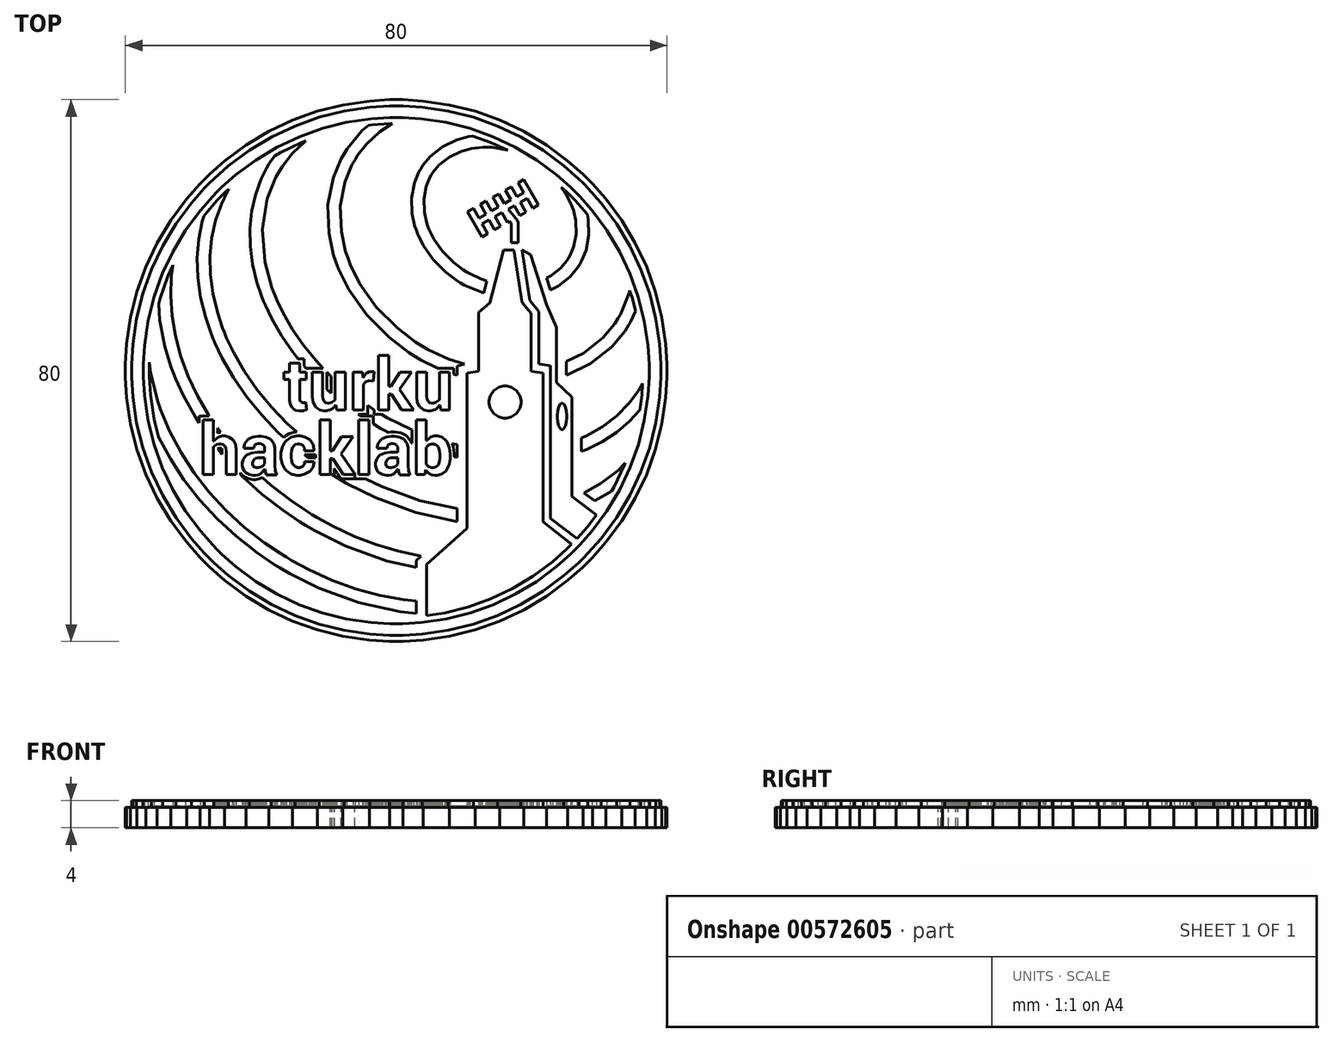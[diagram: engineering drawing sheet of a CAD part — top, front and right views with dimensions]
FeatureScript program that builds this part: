
annotation { "Feature Type Name" : "Feature", "Feature Type Description" : "" }
export const myFeature = defineFeature(function(context is Context, id is Id, definition is map)
    precondition{}
    {
        {
            var Q0;
            Q0=qCreatedBy(makeId("Top.planeOp"),FACE);
            var sketch = newSketch(context, id + "F0", { "sketchPlane" : qUnion([Q0])});
            skLineSegment(sketch, "E0", {"start": v(-12.45, -21.24) * mm, "end": v(-11.69, -21.7) * mm});
            skLineSegment(sketch, "E1", {"start": v(-11.69, -21.7) * mm, "end": v(-9.32, -22.98) * mm});
            skLineSegment(sketch, "E2", {"start": v(-9.32, -22.98) * mm, "end": v(-6.15, -24.46) * mm});
            skLineSegment(sketch, "E3", {"start": v(-6.15, -24.46) * mm, "end": v(-2.94, -25.69) * mm});
            skLineSegment(sketch, "E4", {"start": v(-2.94, -25.69) * mm, "end": v(0.28, -26.66) * mm});
            skLineSegment(sketch, "E5", {"start": v(0.28, -26.66) * mm, "end": v(3.5, -27.37) * mm});
            skLineSegment(sketch, "E6", {"start": v(3.5, -27.37) * mm, "end": v(6.7, -27.84) * mm});
            skLineSegment(sketch, "E7", {"start": v(6.7, -27.84) * mm, "end": v(9.84, -28.05) * mm});
            skLineSegment(sketch, "E8", {"start": v(9.84, -28.05) * mm, "end": v(12.93, -28.02) * mm});
            skLineSegment(sketch, "E9", {"start": v(12.93, -28.02) * mm, "end": v(15.94, -27.74) * mm});
            skLineSegment(sketch, "E10", {"start": v(15.94, -27.74) * mm, "end": v(18.85, -27.22) * mm});
            skLineSegment(sketch, "E11", {"start": v(18.85, -27.22) * mm, "end": v(21.64, -26.46) * mm});
            skLineSegment(sketch, "E12", {"start": v(21.64, -26.46) * mm, "end": v(24.3, -25.46) * mm});
            skLineSegment(sketch, "E13", {"start": v(24.3, -25.46) * mm, "end": v(26.8, -24.22) * mm});
            skLineSegment(sketch, "E14", {"start": v(26.8, -24.22) * mm, "end": v(29.13, -22.75) * mm});
            skLineSegment(sketch, "E15", {"start": v(29.13, -22.75) * mm, "end": v(31.27, -21.05) * mm});
            skLineSegment(sketch, "E16", {"start": v(31.27, -21.05) * mm, "end": v(32.74, -19.62) * mm});
            skLineSegment(sketch, "E17", {"start": v(32.74, -19.62) * mm, "end": v(33.2, -19.11) * mm});
            skLineSegment(sketch, "E18", {"start": v(33.2, -19.11) * mm, "end": v(33.4, -18.77) * mm});
            skLineSegment(sketch, "E19", {"start": v(33.4, -18.77) * mm, "end": v(35.17, -15.19) * mm});
            skLineSegment(sketch, "E20", {"start": v(35.17, -15.19) * mm, "end": v(35.32, -14.82) * mm});
            skLineSegment(sketch, "E21", {"start": v(35.32, -14.82) * mm, "end": v(34.55, -15.63) * mm});
            skLineSegment(sketch, "E22", {"start": v(34.55, -15.63) * mm, "end": v(31.91, -17.75) * mm});
            skLineSegment(sketch, "E23", {"start": v(31.91, -17.75) * mm, "end": v(27.89, -20.04) * mm});
            skLineSegment(sketch, "E24", {"start": v(27.89, -20.04) * mm, "end": v(23.32, -21.64) * mm});
            skLineSegment(sketch, "E25", {"start": v(23.32, -21.64) * mm, "end": v(19.53, -22.4) * mm});
            skLineSegment(sketch, "E26", {"start": v(19.53, -22.4) * mm, "end": v(18.25, -22.53) * mm});
            skLineSegment(sketch, "E27", {"start": v(18.25, -22.53) * mm, "end": v(17.96, -22.56) * mm});
            skLineSegment(sketch, "E28", {"start": v(17.96, -22.56) * mm, "end": v(15.49, -22.7) * mm});
            skLineSegment(sketch, "E29", {"start": v(15.49, -22.7) * mm, "end": v(14.67, -22.7) * mm});
            skLineSegment(sketch, "E30", {"start": v(14.67, -22.7) * mm, "end": v(13.2, -22.7) * mm});
            skLineSegment(sketch, "E31", {"start": v(13.2, -22.7) * mm, "end": v(8.78, -22.26) * mm});
            skLineSegment(sketch, "E32", {"start": v(8.78, -22.26) * mm, "end": v(2.85, -20.95) * mm});
            skLineSegment(sketch, "E33", {"start": v(2.85, -20.95) * mm, "end": v(-3, -18.8) * mm});
            skLineSegment(sketch, "E34", {"start": v(-3, -18.8) * mm, "end": v(-7.31, -16.66) * mm});
            skLineSegment(sketch, "E35", {"start": v(-7.31, -16.66) * mm, "end": v(-8.68, -15.84) * mm});
            skLineSegment(sketch, "E36", {"start": v(-8.68, -15.84) * mm, "end": v(-9.48, -15.36) * mm});
            skLineSegment(sketch, "E37", {"start": v(-9.48, -15.36) * mm, "end": v(-11.8, -13.8) * mm});
            skLineSegment(sketch, "E38", {"start": v(-11.8, -13.8) * mm, "end": v(-14.7, -11.57) * mm});
            skLineSegment(sketch, "E39", {"start": v(-14.7, -11.57) * mm, "end": v(-17.4, -9.16) * mm});
            skLineSegment(sketch, "E40", {"start": v(-17.4, -9.16) * mm, "end": v(-19.85, -6.6) * mm});
            skLineSegment(sketch, "E41", {"start": v(-19.85, -6.6) * mm, "end": v(-22.07, -3.9) * mm});
            skLineSegment(sketch, "E42", {"start": v(-22.07, -3.9) * mm, "end": v(-24.03, -1.07) * mm});
            skLineSegment(sketch, "E43", {"start": v(-24.03, -1.07) * mm, "end": v(-25.7, 1.88) * mm});
            skLineSegment(sketch, "E44", {"start": v(-25.7, 1.88) * mm, "end": v(-26.79, 4.14) * mm});
            skLineSegment(sketch, "E45", {"start": v(-26.79, 4.14) * mm, "end": v(-27.1, 4.9) * mm});
            skLineSegment(sketch, "E46", {"start": v(-27.1, 4.9) * mm, "end": v(-27.4, 5.64) * mm});
            skLineSegment(sketch, "E47", {"start": v(-27.4, 5.64) * mm, "end": v(-28.16, 7.9) * mm});
            skLineSegment(sketch, "E48", {"start": v(-28.16, 7.9) * mm, "end": v(-28.9, 10.84) * mm});
            skLineSegment(sketch, "E49", {"start": v(-28.9, 10.84) * mm, "end": v(-29.3, 13.75) * mm});
            skLineSegment(sketch, "E50", {"start": v(-29.3, 13.75) * mm, "end": v(-29.4, 16.6) * mm});
            skLineSegment(sketch, "E51", {"start": v(-29.4, 16.6) * mm, "end": v(-29.2, 19.38) * mm});
            skLineSegment(sketch, "E52", {"start": v(-29.2, 19.38) * mm, "end": v(-28.66, 22.06) * mm});
            skLineSegment(sketch, "E53", {"start": v(-28.66, 22.06) * mm, "end": v(-27.82, 24.64) * mm});
            skLineSegment(sketch, "E54", {"start": v(-27.82, 24.64) * mm, "end": v(-26.98, 26.5) * mm});
            skLineSegment(sketch, "E55", {"start": v(-26.98, 26.5) * mm, "end": v(-26.66, 27.1) * mm});
            skLineSegment(sketch, "E56", {"start": v(-26.66, 27.1) * mm, "end": v(-27.05, 26.72) * mm});
            skLineSegment(sketch, "E57", {"start": v(-27.05, 26.72) * mm, "end": v(-28.88, 24.72) * mm});
            skLineSegment(sketch, "E58", {"start": v(-28.88, 24.72) * mm, "end": v(-30.57, 22.6) * mm});
            skLineSegment(sketch, "E59", {"start": v(-30.57, 22.6) * mm, "end": v(-30.89, 22.16) * mm});
            skLineSegment(sketch, "E60", {"start": v(-30.89, 22.16) * mm, "end": v(-31.2, 21.52) * mm});
            skLineSegment(sketch, "E61", {"start": v(-31.2, 21.52) * mm, "end": v(-32, 19.5) * mm});
            skLineSegment(sketch, "E62", {"start": v(-32, 19.5) * mm, "end": v(-32.76, 16.75) * mm});
            skLineSegment(sketch, "E63", {"start": v(-32.76, 16.75) * mm, "end": v(-33.2, 13.9) * mm});
            skLineSegment(sketch, "E64", {"start": v(-33.2, 13.9) * mm, "end": v(-33.32, 11) * mm});
            skLineSegment(sketch, "E65", {"start": v(-33.32, 11) * mm, "end": v(-33.12, 8.06) * mm});
            skLineSegment(sketch, "E66", {"start": v(-33.12, 8.06) * mm, "end": v(-32.61, 5.1) * mm});
            skLineSegment(sketch, "E67", {"start": v(-32.61, 5.1) * mm, "end": v(-31.81, 2.14) * mm});
            skLineSegment(sketch, "E68", {"start": v(-31.81, 2.14) * mm, "end": v(-30.72, -0.8) * mm});
            skLineSegment(sketch, "E69", {"start": v(-30.72, -0.8) * mm, "end": v(-29.34, -3.71) * mm});
            skLineSegment(sketch, "E70", {"start": v(-29.34, -3.71) * mm, "end": v(-27.7, -6.56) * mm});
            skLineSegment(sketch, "E71", {"start": v(-27.7, -6.56) * mm, "end": v(-25.78, -9.32) * mm});
            skLineSegment(sketch, "E72", {"start": v(-25.78, -9.32) * mm, "end": v(-23.6, -11.99) * mm});
            skLineSegment(sketch, "E73", {"start": v(-23.6, -11.99) * mm, "end": v(-21.17, -14.53) * mm});
            skLineSegment(sketch, "E74", {"start": v(-21.17, -14.53) * mm, "end": v(-18.5, -16.93) * mm});
            skLineSegment(sketch, "E75", {"start": v(-18.5, -16.93) * mm, "end": v(-15.59, -19.18) * mm});
            skLineSegment(sketch, "E76", {"start": v(-15.59, -19.18) * mm, "end": v(-13.25, -20.75) * mm});
            skLineSegment(sketch, "E77", {"start": v(-13.25, -20.75) * mm, "end": v(-12.45, -21.24) * mm});
            skLineSegment(sketch, "E78", {"start": v(-24.6, 26.95) * mm, "end": v(-24.95, 26.39) * mm});
            skLineSegment(sketch, "E79", {"start": v(-24.95, 26.39) * mm, "end": v(-25.81, 24.62) * mm});
            skLineSegment(sketch, "E80", {"start": v(-25.81, 24.62) * mm, "end": v(-26.7, 22.17) * mm});
            skLineSegment(sketch, "E81", {"start": v(-26.7, 22.17) * mm, "end": v(-27.28, 19.6) * mm});
            skLineSegment(sketch, "E82", {"start": v(-27.28, 19.6) * mm, "end": v(-27.53, 16.93) * mm});
            skLineSegment(sketch, "E83", {"start": v(-27.53, 16.93) * mm, "end": v(-27.47, 14.18) * mm});
            skLineSegment(sketch, "E84", {"start": v(-27.47, 14.18) * mm, "end": v(-27.1, 11.37) * mm});
            skLineSegment(sketch, "E85", {"start": v(-27.1, 11.37) * mm, "end": v(-26.4, 8.51) * mm});
            skLineSegment(sketch, "E86", {"start": v(-26.4, 8.51) * mm, "end": v(-25.67, 6.33) * mm});
            skLineSegment(sketch, "E87", {"start": v(-25.67, 6.33) * mm, "end": v(-25.38, 5.62) * mm});
            skLineSegment(sketch, "E88", {"start": v(-25.38, 5.62) * mm, "end": v(-25.08, 4.88) * mm});
            skLineSegment(sketch, "E89", {"start": v(-25.08, 4.88) * mm, "end": v(-24.05, 2.72) * mm});
            skLineSegment(sketch, "E90", {"start": v(-24.05, 2.72) * mm, "end": v(-22.44, -0.1) * mm});
            skLineSegment(sketch, "E91", {"start": v(-22.44, -0.1) * mm, "end": v(-20.56, -2.8) * mm});
            skLineSegment(sketch, "E92", {"start": v(-20.56, -2.8) * mm, "end": v(-18.44, -5.39) * mm});
            skLineSegment(sketch, "E93", {"start": v(-18.44, -5.39) * mm, "end": v(-16.08, -7.85) * mm});
            skLineSegment(sketch, "E94", {"start": v(-16.08, -7.85) * mm, "end": v(-13.5, -10.15) * mm});
            skLineSegment(sketch, "E95", {"start": v(-13.5, -10.15) * mm, "end": v(-10.7, -12.3) * mm});
            skLineSegment(sketch, "E96", {"start": v(-10.7, -12.3) * mm, "end": v(-8.47, -13.79) * mm});
            skLineSegment(sketch, "E97", {"start": v(-8.47, -13.79) * mm, "end": v(-7.71, -14.25) * mm});
            skLineSegment(sketch, "E98", {"start": v(-7.71, -14.25) * mm, "end": v(-6.37, -15.06) * mm});
            skLineSegment(sketch, "E99", {"start": v(-6.37, -15.06) * mm, "end": v(-2.13, -17.15) * mm});
            skLineSegment(sketch, "E100", {"start": v(-2.13, -17.15) * mm, "end": v(3.55, -19.2) * mm});
            skLineSegment(sketch, "E101", {"start": v(3.55, -19.2) * mm, "end": v(9.2, -20.43) * mm});
            skLineSegment(sketch, "E102", {"start": v(9.2, -20.43) * mm, "end": v(13.35, -20.84) * mm});
            skLineSegment(sketch, "E103", {"start": v(13.35, -20.84) * mm, "end": v(14.73, -20.84) * mm});
            skLineSegment(sketch, "E104", {"start": v(14.73, -20.84) * mm, "end": v(15.6, -20.84) * mm});
            skLineSegment(sketch, "E105", {"start": v(15.6, -20.84) * mm, "end": v(18.19, -20.67) * mm});
            skLineSegment(sketch, "E106", {"start": v(18.19, -20.67) * mm, "end": v(21.5, -20.16) * mm});
            skLineSegment(sketch, "E107", {"start": v(21.5, -20.16) * mm, "end": v(24.66, -19.3) * mm});
            skLineSegment(sketch, "E108", {"start": v(24.66, -19.3) * mm, "end": v(27.6, -18.12) * mm});
            skLineSegment(sketch, "E109", {"start": v(27.6, -18.12) * mm, "end": v(30.3, -16.6) * mm});
            skLineSegment(sketch, "E110", {"start": v(30.3, -16.6) * mm, "end": v(32.72, -14.76) * mm});
            skLineSegment(sketch, "E111", {"start": v(32.72, -14.76) * mm, "end": v(34.84, -12.59) * mm});
            skLineSegment(sketch, "E112", {"start": v(34.84, -12.59) * mm, "end": v(36.23, -10.75) * mm});
            skLineSegment(sketch, "E113", {"start": v(36.23, -10.75) * mm, "end": v(36.63, -10.1) * mm});
            skLineSegment(sketch, "E114", {"start": v(36.63, -10.1) * mm, "end": v(36.68, -10.01) * mm});
            skLineSegment(sketch, "E115", {"start": v(36.68, -10.01) * mm, "end": v(37.17, -9.14) * mm});
            skLineSegment(sketch, "E116", {"start": v(37.17, -9.14) * mm, "end": v(37.21, -9.05) * mm});
            skLineSegment(sketch, "E117", {"start": v(37.21, -9.05) * mm, "end": v(37.34, -8.51) * mm});
            skLineSegment(sketch, "E118", {"start": v(37.34, -8.51) * mm, "end": v(37.85, -5.78) * mm});
            skLineSegment(sketch, "E119", {"start": v(37.85, -5.78) * mm, "end": v(38.16, -2.99) * mm});
            skLineSegment(sketch, "E120", {"start": v(38.16, -2.99) * mm, "end": v(38.2, -2.42) * mm});
            skLineSegment(sketch, "E121", {"start": v(38.2, -2.42) * mm, "end": v(38.15, -2.52) * mm});
            skLineSegment(sketch, "E122", {"start": v(38.15, -2.52) * mm, "end": v(37.6, -3.52) * mm});
            skLineSegment(sketch, "E123", {"start": v(37.6, -3.52) * mm, "end": v(37.54, -3.62) * mm});
            skLineSegment(sketch, "E124", {"start": v(37.54, -3.62) * mm, "end": v(37.22, -4.15) * mm});
            skLineSegment(sketch, "E125", {"start": v(37.22, -4.15) * mm, "end": v(36.11, -5.66) * mm});
            skLineSegment(sketch, "E126", {"start": v(36.11, -5.66) * mm, "end": v(34.44, -7.5) * mm});
            skLineSegment(sketch, "E127", {"start": v(34.44, -7.5) * mm, "end": v(32.55, -9.11) * mm});
            skLineSegment(sketch, "E128", {"start": v(32.55, -9.11) * mm, "end": v(30.43, -10.5) * mm});
            skLineSegment(sketch, "E129", {"start": v(30.43, -10.5) * mm, "end": v(28.11, -11.66) * mm});
            skLineSegment(sketch, "E130", {"start": v(28.11, -11.66) * mm, "end": v(25.6, -12.58) * mm});
            skLineSegment(sketch, "E131", {"start": v(25.6, -12.58) * mm, "end": v(22.92, -13.25) * mm});
            skLineSegment(sketch, "E132", {"start": v(22.92, -13.25) * mm, "end": v(20.78, -13.6) * mm});
            skLineSegment(sketch, "E133", {"start": v(20.78, -13.6) * mm, "end": v(20.07, -13.67) * mm});
            skLineSegment(sketch, "E134", {"start": v(20.07, -13.67) * mm, "end": v(19.81, -13.7) * mm});
            skLineSegment(sketch, "E135", {"start": v(19.81, -13.7) * mm, "end": v(17.65, -13.82) * mm});
            skLineSegment(sketch, "E136", {"start": v(17.65, -13.82) * mm, "end": v(16.93, -13.82) * mm});
            skLineSegment(sketch, "E137", {"start": v(16.93, -13.82) * mm, "end": v(15.64, -13.82) * mm});
            skLineSegment(sketch, "E138", {"start": v(15.64, -13.82) * mm, "end": v(11.78, -13.43) * mm});
            skLineSegment(sketch, "E139", {"start": v(11.78, -13.43) * mm, "end": v(6.6, -12.3) * mm});
            skLineSegment(sketch, "E140", {"start": v(6.6, -12.3) * mm, "end": v(1.47, -10.41) * mm});
            skLineSegment(sketch, "E141", {"start": v(1.47, -10.41) * mm, "end": v(-2.3, -8.54) * mm});
            skLineSegment(sketch, "E142", {"start": v(-2.3, -8.54) * mm, "end": v(-3.5, -7.82) * mm});
            skLineSegment(sketch, "E143", {"start": v(-3.5, -7.82) * mm, "end": v(-4.19, -7.4) * mm});
            skLineSegment(sketch, "E144", {"start": v(-4.19, -7.4) * mm, "end": v(-6.21, -6.03) * mm});
            skLineSegment(sketch, "E145", {"start": v(-6.21, -6.03) * mm, "end": v(-8.76, -4.08) * mm});
            skLineSegment(sketch, "E146", {"start": v(-8.76, -4.08) * mm, "end": v(-11.11, -1.98) * mm});
            skLineSegment(sketch, "E147", {"start": v(-11.11, -1.98) * mm, "end": v(-13.27, 0.26) * mm});
            skLineSegment(sketch, "E148", {"start": v(-13.27, 0.26) * mm, "end": v(-15.2, 2.63) * mm});
            skLineSegment(sketch, "E149", {"start": v(-15.2, 2.63) * mm, "end": v(-16.92, 5.1) * mm});
            skLineSegment(sketch, "E150", {"start": v(-16.92, 5.1) * mm, "end": v(-18.39, 7.67) * mm});
            skLineSegment(sketch, "E151", {"start": v(-18.39, 7.67) * mm, "end": v(-19.33, 9.65) * mm});
            skLineSegment(sketch, "E152", {"start": v(-19.33, 9.65) * mm, "end": v(-19.6, 10.33) * mm});
            skLineSegment(sketch, "E153", {"start": v(-19.6, 10.33) * mm, "end": v(-19.88, 11) * mm});
            skLineSegment(sketch, "E154", {"start": v(-19.88, 11) * mm, "end": v(-20.56, 13.04) * mm});
            skLineSegment(sketch, "E155", {"start": v(-20.56, 13.04) * mm, "end": v(-21.2, 15.74) * mm});
            skLineSegment(sketch, "E156", {"start": v(-21.2, 15.74) * mm, "end": v(-21.56, 18.38) * mm});
            skLineSegment(sketch, "E157", {"start": v(-21.56, 18.38) * mm, "end": v(-21.6, 20.98) * mm});
            skLineSegment(sketch, "E158", {"start": v(-21.6, 20.98) * mm, "end": v(-21.36, 23.5) * mm});
            skLineSegment(sketch, "E159", {"start": v(-21.36, 23.5) * mm, "end": v(-20.8, 25.93) * mm});
            skLineSegment(sketch, "E160", {"start": v(-20.8, 25.93) * mm, "end": v(-19.96, 28.26) * mm});
            skLineSegment(sketch, "E161", {"start": v(-19.96, 28.26) * mm, "end": v(-19.13, 29.94) * mm});
            skLineSegment(sketch, "E162", {"start": v(-19.13, 29.94) * mm, "end": v(-18.8, 30.47) * mm});
            skLineSegment(sketch, "E163", {"start": v(-18.8, 30.47) * mm, "end": v(-18.55, 30.9) * mm});
            skLineSegment(sketch, "E164", {"start": v(-18.55, 30.9) * mm, "end": v(-17.1, 32.85) * mm});
            skLineSegment(sketch, "E165", {"start": v(-17.1, 32.85) * mm, "end": v(-15.43, 34.61) * mm});
            skLineSegment(sketch, "E166", {"start": v(-15.43, 34.61) * mm, "end": v(-15.07, 34.94) * mm});
            skLineSegment(sketch, "E167", {"start": v(-15.07, 34.94) * mm, "end": v(-15.42, 34.78) * mm});
            skLineSegment(sketch, "E168", {"start": v(-15.42, 34.78) * mm, "end": v(-18.86, 33.04) * mm});
            skLineSegment(sketch, "E169", {"start": v(-18.86, 33.04) * mm, "end": v(-19.2, 32.84) * mm});
            skLineSegment(sketch, "E170", {"start": v(-19.2, 32.84) * mm, "end": v(-19.74, 32.44) * mm});
            skLineSegment(sketch, "E171", {"start": v(-19.74, 32.44) * mm, "end": v(-22.2, 30.16) * mm});
            skLineSegment(sketch, "E172", {"start": v(-22.2, 30.16) * mm, "end": v(-24.26, 27.53) * mm});
            skLineSegment(sketch, "E173", {"start": v(-24.26, 27.53) * mm, "end": v(-24.6, 26.95) * mm});
            skLineSegment(sketch, "E174", {"start": v(-6.06, 31.17) * mm, "end": v(-6.53, 30.4) * mm});
            skLineSegment(sketch, "E175", {"start": v(-6.53, 30.4) * mm, "end": v(-7.56, 27.86) * mm});
            skLineSegment(sketch, "E176", {"start": v(-7.56, 27.86) * mm, "end": v(-8.24, 24.29) * mm});
            skLineSegment(sketch, "E177", {"start": v(-8.24, 24.29) * mm, "end": v(-8.11, 20.53) * mm});
            skLineSegment(sketch, "E178", {"start": v(-8.11, 20.53) * mm, "end": v(-7.49, 17.6) * mm});
            skLineSegment(sketch, "E179", {"start": v(-7.49, 17.6) * mm, "end": v(-7.16, 16.67) * mm});
            skLineSegment(sketch, "E180", {"start": v(-7.16, 16.67) * mm, "end": v(-6.81, 15.69) * mm});
            skLineSegment(sketch, "E181", {"start": v(-6.81, 15.69) * mm, "end": v(-5.4, 12.87) * mm});
            skLineSegment(sketch, "E182", {"start": v(-5.4, 12.87) * mm, "end": v(-2.94, 9.39) * mm});
            skLineSegment(sketch, "E183", {"start": v(-2.94, 9.39) * mm, "end": v(0.15, 6.3) * mm});
            skLineSegment(sketch, "E184", {"start": v(0.15, 6.3) * mm, "end": v(2.84, 4.24) * mm});
            skLineSegment(sketch, "E185", {"start": v(2.84, 4.24) * mm, "end": v(3.8, 3.66) * mm});
            skLineSegment(sketch, "E186", {"start": v(3.8, 3.66) * mm, "end": v(4.76, 3.08) * mm});
            skLineSegment(sketch, "E187", {"start": v(4.76, 3.08) * mm, "end": v(7.82, 1.65) * mm});
            skLineSegment(sketch, "E188", {"start": v(7.82, 1.65) * mm, "end": v(12, 0.35) * mm});
            skLineSegment(sketch, "E189", {"start": v(12, 0.35) * mm, "end": v(16.23, -0.2) * mm});
            skLineSegment(sketch, "E190", {"start": v(16.23, -0.2) * mm, "end": v(19.38, -0.15) * mm});
            skLineSegment(sketch, "E191", {"start": v(19.38, -0.15) * mm, "end": v(20.4, 0) * mm});
            skLineSegment(sketch, "E192", {"start": v(20.4, 0) * mm, "end": v(21.39, 0.14) * mm});
            skLineSegment(sketch, "E193", {"start": v(21.39, 0.14) * mm, "end": v(24.27, 0.94) * mm});
            skLineSegment(sketch, "E194", {"start": v(24.27, 0.94) * mm, "end": v(27.66, 2.57) * mm});
            skLineSegment(sketch, "E195", {"start": v(27.66, 2.57) * mm, "end": v(30.51, 4.84) * mm});
            skLineSegment(sketch, "E196", {"start": v(30.51, 4.84) * mm, "end": v(32.28, 6.93) * mm});
            skLineSegment(sketch, "E197", {"start": v(32.28, 6.93) * mm, "end": v(32.75, 7.7) * mm});
            skLineSegment(sketch, "E198", {"start": v(32.75, 7.7) * mm, "end": v(33.11, 8.3) * mm});
            skLineSegment(sketch, "E199", {"start": v(33.11, 8.3) * mm, "end": v(34.38, 11.48) * mm});
            skLineSegment(sketch, "E200", {"start": v(34.38, 11.48) * mm, "end": v(34.95, 14.83) * mm});
            skLineSegment(sketch, "E201", {"start": v(34.95, 14.83) * mm, "end": v(34.97, 15.51) * mm});
            skLineSegment(sketch, "E202", {"start": v(34.97, 15.51) * mm, "end": v(34.58, 16.38) * mm});
            skLineSegment(sketch, "E203", {"start": v(34.58, 16.38) * mm, "end": v(33.25, 18.88) * mm});
            skLineSegment(sketch, "E204", {"start": v(33.25, 18.88) * mm, "end": v(31.22, 22.04) * mm});
            skLineSegment(sketch, "E205", {"start": v(31.22, 22.04) * mm, "end": v(28.9, 24.98) * mm});
            skLineSegment(sketch, "E206", {"start": v(28.9, 24.98) * mm, "end": v(27, 27.03) * mm});
            skLineSegment(sketch, "E207", {"start": v(27, 27.03) * mm, "end": v(26.32, 27.67) * mm});
            skLineSegment(sketch, "E208", {"start": v(26.32, 27.67) * mm, "end": v(26.47, 27.44) * mm});
            skLineSegment(sketch, "E209", {"start": v(26.47, 27.44) * mm, "end": v(27.15, 26.24) * mm});
            skLineSegment(sketch, "E210", {"start": v(27.15, 26.24) * mm, "end": v(27.7, 24.98) * mm});
            skLineSegment(sketch, "E211", {"start": v(27.7, 24.98) * mm, "end": v(27.8, 24.72) * mm});
            skLineSegment(sketch, "E212", {"start": v(27.8, 24.72) * mm, "end": v(28, 24.14) * mm});
            skLineSegment(sketch, "E213", {"start": v(28, 24.14) * mm, "end": v(28.39, 22.32) * mm});
            skLineSegment(sketch, "E214", {"start": v(28.39, 22.32) * mm, "end": v(28.46, 19.98) * mm});
            skLineSegment(sketch, "E215", {"start": v(28.46, 19.98) * mm, "end": v(28.03, 17.74) * mm});
            skLineSegment(sketch, "E216", {"start": v(28.03, 17.74) * mm, "end": v(27.38, 16.15) * mm});
            skLineSegment(sketch, "E217", {"start": v(27.38, 16.15) * mm, "end": v(27.09, 15.67) * mm});
            skLineSegment(sketch, "E218", {"start": v(27.09, 15.67) * mm, "end": v(26.8, 15.18) * mm});
            skLineSegment(sketch, "E219", {"start": v(26.8, 15.18) * mm, "end": v(25.68, 13.87) * mm});
            skLineSegment(sketch, "E220", {"start": v(25.68, 13.87) * mm, "end": v(23.9, 12.44) * mm});
            skLineSegment(sketch, "E221", {"start": v(23.9, 12.44) * mm, "end": v(21.8, 11.42) * mm});
            skLineSegment(sketch, "E222", {"start": v(21.8, 11.42) * mm, "end": v(20, 10.92) * mm});
            skLineSegment(sketch, "E223", {"start": v(20, 10.92) * mm, "end": v(19.4, 10.84) * mm});
            skLineSegment(sketch, "E224", {"start": v(19.4, 10.84) * mm, "end": v(19.23, 10.81) * mm});
            skLineSegment(sketch, "E225", {"start": v(19.23, 10.81) * mm, "end": v(17.9, 10.7) * mm});
            skLineSegment(sketch, "E226", {"start": v(17.9, 10.7) * mm, "end": v(17.47, 10.7) * mm});
            skLineSegment(sketch, "E227", {"start": v(17.47, 10.7) * mm, "end": v(16.45, 10.7) * mm});
            skLineSegment(sketch, "E228", {"start": v(16.45, 10.7) * mm, "end": v(13.4, 11.29) * mm});
            skLineSegment(sketch, "E229", {"start": v(13.4, 11.29) * mm, "end": v(10.1, 12.63) * mm});
            skLineSegment(sketch, "E230", {"start": v(10.1, 12.63) * mm, "end": v(9.47, 13) * mm});
            skLineSegment(sketch, "E231", {"start": v(9.47, 13) * mm, "end": v(8.9, 13.35) * mm});
            skLineSegment(sketch, "E232", {"start": v(8.9, 13.35) * mm, "end": v(7.3, 14.57) * mm});
            skLineSegment(sketch, "E233", {"start": v(7.3, 14.57) * mm, "end": v(5.46, 16.42) * mm});
            skLineSegment(sketch, "E234", {"start": v(5.46, 16.42) * mm, "end": v(4, 18.5) * mm});
            skLineSegment(sketch, "E235", {"start": v(4, 18.5) * mm, "end": v(3.15, 20.19) * mm});
            skLineSegment(sketch, "E236", {"start": v(3.15, 20.19) * mm, "end": v(2.94, 20.78) * mm});
            skLineSegment(sketch, "E237", {"start": v(2.94, 20.78) * mm, "end": v(2.73, 21.36) * mm});
            skLineSegment(sketch, "E238", {"start": v(2.73, 21.36) * mm, "end": v(2.35, 23.17) * mm});
            skLineSegment(sketch, "E239", {"start": v(2.35, 23.17) * mm, "end": v(2.27, 25.52) * mm});
            skLineSegment(sketch, "E240", {"start": v(2.27, 25.52) * mm, "end": v(2.7, 27.75) * mm});
            skLineSegment(sketch, "E241", {"start": v(2.7, 27.75) * mm, "end": v(3.36, 29.34) * mm});
            skLineSegment(sketch, "E242", {"start": v(3.36, 29.34) * mm, "end": v(3.65, 29.83) * mm});
            skLineSegment(sketch, "E243", {"start": v(3.65, 29.83) * mm, "end": v(3.94, 30.31) * mm});
            skLineSegment(sketch, "E244", {"start": v(3.94, 30.31) * mm, "end": v(5.05, 31.63) * mm});
            skLineSegment(sketch, "E245", {"start": v(5.05, 31.63) * mm, "end": v(6.83, 33.05) * mm});
            skLineSegment(sketch, "E246", {"start": v(6.83, 33.05) * mm, "end": v(8.94, 34.07) * mm});
            skLineSegment(sketch, "E247", {"start": v(8.94, 34.07) * mm, "end": v(10.73, 34.57) * mm});
            skLineSegment(sketch, "E248", {"start": v(10.73, 34.57) * mm, "end": v(11.34, 34.66) * mm});
            skLineSegment(sketch, "E249", {"start": v(11.34, 34.66) * mm, "end": v(11.75, 34.72) * mm});
            skLineSegment(sketch, "E250", {"start": v(11.75, 34.72) * mm, "end": v(13.82, 34.78) * mm});
            skLineSegment(sketch, "E251", {"start": v(13.82, 34.78) * mm, "end": v(15.9, 34.55) * mm});
            skLineSegment(sketch, "E252", {"start": v(15.9, 34.55) * mm, "end": v(16.31, 34.46) * mm});
            skLineSegment(sketch, "E253", {"start": v(16.31, 34.46) * mm, "end": v(15.53, 34.83) * mm});
            skLineSegment(sketch, "E254", {"start": v(15.53, 34.83) * mm, "end": v(13.1, 35.8) * mm});
            skLineSegment(sketch, "E255", {"start": v(13.1, 35.8) * mm, "end": v(9.73, 36.83) * mm});
            skLineSegment(sketch, "E256", {"start": v(9.73, 36.83) * mm, "end": v(6.25, 37.56) * mm});
            skLineSegment(sketch, "E257", {"start": v(6.25, 37.56) * mm, "end": v(3.55, 37.9) * mm});
            skLineSegment(sketch, "E258", {"start": v(3.55, 37.9) * mm, "end": v(2.65, 37.97) * mm});
            skLineSegment(sketch, "E259", {"start": v(2.65, 37.97) * mm, "end": v(1.96, 37.74) * mm});
            skLineSegment(sketch, "E260", {"start": v(1.96, 37.74) * mm, "end": v(-0.03, 36.82) * mm});
            skLineSegment(sketch, "E261", {"start": v(-0.03, 36.82) * mm, "end": v(-2.4, 35.3) * mm});
            skLineSegment(sketch, "E262", {"start": v(-2.4, 35.3) * mm, "end": v(-4.42, 33.4) * mm});
            skLineSegment(sketch, "E263", {"start": v(-4.42, 33.4) * mm, "end": v(-5.7, 31.76) * mm});
            skLineSegment(sketch, "E264", {"start": v(-5.7, 31.76) * mm, "end": v(-6.06, 31.17) * mm});
            skLineSegment(sketch, "E265", {"start": v(13.24, 32.97) * mm, "end": v(12.82, 32.97) * mm});
            skLineSegment(sketch, "E266", {"start": v(12.82, 32.97) * mm, "end": v(11.71, 32.86) * mm});
            skLineSegment(sketch, "E267", {"start": v(11.71, 32.86) * mm, "end": v(11.57, 32.84) * mm});
            skLineSegment(sketch, "E268", {"start": v(11.57, 32.84) * mm, "end": v(11.07, 32.77) * mm});
            skLineSegment(sketch, "E269", {"start": v(11.07, 32.77) * mm, "end": v(9.58, 32.36) * mm});
            skLineSegment(sketch, "E270", {"start": v(9.58, 32.36) * mm, "end": v(7.83, 31.52) * mm});
            skLineSegment(sketch, "E271", {"start": v(7.83, 31.52) * mm, "end": v(6.36, 30.35) * mm});
            skLineSegment(sketch, "E272", {"start": v(6.36, 30.35) * mm, "end": v(5.44, 29.28) * mm});
            skLineSegment(sketch, "E273", {"start": v(5.44, 29.28) * mm, "end": v(5.2, 28.89) * mm});
            skLineSegment(sketch, "E274", {"start": v(5.2, 28.89) * mm, "end": v(4.96, 28.5) * mm});
            skLineSegment(sketch, "E275", {"start": v(4.96, 28.5) * mm, "end": v(4.43, 27.19) * mm});
            skLineSegment(sketch, "E276", {"start": v(4.43, 27.19) * mm, "end": v(4.08, 25.34) * mm});
            skLineSegment(sketch, "E277", {"start": v(4.08, 25.34) * mm, "end": v(4.15, 23.4) * mm});
            skLineSegment(sketch, "E278", {"start": v(4.15, 23.4) * mm, "end": v(4.48, 21.9) * mm});
            skLineSegment(sketch, "E279", {"start": v(4.48, 21.9) * mm, "end": v(4.65, 21.4) * mm});
            skLineSegment(sketch, "E280", {"start": v(4.65, 21.4) * mm, "end": v(4.83, 20.9) * mm});
            skLineSegment(sketch, "E281", {"start": v(4.83, 20.9) * mm, "end": v(5.57, 19.42) * mm});
            skLineSegment(sketch, "E282", {"start": v(5.57, 19.42) * mm, "end": v(6.85, 17.6) * mm});
            skLineSegment(sketch, "E283", {"start": v(6.85, 17.6) * mm, "end": v(8.47, 15.97) * mm});
            skLineSegment(sketch, "E284", {"start": v(8.47, 15.97) * mm, "end": v(9.89, 14.9) * mm});
            skLineSegment(sketch, "E285", {"start": v(9.89, 14.9) * mm, "end": v(10.39, 14.6) * mm});
            skLineSegment(sketch, "E286", {"start": v(10.39, 14.6) * mm, "end": v(10.9, 14.29) * mm});
            skLineSegment(sketch, "E287", {"start": v(10.9, 14.29) * mm, "end": v(12.5, 13.53) * mm});
            skLineSegment(sketch, "E288", {"start": v(12.5, 13.53) * mm, "end": v(14.68, 12.85) * mm});
            skLineSegment(sketch, "E289", {"start": v(14.68, 12.85) * mm, "end": v(16.9, 12.56) * mm});
            skLineSegment(sketch, "E290", {"start": v(16.9, 12.56) * mm, "end": v(18.54, 12.59) * mm});
            skLineSegment(sketch, "E291", {"start": v(18.54, 12.59) * mm, "end": v(19.08, 12.67) * mm});
            skLineSegment(sketch, "E292", {"start": v(19.08, 12.67) * mm, "end": v(19.59, 12.74) * mm});
            skLineSegment(sketch, "E293", {"start": v(19.59, 12.74) * mm, "end": v(21.08, 13.15) * mm});
            skLineSegment(sketch, "E294", {"start": v(21.08, 13.15) * mm, "end": v(22.83, 14) * mm});
            skLineSegment(sketch, "E295", {"start": v(22.83, 14) * mm, "end": v(24.3, 15.16) * mm});
            skLineSegment(sketch, "E296", {"start": v(24.3, 15.16) * mm, "end": v(25.21, 16.23) * mm});
            skLineSegment(sketch, "E297", {"start": v(25.21, 16.23) * mm, "end": v(25.46, 16.62) * mm});
            skLineSegment(sketch, "E298", {"start": v(25.46, 16.62) * mm, "end": v(25.7, 17.02) * mm});
            skLineSegment(sketch, "E299", {"start": v(25.7, 17.02) * mm, "end": v(26.23, 18.32) * mm});
            skLineSegment(sketch, "E300", {"start": v(26.23, 18.32) * mm, "end": v(26.57, 20.17) * mm});
            skLineSegment(sketch, "E301", {"start": v(26.57, 20.17) * mm, "end": v(26.5, 22.1) * mm});
            skLineSegment(sketch, "E302", {"start": v(26.5, 22.1) * mm, "end": v(26.18, 23.62) * mm});
            skLineSegment(sketch, "E303", {"start": v(26.18, 23.62) * mm, "end": v(26, 24.1) * mm});
            skLineSegment(sketch, "E304", {"start": v(26, 24.1) * mm, "end": v(25.83, 24.62) * mm});
            skLineSegment(sketch, "E305", {"start": v(25.83, 24.62) * mm, "end": v(25.09, 26.09) * mm});
            skLineSegment(sketch, "E306", {"start": v(25.09, 26.09) * mm, "end": v(23.8, 27.91) * mm});
            skLineSegment(sketch, "E307", {"start": v(23.8, 27.91) * mm, "end": v(22.18, 29.54) * mm});
            skLineSegment(sketch, "E308", {"start": v(22.18, 29.54) * mm, "end": v(20.77, 30.61) * mm});
            skLineSegment(sketch, "E309", {"start": v(20.77, 30.61) * mm, "end": v(20.27, 30.92) * mm});
            skLineSegment(sketch, "E310", {"start": v(20.27, 30.92) * mm, "end": v(19.71, 31.25) * mm});
            skLineSegment(sketch, "E311", {"start": v(19.71, 31.25) * mm, "end": v(16.81, 32.45) * mm});
            skLineSegment(sketch, "E312", {"start": v(16.81, 32.45) * mm, "end": v(14.13, 32.97) * mm});
            skLineSegment(sketch, "E313", {"start": v(14.13, 32.97) * mm, "end": v(13.24, 32.97) * mm});
            skLineSegment(sketch, "E314", {"start": v(19.65, 18.9) * mm, "end": v(14.93, 18.9) * mm});
            skLineSegment(sketch, "E315", {"start": v(14.93, 18.9) * mm, "end": v(12.68, 10.53) * mm});
            skLineSegment(sketch, "E316", {"start": v(12.68, 10.53) * mm, "end": v(11.03, 9.19) * mm});
            skLineSegment(sketch, "E317", {"start": v(11.03, 9.19) * mm, "end": v(11.03, 1.19) * mm});
            skLineSegment(sketch, "E318", {"start": v(11.03, 1.19) * mm, "end": v(8.99, 0.68) * mm});
            skLineSegment(sketch, "E319", {"start": v(8.99, 0.68) * mm, "end": v(8.99, -22.52) * mm});
            skLineSegment(sketch, "E320", {"start": v(8.99, -22.52) * mm, "end": v(2.94, -28.06) * mm});
            skLineSegment(sketch, "E321", {"start": v(2.94, -28.06) * mm, "end": v(2.94, -37.83) * mm});
            skLineSegment(sketch, "E322", {"start": v(2.94, -37.83) * mm, "end": v(11.7, -36.24) * mm});
            skLineSegment(sketch, "E323", {"start": v(11.7, -36.24) * mm, "end": v(20.02, -32.58) * mm});
            skLineSegment(sketch, "E324", {"start": v(20.02, -32.58) * mm, "end": v(26.36, -27.69) * mm});
            skLineSegment(sketch, "E325", {"start": v(26.36, -27.69) * mm, "end": v(31.9, -21.07) * mm});
            skLineSegment(sketch, "E326", {"start": v(31.9, -21.07) * mm, "end": v(27.35, -17.8) * mm});
            skLineSegment(sketch, "E327", {"start": v(27.35, -17.8) * mm, "end": v(27.35, -3.02) * mm});
            skLineSegment(sketch, "E328", {"start": v(27.35, -3.02) * mm, "end": v(25.1, -0.55) * mm});
            skLineSegment(sketch, "E329", {"start": v(25.1, -0.55) * mm, "end": v(25.1, 6.11) * mm});
            skLineSegment(sketch, "E330", {"start": v(25.1, 6.11) * mm, "end": v(23.35, 10.22) * mm});
            skLineSegment(sketch, "E331", {"start": v(23.35, 10.22) * mm, "end": v(20.58, 18.9) * mm});
            skLineSegment(sketch, "E332", {"start": v(20.58, 18.9) * mm, "end": v(19.65, 18.9) * mm});
            skLineSegment(sketch, "E333", {"start": v(18.86, 28.2) * mm, "end": v(18, 27.71) * mm});
            skLineSegment(sketch, "E334", {"start": v(18, 27.71) * mm, "end": v(18.82, 26.27) * mm});
            skLineSegment(sketch, "E335", {"start": v(18.82, 26.27) * mm, "end": v(17.82, 25.7) * mm});
            skLineSegment(sketch, "E336", {"start": v(17.82, 25.7) * mm, "end": v(17, 27.14) * mm});
            skLineSegment(sketch, "E337", {"start": v(17, 27.14) * mm, "end": v(16.14, 26.65) * mm});
            skLineSegment(sketch, "E338", {"start": v(16.14, 26.65) * mm, "end": v(16.96, 25.2) * mm});
            skLineSegment(sketch, "E339", {"start": v(16.96, 25.2) * mm, "end": v(15.96, 24.64) * mm});
            skLineSegment(sketch, "E340", {"start": v(15.96, 24.64) * mm, "end": v(15.13, 26.08) * mm});
            skLineSegment(sketch, "E341", {"start": v(15.13, 26.08) * mm, "end": v(14.27, 25.59) * mm});
            skLineSegment(sketch, "E342", {"start": v(14.27, 25.59) * mm, "end": v(15.1, 24.14) * mm});
            skLineSegment(sketch, "E343", {"start": v(15.1, 24.14) * mm, "end": v(14.1, 23.57) * mm});
            skLineSegment(sketch, "E344", {"start": v(14.1, 23.57) * mm, "end": v(13.27, 25.02) * mm});
            skLineSegment(sketch, "E345", {"start": v(13.27, 25.02) * mm, "end": v(12.41, 24.52) * mm});
            skLineSegment(sketch, "E346", {"start": v(12.41, 24.52) * mm, "end": v(13.23, 23.08) * mm});
            skLineSegment(sketch, "E347", {"start": v(13.23, 23.08) * mm, "end": v(12.23, 22.51) * mm});
            skLineSegment(sketch, "E348", {"start": v(12.23, 22.51) * mm, "end": v(11.4, 23.95) * mm});
            skLineSegment(sketch, "E349", {"start": v(11.4, 23.95) * mm, "end": v(10.55, 23.46) * mm});
            skLineSegment(sketch, "E350", {"start": v(10.55, 23.46) * mm, "end": v(12.67, 19.74) * mm});
            skLineSegment(sketch, "E351", {"start": v(12.67, 19.74) * mm, "end": v(13.53, 20.23) * mm});
            skLineSegment(sketch, "E352", {"start": v(13.53, 20.23) * mm, "end": v(12.71, 21.67) * mm});
            skLineSegment(sketch, "E353", {"start": v(12.71, 21.67) * mm, "end": v(13.71, 22.24) * mm});
            skLineSegment(sketch, "E354", {"start": v(13.71, 22.24) * mm, "end": v(14.54, 20.8) * mm});
            skLineSegment(sketch, "E355", {"start": v(14.54, 20.8) * mm, "end": v(15.4, 21.3) * mm});
            skLineSegment(sketch, "E356", {"start": v(15.4, 21.3) * mm, "end": v(14.57, 22.73) * mm});
            skLineSegment(sketch, "E357", {"start": v(14.57, 22.73) * mm, "end": v(15.57, 23.3) * mm});
            skLineSegment(sketch, "E358", {"start": v(15.57, 23.3) * mm, "end": v(16.4, 21.86) * mm});
            skLineSegment(sketch, "E359", {"start": v(16.4, 21.86) * mm, "end": v(16.72, 22.05) * mm});
            skLineSegment(sketch, "E360", {"start": v(16.72, 22.05) * mm, "end": v(17, 21.71) * mm});
            skLineSegment(sketch, "E361", {"start": v(17, 21.71) * mm, "end": v(17.02, 18.88) * mm});
            skLineSegment(sketch, "E362", {"start": v(17.02, 18.88) * mm, "end": v(18, 18.89) * mm});
            skLineSegment(sketch, "E363", {"start": v(18, 18.89) * mm, "end": v(18, 21.88) * mm});
            skLineSegment(sketch, "E364", {"start": v(18, 21.88) * mm, "end": v(17.98, 22.06) * mm});
            skLineSegment(sketch, "E365", {"start": v(17.98, 22.06) * mm, "end": v(17.88, 22.18) * mm});
            skLineSegment(sketch, "E366", {"start": v(17.88, 22.18) * mm, "end": v(16.54, 23.83) * mm});
            skLineSegment(sketch, "E367", {"start": v(16.54, 23.83) * mm, "end": v(17.47, 24.36) * mm});
            skLineSegment(sketch, "E368", {"start": v(17.47, 24.36) * mm, "end": v(18.3, 22.91) * mm});
            skLineSegment(sketch, "E369", {"start": v(18.3, 22.91) * mm, "end": v(19.16, 23.4) * mm});
            skLineSegment(sketch, "E370", {"start": v(19.16, 23.4) * mm, "end": v(18.34, 24.85) * mm});
            skLineSegment(sketch, "E371", {"start": v(18.34, 24.85) * mm, "end": v(19.34, 25.42) * mm});
            skLineSegment(sketch, "E372", {"start": v(19.34, 25.42) * mm, "end": v(20.16, 23.98) * mm});
            skLineSegment(sketch, "E373", {"start": v(20.16, 23.98) * mm, "end": v(21.02, 24.47) * mm});
            skLineSegment(sketch, "E374", {"start": v(21.02, 24.47) * mm, "end": v(18.86, 28.2) * mm});
            skLineSegment(sketch, "E375", {"start": v(15.86, 17.8) * mm, "end": v(13.86, 9.99) * mm});
            skLineSegment(sketch, "E376", {"start": v(13.86, 9.99) * mm, "end": v(12.18, 8.59) * mm});
            skLineSegment(sketch, "E377", {"start": v(12.18, 8.59) * mm, "end": v(12.18, -0.1) * mm});
            skLineSegment(sketch, "E378", {"start": v(12.18, -0.1) * mm, "end": v(10.44, -0.35) * mm});
            skLineSegment(sketch, "E379", {"start": v(10.44, -0.35) * mm, "end": v(10.44, -23.25) * mm});
            skLineSegment(sketch, "E380", {"start": v(10.44, -23.25) * mm, "end": v(4.5, -28.6) * mm});
            skLineSegment(sketch, "E381", {"start": v(4.5, -28.6) * mm, "end": v(4.5, -38.12) * mm});
            skLineSegment(sketch, "E382", {"start": v(4.5, -38.12) * mm, "end": v(18.58, -34.43) * mm});
            skLineSegment(sketch, "E383", {"start": v(18.58, -34.43) * mm, "end": v(28.17, -27.46) * mm});
            skLineSegment(sketch, "E384", {"start": v(28.17, -27.46) * mm, "end": v(21.67, -22.31) * mm});
            skLineSegment(sketch, "E385", {"start": v(21.67, -22.31) * mm, "end": v(21.67, -0.35) * mm});
            skLineSegment(sketch, "E386", {"start": v(21.67, -0.35) * mm, "end": v(19.95, -0.1) * mm});
            skLineSegment(sketch, "E387", {"start": v(19.95, -0.1) * mm, "end": v(19.95, 8.47) * mm});
            skLineSegment(sketch, "E388", {"start": v(19.95, 8.47) * mm, "end": v(18.61, 10.07) * mm});
            skLineSegment(sketch, "E389", {"start": v(18.61, 10.07) * mm, "end": v(17.41, 17.8) * mm});
            skLineSegment(sketch, "E390", {"start": v(17.41, 17.8) * mm, "end": v(15.86, 17.8) * mm});
            skLineSegment(sketch, "E391", {"start": v(16.09, -2.26) * mm, "end": v(16.32, -2.26) * mm});
            skLineSegment(sketch, "E392", {"start": v(16.32, -2.26) * mm, "end": v(17.01, -2.45) * mm});
            skLineSegment(sketch, "E393", {"start": v(17.01, -2.45) * mm, "end": v(17.76, -2.96) * mm});
            skLineSegment(sketch, "E394", {"start": v(17.76, -2.96) * mm, "end": v(18.27, -3.7) * mm});
            skLineSegment(sketch, "E395", {"start": v(18.27, -3.7) * mm, "end": v(18.46, -4.4) * mm});
            skLineSegment(sketch, "E396", {"start": v(18.46, -4.4) * mm, "end": v(18.46, -4.63) * mm});
            skLineSegment(sketch, "E397", {"start": v(18.46, -4.63) * mm, "end": v(18.46, -4.86) * mm});
            skLineSegment(sketch, "E398", {"start": v(18.46, -4.86) * mm, "end": v(18.27, -5.55) * mm});
            skLineSegment(sketch, "E399", {"start": v(18.27, -5.55) * mm, "end": v(17.76, -6.3) * mm});
            skLineSegment(sketch, "E400", {"start": v(17.76, -6.3) * mm, "end": v(17.01, -6.81) * mm});
            skLineSegment(sketch, "E401", {"start": v(17.01, -6.81) * mm, "end": v(16.32, -7) * mm});
            skLineSegment(sketch, "E402", {"start": v(16.32, -7) * mm, "end": v(16.09, -7) * mm});
            skLineSegment(sketch, "E403", {"start": v(16.09, -7) * mm, "end": v(15.86, -7) * mm});
            skLineSegment(sketch, "E404", {"start": v(15.86, -7) * mm, "end": v(15.17, -6.81) * mm});
            skLineSegment(sketch, "E405", {"start": v(15.17, -6.81) * mm, "end": v(14.41, -6.3) * mm});
            skLineSegment(sketch, "E406", {"start": v(14.41, -6.3) * mm, "end": v(13.9, -5.55) * mm});
            skLineSegment(sketch, "E407", {"start": v(13.9, -5.55) * mm, "end": v(13.72, -4.86) * mm});
            skLineSegment(sketch, "E408", {"start": v(13.72, -4.86) * mm, "end": v(13.72, -4.63) * mm});
            skLineSegment(sketch, "E409", {"start": v(13.72, -4.63) * mm, "end": v(13.72, -4.4) * mm});
            skLineSegment(sketch, "E410", {"start": v(13.72, -4.4) * mm, "end": v(13.9, -3.7) * mm});
            skLineSegment(sketch, "E411", {"start": v(13.9, -3.7) * mm, "end": v(14.41, -2.96) * mm});
            skLineSegment(sketch, "E412", {"start": v(14.41, -2.96) * mm, "end": v(15.17, -2.45) * mm});
            skLineSegment(sketch, "E413", {"start": v(15.17, -2.45) * mm, "end": v(15.86, -2.26) * mm});
            skLineSegment(sketch, "E414", {"start": v(15.86, -2.26) * mm, "end": v(16.09, -2.26) * mm});
            skLineSegment(sketch, "E415", {"start": v(32, -23.12) * mm, "end": v(25.95, -18.6) * mm});
            skLineSegment(sketch, "E416", {"start": v(25.95, -18.6) * mm, "end": v(25.95, -3.9) * mm});
            skLineSegment(sketch, "E417", {"start": v(25.95, -3.9) * mm, "end": v(23.68, -1.75) * mm});
            skLineSegment(sketch, "E418", {"start": v(23.68, -1.75) * mm, "end": v(23.68, 6.39) * mm});
            skLineSegment(sketch, "E419", {"start": v(23.68, 6.39) * mm, "end": v(22.2, 9.71) * mm});
            skLineSegment(sketch, "E420", {"start": v(22.2, 9.71) * mm, "end": v(19.83, 17.1) * mm});
            skLineSegment(sketch, "E421", {"start": v(19.83, 17.1) * mm, "end": v(18.57, 17.8) * mm});
            skLineSegment(sketch, "E422", {"start": v(18.57, 17.8) * mm, "end": v(19.75, 10.34) * mm});
            skLineSegment(sketch, "E423", {"start": v(19.75, 10.34) * mm, "end": v(21.08, 8.7) * mm});
            skLineSegment(sketch, "E424", {"start": v(21.08, 8.7) * mm, "end": v(21.06, 0.97) * mm});
            skLineSegment(sketch, "E425", {"start": v(21.06, 0.97) * mm, "end": v(22.8, 0.7) * mm});
            skLineSegment(sketch, "E426", {"start": v(22.8, 0.7) * mm, "end": v(22.8, -21.8) * mm});
            skLineSegment(sketch, "E427", {"start": v(22.8, -21.8) * mm, "end": v(29.02, -26.6) * mm});
            skLineSegment(sketch, "E428", {"start": v(24.5, -4.79) * mm, "end": v(24.56, -4.79) * mm});
            skLineSegment(sketch, "E429", {"start": v(24.56, -4.79) * mm, "end": v(24.77, -4.94) * mm});
            skLineSegment(sketch, "E430", {"start": v(24.77, -4.94) * mm, "end": v(24.99, -5.36) * mm});
            skLineSegment(sketch, "E431", {"start": v(24.99, -5.36) * mm, "end": v(25.13, -5.99) * mm});
            skLineSegment(sketch, "E432", {"start": v(25.13, -5.99) * mm, "end": v(25.18, -6.56) * mm});
            skLineSegment(sketch, "E433", {"start": v(25.18, -6.56) * mm, "end": v(25.18, -6.75) * mm});
            skLineSegment(sketch, "E434", {"start": v(25.18, -6.75) * mm, "end": v(25.18, -6.95) * mm});
            skLineSegment(sketch, "E435", {"start": v(25.18, -6.95) * mm, "end": v(25.13, -7.52) * mm});
            skLineSegment(sketch, "E436", {"start": v(25.13, -7.52) * mm, "end": v(24.98, -8.15) * mm});
            skLineSegment(sketch, "E437", {"start": v(24.98, -8.15) * mm, "end": v(24.76, -8.57) * mm});
            skLineSegment(sketch, "E438", {"start": v(24.76, -8.57) * mm, "end": v(24.56, -8.73) * mm});
            skLineSegment(sketch, "E439", {"start": v(24.56, -8.73) * mm, "end": v(24.5, -8.73) * mm});
            skLineSegment(sketch, "E440", {"start": v(24.5, -8.73) * mm, "end": v(24.42, -8.73) * mm});
            skLineSegment(sketch, "E441", {"start": v(24.42, -8.73) * mm, "end": v(24.22, -8.57) * mm});
            skLineSegment(sketch, "E442", {"start": v(24.22, -8.57) * mm, "end": v(24, -8.15) * mm});
            skLineSegment(sketch, "E443", {"start": v(24, -8.15) * mm, "end": v(23.85, -7.52) * mm});
            skLineSegment(sketch, "E444", {"start": v(23.85, -7.52) * mm, "end": v(23.8, -6.95) * mm});
            skLineSegment(sketch, "E445", {"start": v(23.8, -6.95) * mm, "end": v(23.8, -6.75) * mm});
            skLineSegment(sketch, "E446", {"start": v(23.8, -6.75) * mm, "end": v(23.8, -6.56) * mm});
            skLineSegment(sketch, "E447", {"start": v(23.8, -6.56) * mm, "end": v(23.85, -6) * mm});
            skLineSegment(sketch, "E448", {"start": v(23.85, -6) * mm, "end": v(24, -5.37) * mm});
            skLineSegment(sketch, "E449", {"start": v(24, -5.37) * mm, "end": v(24.22, -4.94) * mm});
            skLineSegment(sketch, "E450", {"start": v(24.22, -4.94) * mm, "end": v(24.42, -4.79) * mm});
            skLineSegment(sketch, "E451", {"start": v(24.42, -4.79) * mm, "end": v(24.5, -4.79) * mm});
            skLineSegment(sketch, "E452", {"start": v(-26.96, -10.47) * mm, "end": v(-26.92, -10.4) * mm});
            skLineSegment(sketch, "E453", {"start": v(-26.92, -10.4) * mm, "end": v(-26.38, -9.9) * mm});
            skLineSegment(sketch, "E454", {"start": v(-26.38, -9.9) * mm, "end": v(-26.32, -9.87) * mm});
            skLineSegment(sketch, "E455", {"start": v(-26.32, -9.87) * mm, "end": v(-26.25, -9.83) * mm});
            skLineSegment(sketch, "E456", {"start": v(-26.25, -9.83) * mm, "end": v(-25.67, -9.65) * mm});
            skLineSegment(sketch, "E457", {"start": v(-25.67, -9.65) * mm, "end": v(-25.47, -9.65) * mm});
            skLineSegment(sketch, "E458", {"start": v(-25.47, -9.65) * mm, "end": v(-25.28, -9.65) * mm});
            skLineSegment(sketch, "E459", {"start": v(-25.28, -9.65) * mm, "end": v(-24.69, -9.8) * mm});
            skLineSegment(sketch, "E460", {"start": v(-24.69, -9.8) * mm, "end": v(-24.18, -10.14) * mm});
            skLineSegment(sketch, "E461", {"start": v(-24.18, -10.14) * mm, "end": v(-24.1, -10.23) * mm});
            skLineSegment(sketch, "E462", {"start": v(-24.1, -10.23) * mm, "end": v(-24.02, -10.33) * mm});
            skLineSegment(sketch, "E463", {"start": v(-24.02, -10.33) * mm, "end": v(-23.73, -10.97) * mm});
            skLineSegment(sketch, "E464", {"start": v(-23.73, -10.97) * mm, "end": v(-23.6, -11.77) * mm});
            skLineSegment(sketch, "E465", {"start": v(-23.6, -11.77) * mm, "end": v(-23.6, -12.03) * mm});
            skLineSegment(sketch, "E466", {"start": v(-23.6, -12.03) * mm, "end": v(-23.6, -15.36) * mm});
            skLineSegment(sketch, "E467", {"start": v(-23.6, -15.36) * mm, "end": v(-25.12, -15.36) * mm});
            skLineSegment(sketch, "E468", {"start": v(-25.12, -15.36) * mm, "end": v(-25.12, -12.02) * mm});
            skLineSegment(sketch, "E469", {"start": v(-25.12, -12.02) * mm, "end": v(-25.12, -11.88) * mm});
            skLineSegment(sketch, "E470", {"start": v(-25.12, -11.88) * mm, "end": v(-25.18, -11.47) * mm});
            skLineSegment(sketch, "E471", {"start": v(-25.18, -11.47) * mm, "end": v(-25.31, -11.14) * mm});
            skLineSegment(sketch, "E472", {"start": v(-25.31, -11.14) * mm, "end": v(-25.35, -11.1) * mm});
            skLineSegment(sketch, "E473", {"start": v(-25.35, -11.1) * mm, "end": v(-25.39, -11.05) * mm});
            skLineSegment(sketch, "E474", {"start": v(-25.39, -11.05) * mm, "end": v(-25.64, -10.89) * mm});
            skLineSegment(sketch, "E475", {"start": v(-25.64, -10.89) * mm, "end": v(-25.94, -10.82) * mm});
            skLineSegment(sketch, "E476", {"start": v(-25.94, -10.82) * mm, "end": v(-26.04, -10.82) * mm});
            skLineSegment(sketch, "E477", {"start": v(-26.04, -10.82) * mm, "end": v(-26.18, -10.82) * mm});
            skLineSegment(sketch, "E478", {"start": v(-26.18, -10.82) * mm, "end": v(-26.55, -10.9) * mm});
            skLineSegment(sketch, "E479", {"start": v(-26.55, -10.9) * mm, "end": v(-26.6, -10.93) * mm});
            skLineSegment(sketch, "E480", {"start": v(-26.6, -10.93) * mm, "end": v(-26.63, -10.95) * mm});
            skLineSegment(sketch, "E481", {"start": v(-26.63, -10.95) * mm, "end": v(-26.97, -11.2) * mm});
            skLineSegment(sketch, "E482", {"start": v(-26.97, -11.2) * mm, "end": v(-27, -11.24) * mm});
            skLineSegment(sketch, "E483", {"start": v(-27, -11.24) * mm, "end": v(-27, -15.34) * mm});
            skLineSegment(sketch, "E484", {"start": v(-27, -15.34) * mm, "end": v(-28.5, -15.34) * mm});
            skLineSegment(sketch, "E485", {"start": v(-28.5, -15.34) * mm, "end": v(-28.5, -7.28) * mm});
            skLineSegment(sketch, "E486", {"start": v(-28.5, -7.28) * mm, "end": v(-27, -7.28) * mm});
            skLineSegment(sketch, "E487", {"start": v(-27, -7.28) * mm, "end": v(-27, -10.47) * mm});
            skLineSegment(sketch, "E488", {"start": v(-27, -10.47) * mm, "end": v(-26.96, -10.47) * mm});
            skLineSegment(sketch, "E489", {"start": v(-22.98, -15.97) * mm, "end": v(-25.72, -15.97) * mm});
            skLineSegment(sketch, "E490", {"start": v(-25.72, -15.97) * mm, "end": v(-25.72, -12.02) * mm});
            skLineSegment(sketch, "E491", {"start": v(-25.72, -12.02) * mm, "end": v(-25.72, -11.91) * mm});
            skLineSegment(sketch, "E492", {"start": v(-25.72, -11.91) * mm, "end": v(-25.76, -11.6) * mm});
            skLineSegment(sketch, "E493", {"start": v(-25.76, -11.6) * mm, "end": v(-25.8, -11.5) * mm});
            skLineSegment(sketch, "E494", {"start": v(-25.8, -11.5) * mm, "end": v(-25.81, -11.5) * mm});
            skLineSegment(sketch, "E495", {"start": v(-25.81, -11.5) * mm, "end": v(-25.82, -11.48) * mm});
            skLineSegment(sketch, "E496", {"start": v(-25.82, -11.48) * mm, "end": v(-25.97, -11.45) * mm});
            skLineSegment(sketch, "E497", {"start": v(-25.97, -11.45) * mm, "end": v(-26.03, -11.45) * mm});
            skLineSegment(sketch, "E498", {"start": v(-26.03, -11.45) * mm, "end": v(-26.1, -11.45) * mm});
            skLineSegment(sketch, "E499", {"start": v(-26.1, -11.45) * mm, "end": v(-26.3, -11.49) * mm});
            skLineSegment(sketch, "E500", {"start": v(-26.3, -11.49) * mm, "end": v(-26.32, -11.5) * mm});
            skLineSegment(sketch, "E501", {"start": v(-26.32, -11.5) * mm, "end": v(-26.33, -11.5) * mm});
            skLineSegment(sketch, "E502", {"start": v(-26.33, -11.5) * mm, "end": v(-26.36, -11.51) * mm});
            skLineSegment(sketch, "E503", {"start": v(-26.36, -11.51) * mm, "end": v(-26.36, -11.51) * mm});
            skLineSegment(sketch, "E504", {"start": v(-26.36, -11.51) * mm, "end": v(-26.36, -15.97) * mm});
            skLineSegment(sketch, "E505", {"start": v(-26.36, -15.97) * mm, "end": v(-29.1, -15.97) * mm});
            skLineSegment(sketch, "E506", {"start": v(-29.1, -15.97) * mm, "end": v(-29.1, -6.68) * mm});
            skLineSegment(sketch, "E507", {"start": v(-29.1, -6.68) * mm, "end": v(-26.36, -6.68) * mm});
            skLineSegment(sketch, "E508", {"start": v(-26.36, -6.68) * mm, "end": v(-26.36, -9.22) * mm});
            skLineSegment(sketch, "E509", {"start": v(-26.36, -9.22) * mm, "end": v(-26.3, -9.2) * mm});
            skLineSegment(sketch, "E510", {"start": v(-26.3, -9.2) * mm, "end": v(-25.69, -9.05) * mm});
            skLineSegment(sketch, "E511", {"start": v(-25.69, -9.05) * mm, "end": v(-25.49, -9.05) * mm});
            skLineSegment(sketch, "E512", {"start": v(-25.49, -9.05) * mm, "end": v(-25.23, -9.05) * mm});
            skLineSegment(sketch, "E513", {"start": v(-25.23, -9.05) * mm, "end": v(-24.45, -9.25) * mm});
            skLineSegment(sketch, "E514", {"start": v(-24.45, -9.25) * mm, "end": v(-23.76, -9.72) * mm});
            skLineSegment(sketch, "E515", {"start": v(-23.76, -9.72) * mm, "end": v(-23.64, -9.85) * mm});
            skLineSegment(sketch, "E516", {"start": v(-23.64, -9.85) * mm, "end": v(-23.53, -9.98) * mm});
            skLineSegment(sketch, "E517", {"start": v(-23.53, -9.98) * mm, "end": v(-23.16, -10.78) * mm});
            skLineSegment(sketch, "E518", {"start": v(-23.16, -10.78) * mm, "end": v(-23, -11.73) * mm});
            skLineSegment(sketch, "E519", {"start": v(-23, -11.73) * mm, "end": v(-23, -12.05) * mm});
            skLineSegment(sketch, "E520", {"start": v(-23, -12.05) * mm, "end": v(-23, -15.97) * mm});
            skLineSegment(sketch, "E521", {"start": v(-23, -15.97) * mm, "end": v(-22.98, -15.97) * mm});
            skLineSegment(sketch, "E522", {"start": v(-19.16, -15.36) * mm, "end": v(-19.18, -15.33) * mm});
            skLineSegment(sketch, "E523", {"start": v(-19.18, -15.33) * mm, "end": v(-19.3, -15) * mm});
            skLineSegment(sketch, "E524", {"start": v(-19.3, -15) * mm, "end": v(-19.3, -14.96) * mm});
            skLineSegment(sketch, "E525", {"start": v(-19.3, -14.96) * mm, "end": v(-19.31, -14.92) * mm});
            skLineSegment(sketch, "E526", {"start": v(-19.31, -14.92) * mm, "end": v(-19.38, -14.56) * mm});
            skLineSegment(sketch, "E527", {"start": v(-19.38, -14.56) * mm, "end": v(-19.4, -14.53) * mm});
            skLineSegment(sketch, "E528", {"start": v(-19.4, -14.53) * mm, "end": v(-19.43, -14.6) * mm});
            skLineSegment(sketch, "E529", {"start": v(-19.43, -14.6) * mm, "end": v(-19.94, -15.16) * mm});
            skLineSegment(sketch, "E530", {"start": v(-19.94, -15.16) * mm, "end": v(-20, -15.2) * mm});
            skLineSegment(sketch, "E531", {"start": v(-20, -15.2) * mm, "end": v(-20.07, -15.25) * mm});
            skLineSegment(sketch, "E532", {"start": v(-20.07, -15.25) * mm, "end": v(-20.43, -15.4) * mm});
            skLineSegment(sketch, "E533", {"start": v(-20.43, -15.4) * mm, "end": v(-20.8, -15.47) * mm});
            skLineSegment(sketch, "E534", {"start": v(-20.8, -15.47) * mm, "end": v(-20.92, -15.47) * mm});
            skLineSegment(sketch, "E535", {"start": v(-20.92, -15.47) * mm, "end": v(-21.1, -15.47) * mm});
            skLineSegment(sketch, "E536", {"start": v(-21.1, -15.47) * mm, "end": v(-21.7, -15.35) * mm});
            skLineSegment(sketch, "E537", {"start": v(-21.7, -15.35) * mm, "end": v(-22.19, -15.1) * mm});
            skLineSegment(sketch, "E538", {"start": v(-22.19, -15.1) * mm, "end": v(-22.27, -15.02) * mm});
            skLineSegment(sketch, "E539", {"start": v(-22.27, -15.02) * mm, "end": v(-22.35, -14.95) * mm});
            skLineSegment(sketch, "E540", {"start": v(-22.35, -14.95) * mm, "end": v(-22.63, -14.5) * mm});
            skLineSegment(sketch, "E541", {"start": v(-22.63, -14.5) * mm, "end": v(-22.75, -13.97) * mm});
            skLineSegment(sketch, "E542", {"start": v(-22.75, -13.97) * mm, "end": v(-22.75, -13.79) * mm});
            skLineSegment(sketch, "E543", {"start": v(-22.75, -13.79) * mm, "end": v(-22.75, -13.6) * mm});
            skLineSegment(sketch, "E544", {"start": v(-22.75, -13.6) * mm, "end": v(-22.59, -13.06) * mm});
            skLineSegment(sketch, "E545", {"start": v(-22.59, -13.06) * mm, "end": v(-22.22, -12.59) * mm});
            skLineSegment(sketch, "E546", {"start": v(-22.22, -12.59) * mm, "end": v(-22.12, -12.51) * mm});
            skLineSegment(sketch, "E547", {"start": v(-22.12, -12.51) * mm, "end": v(-22.01, -12.44) * mm});
            skLineSegment(sketch, "E548", {"start": v(-22.01, -12.44) * mm, "end": v(-21.34, -12.17) * mm});
            skLineSegment(sketch, "E549", {"start": v(-21.34, -12.17) * mm, "end": v(-20.54, -12.07) * mm});
            skLineSegment(sketch, "E550", {"start": v(-20.54, -12.07) * mm, "end": v(-20.27, -12.07) * mm});
            skLineSegment(sketch, "E551", {"start": v(-20.27, -12.07) * mm, "end": v(-19.42, -12.07) * mm});
            skLineSegment(sketch, "E552", {"start": v(-19.42, -12.07) * mm, "end": v(-19.42, -11.62) * mm});
            skLineSegment(sketch, "E553", {"start": v(-19.42, -11.62) * mm, "end": v(-19.42, -11.53) * mm});
            skLineSegment(sketch, "E554", {"start": v(-19.42, -11.53) * mm, "end": v(-19.48, -11.26) * mm});
            skLineSegment(sketch, "E555", {"start": v(-19.48, -11.26) * mm, "end": v(-19.6, -11.03) * mm});
            skLineSegment(sketch, "E556", {"start": v(-19.6, -11.03) * mm, "end": v(-19.64, -10.99) * mm});
            skLineSegment(sketch, "E557", {"start": v(-19.64, -10.99) * mm, "end": v(-19.67, -10.95) * mm});
            skLineSegment(sketch, "E558", {"start": v(-19.67, -10.95) * mm, "end": v(-19.9, -10.82) * mm});
            skLineSegment(sketch, "E559", {"start": v(-19.9, -10.82) * mm, "end": v(-20.18, -10.77) * mm});
            skLineSegment(sketch, "E560", {"start": v(-20.18, -10.77) * mm, "end": v(-20.27, -10.77) * mm});
            skLineSegment(sketch, "E561", {"start": v(-20.27, -10.77) * mm, "end": v(-20.41, -10.77) * mm});
            skLineSegment(sketch, "E562", {"start": v(-20.41, -10.77) * mm, "end": v(-20.8, -10.93) * mm});
            skLineSegment(sketch, "E563", {"start": v(-20.8, -10.93) * mm, "end": v(-20.84, -10.96) * mm});
            skLineSegment(sketch, "E564", {"start": v(-20.84, -10.96) * mm, "end": v(-20.87, -10.99) * mm});
            skLineSegment(sketch, "E565", {"start": v(-20.87, -10.99) * mm, "end": v(-21, -11.17) * mm});
            skLineSegment(sketch, "E566", {"start": v(-21, -11.17) * mm, "end": v(-21.04, -11.38) * mm});
            skLineSegment(sketch, "E567", {"start": v(-21.04, -11.38) * mm, "end": v(-21.04, -11.45) * mm});
            skLineSegment(sketch, "E568", {"start": v(-21.04, -11.45) * mm, "end": v(-22.5, -11.45) * mm});
            skLineSegment(sketch, "E569", {"start": v(-22.5, -11.45) * mm, "end": v(-22.5, -11.42) * mm});
            skLineSegment(sketch, "E570", {"start": v(-22.5, -11.42) * mm, "end": v(-22.5, -11.3) * mm});
            skLineSegment(sketch, "E571", {"start": v(-22.5, -11.3) * mm, "end": v(-22.37, -10.76) * mm});
            skLineSegment(sketch, "E572", {"start": v(-22.37, -10.76) * mm, "end": v(-22, -10.28) * mm});
            skLineSegment(sketch, "E573", {"start": v(-22, -10.28) * mm, "end": v(-21.89, -10.19) * mm});
            skLineSegment(sketch, "E574", {"start": v(-21.89, -10.19) * mm, "end": v(-21.78, -10.1) * mm});
            skLineSegment(sketch, "E575", {"start": v(-21.78, -10.1) * mm, "end": v(-21.14, -9.8) * mm});
            skLineSegment(sketch, "E576", {"start": v(-21.14, -9.8) * mm, "end": v(-20.42, -9.68) * mm});
            skLineSegment(sketch, "E577", {"start": v(-20.42, -9.68) * mm, "end": v(-20.18, -9.68) * mm});
            skLineSegment(sketch, "E578", {"start": v(-20.18, -9.68) * mm, "end": v(-19.95, -9.68) * mm});
            skLineSegment(sketch, "E579", {"start": v(-19.95, -9.68) * mm, "end": v(-19.27, -9.8) * mm});
            skLineSegment(sketch, "E580", {"start": v(-19.27, -9.8) * mm, "end": v(-18.65, -10.1) * mm});
            skLineSegment(sketch, "E581", {"start": v(-18.65, -10.1) * mm, "end": v(-18.55, -10.19) * mm});
            skLineSegment(sketch, "E582", {"start": v(-18.55, -10.19) * mm, "end": v(-18.44, -10.27) * mm});
            skLineSegment(sketch, "E583", {"start": v(-18.44, -10.27) * mm, "end": v(-18.08, -10.8) * mm});
            skLineSegment(sketch, "E584", {"start": v(-18.08, -10.8) * mm, "end": v(-17.91, -11.43) * mm});
            skLineSegment(sketch, "E585", {"start": v(-17.91, -11.43) * mm, "end": v(-17.91, -11.63) * mm});
            skLineSegment(sketch, "E586", {"start": v(-17.91, -11.63) * mm, "end": v(-17.91, -13.94) * mm});
            skLineSegment(sketch, "E587", {"start": v(-17.91, -13.94) * mm, "end": v(-17.91, -14.13) * mm});
            skLineSegment(sketch, "E588", {"start": v(-17.91, -14.13) * mm, "end": v(-17.87, -14.63) * mm});
            skLineSegment(sketch, "E589", {"start": v(-17.87, -14.63) * mm, "end": v(-17.85, -14.68) * mm});
            skLineSegment(sketch, "E590", {"start": v(-17.85, -14.68) * mm, "end": v(-17.84, -14.74) * mm});
            skLineSegment(sketch, "E591", {"start": v(-17.84, -14.74) * mm, "end": v(-17.69, -15.32) * mm});
            skLineSegment(sketch, "E592", {"start": v(-17.69, -15.32) * mm, "end": v(-17.67, -15.38) * mm});
            skLineSegment(sketch, "E593", {"start": v(-17.67, -15.38) * mm, "end": v(-19.16, -15.38) * mm});
            skLineSegment(sketch, "E594", {"start": v(-19.16, -15.38) * mm, "end": v(-19.16, -15.36) * mm});
            skLineSegment(sketch, "E595", {"start": v(-20.55, -14.34) * mm, "end": v(-20.37, -14.34) * mm});
            skLineSegment(sketch, "E596", {"start": v(-20.37, -14.34) * mm, "end": v(-19.89, -14.18) * mm});
            skLineSegment(sketch, "E597", {"start": v(-19.89, -14.18) * mm, "end": v(-19.84, -14.14) * mm});
            skLineSegment(sketch, "E598", {"start": v(-19.84, -14.14) * mm, "end": v(-19.79, -14.1) * mm});
            skLineSegment(sketch, "E599", {"start": v(-19.79, -14.1) * mm, "end": v(-19.58, -13.93) * mm});
            skLineSegment(sketch, "E600", {"start": v(-19.58, -13.93) * mm, "end": v(-19.44, -13.73) * mm});
            skLineSegment(sketch, "E601", {"start": v(-19.44, -13.73) * mm, "end": v(-19.42, -13.68) * mm});
            skLineSegment(sketch, "E602", {"start": v(-19.42, -13.68) * mm, "end": v(-19.42, -12.9) * mm});
            skLineSegment(sketch, "E603", {"start": v(-19.42, -12.9) * mm, "end": v(-20.27, -12.9) * mm});
            skLineSegment(sketch, "E604", {"start": v(-20.27, -12.9) * mm, "end": v(-20.38, -12.9) * mm});
            skLineSegment(sketch, "E605", {"start": v(-20.38, -12.9) * mm, "end": v(-20.7, -12.96) * mm});
            skLineSegment(sketch, "E606", {"start": v(-20.7, -12.96) * mm, "end": v(-20.95, -13.1) * mm});
            skLineSegment(sketch, "E607", {"start": v(-20.95, -13.1) * mm, "end": v(-21, -13.14) * mm});
            skLineSegment(sketch, "E608", {"start": v(-21, -13.14) * mm, "end": v(-21.03, -13.19) * mm});
            skLineSegment(sketch, "E609", {"start": v(-21.03, -13.19) * mm, "end": v(-21.17, -13.41) * mm});
            skLineSegment(sketch, "E610", {"start": v(-21.17, -13.41) * mm, "end": v(-21.24, -13.65) * mm});
            skLineSegment(sketch, "E611", {"start": v(-21.24, -13.65) * mm, "end": v(-21.24, -13.73) * mm});
            skLineSegment(sketch, "E612", {"start": v(-21.24, -13.73) * mm, "end": v(-21.24, -13.84) * mm});
            skLineSegment(sketch, "E613", {"start": v(-21.24, -13.84) * mm, "end": v(-21.09, -14.15) * mm});
            skLineSegment(sketch, "E614", {"start": v(-21.09, -14.15) * mm, "end": v(-21.05, -14.17) * mm});
            skLineSegment(sketch, "E615", {"start": v(-21.05, -14.17) * mm, "end": v(-21.02, -14.2) * mm});
            skLineSegment(sketch, "E616", {"start": v(-21.02, -14.2) * mm, "end": v(-20.67, -14.34) * mm});
            skLineSegment(sketch, "E617", {"start": v(-20.67, -14.34) * mm, "end": v(-20.55, -14.34) * mm});
            skLineSegment(sketch, "E618", {"start": v(-20.92, -16.08) * mm, "end": v(-21.17, -16.08) * mm});
            skLineSegment(sketch, "E619", {"start": v(-21.17, -16.08) * mm, "end": v(-21.92, -15.92) * mm});
            skLineSegment(sketch, "E620", {"start": v(-21.92, -15.92) * mm, "end": v(-22.59, -15.57) * mm});
            skLineSegment(sketch, "E621", {"start": v(-22.59, -15.57) * mm, "end": v(-22.7, -15.47) * mm});
            skLineSegment(sketch, "E622", {"start": v(-22.7, -15.47) * mm, "end": v(-22.81, -15.36) * mm});
            skLineSegment(sketch, "E623", {"start": v(-22.81, -15.36) * mm, "end": v(-23.2, -14.73) * mm});
            skLineSegment(sketch, "E624", {"start": v(-23.2, -14.73) * mm, "end": v(-23.36, -14.02) * mm});
            skLineSegment(sketch, "E625", {"start": v(-23.36, -14.02) * mm, "end": v(-23.36, -13.79) * mm});
            skLineSegment(sketch, "E626", {"start": v(-23.36, -13.79) * mm, "end": v(-23.36, -13.54) * mm});
            skLineSegment(sketch, "E627", {"start": v(-23.36, -13.54) * mm, "end": v(-23.15, -12.8) * mm});
            skLineSegment(sketch, "E628", {"start": v(-23.15, -12.8) * mm, "end": v(-22.66, -12.15) * mm});
            skLineSegment(sketch, "E629", {"start": v(-22.66, -12.15) * mm, "end": v(-22.52, -12.05) * mm});
            skLineSegment(sketch, "E630", {"start": v(-22.52, -12.05) * mm, "end": v(-23, -12.05) * mm});
            skLineSegment(sketch, "E631", {"start": v(-23, -12.05) * mm, "end": v(-23.09, -11.43) * mm});
            skLineSegment(sketch, "E632", {"start": v(-23.09, -11.43) * mm, "end": v(-23.1, -11.34) * mm});
            skLineSegment(sketch, "E633", {"start": v(-23.1, -11.34) * mm, "end": v(-23.07, -11.05) * mm});
            skLineSegment(sketch, "E634", {"start": v(-23.07, -11.05) * mm, "end": v(-22.95, -10.61) * mm});
            skLineSegment(sketch, "E635", {"start": v(-22.95, -10.61) * mm, "end": v(-22.69, -10.15) * mm});
            skLineSegment(sketch, "E636", {"start": v(-22.69, -10.15) * mm, "end": v(-22.36, -9.8) * mm});
            skLineSegment(sketch, "E637", {"start": v(-22.36, -9.8) * mm, "end": v(-22.24, -9.7) * mm});
            skLineSegment(sketch, "E638", {"start": v(-22.24, -9.7) * mm, "end": v(-22.1, -9.59) * mm});
            skLineSegment(sketch, "E639", {"start": v(-22.1, -9.59) * mm, "end": v(-21.3, -9.21) * mm});
            skLineSegment(sketch, "E640", {"start": v(-21.3, -9.21) * mm, "end": v(-20.44, -9.05) * mm});
            skLineSegment(sketch, "E641", {"start": v(-20.44, -9.05) * mm, "end": v(-20.15, -9.05) * mm});
            skLineSegment(sketch, "E642", {"start": v(-20.15, -9.05) * mm, "end": v(-19.87, -9.05) * mm});
            skLineSegment(sketch, "E643", {"start": v(-19.87, -9.05) * mm, "end": v(-19.03, -9.21) * mm});
            skLineSegment(sketch, "E644", {"start": v(-19.03, -9.21) * mm, "end": v(-18.26, -9.59) * mm});
            skLineSegment(sketch, "E645", {"start": v(-18.26, -9.59) * mm, "end": v(-18.13, -9.7) * mm});
            skLineSegment(sketch, "E646", {"start": v(-18.13, -9.7) * mm, "end": v(-17.99, -9.81) * mm});
            skLineSegment(sketch, "E647", {"start": v(-17.99, -9.81) * mm, "end": v(-17.5, -10.52) * mm});
            skLineSegment(sketch, "E648", {"start": v(-17.5, -10.52) * mm, "end": v(-17.28, -11.35) * mm});
            skLineSegment(sketch, "E649", {"start": v(-17.28, -11.35) * mm, "end": v(-17.28, -11.62) * mm});
            skLineSegment(sketch, "E650", {"start": v(-17.28, -11.62) * mm, "end": v(-17.28, -13.93) * mm});
            skLineSegment(sketch, "E651", {"start": v(-17.28, -13.93) * mm, "end": v(-17.28, -14.09) * mm});
            skLineSegment(sketch, "E652", {"start": v(-17.28, -14.09) * mm, "end": v(-17.25, -14.51) * mm});
            skLineSegment(sketch, "E653", {"start": v(-17.25, -14.51) * mm, "end": v(-17.24, -14.56) * mm});
            skLineSegment(sketch, "E654", {"start": v(-17.24, -14.56) * mm, "end": v(-17.23, -14.6) * mm});
            skLineSegment(sketch, "E655", {"start": v(-17.23, -14.6) * mm, "end": v(-17.1, -15.08) * mm});
            skLineSegment(sketch, "E656", {"start": v(-17.1, -15.08) * mm, "end": v(-17.08, -15.13) * mm});
            skLineSegment(sketch, "E657", {"start": v(-17.08, -15.13) * mm, "end": v(-16.76, -15.96) * mm});
            skLineSegment(sketch, "E658", {"start": v(-16.76, -15.96) * mm, "end": v(-19.56, -15.96) * mm});
            skLineSegment(sketch, "E659", {"start": v(-19.56, -15.96) * mm, "end": v(-19.67, -15.71) * mm});
            skLineSegment(sketch, "E660", {"start": v(-19.67, -15.71) * mm, "end": v(-19.76, -15.77) * mm});
            skLineSegment(sketch, "E661", {"start": v(-19.76, -15.77) * mm, "end": v(-20.25, -16) * mm});
            skLineSegment(sketch, "E662", {"start": v(-20.25, -16) * mm, "end": v(-20.75, -16.08) * mm});
            skLineSegment(sketch, "E663", {"start": v(-20.75, -16.08) * mm, "end": v(-20.92, -16.08) * mm});
            skLineSegment(sketch, "E664", {"start": v(-20.62, -13.73) * mm, "end": v(-20.55, -13.73) * mm});
            skLineSegment(sketch, "E665", {"start": v(-20.55, -13.73) * mm, "end": v(-20.45, -13.73) * mm});
            skLineSegment(sketch, "E666", {"start": v(-20.45, -13.73) * mm, "end": v(-20.19, -13.64) * mm});
            skLineSegment(sketch, "E667", {"start": v(-20.19, -13.64) * mm, "end": v(-20.16, -13.62) * mm});
            skLineSegment(sketch, "E668", {"start": v(-20.16, -13.62) * mm, "end": v(-20.15, -13.61) * mm});
            skLineSegment(sketch, "E669", {"start": v(-20.15, -13.61) * mm, "end": v(-20.03, -13.52) * mm});
            skLineSegment(sketch, "E670", {"start": v(-20.03, -13.52) * mm, "end": v(-20.02, -13.51) * mm});
            skLineSegment(sketch, "E671", {"start": v(-20.02, -13.51) * mm, "end": v(-20.25, -13.51) * mm});
            skLineSegment(sketch, "E672", {"start": v(-20.25, -13.51) * mm, "end": v(-20.33, -13.51) * mm});
            skLineSegment(sketch, "E673", {"start": v(-20.33, -13.51) * mm, "end": v(-20.55, -13.57) * mm});
            skLineSegment(sketch, "E674", {"start": v(-20.55, -13.57) * mm, "end": v(-20.56, -13.57) * mm});
            skLineSegment(sketch, "E675", {"start": v(-20.56, -13.57) * mm, "end": v(-20.57, -13.59) * mm});
            skLineSegment(sketch, "E676", {"start": v(-20.57, -13.59) * mm, "end": v(-20.62, -13.7) * mm});
            skLineSegment(sketch, "E677", {"start": v(-20.62, -13.7) * mm, "end": v(-20.62, -13.73) * mm});
            skLineSegment(sketch, "E678", {"start": v(-20.4, -11.39) * mm, "end": v(-20.4, -11.42) * mm});
            skLineSegment(sketch, "E679", {"start": v(-20.4, -11.42) * mm, "end": v(-20.07, -11.42) * mm});
            skLineSegment(sketch, "E680", {"start": v(-20.07, -11.42) * mm, "end": v(-20.07, -11.41) * mm});
            skLineSegment(sketch, "E681", {"start": v(-20.07, -11.41) * mm, "end": v(-20.08, -11.39) * mm});
            skLineSegment(sketch, "E682", {"start": v(-20.08, -11.39) * mm, "end": v(-20.22, -11.36) * mm});
            skLineSegment(sketch, "E683", {"start": v(-20.22, -11.36) * mm, "end": v(-20.27, -11.36) * mm});
            skLineSegment(sketch, "E684", {"start": v(-20.27, -11.36) * mm, "end": v(-20.29, -11.36) * mm});
            skLineSegment(sketch, "E685", {"start": v(-20.29, -11.36) * mm, "end": v(-20.38, -11.39) * mm});
            skLineSegment(sketch, "E686", {"start": v(-20.38, -11.39) * mm, "end": v(-20.4, -11.39) * mm});
            skLineSegment(sketch, "E687", {"start": v(-14.4, -14.3) * mm, "end": v(-14.24, -14.3) * mm});
            skLineSegment(sketch, "E688", {"start": v(-14.24, -14.3) * mm, "end": v(-13.8, -14.1) * mm});
            skLineSegment(sketch, "E689", {"start": v(-13.8, -14.1) * mm, "end": v(-13.76, -14.07) * mm});
            skLineSegment(sketch, "E690", {"start": v(-13.76, -14.07) * mm, "end": v(-13.72, -14.03) * mm});
            skLineSegment(sketch, "E691", {"start": v(-13.72, -14.03) * mm, "end": v(-13.57, -13.8) * mm});
            skLineSegment(sketch, "E692", {"start": v(-13.57, -13.8) * mm, "end": v(-13.51, -13.52) * mm});
            skLineSegment(sketch, "E693", {"start": v(-13.51, -13.52) * mm, "end": v(-13.51, -13.44) * mm});
            skLineSegment(sketch, "E694", {"start": v(-13.51, -13.44) * mm, "end": v(-12.14, -13.44) * mm});
            skLineSegment(sketch, "E695", {"start": v(-12.14, -13.44) * mm, "end": v(-12.13, -13.47) * mm});
            skLineSegment(sketch, "E696", {"start": v(-12.13, -13.47) * mm, "end": v(-12.12, -13.6) * mm});
            skLineSegment(sketch, "E697", {"start": v(-12.12, -13.6) * mm, "end": v(-12.28, -14.25) * mm});
            skLineSegment(sketch, "E698", {"start": v(-12.28, -14.25) * mm, "end": v(-12.66, -14.79) * mm});
            skLineSegment(sketch, "E699", {"start": v(-12.66, -14.79) * mm, "end": v(-12.77, -14.88) * mm});
            skLineSegment(sketch, "E700", {"start": v(-12.77, -14.88) * mm, "end": v(-12.89, -14.98) * mm});
            skLineSegment(sketch, "E701", {"start": v(-12.89, -14.98) * mm, "end": v(-13.52, -15.31) * mm});
            skLineSegment(sketch, "E702", {"start": v(-13.52, -15.31) * mm, "end": v(-14.18, -15.45) * mm});
            skLineSegment(sketch, "E703", {"start": v(-14.18, -15.45) * mm, "end": v(-14.4, -15.45) * mm});
            skLineSegment(sketch, "E704", {"start": v(-14.4, -15.45) * mm, "end": v(-14.68, -15.45) * mm});
            skLineSegment(sketch, "E705", {"start": v(-14.68, -15.45) * mm, "end": v(-15.51, -15.26) * mm});
            skLineSegment(sketch, "E706", {"start": v(-15.51, -15.26) * mm, "end": v(-16.22, -14.8) * mm});
            skLineSegment(sketch, "E707", {"start": v(-16.22, -14.8) * mm, "end": v(-16.33, -14.67) * mm});
            skLineSegment(sketch, "E708", {"start": v(-16.33, -14.67) * mm, "end": v(-16.44, -14.54) * mm});
            skLineSegment(sketch, "E709", {"start": v(-16.44, -14.54) * mm, "end": v(-16.84, -13.77) * mm});
            skLineSegment(sketch, "E710", {"start": v(-16.84, -13.77) * mm, "end": v(-17, -12.92) * mm});
            skLineSegment(sketch, "E711", {"start": v(-17, -12.92) * mm, "end": v(-17, -12.64) * mm});
            skLineSegment(sketch, "E712", {"start": v(-17, -12.64) * mm, "end": v(-17, -12.48) * mm});
            skLineSegment(sketch, "E713", {"start": v(-17, -12.48) * mm, "end": v(-17, -12.2) * mm});
            skLineSegment(sketch, "E714", {"start": v(-17, -12.2) * mm, "end": v(-16.84, -11.35) * mm});
            skLineSegment(sketch, "E715", {"start": v(-16.84, -11.35) * mm, "end": v(-16.44, -10.58) * mm});
            skLineSegment(sketch, "E716", {"start": v(-16.44, -10.58) * mm, "end": v(-16.33, -10.45) * mm});
            skLineSegment(sketch, "E717", {"start": v(-16.33, -10.45) * mm, "end": v(-16.22, -10.32) * mm});
            skLineSegment(sketch, "E718", {"start": v(-16.22, -10.32) * mm, "end": v(-15.51, -9.85) * mm});
            skLineSegment(sketch, "E719", {"start": v(-15.51, -9.85) * mm, "end": v(-14.68, -9.65) * mm});
            skLineSegment(sketch, "E720", {"start": v(-14.68, -9.65) * mm, "end": v(-14.4, -9.65) * mm});
            skLineSegment(sketch, "E721", {"start": v(-14.4, -9.65) * mm, "end": v(-14.17, -9.65) * mm});
            skLineSegment(sketch, "E722", {"start": v(-14.17, -9.65) * mm, "end": v(-13.47, -9.8) * mm});
            skLineSegment(sketch, "E723", {"start": v(-13.47, -9.8) * mm, "end": v(-12.85, -10.14) * mm});
            skLineSegment(sketch, "E724", {"start": v(-12.85, -10.14) * mm, "end": v(-12.74, -10.23) * mm});
            skLineSegment(sketch, "E725", {"start": v(-12.74, -10.23) * mm, "end": v(-12.64, -10.33) * mm});
            skLineSegment(sketch, "E726", {"start": v(-12.64, -10.33) * mm, "end": v(-12.27, -10.91) * mm});
            skLineSegment(sketch, "E727", {"start": v(-12.27, -10.91) * mm, "end": v(-12.12, -11.63) * mm});
            skLineSegment(sketch, "E728", {"start": v(-12.12, -11.63) * mm, "end": v(-12.13, -11.79) * mm});
            skLineSegment(sketch, "E729", {"start": v(-12.13, -11.79) * mm, "end": v(-12.14, -11.82) * mm});
            skLineSegment(sketch, "E730", {"start": v(-12.14, -11.82) * mm, "end": v(-13.51, -11.82) * mm});
            skLineSegment(sketch, "E731", {"start": v(-13.51, -11.82) * mm, "end": v(-13.51, -11.72) * mm});
            skLineSegment(sketch, "E732", {"start": v(-13.51, -11.72) * mm, "end": v(-13.57, -11.42) * mm});
            skLineSegment(sketch, "E733", {"start": v(-13.57, -11.42) * mm, "end": v(-13.7, -11.15) * mm});
            skLineSegment(sketch, "E734", {"start": v(-13.7, -11.15) * mm, "end": v(-13.74, -11.1) * mm});
            skLineSegment(sketch, "E735", {"start": v(-13.74, -11.1) * mm, "end": v(-13.78, -11.05) * mm});
            skLineSegment(sketch, "E736", {"start": v(-13.78, -11.05) * mm, "end": v(-14.03, -10.88) * mm});
            skLineSegment(sketch, "E737", {"start": v(-14.03, -10.88) * mm, "end": v(-14.31, -10.8) * mm});
            skLineSegment(sketch, "E738", {"start": v(-14.31, -10.8) * mm, "end": v(-14.4, -10.8) * mm});
            skLineSegment(sketch, "E739", {"start": v(-14.4, -10.8) * mm, "end": v(-14.53, -10.8) * mm});
            skLineSegment(sketch, "E740", {"start": v(-14.53, -10.8) * mm, "end": v(-14.92, -10.92) * mm});
            skLineSegment(sketch, "E741", {"start": v(-14.92, -10.92) * mm, "end": v(-15.21, -11.19) * mm});
            skLineSegment(sketch, "E742", {"start": v(-15.21, -11.19) * mm, "end": v(-15.25, -11.27) * mm});
            skLineSegment(sketch, "E743", {"start": v(-15.25, -11.27) * mm, "end": v(-15.3, -11.34) * mm});
            skLineSegment(sketch, "E744", {"start": v(-15.3, -11.34) * mm, "end": v(-15.44, -11.8) * mm});
            skLineSegment(sketch, "E745", {"start": v(-15.44, -11.8) * mm, "end": v(-15.5, -12.3) * mm});
            skLineSegment(sketch, "E746", {"start": v(-15.5, -12.3) * mm, "end": v(-15.5, -12.47) * mm});
            skLineSegment(sketch, "E747", {"start": v(-15.5, -12.47) * mm, "end": v(-15.5, -12.62) * mm});
            skLineSegment(sketch, "E748", {"start": v(-15.5, -12.62) * mm, "end": v(-15.5, -12.79) * mm});
            skLineSegment(sketch, "E749", {"start": v(-15.5, -12.79) * mm, "end": v(-15.44, -13.3) * mm});
            skLineSegment(sketch, "E750", {"start": v(-15.44, -13.3) * mm, "end": v(-15.3, -13.75) * mm});
            skLineSegment(sketch, "E751", {"start": v(-15.3, -13.75) * mm, "end": v(-15.25, -13.82) * mm});
            skLineSegment(sketch, "E752", {"start": v(-15.25, -13.82) * mm, "end": v(-15.21, -13.9) * mm});
            skLineSegment(sketch, "E753", {"start": v(-15.21, -13.9) * mm, "end": v(-14.92, -14.17) * mm});
            skLineSegment(sketch, "E754", {"start": v(-14.92, -14.17) * mm, "end": v(-14.53, -14.3) * mm});
            skLineSegment(sketch, "E755", {"start": v(-14.53, -14.3) * mm, "end": v(-14.4, -14.3) * mm});
            skLineSegment(sketch, "E756", {"start": v(-14.4, -16.08) * mm, "end": v(-14.59, -16.08) * mm});
            skLineSegment(sketch, "E757", {"start": v(-14.59, -16.08) * mm, "end": v(-15.13, -16.02) * mm});
            skLineSegment(sketch, "E758", {"start": v(-15.13, -16.02) * mm, "end": v(-15.77, -15.83) * mm});
            skLineSegment(sketch, "E759", {"start": v(-15.77, -15.83) * mm, "end": v(-16.33, -15.52) * mm});
            skLineSegment(sketch, "E760", {"start": v(-16.33, -15.52) * mm, "end": v(-16.7, -15.2) * mm});
            skLineSegment(sketch, "E761", {"start": v(-16.7, -15.2) * mm, "end": v(-16.8, -15.08) * mm});
            skLineSegment(sketch, "E762", {"start": v(-16.8, -15.08) * mm, "end": v(-16.95, -14.92) * mm});
            skLineSegment(sketch, "E763", {"start": v(-16.95, -14.92) * mm, "end": v(-17.43, -13.99) * mm});
            skLineSegment(sketch, "E764", {"start": v(-17.43, -13.99) * mm, "end": v(-17.64, -12.98) * mm});
            skLineSegment(sketch, "E765", {"start": v(-17.64, -12.98) * mm, "end": v(-17.64, -12.65) * mm});
            skLineSegment(sketch, "E766", {"start": v(-17.64, -12.65) * mm, "end": v(-17.64, -12.5) * mm});
            skLineSegment(sketch, "E767", {"start": v(-17.64, -12.5) * mm, "end": v(-17.64, -12.16) * mm});
            skLineSegment(sketch, "E768", {"start": v(-17.64, -12.16) * mm, "end": v(-17.43, -11.16) * mm});
            skLineSegment(sketch, "E769", {"start": v(-17.43, -11.16) * mm, "end": v(-16.96, -10.23) * mm});
            skLineSegment(sketch, "E770", {"start": v(-16.96, -10.23) * mm, "end": v(-16.82, -10.07) * mm});
            skLineSegment(sketch, "E771", {"start": v(-16.82, -10.07) * mm, "end": v(-16.72, -9.94) * mm});
            skLineSegment(sketch, "E772", {"start": v(-16.72, -9.94) * mm, "end": v(-16.35, -9.62) * mm});
            skLineSegment(sketch, "E773", {"start": v(-16.35, -9.62) * mm, "end": v(-15.8, -9.3) * mm});
            skLineSegment(sketch, "E774", {"start": v(-15.8, -9.3) * mm, "end": v(-15.15, -9.11) * mm});
            skLineSegment(sketch, "E775", {"start": v(-15.15, -9.11) * mm, "end": v(-14.6, -9.05) * mm});
            skLineSegment(sketch, "E776", {"start": v(-14.6, -9.05) * mm, "end": v(-14.42, -9.05) * mm});
            skLineSegment(sketch, "E777", {"start": v(-14.42, -9.05) * mm, "end": v(-14.13, -9.05) * mm});
            skLineSegment(sketch, "E778", {"start": v(-14.13, -9.05) * mm, "end": v(-13.26, -9.24) * mm});
            skLineSegment(sketch, "E779", {"start": v(-13.26, -9.24) * mm, "end": v(-12.46, -9.68) * mm});
            skLineSegment(sketch, "E780", {"start": v(-12.46, -9.68) * mm, "end": v(-12.33, -9.8) * mm});
            skLineSegment(sketch, "E781", {"start": v(-12.33, -9.8) * mm, "end": v(-12.19, -9.93) * mm});
            skLineSegment(sketch, "E782", {"start": v(-12.19, -9.93) * mm, "end": v(-11.7, -10.7) * mm});
            skLineSegment(sketch, "E783", {"start": v(-11.7, -10.7) * mm, "end": v(-11.5, -11.62) * mm});
            skLineSegment(sketch, "E784", {"start": v(-11.5, -11.62) * mm, "end": v(-11.51, -11.82) * mm});
            skLineSegment(sketch, "E785", {"start": v(-11.51, -11.82) * mm, "end": v(-11.51, -11.91) * mm});
            skLineSegment(sketch, "E786", {"start": v(-11.51, -11.91) * mm, "end": v(-11.7, -12.45) * mm});
            skLineSegment(sketch, "E787", {"start": v(-11.7, -12.45) * mm, "end": v(-14.13, -12.45) * mm});
            skLineSegment(sketch, "E788", {"start": v(-14.13, -12.45) * mm, "end": v(-14.13, -11.84) * mm});
            skLineSegment(sketch, "E789", {"start": v(-14.13, -11.84) * mm, "end": v(-14.13, -11.78) * mm});
            skLineSegment(sketch, "E790", {"start": v(-14.13, -11.78) * mm, "end": v(-14.16, -11.62) * mm});
            skLineSegment(sketch, "E791", {"start": v(-14.16, -11.62) * mm, "end": v(-14.21, -11.52) * mm});
            skLineSegment(sketch, "E792", {"start": v(-14.21, -11.52) * mm, "end": v(-14.22, -11.51) * mm});
            skLineSegment(sketch, "E793", {"start": v(-14.22, -11.51) * mm, "end": v(-14.23, -11.5) * mm});
            skLineSegment(sketch, "E794", {"start": v(-14.23, -11.5) * mm, "end": v(-14.27, -11.47) * mm});
            skLineSegment(sketch, "E795", {"start": v(-14.27, -11.47) * mm, "end": v(-14.37, -11.45) * mm});
            skLineSegment(sketch, "E796", {"start": v(-14.37, -11.45) * mm, "end": v(-14.4, -11.45) * mm});
            skLineSegment(sketch, "E797", {"start": v(-14.4, -11.45) * mm, "end": v(-14.46, -11.45) * mm});
            skLineSegment(sketch, "E798", {"start": v(-14.46, -11.45) * mm, "end": v(-14.63, -11.5) * mm});
            skLineSegment(sketch, "E799", {"start": v(-14.63, -11.5) * mm, "end": v(-14.7, -11.57) * mm});
            skLineSegment(sketch, "E800", {"start": v(-14.7, -11.57) * mm, "end": v(-14.71, -11.59) * mm});
            skLineSegment(sketch, "E801", {"start": v(-14.71, -11.59) * mm, "end": v(-14.74, -11.64) * mm});
            skLineSegment(sketch, "E802", {"start": v(-14.74, -11.64) * mm, "end": v(-14.84, -11.98) * mm});
            skLineSegment(sketch, "E803", {"start": v(-14.84, -11.98) * mm, "end": v(-14.88, -12.37) * mm});
            skLineSegment(sketch, "E804", {"start": v(-14.88, -12.37) * mm, "end": v(-14.88, -12.5) * mm});
            skLineSegment(sketch, "E805", {"start": v(-14.88, -12.5) * mm, "end": v(-14.88, -12.65) * mm});
            skLineSegment(sketch, "E806", {"start": v(-14.88, -12.65) * mm, "end": v(-14.88, -12.78) * mm});
            skLineSegment(sketch, "E807", {"start": v(-14.88, -12.78) * mm, "end": v(-14.84, -13.18) * mm});
            skLineSegment(sketch, "E808", {"start": v(-14.84, -13.18) * mm, "end": v(-14.74, -13.5) * mm});
            skLineSegment(sketch, "E809", {"start": v(-14.74, -13.5) * mm, "end": v(-14.71, -13.56) * mm});
            skLineSegment(sketch, "E810", {"start": v(-14.71, -13.56) * mm, "end": v(-14.7, -13.57) * mm});
            skLineSegment(sketch, "E811", {"start": v(-14.7, -13.57) * mm, "end": v(-14.63, -13.65) * mm});
            skLineSegment(sketch, "E812", {"start": v(-14.63, -13.65) * mm, "end": v(-14.46, -13.7) * mm});
            skLineSegment(sketch, "E813", {"start": v(-14.46, -13.7) * mm, "end": v(-14.4, -13.7) * mm});
            skLineSegment(sketch, "E814", {"start": v(-14.4, -13.7) * mm, "end": v(-14.37, -13.7) * mm});
            skLineSegment(sketch, "E815", {"start": v(-14.37, -13.7) * mm, "end": v(-14.25, -13.67) * mm});
            skLineSegment(sketch, "E816", {"start": v(-14.25, -13.67) * mm, "end": v(-14.2, -13.64) * mm});
            skLineSegment(sketch, "E817", {"start": v(-14.2, -13.64) * mm, "end": v(-14.2, -13.64) * mm});
            skLineSegment(sketch, "E818", {"start": v(-14.2, -13.64) * mm, "end": v(-14.19, -13.63) * mm});
            skLineSegment(sketch, "E819", {"start": v(-14.19, -13.63) * mm, "end": v(-14.15, -13.59) * mm});
            skLineSegment(sketch, "E820", {"start": v(-14.15, -13.59) * mm, "end": v(-14.13, -13.49) * mm});
            skLineSegment(sketch, "E821", {"start": v(-14.13, -13.49) * mm, "end": v(-14.13, -13.45) * mm});
            skLineSegment(sketch, "E822", {"start": v(-14.13, -13.45) * mm, "end": v(-14.13, -12.84) * mm});
            skLineSegment(sketch, "E823", {"start": v(-14.13, -12.84) * mm, "end": v(-11.76, -12.84) * mm});
            skLineSegment(sketch, "E824", {"start": v(-11.76, -12.84) * mm, "end": v(-11.51, -13.33) * mm});
            skLineSegment(sketch, "E825", {"start": v(-11.51, -13.33) * mm, "end": v(-11.51, -13.47) * mm});
            skLineSegment(sketch, "E826", {"start": v(-11.51, -13.47) * mm, "end": v(-11.5, -13.65) * mm});
            skLineSegment(sketch, "E827", {"start": v(-11.5, -13.65) * mm, "end": v(-11.72, -14.5) * mm});
            skLineSegment(sketch, "E828", {"start": v(-11.72, -14.5) * mm, "end": v(-12.22, -15.24) * mm});
            skLineSegment(sketch, "E829", {"start": v(-12.22, -15.24) * mm, "end": v(-12.36, -15.36) * mm});
            skLineSegment(sketch, "E830", {"start": v(-12.36, -15.36) * mm, "end": v(-12.5, -15.48) * mm});
            skLineSegment(sketch, "E831", {"start": v(-12.5, -15.48) * mm, "end": v(-13.3, -15.9) * mm});
            skLineSegment(sketch, "E832", {"start": v(-13.3, -15.9) * mm, "end": v(-14.13, -16.08) * mm});
            skLineSegment(sketch, "E833", {"start": v(-14.13, -16.08) * mm, "end": v(-14.4, -16.08) * mm});
            skLineSegment(sketch, "E834", {"start": v(-9.34, -13) * mm, "end": v(-9.76, -13) * mm});
            skLineSegment(sketch, "E835", {"start": v(-9.76, -13) * mm, "end": v(-9.76, -15.34) * mm});
            skLineSegment(sketch, "E836", {"start": v(-9.76, -15.34) * mm, "end": v(-11.27, -15.34) * mm});
            skLineSegment(sketch, "E837", {"start": v(-11.27, -15.34) * mm, "end": v(-11.27, -7.28) * mm});
            skLineSegment(sketch, "E838", {"start": v(-11.27, -7.28) * mm, "end": v(-9.76, -7.28) * mm});
            skLineSegment(sketch, "E839", {"start": v(-9.76, -7.28) * mm, "end": v(-9.76, -11.87) * mm});
            skLineSegment(sketch, "E840", {"start": v(-9.76, -11.87) * mm, "end": v(-9.39, -11.87) * mm});
            skLineSegment(sketch, "E841", {"start": v(-9.39, -11.87) * mm, "end": v(-8.1, -9.76) * mm});
            skLineSegment(sketch, "E842", {"start": v(-8.1, -9.76) * mm, "end": v(-6.34, -9.76) * mm});
            skLineSegment(sketch, "E843", {"start": v(-6.34, -9.76) * mm, "end": v(-8.13, -12.3) * mm});
            skLineSegment(sketch, "E844", {"start": v(-8.13, -12.3) * mm, "end": v(-6.06, -15.36) * mm});
            skLineSegment(sketch, "E845", {"start": v(-6.06, -15.36) * mm, "end": v(-7.8, -15.36) * mm});
            skLineSegment(sketch, "E846", {"start": v(-7.8, -15.36) * mm, "end": v(-9.34, -13) * mm});
            skLineSegment(sketch, "E847", {"start": v(-4.9, -15.97) * mm, "end": v(-8.13, -15.97) * mm});
            skLineSegment(sketch, "E848", {"start": v(-8.13, -15.97) * mm, "end": v(-9.14, -14.44) * mm});
            skLineSegment(sketch, "E849", {"start": v(-9.14, -14.44) * mm, "end": v(-9.14, -15.97) * mm});
            skLineSegment(sketch, "E850", {"start": v(-9.14, -15.97) * mm, "end": v(-11.88, -15.97) * mm});
            skLineSegment(sketch, "E851", {"start": v(-11.88, -15.97) * mm, "end": v(-11.88, -6.68) * mm});
            skLineSegment(sketch, "E852", {"start": v(-11.88, -6.68) * mm, "end": v(-9.14, -6.68) * mm});
            skLineSegment(sketch, "E853", {"start": v(-9.14, -6.68) * mm, "end": v(-9.14, -10.31) * mm});
            skLineSegment(sketch, "E854", {"start": v(-9.14, -10.31) * mm, "end": v(-8.43, -9.16) * mm});
            skLineSegment(sketch, "E855", {"start": v(-8.43, -9.16) * mm, "end": v(-5.16, -9.16) * mm});
            skLineSegment(sketch, "E856", {"start": v(-5.16, -9.16) * mm, "end": v(-7.39, -12.31) * mm});
            skLineSegment(sketch, "E857", {"start": v(-7.39, -12.31) * mm, "end": v(-4.9, -15.97) * mm});
            skLineSegment(sketch, "E858", {"start": v(-5.53, -7.3) * mm, "end": v(-4.02, -7.3) * mm});
            skLineSegment(sketch, "E859", {"start": v(-4.02, -7.3) * mm, "end": v(-4.02, -15.36) * mm});
            skLineSegment(sketch, "E860", {"start": v(-4.02, -15.36) * mm, "end": v(-5.53, -15.36) * mm});
            skLineSegment(sketch, "E861", {"start": v(-5.53, -15.36) * mm, "end": v(-5.53, -7.3) * mm});
            skLineSegment(sketch, "E862", {"start": v(-6.14, -6.68) * mm, "end": v(-3.4, -6.68) * mm});
            skLineSegment(sketch, "E863", {"start": v(-3.4, -6.68) * mm, "end": v(-3.4, -15.97) * mm});
            skLineSegment(sketch, "E864", {"start": v(-3.4, -15.97) * mm, "end": v(-6.14, -15.97) * mm});
            skLineSegment(sketch, "E865", {"start": v(-6.14, -15.97) * mm, "end": v(-6.14, -6.68) * mm});
            skLineSegment(sketch, "E866", {"start": v(0.52, -15.36) * mm, "end": v(0.5, -15.33) * mm});
            skLineSegment(sketch, "E867", {"start": v(0.5, -15.33) * mm, "end": v(0.4, -15) * mm});
            skLineSegment(sketch, "E868", {"start": v(0.4, -15) * mm, "end": v(0.38, -14.96) * mm});
            skLineSegment(sketch, "E869", {"start": v(0.38, -14.96) * mm, "end": v(0.37, -14.92) * mm});
            skLineSegment(sketch, "E870", {"start": v(0.37, -14.92) * mm, "end": v(0.3, -14.56) * mm});
            skLineSegment(sketch, "E871", {"start": v(0.3, -14.56) * mm, "end": v(0.3, -14.53) * mm});
            skLineSegment(sketch, "E872", {"start": v(0.3, -14.53) * mm, "end": v(0.25, -14.6) * mm});
            skLineSegment(sketch, "E873", {"start": v(0.25, -14.6) * mm, "end": v(-0.26, -15.16) * mm});
            skLineSegment(sketch, "E874", {"start": v(-0.26, -15.16) * mm, "end": v(-0.32, -15.2) * mm});
            skLineSegment(sketch, "E875", {"start": v(-0.32, -15.2) * mm, "end": v(-0.39, -15.25) * mm});
            skLineSegment(sketch, "E876", {"start": v(-0.39, -15.25) * mm, "end": v(-0.74, -15.4) * mm});
            skLineSegment(sketch, "E877", {"start": v(-0.74, -15.4) * mm, "end": v(-1.1, -15.47) * mm});
            skLineSegment(sketch, "E878", {"start": v(-1.1, -15.47) * mm, "end": v(-1.23, -15.47) * mm});
            skLineSegment(sketch, "E879", {"start": v(-1.23, -15.47) * mm, "end": v(-1.43, -15.47) * mm});
            skLineSegment(sketch, "E880", {"start": v(-1.43, -15.47) * mm, "end": v(-2, -15.35) * mm});
            skLineSegment(sketch, "E881", {"start": v(-2, -15.35) * mm, "end": v(-2.5, -15.1) * mm});
            skLineSegment(sketch, "E882", {"start": v(-2.5, -15.1) * mm, "end": v(-2.59, -15.02) * mm});
            skLineSegment(sketch, "E883", {"start": v(-2.59, -15.02) * mm, "end": v(-2.67, -14.95) * mm});
            skLineSegment(sketch, "E884", {"start": v(-2.67, -14.95) * mm, "end": v(-2.95, -14.5) * mm});
            skLineSegment(sketch, "E885", {"start": v(-2.95, -14.5) * mm, "end": v(-3.06, -13.97) * mm});
            skLineSegment(sketch, "E886", {"start": v(-3.06, -13.97) * mm, "end": v(-3.06, -13.79) * mm});
            skLineSegment(sketch, "E887", {"start": v(-3.06, -13.79) * mm, "end": v(-3.06, -13.6) * mm});
            skLineSegment(sketch, "E888", {"start": v(-3.06, -13.6) * mm, "end": v(-2.9, -13.06) * mm});
            skLineSegment(sketch, "E889", {"start": v(-2.9, -13.06) * mm, "end": v(-2.54, -12.59) * mm});
            skLineSegment(sketch, "E890", {"start": v(-2.54, -12.59) * mm, "end": v(-2.43, -12.51) * mm});
            skLineSegment(sketch, "E891", {"start": v(-2.43, -12.51) * mm, "end": v(-2.33, -12.44) * mm});
            skLineSegment(sketch, "E892", {"start": v(-2.33, -12.44) * mm, "end": v(-1.65, -12.17) * mm});
            skLineSegment(sketch, "E893", {"start": v(-1.65, -12.17) * mm, "end": v(-0.85, -12.07) * mm});
            skLineSegment(sketch, "E894", {"start": v(-0.85, -12.07) * mm, "end": v(-0.59, -12.07) * mm});
            skLineSegment(sketch, "E895", {"start": v(-0.59, -12.07) * mm, "end": v(0.26, -12.07) * mm});
            skLineSegment(sketch, "E896", {"start": v(0.26, -12.07) * mm, "end": v(0.26, -11.62) * mm});
            skLineSegment(sketch, "E897", {"start": v(0.26, -11.62) * mm, "end": v(0.26, -11.53) * mm});
            skLineSegment(sketch, "E898", {"start": v(0.26, -11.53) * mm, "end": v(0.2, -11.26) * mm});
            skLineSegment(sketch, "E899", {"start": v(0.2, -11.26) * mm, "end": v(0.08, -11.03) * mm});
            skLineSegment(sketch, "E900", {"start": v(0.08, -11.03) * mm, "end": v(0.05, -10.99) * mm});
            skLineSegment(sketch, "E901", {"start": v(0.05, -10.99) * mm, "end": v(0.01, -10.95) * mm});
            skLineSegment(sketch, "E902", {"start": v(0.01, -10.95) * mm, "end": v(-0.22, -10.82) * mm});
            skLineSegment(sketch, "E903", {"start": v(-0.22, -10.82) * mm, "end": v(-0.5, -10.77) * mm});
            skLineSegment(sketch, "E904", {"start": v(-0.5, -10.77) * mm, "end": v(-0.59, -10.77) * mm});
            skLineSegment(sketch, "E905", {"start": v(-0.59, -10.77) * mm, "end": v(-0.73, -10.77) * mm});
            skLineSegment(sketch, "E906", {"start": v(-0.73, -10.77) * mm, "end": v(-1.12, -10.93) * mm});
            skLineSegment(sketch, "E907", {"start": v(-1.12, -10.93) * mm, "end": v(-1.15, -10.96) * mm});
            skLineSegment(sketch, "E908", {"start": v(-1.15, -10.96) * mm, "end": v(-1.19, -10.99) * mm});
            skLineSegment(sketch, "E909", {"start": v(-1.19, -10.99) * mm, "end": v(-1.3, -11.17) * mm});
            skLineSegment(sketch, "E910", {"start": v(-1.3, -11.17) * mm, "end": v(-1.35, -11.38) * mm});
            skLineSegment(sketch, "E911", {"start": v(-1.35, -11.38) * mm, "end": v(-1.35, -11.45) * mm});
            skLineSegment(sketch, "E912", {"start": v(-1.35, -11.45) * mm, "end": v(-2.82, -11.45) * mm});
            skLineSegment(sketch, "E913", {"start": v(-2.82, -11.45) * mm, "end": v(-2.82, -11.42) * mm});
            skLineSegment(sketch, "E914", {"start": v(-2.82, -11.42) * mm, "end": v(-2.82, -11.3) * mm});
            skLineSegment(sketch, "E915", {"start": v(-2.82, -11.3) * mm, "end": v(-2.68, -10.76) * mm});
            skLineSegment(sketch, "E916", {"start": v(-2.68, -10.76) * mm, "end": v(-2.3, -10.28) * mm});
            skLineSegment(sketch, "E917", {"start": v(-2.3, -10.28) * mm, "end": v(-2.2, -10.19) * mm});
            skLineSegment(sketch, "E918", {"start": v(-2.2, -10.19) * mm, "end": v(-2.1, -10.1) * mm});
            skLineSegment(sketch, "E919", {"start": v(-2.1, -10.1) * mm, "end": v(-1.45, -9.8) * mm});
            skLineSegment(sketch, "E920", {"start": v(-1.45, -9.8) * mm, "end": v(-0.73, -9.68) * mm});
            skLineSegment(sketch, "E921", {"start": v(-0.73, -9.68) * mm, "end": v(-0.5, -9.68) * mm});
            skLineSegment(sketch, "E922", {"start": v(-0.5, -9.68) * mm, "end": v(-0.27, -9.68) * mm});
            skLineSegment(sketch, "E923", {"start": v(-0.27, -9.68) * mm, "end": v(0.42, -9.8) * mm});
            skLineSegment(sketch, "E924", {"start": v(0.42, -9.8) * mm, "end": v(1.03, -10.1) * mm});
            skLineSegment(sketch, "E925", {"start": v(1.03, -10.1) * mm, "end": v(1.14, -10.19) * mm});
            skLineSegment(sketch, "E926", {"start": v(1.14, -10.19) * mm, "end": v(1.24, -10.27) * mm});
            skLineSegment(sketch, "E927", {"start": v(1.24, -10.27) * mm, "end": v(1.6, -10.8) * mm});
            skLineSegment(sketch, "E928", {"start": v(1.6, -10.8) * mm, "end": v(1.77, -11.43) * mm});
            skLineSegment(sketch, "E929", {"start": v(1.77, -11.43) * mm, "end": v(1.77, -11.63) * mm});
            skLineSegment(sketch, "E930", {"start": v(1.77, -11.63) * mm, "end": v(1.77, -13.94) * mm});
            skLineSegment(sketch, "E931", {"start": v(1.77, -13.94) * mm, "end": v(1.77, -14.13) * mm});
            skLineSegment(sketch, "E932", {"start": v(1.77, -14.13) * mm, "end": v(1.82, -14.63) * mm});
            skLineSegment(sketch, "E933", {"start": v(1.82, -14.63) * mm, "end": v(1.83, -14.68) * mm});
            skLineSegment(sketch, "E934", {"start": v(1.83, -14.68) * mm, "end": v(1.84, -14.74) * mm});
            skLineSegment(sketch, "E935", {"start": v(1.84, -14.74) * mm, "end": v(2, -15.32) * mm});
            skLineSegment(sketch, "E936", {"start": v(2, -15.32) * mm, "end": v(2.02, -15.38) * mm});
            skLineSegment(sketch, "E937", {"start": v(2.02, -15.38) * mm, "end": v(0.52, -15.38) * mm});
            skLineSegment(sketch, "E938", {"start": v(0.52, -15.38) * mm, "end": v(0.52, -15.36) * mm});
            skLineSegment(sketch, "E939", {"start": v(-0.86, -14.34) * mm, "end": v(-0.69, -14.34) * mm});
            skLineSegment(sketch, "E940", {"start": v(-0.69, -14.34) * mm, "end": v(-0.2, -14.18) * mm});
            skLineSegment(sketch, "E941", {"start": v(-0.2, -14.18) * mm, "end": v(-0.15, -14.14) * mm});
            skLineSegment(sketch, "E942", {"start": v(-0.15, -14.14) * mm, "end": v(-0.1, -14.1) * mm});
            skLineSegment(sketch, "E943", {"start": v(-0.1, -14.1) * mm, "end": v(0.1, -13.93) * mm});
            skLineSegment(sketch, "E944", {"start": v(0.1, -13.93) * mm, "end": v(0.25, -13.73) * mm});
            skLineSegment(sketch, "E945", {"start": v(0.25, -13.73) * mm, "end": v(0.26, -13.68) * mm});
            skLineSegment(sketch, "E946", {"start": v(0.26, -13.68) * mm, "end": v(0.26, -12.9) * mm});
            skLineSegment(sketch, "E947", {"start": v(0.26, -12.9) * mm, "end": v(-0.59, -12.9) * mm});
            skLineSegment(sketch, "E948", {"start": v(-0.59, -12.9) * mm, "end": v(-0.7, -12.9) * mm});
            skLineSegment(sketch, "E949", {"start": v(-0.7, -12.9) * mm, "end": v(-1.01, -12.96) * mm});
            skLineSegment(sketch, "E950", {"start": v(-1.01, -12.96) * mm, "end": v(-1.27, -13.1) * mm});
            skLineSegment(sketch, "E951", {"start": v(-1.27, -13.1) * mm, "end": v(-1.3, -13.14) * mm});
            skLineSegment(sketch, "E952", {"start": v(-1.3, -13.14) * mm, "end": v(-1.35, -13.19) * mm});
            skLineSegment(sketch, "E953", {"start": v(-1.35, -13.19) * mm, "end": v(-1.49, -13.41) * mm});
            skLineSegment(sketch, "E954", {"start": v(-1.49, -13.41) * mm, "end": v(-1.55, -13.65) * mm});
            skLineSegment(sketch, "E955", {"start": v(-1.55, -13.65) * mm, "end": v(-1.55, -13.73) * mm});
            skLineSegment(sketch, "E956", {"start": v(-1.55, -13.73) * mm, "end": v(-1.55, -13.84) * mm});
            skLineSegment(sketch, "E957", {"start": v(-1.55, -13.84) * mm, "end": v(-1.4, -14.15) * mm});
            skLineSegment(sketch, "E958", {"start": v(-1.4, -14.15) * mm, "end": v(-1.37, -14.17) * mm});
            skLineSegment(sketch, "E959", {"start": v(-1.37, -14.17) * mm, "end": v(-1.34, -14.2) * mm});
            skLineSegment(sketch, "E960", {"start": v(-1.34, -14.2) * mm, "end": v(-0.98, -14.34) * mm});
            skLineSegment(sketch, "E961", {"start": v(-0.98, -14.34) * mm, "end": v(-0.86, -14.34) * mm});
            skLineSegment(sketch, "E962", {"start": v(-1.23, -16.08) * mm, "end": v(-1.48, -16.08) * mm});
            skLineSegment(sketch, "E963", {"start": v(-1.48, -16.08) * mm, "end": v(-2.24, -15.92) * mm});
            skLineSegment(sketch, "E964", {"start": v(-2.24, -15.92) * mm, "end": v(-2.9, -15.57) * mm});
            skLineSegment(sketch, "E965", {"start": v(-2.9, -15.57) * mm, "end": v(-3.02, -15.47) * mm});
            skLineSegment(sketch, "E966", {"start": v(-3.02, -15.47) * mm, "end": v(-3.13, -15.36) * mm});
            skLineSegment(sketch, "E967", {"start": v(-3.13, -15.36) * mm, "end": v(-3.52, -14.73) * mm});
            skLineSegment(sketch, "E968", {"start": v(-3.52, -14.73) * mm, "end": v(-3.68, -14.02) * mm});
            skLineSegment(sketch, "E969", {"start": v(-3.68, -14.02) * mm, "end": v(-3.68, -13.79) * mm});
            skLineSegment(sketch, "E970", {"start": v(-3.68, -13.79) * mm, "end": v(-3.68, -13.54) * mm});
            skLineSegment(sketch, "E971", {"start": v(-3.68, -13.54) * mm, "end": v(-3.46, -12.8) * mm});
            skLineSegment(sketch, "E972", {"start": v(-3.46, -12.8) * mm, "end": v(-2.97, -12.15) * mm});
            skLineSegment(sketch, "E973", {"start": v(-2.97, -12.15) * mm, "end": v(-2.83, -12.05) * mm});
            skLineSegment(sketch, "E974", {"start": v(-2.83, -12.05) * mm, "end": v(-3.3, -12.05) * mm});
            skLineSegment(sketch, "E975", {"start": v(-3.3, -12.05) * mm, "end": v(-3.4, -11.43) * mm});
            skLineSegment(sketch, "E976", {"start": v(-3.4, -11.43) * mm, "end": v(-3.4, -11.34) * mm});
            skLineSegment(sketch, "E977", {"start": v(-3.4, -11.34) * mm, "end": v(-3.39, -11.05) * mm});
            skLineSegment(sketch, "E978", {"start": v(-3.39, -11.05) * mm, "end": v(-3.27, -10.61) * mm});
            skLineSegment(sketch, "E979", {"start": v(-3.27, -10.61) * mm, "end": v(-3, -10.15) * mm});
            skLineSegment(sketch, "E980", {"start": v(-3, -10.15) * mm, "end": v(-2.68, -9.8) * mm});
            skLineSegment(sketch, "E981", {"start": v(-2.68, -9.8) * mm, "end": v(-2.55, -9.7) * mm});
            skLineSegment(sketch, "E982", {"start": v(-2.55, -9.7) * mm, "end": v(-2.42, -9.59) * mm});
            skLineSegment(sketch, "E983", {"start": v(-2.42, -9.59) * mm, "end": v(-1.62, -9.21) * mm});
            skLineSegment(sketch, "E984", {"start": v(-1.62, -9.21) * mm, "end": v(-0.75, -9.05) * mm});
            skLineSegment(sketch, "E985", {"start": v(-0.75, -9.05) * mm, "end": v(-0.46, -9.05) * mm});
            skLineSegment(sketch, "E986", {"start": v(-0.46, -9.05) * mm, "end": v(-0.18, -9.05) * mm});
            skLineSegment(sketch, "E987", {"start": v(-0.18, -9.05) * mm, "end": v(0.66, -9.21) * mm});
            skLineSegment(sketch, "E988", {"start": v(0.66, -9.21) * mm, "end": v(1.42, -9.59) * mm});
            skLineSegment(sketch, "E989", {"start": v(1.42, -9.59) * mm, "end": v(1.55, -9.7) * mm});
            skLineSegment(sketch, "E990", {"start": v(1.55, -9.7) * mm, "end": v(1.7, -9.81) * mm});
            skLineSegment(sketch, "E991", {"start": v(1.7, -9.81) * mm, "end": v(2.2, -10.52) * mm});
            skLineSegment(sketch, "E992", {"start": v(2.2, -10.52) * mm, "end": v(2.4, -11.35) * mm});
            skLineSegment(sketch, "E993", {"start": v(2.4, -11.35) * mm, "end": v(2.4, -11.62) * mm});
            skLineSegment(sketch, "E994", {"start": v(2.4, -11.62) * mm, "end": v(2.4, -13.93) * mm});
            skLineSegment(sketch, "E995", {"start": v(2.4, -13.93) * mm, "end": v(2.4, -14.09) * mm});
            skLineSegment(sketch, "E996", {"start": v(2.4, -14.09) * mm, "end": v(2.44, -14.51) * mm});
            skLineSegment(sketch, "E997", {"start": v(2.44, -14.51) * mm, "end": v(2.45, -14.56) * mm});
            skLineSegment(sketch, "E998", {"start": v(2.45, -14.56) * mm, "end": v(2.45, -14.6) * mm});
            skLineSegment(sketch, "E999", {"start": v(2.45, -14.6) * mm, "end": v(2.58, -15.08) * mm});
            skLineSegment(sketch, "E1000", {"start": v(2.58, -15.08) * mm, "end": v(2.6, -15.13) * mm});
            skLineSegment(sketch, "E1001", {"start": v(2.6, -15.13) * mm, "end": v(2.92, -15.96) * mm});
            skLineSegment(sketch, "E1002", {"start": v(2.92, -15.96) * mm, "end": v(0.12, -15.96) * mm});
            skLineSegment(sketch, "E1003", {"start": v(0.12, -15.96) * mm, "end": v(0.02, -15.71) * mm});
            skLineSegment(sketch, "E1004", {"start": v(0.02, -15.71) * mm, "end": v(-0.08, -15.77) * mm});
            skLineSegment(sketch, "E1005", {"start": v(-0.08, -15.77) * mm, "end": v(-0.57, -16) * mm});
            skLineSegment(sketch, "E1006", {"start": v(-0.57, -16) * mm, "end": v(-1.07, -16.08) * mm});
            skLineSegment(sketch, "E1007", {"start": v(-1.07, -16.08) * mm, "end": v(-1.23, -16.08) * mm});
            skLineSegment(sketch, "E1008", {"start": v(-0.94, -13.73) * mm, "end": v(-0.86, -13.73) * mm});
            skLineSegment(sketch, "E1009", {"start": v(-0.86, -13.73) * mm, "end": v(-0.77, -13.73) * mm});
            skLineSegment(sketch, "E1010", {"start": v(-0.77, -13.73) * mm, "end": v(-0.5, -13.64) * mm});
            skLineSegment(sketch, "E1011", {"start": v(-0.5, -13.64) * mm, "end": v(-0.48, -13.62) * mm});
            skLineSegment(sketch, "E1012", {"start": v(-0.48, -13.62) * mm, "end": v(-0.46, -13.61) * mm});
            skLineSegment(sketch, "E1013", {"start": v(-0.46, -13.61) * mm, "end": v(-0.35, -13.52) * mm});
            skLineSegment(sketch, "E1014", {"start": v(-0.35, -13.52) * mm, "end": v(-0.34, -13.51) * mm});
            skLineSegment(sketch, "E1015", {"start": v(-0.34, -13.51) * mm, "end": v(-0.57, -13.51) * mm});
            skLineSegment(sketch, "E1016", {"start": v(-0.57, -13.51) * mm, "end": v(-0.65, -13.51) * mm});
            skLineSegment(sketch, "E1017", {"start": v(-0.65, -13.51) * mm, "end": v(-0.87, -13.57) * mm});
            skLineSegment(sketch, "E1018", {"start": v(-0.87, -13.57) * mm, "end": v(-0.88, -13.57) * mm});
            skLineSegment(sketch, "E1019", {"start": v(-0.88, -13.57) * mm, "end": v(-0.89, -13.59) * mm});
            skLineSegment(sketch, "E1020", {"start": v(-0.89, -13.59) * mm, "end": v(-0.94, -13.7) * mm});
            skLineSegment(sketch, "E1021", {"start": v(-0.94, -13.7) * mm, "end": v(-0.94, -13.73) * mm});
            skLineSegment(sketch, "E1022", {"start": v(-0.72, -11.39) * mm, "end": v(-0.72, -11.42) * mm});
            skLineSegment(sketch, "E1023", {"start": v(-0.72, -11.42) * mm, "end": v(-0.38, -11.42) * mm});
            skLineSegment(sketch, "E1024", {"start": v(-0.38, -11.42) * mm, "end": v(-0.38, -11.41) * mm});
            skLineSegment(sketch, "E1025", {"start": v(-0.38, -11.41) * mm, "end": v(-0.4, -11.39) * mm});
            skLineSegment(sketch, "E1026", {"start": v(-0.4, -11.39) * mm, "end": v(-0.54, -11.36) * mm});
            skLineSegment(sketch, "E1027", {"start": v(-0.54, -11.36) * mm, "end": v(-0.59, -11.36) * mm});
            skLineSegment(sketch, "E1028", {"start": v(-0.59, -11.36) * mm, "end": v(-0.6, -11.36) * mm});
            skLineSegment(sketch, "E1029", {"start": v(-0.6, -11.36) * mm, "end": v(-0.7, -11.39) * mm});
            skLineSegment(sketch, "E1030", {"start": v(-0.7, -11.39) * mm, "end": v(-0.72, -11.39) * mm});
            skLineSegment(sketch, "E1031", {"start": v(7.97, -12.71) * mm, "end": v(7.97, -13) * mm});
            skLineSegment(sketch, "E1032", {"start": v(7.97, -13) * mm, "end": v(7.83, -13.84) * mm});
            skLineSegment(sketch, "E1033", {"start": v(7.83, -13.84) * mm, "end": v(7.5, -14.59) * mm});
            skLineSegment(sketch, "E1034", {"start": v(7.5, -14.59) * mm, "end": v(7.42, -14.71) * mm});
            skLineSegment(sketch, "E1035", {"start": v(7.42, -14.71) * mm, "end": v(7.32, -14.84) * mm});
            skLineSegment(sketch, "E1036", {"start": v(7.32, -14.84) * mm, "end": v(6.74, -15.27) * mm});
            skLineSegment(sketch, "E1037", {"start": v(6.74, -15.27) * mm, "end": v(6.04, -15.47) * mm});
            skLineSegment(sketch, "E1038", {"start": v(6.04, -15.47) * mm, "end": v(5.8, -15.47) * mm});
            skLineSegment(sketch, "E1039", {"start": v(5.8, -15.47) * mm, "end": v(5.69, -15.47) * mm});
            skLineSegment(sketch, "E1040", {"start": v(5.69, -15.47) * mm, "end": v(5.34, -15.42) * mm});
            skLineSegment(sketch, "E1041", {"start": v(5.34, -15.42) * mm, "end": v(5.01, -15.3) * mm});
            skLineSegment(sketch, "E1042", {"start": v(5.01, -15.3) * mm, "end": v(4.96, -15.27) * mm});
            skLineSegment(sketch, "E1043", {"start": v(4.96, -15.27) * mm, "end": v(4.9, -15.23) * mm});
            skLineSegment(sketch, "E1044", {"start": v(4.9, -15.23) * mm, "end": v(4.38, -14.73) * mm});
            skLineSegment(sketch, "E1045", {"start": v(4.38, -14.73) * mm, "end": v(4.34, -14.67) * mm});
            skLineSegment(sketch, "E1046", {"start": v(4.34, -14.67) * mm, "end": v(4.23, -15.36) * mm});
            skLineSegment(sketch, "E1047", {"start": v(4.23, -15.36) * mm, "end": v(2.94, -15.36) * mm});
            skLineSegment(sketch, "E1048", {"start": v(2.94, -15.36) * mm, "end": v(2.94, -7.3) * mm});
            skLineSegment(sketch, "E1049", {"start": v(2.94, -7.3) * mm, "end": v(4.45, -7.3) * mm});
            skLineSegment(sketch, "E1050", {"start": v(4.45, -7.3) * mm, "end": v(4.45, -10.36) * mm});
            skLineSegment(sketch, "E1051", {"start": v(4.45, -10.36) * mm, "end": v(4.49, -10.3) * mm});
            skLineSegment(sketch, "E1052", {"start": v(4.49, -10.3) * mm, "end": v(4.97, -9.87) * mm});
            skLineSegment(sketch, "E1053", {"start": v(4.97, -9.87) * mm, "end": v(5.03, -9.83) * mm});
            skLineSegment(sketch, "E1054", {"start": v(5.03, -9.83) * mm, "end": v(5.1, -9.8) * mm});
            skLineSegment(sketch, "E1055", {"start": v(5.1, -9.8) * mm, "end": v(5.64, -9.65) * mm});
            skLineSegment(sketch, "E1056", {"start": v(5.64, -9.65) * mm, "end": v(5.82, -9.65) * mm});
            skLineSegment(sketch, "E1057", {"start": v(5.82, -9.65) * mm, "end": v(6.05, -9.65) * mm});
            skLineSegment(sketch, "E1058", {"start": v(6.05, -9.65) * mm, "end": v(6.75, -9.85) * mm});
            skLineSegment(sketch, "E1059", {"start": v(6.75, -9.85) * mm, "end": v(7.35, -10.32) * mm});
            skLineSegment(sketch, "E1060", {"start": v(7.35, -10.32) * mm, "end": v(7.45, -10.45) * mm});
            skLineSegment(sketch, "E1061", {"start": v(7.45, -10.45) * mm, "end": v(7.54, -10.58) * mm});
            skLineSegment(sketch, "E1062", {"start": v(7.54, -10.58) * mm, "end": v(7.86, -11.39) * mm});
            skLineSegment(sketch, "E1063", {"start": v(7.86, -11.39) * mm, "end": v(8, -12.29) * mm});
            skLineSegment(sketch, "E1064", {"start": v(8, -12.29) * mm, "end": v(8, -12.59) * mm});
            skLineSegment(sketch, "E1065", {"start": v(8, -12.59) * mm, "end": v(8, -12.71) * mm});
            skLineSegment(sketch, "E1066", {"start": v(8, -12.71) * mm, "end": v(7.97, -12.71) * mm});
            skLineSegment(sketch, "E1067", {"start": v(6.46, -12.6) * mm, "end": v(6.46, -12.42) * mm});
            skLineSegment(sketch, "E1068", {"start": v(6.46, -12.42) * mm, "end": v(6.4, -11.86) * mm});
            skLineSegment(sketch, "E1069", {"start": v(6.4, -11.86) * mm, "end": v(6.26, -11.38) * mm});
            skLineSegment(sketch, "E1070", {"start": v(6.26, -11.38) * mm, "end": v(6.22, -11.3) * mm});
            skLineSegment(sketch, "E1071", {"start": v(6.22, -11.3) * mm, "end": v(6.18, -11.22) * mm});
            skLineSegment(sketch, "E1072", {"start": v(6.18, -11.22) * mm, "end": v(5.9, -10.94) * mm});
            skLineSegment(sketch, "E1073", {"start": v(5.9, -10.94) * mm, "end": v(5.53, -10.82) * mm});
            skLineSegment(sketch, "E1074", {"start": v(5.53, -10.82) * mm, "end": v(5.4, -10.82) * mm});
            skLineSegment(sketch, "E1075", {"start": v(5.4, -10.82) * mm, "end": v(5.25, -10.82) * mm});
            skLineSegment(sketch, "E1076", {"start": v(5.25, -10.82) * mm, "end": v(4.84, -10.95) * mm});
            skLineSegment(sketch, "E1077", {"start": v(4.84, -10.95) * mm, "end": v(4.8, -10.97) * mm});
            skLineSegment(sketch, "E1078", {"start": v(4.8, -10.97) * mm, "end": v(4.76, -11) * mm});
            skLineSegment(sketch, "E1079", {"start": v(4.76, -11) * mm, "end": v(4.44, -11.36) * mm});
            skLineSegment(sketch, "E1080", {"start": v(4.44, -11.36) * mm, "end": v(4.42, -11.4) * mm});
            skLineSegment(sketch, "E1081", {"start": v(4.42, -11.4) * mm, "end": v(4.42, -13.79) * mm});
            skLineSegment(sketch, "E1082", {"start": v(4.42, -13.79) * mm, "end": v(4.44, -13.83) * mm});
            skLineSegment(sketch, "E1083", {"start": v(4.44, -13.83) * mm, "end": v(4.76, -14.16) * mm});
            skLineSegment(sketch, "E1084", {"start": v(4.76, -14.16) * mm, "end": v(4.8, -14.17) * mm});
            skLineSegment(sketch, "E1085", {"start": v(4.8, -14.17) * mm, "end": v(4.84, -14.2) * mm});
            skLineSegment(sketch, "E1086", {"start": v(4.84, -14.2) * mm, "end": v(5.26, -14.31) * mm});
            skLineSegment(sketch, "E1087", {"start": v(5.26, -14.31) * mm, "end": v(5.4, -14.31) * mm});
            skLineSegment(sketch, "E1088", {"start": v(5.4, -14.31) * mm, "end": v(5.53, -14.31) * mm});
            skLineSegment(sketch, "E1089", {"start": v(5.53, -14.31) * mm, "end": v(5.9, -14.2) * mm});
            skLineSegment(sketch, "E1090", {"start": v(5.9, -14.2) * mm, "end": v(6.18, -13.97) * mm});
            skLineSegment(sketch, "E1091", {"start": v(6.18, -13.97) * mm, "end": v(6.22, -13.9) * mm});
            skLineSegment(sketch, "E1092", {"start": v(6.22, -13.9) * mm, "end": v(6.26, -13.83) * mm});
            skLineSegment(sketch, "E1093", {"start": v(6.26, -13.83) * mm, "end": v(6.4, -13.4) * mm});
            skLineSegment(sketch, "E1094", {"start": v(6.4, -13.4) * mm, "end": v(6.45, -12.9) * mm});
            skLineSegment(sketch, "E1095", {"start": v(6.45, -12.9) * mm, "end": v(6.45, -12.73) * mm});
            skLineSegment(sketch, "E1096", {"start": v(6.45, -12.73) * mm, "end": v(6.45, -12.6) * mm});
            skLineSegment(sketch, "E1097", {"start": v(6.45, -12.6) * mm, "end": v(6.46, -12.6) * mm});
            skLineSegment(sketch, "E1098", {"start": v(5.8, -16.08) * mm, "end": v(5.54, -16.08) * mm});
            skLineSegment(sketch, "E1099", {"start": v(5.54, -16.08) * mm, "end": v(4.83, -15.9) * mm});
            skLineSegment(sketch, "E1100", {"start": v(4.83, -15.9) * mm, "end": v(4.76, -15.85) * mm});
            skLineSegment(sketch, "E1101", {"start": v(4.76, -15.85) * mm, "end": v(4.74, -15.97) * mm});
            skLineSegment(sketch, "E1102", {"start": v(4.74, -15.97) * mm, "end": v(2.3, -15.97) * mm});
            skLineSegment(sketch, "E1103", {"start": v(2.3, -15.97) * mm, "end": v(2.3, -6.68) * mm});
            skLineSegment(sketch, "E1104", {"start": v(2.3, -6.68) * mm, "end": v(5.05, -6.68) * mm});
            skLineSegment(sketch, "E1105", {"start": v(5.05, -6.68) * mm, "end": v(5.05, -9.16) * mm});
            skLineSegment(sketch, "E1106", {"start": v(5.05, -9.16) * mm, "end": v(5.1, -9.14) * mm});
            skLineSegment(sketch, "E1107", {"start": v(5.1, -9.14) * mm, "end": v(5.62, -9.05) * mm});
            skLineSegment(sketch, "E1108", {"start": v(5.62, -9.05) * mm, "end": v(5.79, -9.05) * mm});
            skLineSegment(sketch, "E1109", {"start": v(5.79, -9.05) * mm, "end": v(5.95, -9.05) * mm});
            skLineSegment(sketch, "E1110", {"start": v(5.95, -9.05) * mm, "end": v(6.43, -9.12) * mm});
            skLineSegment(sketch, "E1111", {"start": v(6.43, -9.12) * mm, "end": v(7, -9.32) * mm});
            skLineSegment(sketch, "E1112", {"start": v(7, -9.32) * mm, "end": v(7.5, -9.65) * mm});
            skLineSegment(sketch, "E1113", {"start": v(7.5, -9.65) * mm, "end": v(7.82, -9.99) * mm});
            skLineSegment(sketch, "E1114", {"start": v(7.82, -9.99) * mm, "end": v(7.91, -10.11) * mm});
            skLineSegment(sketch, "E1115", {"start": v(7.91, -10.11) * mm, "end": v(8.02, -10.27) * mm});
            skLineSegment(sketch, "E1116", {"start": v(8.02, -10.27) * mm, "end": v(8.4, -11.22) * mm});
            skLineSegment(sketch, "E1117", {"start": v(8.4, -11.22) * mm, "end": v(8.57, -12.26) * mm});
            skLineSegment(sketch, "E1118", {"start": v(8.57, -12.26) * mm, "end": v(8.57, -12.6) * mm});
            skLineSegment(sketch, "E1119", {"start": v(8.57, -12.6) * mm, "end": v(8.57, -12.71) * mm});
            skLineSegment(sketch, "E1120", {"start": v(8.57, -12.71) * mm, "end": v(8.57, -13.04) * mm});
            skLineSegment(sketch, "E1121", {"start": v(8.57, -13.04) * mm, "end": v(8.4, -14.04) * mm});
            skLineSegment(sketch, "E1122", {"start": v(8.4, -14.04) * mm, "end": v(8, -14.93) * mm});
            skLineSegment(sketch, "E1123", {"start": v(8, -14.93) * mm, "end": v(7.9, -15.08) * mm});
            skLineSegment(sketch, "E1124", {"start": v(7.9, -15.08) * mm, "end": v(7.8, -15.2) * mm});
            skLineSegment(sketch, "E1125", {"start": v(7.8, -15.2) * mm, "end": v(7.5, -15.51) * mm});
            skLineSegment(sketch, "E1126", {"start": v(7.5, -15.51) * mm, "end": v(7, -15.82) * mm});
            skLineSegment(sketch, "E1127", {"start": v(7, -15.82) * mm, "end": v(6.44, -16.02) * mm});
            skLineSegment(sketch, "E1128", {"start": v(6.44, -16.02) * mm, "end": v(5.96, -16.08) * mm});
            skLineSegment(sketch, "E1129", {"start": v(5.96, -16.08) * mm, "end": v(5.8, -16.08) * mm});
            skLineSegment(sketch, "E1130", {"start": v(5.05, -13.57) * mm, "end": v(5.05, -13.58) * mm});
            skLineSegment(sketch, "E1131", {"start": v(5.05, -13.58) * mm, "end": v(5.1, -13.62) * mm});
            skLineSegment(sketch, "E1132", {"start": v(5.1, -13.62) * mm, "end": v(5.1, -13.62) * mm});
            skLineSegment(sketch, "E1133", {"start": v(5.1, -13.62) * mm, "end": v(5.13, -13.63) * mm});
            skLineSegment(sketch, "E1134", {"start": v(5.13, -13.63) * mm, "end": v(5.35, -13.68) * mm});
            skLineSegment(sketch, "E1135", {"start": v(5.35, -13.68) * mm, "end": v(5.42, -13.68) * mm});
            skLineSegment(sketch, "E1136", {"start": v(5.42, -13.68) * mm, "end": v(5.47, -13.68) * mm});
            skLineSegment(sketch, "E1137", {"start": v(5.47, -13.68) * mm, "end": v(5.64, -13.65) * mm});
            skLineSegment(sketch, "E1138", {"start": v(5.64, -13.65) * mm, "end": v(5.7, -13.6) * mm});
            skLineSegment(sketch, "E1139", {"start": v(5.7, -13.6) * mm, "end": v(5.7, -13.59) * mm});
            skLineSegment(sketch, "E1140", {"start": v(5.7, -13.59) * mm, "end": v(5.71, -13.56) * mm});
            skLineSegment(sketch, "E1141", {"start": v(5.71, -13.56) * mm, "end": v(5.8, -13.29) * mm});
            skLineSegment(sketch, "E1142", {"start": v(5.8, -13.29) * mm, "end": v(5.85, -12.86) * mm});
            skLineSegment(sketch, "E1143", {"start": v(5.85, -12.86) * mm, "end": v(5.85, -12.71) * mm});
            skLineSegment(sketch, "E1144", {"start": v(5.85, -12.71) * mm, "end": v(5.85, -12.6) * mm});
            skLineSegment(sketch, "E1145", {"start": v(5.85, -12.6) * mm, "end": v(5.85, -12.45) * mm});
            skLineSegment(sketch, "E1146", {"start": v(5.85, -12.45) * mm, "end": v(5.8, -12) * mm});
            skLineSegment(sketch, "E1147", {"start": v(5.8, -12) * mm, "end": v(5.7, -11.63) * mm});
            skLineSegment(sketch, "E1148", {"start": v(5.7, -11.63) * mm, "end": v(5.68, -11.57) * mm});
            skLineSegment(sketch, "E1149", {"start": v(5.68, -11.57) * mm, "end": v(5.67, -11.55) * mm});
            skLineSegment(sketch, "E1150", {"start": v(5.67, -11.55) * mm, "end": v(5.6, -11.47) * mm});
            skLineSegment(sketch, "E1151", {"start": v(5.6, -11.47) * mm, "end": v(5.45, -11.43) * mm});
            skLineSegment(sketch, "E1152", {"start": v(5.45, -11.43) * mm, "end": v(5.4, -11.43) * mm});
            skLineSegment(sketch, "E1153", {"start": v(5.4, -11.43) * mm, "end": v(5.33, -11.43) * mm});
            skLineSegment(sketch, "E1154", {"start": v(5.33, -11.43) * mm, "end": v(5.14, -11.48) * mm});
            skLineSegment(sketch, "E1155", {"start": v(5.14, -11.48) * mm, "end": v(5.12, -11.5) * mm});
            skLineSegment(sketch, "E1156", {"start": v(5.12, -11.5) * mm, "end": v(5.12, -11.5) * mm});
            skLineSegment(sketch, "E1157", {"start": v(5.12, -11.5) * mm, "end": v(5.04, -11.57) * mm});
            skLineSegment(sketch, "E1158", {"start": v(5.04, -11.57) * mm, "end": v(5.03, -11.57) * mm});
            skLineSegment(sketch, "E1159", {"start": v(5.03, -11.57) * mm, "end": v(5.03, -13.57) * mm});
            skLineSegment(sketch, "E1160", {"start": v(5.03, -13.57) * mm, "end": v(5.05, -13.57) * mm});
            skLineSegment(sketch, "E1161", {"start": v(-14.24, 1.12) * mm, "end": v(-14.24, -0.25) * mm});
            skLineSegment(sketch, "E1162", {"start": v(-14.24, -0.25) * mm, "end": v(-13.3, -0.25) * mm});
            skLineSegment(sketch, "E1163", {"start": v(-13.3, -0.25) * mm, "end": v(-13.3, -1.3) * mm});
            skLineSegment(sketch, "E1164", {"start": v(-13.3, -1.3) * mm, "end": v(-14.24, -1.3) * mm});
            skLineSegment(sketch, "E1165", {"start": v(-14.24, -1.3) * mm, "end": v(-14.24, -4.16) * mm});
            skLineSegment(sketch, "E1166", {"start": v(-14.24, -4.16) * mm, "end": v(-14.24, -4.27) * mm});
            skLineSegment(sketch, "E1167", {"start": v(-14.24, -4.27) * mm, "end": v(-14.12, -4.6) * mm});
            skLineSegment(sketch, "E1168", {"start": v(-14.12, -4.6) * mm, "end": v(-14.1, -4.62) * mm});
            skLineSegment(sketch, "E1169", {"start": v(-14.1, -4.62) * mm, "end": v(-14.08, -4.64) * mm});
            skLineSegment(sketch, "E1170", {"start": v(-14.08, -4.64) * mm, "end": v(-13.82, -4.76) * mm});
            skLineSegment(sketch, "E1171", {"start": v(-13.82, -4.76) * mm, "end": v(-13.73, -4.76) * mm});
            skLineSegment(sketch, "E1172", {"start": v(-13.73, -4.76) * mm, "end": v(-13.68, -4.76) * mm});
            skLineSegment(sketch, "E1173", {"start": v(-13.68, -4.76) * mm, "end": v(-13.54, -4.74) * mm});
            skLineSegment(sketch, "E1174", {"start": v(-13.54, -4.74) * mm, "end": v(-13.53, -4.74) * mm});
            skLineSegment(sketch, "E1175", {"start": v(-13.53, -4.74) * mm, "end": v(-13.51, -4.74) * mm});
            skLineSegment(sketch, "E1176", {"start": v(-13.51, -4.74) * mm, "end": v(-13.35, -4.7) * mm});
            skLineSegment(sketch, "E1177", {"start": v(-13.35, -4.7) * mm, "end": v(-13.33, -4.7) * mm});
            skLineSegment(sketch, "E1178", {"start": v(-13.33, -4.7) * mm, "end": v(-13.2, -5.79) * mm});
            skLineSegment(sketch, "E1179", {"start": v(-13.2, -5.79) * mm, "end": v(-13.24, -5.8) * mm});
            skLineSegment(sketch, "E1180", {"start": v(-13.24, -5.8) * mm, "end": v(-13.62, -5.9) * mm});
            skLineSegment(sketch, "E1181", {"start": v(-13.62, -5.9) * mm, "end": v(-13.65, -5.91) * mm});
            skLineSegment(sketch, "E1182", {"start": v(-13.65, -5.91) * mm, "end": v(-13.69, -5.92) * mm});
            skLineSegment(sketch, "E1183", {"start": v(-13.69, -5.92) * mm, "end": v(-14.02, -5.96) * mm});
            skLineSegment(sketch, "E1184", {"start": v(-14.02, -5.96) * mm, "end": v(-14.13, -5.96) * mm});
            skLineSegment(sketch, "E1185", {"start": v(-14.13, -5.96) * mm, "end": v(-14.3, -5.96) * mm});
            skLineSegment(sketch, "E1186", {"start": v(-14.3, -5.96) * mm, "end": v(-14.82, -5.85) * mm});
            skLineSegment(sketch, "E1187", {"start": v(-14.82, -5.85) * mm, "end": v(-15.26, -5.6) * mm});
            skLineSegment(sketch, "E1188", {"start": v(-15.26, -5.6) * mm, "end": v(-15.33, -5.53) * mm});
            skLineSegment(sketch, "E1189", {"start": v(-15.33, -5.53) * mm, "end": v(-15.4, -5.45) * mm});
            skLineSegment(sketch, "E1190", {"start": v(-15.4, -5.45) * mm, "end": v(-15.64, -4.97) * mm});
            skLineSegment(sketch, "E1191", {"start": v(-15.64, -4.97) * mm, "end": v(-15.74, -4.37) * mm});
            skLineSegment(sketch, "E1192", {"start": v(-15.74, -4.37) * mm, "end": v(-15.74, -4.17) * mm});
            skLineSegment(sketch, "E1193", {"start": v(-15.74, -4.17) * mm, "end": v(-15.74, -1.3) * mm});
            skLineSegment(sketch, "E1194", {"start": v(-15.74, -1.3) * mm, "end": v(-16.56, -1.3) * mm});
            skLineSegment(sketch, "E1195", {"start": v(-16.56, -1.3) * mm, "end": v(-16.56, -0.25) * mm});
            skLineSegment(sketch, "E1196", {"start": v(-16.56, -0.25) * mm, "end": v(-15.74, -0.25) * mm});
            skLineSegment(sketch, "E1197", {"start": v(-15.74, -0.25) * mm, "end": v(-15.74, 1.12) * mm});
            skLineSegment(sketch, "E1198", {"start": v(-15.74, 1.12) * mm, "end": v(-14.24, 1.12) * mm});
            skLineSegment(sketch, "E1199", {"start": v(-14.11, -6.57) * mm, "end": v(-14.35, -6.57) * mm});
            skLineSegment(sketch, "E1200", {"start": v(-14.35, -6.57) * mm, "end": v(-15.05, -6.42) * mm});
            skLineSegment(sketch, "E1201", {"start": v(-15.05, -6.42) * mm, "end": v(-15.66, -6.06) * mm});
            skLineSegment(sketch, "E1202", {"start": v(-15.66, -6.06) * mm, "end": v(-15.76, -5.96) * mm});
            skLineSegment(sketch, "E1203", {"start": v(-15.76, -5.96) * mm, "end": v(-15.86, -5.86) * mm});
            skLineSegment(sketch, "E1204", {"start": v(-15.86, -5.86) * mm, "end": v(-16.21, -5.2) * mm});
            skLineSegment(sketch, "E1205", {"start": v(-16.21, -5.2) * mm, "end": v(-16.36, -4.43) * mm});
            skLineSegment(sketch, "E1206", {"start": v(-16.36, -4.43) * mm, "end": v(-16.36, -4.17) * mm});
            skLineSegment(sketch, "E1207", {"start": v(-16.36, -4.17) * mm, "end": v(-16.36, -1.92) * mm});
            skLineSegment(sketch, "E1208", {"start": v(-16.36, -1.92) * mm, "end": v(-17.18, -1.92) * mm});
            skLineSegment(sketch, "E1209", {"start": v(-17.18, -1.92) * mm, "end": v(-17.18, 0.37) * mm});
            skLineSegment(sketch, "E1210", {"start": v(-17.18, 0.37) * mm, "end": v(-16.36, 0.37) * mm});
            skLineSegment(sketch, "E1211", {"start": v(-16.36, 0.37) * mm, "end": v(-16.36, 1.74) * mm});
            skLineSegment(sketch, "E1212", {"start": v(-16.36, 1.74) * mm, "end": v(-13.62, 1.74) * mm});
            skLineSegment(sketch, "E1213", {"start": v(-13.62, 1.74) * mm, "end": v(-13.62, 0.37) * mm});
            skLineSegment(sketch, "E1214", {"start": v(-13.62, 0.37) * mm, "end": v(-12.68, 0.37) * mm});
            skLineSegment(sketch, "E1215", {"start": v(-12.68, 0.37) * mm, "end": v(-12.68, -1.92) * mm});
            skLineSegment(sketch, "E1216", {"start": v(-12.68, -1.92) * mm, "end": v(-13.62, -1.92) * mm});
            skLineSegment(sketch, "E1217", {"start": v(-13.62, -1.92) * mm, "end": v(-13.62, -4.14) * mm});
            skLineSegment(sketch, "E1218", {"start": v(-13.62, -4.14) * mm, "end": v(-13.51, -4.11) * mm});
            skLineSegment(sketch, "E1219", {"start": v(-13.51, -4.11) * mm, "end": v(-13.5, -4.1) * mm});
            skLineSegment(sketch, "E1220", {"start": v(-13.5, -4.1) * mm, "end": v(-12.8, -3.92) * mm});
            skLineSegment(sketch, "E1221", {"start": v(-12.8, -3.92) * mm, "end": v(-12.53, -6.22) * mm});
            skLineSegment(sketch, "E1222", {"start": v(-12.53, -6.22) * mm, "end": v(-13, -6.37) * mm});
            skLineSegment(sketch, "E1223", {"start": v(-13, -6.37) * mm, "end": v(-13.05, -6.39) * mm});
            skLineSegment(sketch, "E1224", {"start": v(-13.05, -6.39) * mm, "end": v(-13.5, -6.5) * mm});
            skLineSegment(sketch, "E1225", {"start": v(-13.5, -6.5) * mm, "end": v(-13.54, -6.5) * mm});
            skLineSegment(sketch, "E1226", {"start": v(-13.54, -6.5) * mm, "end": v(-13.59, -6.52) * mm});
            skLineSegment(sketch, "E1227", {"start": v(-13.59, -6.52) * mm, "end": v(-13.98, -6.57) * mm});
            skLineSegment(sketch, "E1228", {"start": v(-13.98, -6.57) * mm, "end": v(-14.11, -6.57) * mm});
            skLineSegment(sketch, "E1229", {"start": v(-8.91, -5.03) * mm, "end": v(-8.95, -5.1) * mm});
            skLineSegment(sketch, "E1230", {"start": v(-8.95, -5.1) * mm, "end": v(-9.2, -5.42) * mm});
            skLineSegment(sketch, "E1231", {"start": v(-9.2, -5.42) * mm, "end": v(-9.5, -5.67) * mm});
            skLineSegment(sketch, "E1232", {"start": v(-9.5, -5.67) * mm, "end": v(-9.57, -5.7) * mm});
            skLineSegment(sketch, "E1233", {"start": v(-9.57, -5.7) * mm, "end": v(-9.64, -5.75) * mm});
            skLineSegment(sketch, "E1234", {"start": v(-9.64, -5.75) * mm, "end": v(-10.28, -5.94) * mm});
            skLineSegment(sketch, "E1235", {"start": v(-10.28, -5.94) * mm, "end": v(-10.5, -5.94) * mm});
            skLineSegment(sketch, "E1236", {"start": v(-10.5, -5.94) * mm, "end": v(-10.7, -5.94) * mm});
            skLineSegment(sketch, "E1237", {"start": v(-10.7, -5.94) * mm, "end": v(-11.28, -5.8) * mm});
            skLineSegment(sketch, "E1238", {"start": v(-11.28, -5.8) * mm, "end": v(-11.8, -5.47) * mm});
            skLineSegment(sketch, "E1239", {"start": v(-11.8, -5.47) * mm, "end": v(-11.88, -5.37) * mm});
            skLineSegment(sketch, "E1240", {"start": v(-11.88, -5.37) * mm, "end": v(-11.97, -5.28) * mm});
            skLineSegment(sketch, "E1241", {"start": v(-11.97, -5.28) * mm, "end": v(-12.26, -4.64) * mm});
            skLineSegment(sketch, "E1242", {"start": v(-12.26, -4.64) * mm, "end": v(-12.37, -3.87) * mm});
            skLineSegment(sketch, "E1243", {"start": v(-12.37, -3.87) * mm, "end": v(-12.37, -3.62) * mm});
            skLineSegment(sketch, "E1244", {"start": v(-12.37, -3.62) * mm, "end": v(-12.37, -0.23) * mm});
            skLineSegment(sketch, "E1245", {"start": v(-12.37, -0.23) * mm, "end": v(-10.87, -0.23) * mm});
            skLineSegment(sketch, "E1246", {"start": v(-10.87, -0.23) * mm, "end": v(-10.87, -3.63) * mm});
            skLineSegment(sketch, "E1247", {"start": v(-10.87, -3.63) * mm, "end": v(-10.87, -3.76) * mm});
            skLineSegment(sketch, "E1248", {"start": v(-10.87, -3.76) * mm, "end": v(-10.82, -4.16) * mm});
            skLineSegment(sketch, "E1249", {"start": v(-10.82, -4.16) * mm, "end": v(-10.7, -4.47) * mm});
            skLineSegment(sketch, "E1250", {"start": v(-10.7, -4.47) * mm, "end": v(-10.67, -4.5) * mm});
            skLineSegment(sketch, "E1251", {"start": v(-10.67, -4.5) * mm, "end": v(-10.63, -4.55) * mm});
            skLineSegment(sketch, "E1252", {"start": v(-10.63, -4.55) * mm, "end": v(-10.41, -4.7) * mm});
            skLineSegment(sketch, "E1253", {"start": v(-10.41, -4.7) * mm, "end": v(-10.14, -4.77) * mm});
            skLineSegment(sketch, "E1254", {"start": v(-10.14, -4.77) * mm, "end": v(-10.05, -4.77) * mm});
            skLineSegment(sketch, "E1255", {"start": v(-10.05, -4.77) * mm, "end": v(-9.9, -4.77) * mm});
            skLineSegment(sketch, "E1256", {"start": v(-9.9, -4.77) * mm, "end": v(-9.48, -4.67) * mm});
            skLineSegment(sketch, "E1257", {"start": v(-9.48, -4.67) * mm, "end": v(-9.43, -4.65) * mm});
            skLineSegment(sketch, "E1258", {"start": v(-9.43, -4.65) * mm, "end": v(-9.4, -4.63) * mm});
            skLineSegment(sketch, "E1259", {"start": v(-9.4, -4.63) * mm, "end": v(-9.03, -4.34) * mm});
            skLineSegment(sketch, "E1260", {"start": v(-9.03, -4.34) * mm, "end": v(-9, -4.3) * mm});
            skLineSegment(sketch, "E1261", {"start": v(-9, -4.3) * mm, "end": v(-9, -0.23) * mm});
            skLineSegment(sketch, "E1262", {"start": v(-9, -0.23) * mm, "end": v(-7.5, -0.23) * mm});
            skLineSegment(sketch, "E1263", {"start": v(-7.5, -0.23) * mm, "end": v(-7.5, -5.83) * mm});
            skLineSegment(sketch, "E1264", {"start": v(-7.5, -5.83) * mm, "end": v(-8.79, -5.83) * mm});
            skLineSegment(sketch, "E1265", {"start": v(-8.79, -5.83) * mm, "end": v(-8.91, -5.03) * mm});
            skLineSegment(sketch, "E1266", {"start": v(-10.48, -6.57) * mm, "end": v(-10.74, -6.57) * mm});
            skLineSegment(sketch, "E1267", {"start": v(-10.74, -6.57) * mm, "end": v(-11.52, -6.38) * mm});
            skLineSegment(sketch, "E1268", {"start": v(-11.52, -6.38) * mm, "end": v(-12.21, -5.93) * mm});
            skLineSegment(sketch, "E1269", {"start": v(-12.21, -5.93) * mm, "end": v(-12.33, -5.8) * mm});
            skLineSegment(sketch, "E1270", {"start": v(-12.33, -5.8) * mm, "end": v(-12.44, -5.68) * mm});
            skLineSegment(sketch, "E1271", {"start": v(-12.44, -5.68) * mm, "end": v(-12.81, -4.89) * mm});
            skLineSegment(sketch, "E1272", {"start": v(-12.81, -4.89) * mm, "end": v(-12.97, -3.95) * mm});
            skLineSegment(sketch, "E1273", {"start": v(-12.97, -3.95) * mm, "end": v(-12.97, -3.63) * mm});
            skLineSegment(sketch, "E1274", {"start": v(-12.97, -3.63) * mm, "end": v(-12.97, 0.37) * mm});
            skLineSegment(sketch, "E1275", {"start": v(-12.97, 0.37) * mm, "end": v(-10.23, 0.37) * mm});
            skLineSegment(sketch, "E1276", {"start": v(-10.23, 0.37) * mm, "end": v(-10.23, -3.65) * mm});
            skLineSegment(sketch, "E1277", {"start": v(-10.23, -3.65) * mm, "end": v(-10.23, -3.75) * mm});
            skLineSegment(sketch, "E1278", {"start": v(-10.23, -3.75) * mm, "end": v(-10.2, -4.05) * mm});
            skLineSegment(sketch, "E1279", {"start": v(-10.2, -4.05) * mm, "end": v(-10.16, -4.16) * mm});
            skLineSegment(sketch, "E1280", {"start": v(-10.16, -4.16) * mm, "end": v(-10.15, -4.16) * mm});
            skLineSegment(sketch, "E1281", {"start": v(-10.15, -4.16) * mm, "end": v(-10.07, -4.19) * mm});
            skLineSegment(sketch, "E1282", {"start": v(-10.07, -4.19) * mm, "end": v(-10.04, -4.19) * mm});
            skLineSegment(sketch, "E1283", {"start": v(-10.04, -4.19) * mm, "end": v(-9.94, -4.19) * mm});
            skLineSegment(sketch, "E1284", {"start": v(-9.94, -4.19) * mm, "end": v(-9.69, -4.14) * mm});
            skLineSegment(sketch, "E1285", {"start": v(-9.69, -4.14) * mm, "end": v(-9.67, -4.12) * mm});
            skLineSegment(sketch, "E1286", {"start": v(-9.67, -4.12) * mm, "end": v(-9.66, -4.12) * mm});
            skLineSegment(sketch, "E1287", {"start": v(-9.66, -4.12) * mm, "end": v(-9.6, -4.1) * mm});
            skLineSegment(sketch, "E1288", {"start": v(-9.6, -4.1) * mm, "end": v(-9.6, -4.1) * mm});
            skLineSegment(sketch, "E1289", {"start": v(-9.6, -4.1) * mm, "end": v(-9.6, 0.35) * mm});
            skLineSegment(sketch, "E1290", {"start": v(-9.6, 0.35) * mm, "end": v(-6.86, 0.35) * mm});
            skLineSegment(sketch, "E1291", {"start": v(-6.86, 0.35) * mm, "end": v(-6.86, -6.48) * mm});
            skLineSegment(sketch, "E1292", {"start": v(-6.86, -6.48) * mm, "end": v(-9.3, -6.48) * mm});
            skLineSegment(sketch, "E1293", {"start": v(-9.3, -6.48) * mm, "end": v(-9.33, -6.31) * mm});
            skLineSegment(sketch, "E1294", {"start": v(-9.33, -6.31) * mm, "end": v(-9.41, -6.35) * mm});
            skLineSegment(sketch, "E1295", {"start": v(-9.41, -6.35) * mm, "end": v(-9.87, -6.5) * mm});
            skLineSegment(sketch, "E1296", {"start": v(-9.87, -6.5) * mm, "end": v(-10.33, -6.57) * mm});
            skLineSegment(sketch, "E1297", {"start": v(-10.33, -6.57) * mm, "end": v(-10.48, -6.57) * mm});
            skLineSegment(sketch, "E1298", {"start": v(-3.4, -1.54) * mm, "end": v(-3.96, -1.52) * mm});
            skLineSegment(sketch, "E1299", {"start": v(-3.96, -1.52) * mm, "end": v(-4.1, -1.52) * mm});
            skLineSegment(sketch, "E1300", {"start": v(-4.1, -1.52) * mm, "end": v(-4.48, -1.64) * mm});
            skLineSegment(sketch, "E1301", {"start": v(-4.48, -1.64) * mm, "end": v(-4.5, -1.66) * mm});
            skLineSegment(sketch, "E1302", {"start": v(-4.5, -1.66) * mm, "end": v(-4.55, -1.69) * mm});
            skLineSegment(sketch, "E1303", {"start": v(-4.55, -1.69) * mm, "end": v(-4.83, -2.02) * mm});
            skLineSegment(sketch, "E1304", {"start": v(-4.83, -2.02) * mm, "end": v(-4.85, -2.06) * mm});
            skLineSegment(sketch, "E1305", {"start": v(-4.85, -2.06) * mm, "end": v(-4.85, -5.85) * mm});
            skLineSegment(sketch, "E1306", {"start": v(-4.85, -5.85) * mm, "end": v(-6.36, -5.85) * mm});
            skLineSegment(sketch, "E1307", {"start": v(-6.36, -5.85) * mm, "end": v(-6.36, -0.25) * mm});
            skLineSegment(sketch, "E1308", {"start": v(-6.36, -0.25) * mm, "end": v(-4.96, -0.25) * mm});
            skLineSegment(sketch, "E1309", {"start": v(-4.96, -0.25) * mm, "end": v(-4.9, -1.08) * mm});
            skLineSegment(sketch, "E1310", {"start": v(-4.9, -1.08) * mm, "end": v(-4.86, -1) * mm});
            skLineSegment(sketch, "E1311", {"start": v(-4.86, -1) * mm, "end": v(-4.44, -0.43) * mm});
            skLineSegment(sketch, "E1312", {"start": v(-4.44, -0.43) * mm, "end": v(-4.39, -0.38) * mm});
            skLineSegment(sketch, "E1313", {"start": v(-4.39, -0.38) * mm, "end": v(-4.33, -0.34) * mm});
            skLineSegment(sketch, "E1314", {"start": v(-4.33, -0.34) * mm, "end": v(-4.05, -0.2) * mm});
            skLineSegment(sketch, "E1315", {"start": v(-4.05, -0.2) * mm, "end": v(-3.76, -0.14) * mm});
            skLineSegment(sketch, "E1316", {"start": v(-3.76, -0.14) * mm, "end": v(-3.66, -0.14) * mm});
            skLineSegment(sketch, "E1317", {"start": v(-3.66, -0.14) * mm, "end": v(-3.6, -0.14) * mm});
            skLineSegment(sketch, "E1318", {"start": v(-3.6, -0.14) * mm, "end": v(-3.47, -0.15) * mm});
            skLineSegment(sketch, "E1319", {"start": v(-3.47, -0.15) * mm, "end": v(-3.45, -0.15) * mm});
            skLineSegment(sketch, "E1320", {"start": v(-3.45, -0.15) * mm, "end": v(-3.43, -0.16) * mm});
            skLineSegment(sketch, "E1321", {"start": v(-3.43, -0.16) * mm, "end": v(-3.27, -0.2) * mm});
            skLineSegment(sketch, "E1322", {"start": v(-3.27, -0.2) * mm, "end": v(-3.25, -0.2) * mm});
            skLineSegment(sketch, "E1323", {"start": v(-3.25, -0.2) * mm, "end": v(-3.4, -1.54) * mm});
            skLineSegment(sketch, "E1324", {"start": v(-4.22, -6.46) * mm, "end": v(-6.96, -6.46) * mm});
            skLineSegment(sketch, "E1325", {"start": v(-6.96, -6.46) * mm, "end": v(-6.96, 0.37) * mm});
            skLineSegment(sketch, "E1326", {"start": v(-6.96, 0.37) * mm, "end": v(-4.37, 0.37) * mm});
            skLineSegment(sketch, "E1327", {"start": v(-4.37, 0.37) * mm, "end": v(-4.37, 0.32) * mm});
            skLineSegment(sketch, "E1328", {"start": v(-4.37, 0.32) * mm, "end": v(-4.31, 0.35) * mm});
            skLineSegment(sketch, "E1329", {"start": v(-4.31, 0.35) * mm, "end": v(-3.81, 0.48) * mm});
            skLineSegment(sketch, "E1330", {"start": v(-3.81, 0.48) * mm, "end": v(-3.65, 0.48) * mm});
            skLineSegment(sketch, "E1331", {"start": v(-3.65, 0.48) * mm, "end": v(-3.57, 0.48) * mm});
            skLineSegment(sketch, "E1332", {"start": v(-3.57, 0.48) * mm, "end": v(-3.35, 0.45) * mm});
            skLineSegment(sketch, "E1333", {"start": v(-3.35, 0.45) * mm, "end": v(-3.32, 0.45) * mm});
            skLineSegment(sketch, "E1334", {"start": v(-3.32, 0.45) * mm, "end": v(-3.1, 0.4) * mm});
            skLineSegment(sketch, "E1335", {"start": v(-3.1, 0.4) * mm, "end": v(-2.57, 0.26) * mm});
            skLineSegment(sketch, "E1336", {"start": v(-2.57, 0.26) * mm, "end": v(-2.86, -2.17) * mm});
            skLineSegment(sketch, "E1337", {"start": v(-2.86, -2.17) * mm, "end": v(-3.97, -2.14) * mm});
            skLineSegment(sketch, "E1338", {"start": v(-3.97, -2.14) * mm, "end": v(-4.03, -2.14) * mm});
            skLineSegment(sketch, "E1339", {"start": v(-4.03, -2.14) * mm, "end": v(-4.18, -2.18) * mm});
            skLineSegment(sketch, "E1340", {"start": v(-4.18, -2.18) * mm, "end": v(-4.19, -2.19) * mm});
            skLineSegment(sketch, "E1341", {"start": v(-4.19, -2.19) * mm, "end": v(-4.2, -2.19) * mm});
            skLineSegment(sketch, "E1342", {"start": v(-4.2, -2.19) * mm, "end": v(-4.23, -2.22) * mm});
            skLineSegment(sketch, "E1343", {"start": v(-4.23, -2.22) * mm, "end": v(-4.23, -2.23) * mm});
            skLineSegment(sketch, "E1344", {"start": v(-4.23, -2.23) * mm, "end": v(-4.23, -6.46) * mm});
            skLineSegment(sketch, "E1345", {"start": v(-4.23, -6.46) * mm, "end": v(-4.22, -6.46) * mm});
            skLineSegment(sketch, "E1346", {"start": v(-0.7, -3.5) * mm, "end": v(-1.12, -3.5) * mm});
            skLineSegment(sketch, "E1347", {"start": v(-1.12, -3.5) * mm, "end": v(-1.12, -5.83) * mm});
            skLineSegment(sketch, "E1348", {"start": v(-1.12, -5.83) * mm, "end": v(-2.63, -5.83) * mm});
            skLineSegment(sketch, "E1349", {"start": v(-2.63, -5.83) * mm, "end": v(-2.63, 2.23) * mm});
            skLineSegment(sketch, "E1350", {"start": v(-2.63, 2.23) * mm, "end": v(-1.12, 2.23) * mm});
            skLineSegment(sketch, "E1351", {"start": v(-1.12, 2.23) * mm, "end": v(-1.12, -2.35) * mm});
            skLineSegment(sketch, "E1352", {"start": v(-1.12, -2.35) * mm, "end": v(-0.75, -2.35) * mm});
            skLineSegment(sketch, "E1353", {"start": v(-0.75, -2.35) * mm, "end": v(0.54, -0.25) * mm});
            skLineSegment(sketch, "E1354", {"start": v(0.54, -0.25) * mm, "end": v(2.3, -0.25) * mm});
            skLineSegment(sketch, "E1355", {"start": v(2.3, -0.25) * mm, "end": v(0.5, -2.79) * mm});
            skLineSegment(sketch, "E1356", {"start": v(0.5, -2.79) * mm, "end": v(2.57, -5.85) * mm});
            skLineSegment(sketch, "E1357", {"start": v(2.57, -5.85) * mm, "end": v(0.83, -5.85) * mm});
            skLineSegment(sketch, "E1358", {"start": v(0.83, -5.85) * mm, "end": v(-0.7, -3.5) * mm});
            skLineSegment(sketch, "E1359", {"start": v(3.72, -6.46) * mm, "end": v(0.5, -6.46) * mm});
            skLineSegment(sketch, "E1360", {"start": v(0.5, -6.46) * mm, "end": v(-0.5, -4.92) * mm});
            skLineSegment(sketch, "E1361", {"start": v(-0.5, -4.92) * mm, "end": v(-0.5, -6.46) * mm});
            skLineSegment(sketch, "E1362", {"start": v(-0.5, -6.46) * mm, "end": v(-3.25, -6.46) * mm});
            skLineSegment(sketch, "E1363", {"start": v(-3.25, -6.46) * mm, "end": v(-3.25, 2.83) * mm});
            skLineSegment(sketch, "E1364", {"start": v(-3.25, 2.83) * mm, "end": v(-0.5, 2.83) * mm});
            skLineSegment(sketch, "E1365", {"start": v(-0.5, 2.83) * mm, "end": v(-0.5, -0.8) * mm});
            skLineSegment(sketch, "E1366", {"start": v(-0.5, -0.8) * mm, "end": v(0.2, 0.35) * mm});
            skLineSegment(sketch, "E1367", {"start": v(0.2, 0.35) * mm, "end": v(3.48, 0.35) * mm});
            skLineSegment(sketch, "E1368", {"start": v(3.48, 0.35) * mm, "end": v(1.25, -2.8) * mm});
            skLineSegment(sketch, "E1369", {"start": v(1.25, -2.8) * mm, "end": v(3.72, -6.46) * mm});
            skLineSegment(sketch, "E1370", {"start": v(6.46, -5.03) * mm, "end": v(6.42, -5.1) * mm});
            skLineSegment(sketch, "E1371", {"start": v(6.42, -5.1) * mm, "end": v(6.17, -5.42) * mm});
            skLineSegment(sketch, "E1372", {"start": v(6.17, -5.42) * mm, "end": v(5.87, -5.67) * mm});
            skLineSegment(sketch, "E1373", {"start": v(5.87, -5.67) * mm, "end": v(5.8, -5.7) * mm});
            skLineSegment(sketch, "E1374", {"start": v(5.8, -5.7) * mm, "end": v(5.74, -5.75) * mm});
            skLineSegment(sketch, "E1375", {"start": v(5.74, -5.75) * mm, "end": v(5.1, -5.94) * mm});
            skLineSegment(sketch, "E1376", {"start": v(5.1, -5.94) * mm, "end": v(4.88, -5.94) * mm});
            skLineSegment(sketch, "E1377", {"start": v(4.88, -5.94) * mm, "end": v(4.68, -5.94) * mm});
            skLineSegment(sketch, "E1378", {"start": v(4.68, -5.94) * mm, "end": v(4.1, -5.8) * mm});
            skLineSegment(sketch, "E1379", {"start": v(4.1, -5.8) * mm, "end": v(3.58, -5.47) * mm});
            skLineSegment(sketch, "E1380", {"start": v(3.58, -5.47) * mm, "end": v(3.5, -5.37) * mm});
            skLineSegment(sketch, "E1381", {"start": v(3.5, -5.37) * mm, "end": v(3.4, -5.28) * mm});
            skLineSegment(sketch, "E1382", {"start": v(3.4, -5.28) * mm, "end": v(3.12, -4.64) * mm});
            skLineSegment(sketch, "E1383", {"start": v(3.12, -4.64) * mm, "end": v(3, -3.87) * mm});
            skLineSegment(sketch, "E1384", {"start": v(3, -3.87) * mm, "end": v(3, -3.62) * mm});
            skLineSegment(sketch, "E1385", {"start": v(3, -3.62) * mm, "end": v(3, -0.23) * mm});
            skLineSegment(sketch, "E1386", {"start": v(3, -0.23) * mm, "end": v(4.5, -0.23) * mm});
            skLineSegment(sketch, "E1387", {"start": v(4.5, -0.23) * mm, "end": v(4.5, -3.63) * mm});
            skLineSegment(sketch, "E1388", {"start": v(4.5, -3.63) * mm, "end": v(4.5, -3.76) * mm});
            skLineSegment(sketch, "E1389", {"start": v(4.5, -3.76) * mm, "end": v(4.56, -4.16) * mm});
            skLineSegment(sketch, "E1390", {"start": v(4.56, -4.16) * mm, "end": v(4.67, -4.47) * mm});
            skLineSegment(sketch, "E1391", {"start": v(4.67, -4.47) * mm, "end": v(4.7, -4.5) * mm});
            skLineSegment(sketch, "E1392", {"start": v(4.7, -4.5) * mm, "end": v(4.74, -4.55) * mm});
            skLineSegment(sketch, "E1393", {"start": v(4.74, -4.55) * mm, "end": v(4.97, -4.7) * mm});
            skLineSegment(sketch, "E1394", {"start": v(4.97, -4.7) * mm, "end": v(5.23, -4.77) * mm});
            skLineSegment(sketch, "E1395", {"start": v(5.23, -4.77) * mm, "end": v(5.32, -4.77) * mm});
            skLineSegment(sketch, "E1396", {"start": v(5.32, -4.77) * mm, "end": v(5.48, -4.77) * mm});
            skLineSegment(sketch, "E1397", {"start": v(5.48, -4.77) * mm, "end": v(5.9, -4.67) * mm});
            skLineSegment(sketch, "E1398", {"start": v(5.9, -4.67) * mm, "end": v(5.94, -4.65) * mm});
            skLineSegment(sketch, "E1399", {"start": v(5.94, -4.65) * mm, "end": v(5.98, -4.63) * mm});
            skLineSegment(sketch, "E1400", {"start": v(5.98, -4.63) * mm, "end": v(6.34, -4.34) * mm});
            skLineSegment(sketch, "E1401", {"start": v(6.34, -4.34) * mm, "end": v(6.37, -4.3) * mm});
            skLineSegment(sketch, "E1402", {"start": v(6.37, -4.3) * mm, "end": v(6.37, -0.23) * mm});
            skLineSegment(sketch, "E1403", {"start": v(6.37, -0.23) * mm, "end": v(7.88, -0.23) * mm});
            skLineSegment(sketch, "E1404", {"start": v(7.88, -0.23) * mm, "end": v(7.88, -5.83) * mm});
            skLineSegment(sketch, "E1405", {"start": v(7.88, -5.83) * mm, "end": v(6.59, -5.83) * mm});
            skLineSegment(sketch, "E1406", {"start": v(6.59, -5.83) * mm, "end": v(6.46, -5.03) * mm});
            skLineSegment(sketch, "E1407", {"start": v(4.9, -6.57) * mm, "end": v(4.63, -6.57) * mm});
            skLineSegment(sketch, "E1408", {"start": v(4.63, -6.57) * mm, "end": v(3.85, -6.38) * mm});
            skLineSegment(sketch, "E1409", {"start": v(3.85, -6.38) * mm, "end": v(3.16, -5.93) * mm});
            skLineSegment(sketch, "E1410", {"start": v(3.16, -5.93) * mm, "end": v(3.05, -5.8) * mm});
            skLineSegment(sketch, "E1411", {"start": v(3.05, -5.8) * mm, "end": v(2.94, -5.68) * mm});
            skLineSegment(sketch, "E1412", {"start": v(2.94, -5.68) * mm, "end": v(2.56, -4.89) * mm});
            skLineSegment(sketch, "E1413", {"start": v(2.56, -4.89) * mm, "end": v(2.4, -3.95) * mm});
            skLineSegment(sketch, "E1414", {"start": v(2.4, -3.95) * mm, "end": v(2.4, -3.63) * mm});
            skLineSegment(sketch, "E1415", {"start": v(2.4, -3.63) * mm, "end": v(2.4, 0.37) * mm});
            skLineSegment(sketch, "E1416", {"start": v(2.4, 0.37) * mm, "end": v(5.14, 0.37) * mm});
            skLineSegment(sketch, "E1417", {"start": v(5.14, 0.37) * mm, "end": v(5.14, -3.65) * mm});
            skLineSegment(sketch, "E1418", {"start": v(5.14, -3.65) * mm, "end": v(5.14, -3.75) * mm});
            skLineSegment(sketch, "E1419", {"start": v(5.14, -3.75) * mm, "end": v(5.18, -4.05) * mm});
            skLineSegment(sketch, "E1420", {"start": v(5.18, -4.05) * mm, "end": v(5.22, -4.16) * mm});
            skLineSegment(sketch, "E1421", {"start": v(5.22, -4.16) * mm, "end": v(5.22, -4.16) * mm});
            skLineSegment(sketch, "E1422", {"start": v(5.22, -4.16) * mm, "end": v(5.3, -4.19) * mm});
            skLineSegment(sketch, "E1423", {"start": v(5.3, -4.19) * mm, "end": v(5.34, -4.19) * mm});
            skLineSegment(sketch, "E1424", {"start": v(5.34, -4.19) * mm, "end": v(5.43, -4.19) * mm});
            skLineSegment(sketch, "E1425", {"start": v(5.43, -4.19) * mm, "end": v(5.69, -4.14) * mm});
            skLineSegment(sketch, "E1426", {"start": v(5.69, -4.14) * mm, "end": v(5.7, -4.12) * mm});
            skLineSegment(sketch, "E1427", {"start": v(5.7, -4.12) * mm, "end": v(5.71, -4.12) * mm});
            skLineSegment(sketch, "E1428", {"start": v(5.71, -4.12) * mm, "end": v(5.77, -4.1) * mm});
            skLineSegment(sketch, "E1429", {"start": v(5.77, -4.1) * mm, "end": v(5.77, -4.1) * mm});
            skLineSegment(sketch, "E1430", {"start": v(5.77, -4.1) * mm, "end": v(5.77, 0.35) * mm});
            skLineSegment(sketch, "E1431", {"start": v(5.77, 0.35) * mm, "end": v(8.51, 0.35) * mm});
            skLineSegment(sketch, "E1432", {"start": v(8.51, 0.35) * mm, "end": v(8.51, -6.48) * mm});
            skLineSegment(sketch, "E1433", {"start": v(8.51, -6.48) * mm, "end": v(6.08, -6.48) * mm});
            skLineSegment(sketch, "E1434", {"start": v(6.08, -6.48) * mm, "end": v(6.05, -6.31) * mm});
            skLineSegment(sketch, "E1435", {"start": v(6.05, -6.31) * mm, "end": v(5.96, -6.35) * mm});
            skLineSegment(sketch, "E1436", {"start": v(5.96, -6.35) * mm, "end": v(5.16, -6.57) * mm});
            skLineSegment(sketch, "E1437", {"start": v(5.16, -6.57) * mm, "end": v(4.9, -6.57) * mm});
            skLineSegment(sketch, "E1438", {"start": v(0, 39.08) * mm, "end": v(0.97, 39.08) * mm});
            skLineSegment(sketch, "E1439", {"start": v(0.97, 39.08) * mm, "end": v(3.88, 38.89) * mm});
            skLineSegment(sketch, "E1440", {"start": v(3.88, 38.89) * mm, "end": v(7.68, 38.33) * mm});
            skLineSegment(sketch, "E1441", {"start": v(7.68, 38.33) * mm, "end": v(11.38, 37.4) * mm});
            skLineSegment(sketch, "E1442", {"start": v(11.38, 37.4) * mm, "end": v(14.96, 36.12) * mm});
            skLineSegment(sketch, "E1443", {"start": v(14.96, 36.12) * mm, "end": v(18.4, 34.5) * mm});
            skLineSegment(sketch, "E1444", {"start": v(18.4, 34.5) * mm, "end": v(21.67, 32.53) * mm});
            skLineSegment(sketch, "E1445", {"start": v(21.67, 32.53) * mm, "end": v(24.76, 30.24) * mm});
            skLineSegment(sketch, "E1446", {"start": v(24.76, 30.24) * mm, "end": v(26.95, 28.31) * mm});
            skLineSegment(sketch, "E1447", {"start": v(26.95, 28.31) * mm, "end": v(27.64, 27.63) * mm});
            skLineSegment(sketch, "E1448", {"start": v(27.64, 27.63) * mm, "end": v(28.33, 26.94) * mm});
            skLineSegment(sketch, "E1449", {"start": v(28.33, 26.94) * mm, "end": v(30.25, 24.75) * mm});
            skLineSegment(sketch, "E1450", {"start": v(30.25, 24.75) * mm, "end": v(32.55, 21.66) * mm});
            skLineSegment(sketch, "E1451", {"start": v(32.55, 21.66) * mm, "end": v(34.5, 18.39) * mm});
            skLineSegment(sketch, "E1452", {"start": v(34.5, 18.39) * mm, "end": v(36.14, 14.95) * mm});
            skLineSegment(sketch, "E1453", {"start": v(36.14, 14.95) * mm, "end": v(37.42, 11.38) * mm});
            skLineSegment(sketch, "E1454", {"start": v(37.42, 11.38) * mm, "end": v(38.34, 7.67) * mm});
            skLineSegment(sketch, "E1455", {"start": v(38.34, 7.67) * mm, "end": v(38.9, 3.87) * mm});
            skLineSegment(sketch, "E1456", {"start": v(38.9, 3.87) * mm, "end": v(39.1, 0.96) * mm});
            skLineSegment(sketch, "E1457", {"start": v(39.1, 0.96) * mm, "end": v(39.1, -0.02) * mm});
            skLineSegment(sketch, "E1458", {"start": v(39.1, -0.02) * mm, "end": v(39.1, -0.99) * mm});
            skLineSegment(sketch, "E1459", {"start": v(39.1, -0.99) * mm, "end": v(38.9, -3.9) * mm});
            skLineSegment(sketch, "E1460", {"start": v(38.9, -3.9) * mm, "end": v(38.34, -7.7) * mm});
            skLineSegment(sketch, "E1461", {"start": v(38.34, -7.7) * mm, "end": v(37.42, -11.4) * mm});
            skLineSegment(sketch, "E1462", {"start": v(37.42, -11.4) * mm, "end": v(36.14, -14.98) * mm});
            skLineSegment(sketch, "E1463", {"start": v(36.14, -14.98) * mm, "end": v(34.5, -18.41) * mm});
            skLineSegment(sketch, "E1464", {"start": v(34.5, -18.41) * mm, "end": v(32.55, -21.69) * mm});
            skLineSegment(sketch, "E1465", {"start": v(32.55, -21.69) * mm, "end": v(30.25, -24.78) * mm});
            skLineSegment(sketch, "E1466", {"start": v(30.25, -24.78) * mm, "end": v(28.33, -26.97) * mm});
            skLineSegment(sketch, "E1467", {"start": v(28.33, -26.97) * mm, "end": v(27.64, -27.66) * mm});
            skLineSegment(sketch, "E1468", {"start": v(27.64, -27.66) * mm, "end": v(26.95, -28.34) * mm});
            skLineSegment(sketch, "E1469", {"start": v(26.95, -28.34) * mm, "end": v(24.76, -30.27) * mm});
            skLineSegment(sketch, "E1470", {"start": v(24.76, -30.27) * mm, "end": v(21.67, -32.56) * mm});
            skLineSegment(sketch, "E1471", {"start": v(21.67, -32.56) * mm, "end": v(18.4, -34.53) * mm});
            skLineSegment(sketch, "E1472", {"start": v(18.4, -34.53) * mm, "end": v(14.97, -36.15) * mm});
            skLineSegment(sketch, "E1473", {"start": v(14.97, -36.15) * mm, "end": v(11.39, -37.43) * mm});
            skLineSegment(sketch, "E1474", {"start": v(11.39, -37.43) * mm, "end": v(7.69, -38.36) * mm});
            skLineSegment(sketch, "E1475", {"start": v(7.69, -38.36) * mm, "end": v(3.88, -38.92) * mm});
            skLineSegment(sketch, "E1476", {"start": v(3.88, -38.92) * mm, "end": v(0.97, -39.1) * mm});
            skLineSegment(sketch, "E1477", {"start": v(0.97, -39.1) * mm, "end": v(0, -39.1) * mm});
            skLineSegment(sketch, "E1478", {"start": v(0, -39.1) * mm, "end": v(-0.97, -39.1) * mm});
            skLineSegment(sketch, "E1479", {"start": v(-0.97, -39.1) * mm, "end": v(-3.89, -38.92) * mm});
            skLineSegment(sketch, "E1480", {"start": v(-3.89, -38.92) * mm, "end": v(-7.69, -38.36) * mm});
            skLineSegment(sketch, "E1481", {"start": v(-7.69, -38.36) * mm, "end": v(-11.4, -37.43) * mm});
            skLineSegment(sketch, "E1482", {"start": v(-11.4, -37.43) * mm, "end": v(-14.97, -36.15) * mm});
            skLineSegment(sketch, "E1483", {"start": v(-14.97, -36.15) * mm, "end": v(-18.4, -34.53) * mm});
            skLineSegment(sketch, "E1484", {"start": v(-18.4, -34.53) * mm, "end": v(-21.68, -32.56) * mm});
            skLineSegment(sketch, "E1485", {"start": v(-21.68, -32.56) * mm, "end": v(-24.76, -30.27) * mm});
            skLineSegment(sketch, "E1486", {"start": v(-24.76, -30.27) * mm, "end": v(-26.95, -28.34) * mm});
            skLineSegment(sketch, "E1487", {"start": v(-26.95, -28.34) * mm, "end": v(-27.64, -27.66) * mm});
            skLineSegment(sketch, "E1488", {"start": v(-27.64, -27.66) * mm, "end": v(-28.33, -26.97) * mm});
            skLineSegment(sketch, "E1489", {"start": v(-28.33, -26.97) * mm, "end": v(-30.25, -24.78) * mm});
            skLineSegment(sketch, "E1490", {"start": v(-30.25, -24.78) * mm, "end": v(-32.55, -21.7) * mm});
            skLineSegment(sketch, "E1491", {"start": v(-32.55, -21.7) * mm, "end": v(-34.51, -18.42) * mm});
            skLineSegment(sketch, "E1492", {"start": v(-34.51, -18.42) * mm, "end": v(-36.14, -14.98) * mm});
            skLineSegment(sketch, "E1493", {"start": v(-36.14, -14.98) * mm, "end": v(-37.42, -11.4) * mm});
            skLineSegment(sketch, "E1494", {"start": v(-37.42, -11.4) * mm, "end": v(-38.34, -7.7) * mm});
            skLineSegment(sketch, "E1495", {"start": v(-38.34, -7.7) * mm, "end": v(-38.9, -3.9) * mm});
            skLineSegment(sketch, "E1496", {"start": v(-38.9, -3.9) * mm, "end": v(-39.1, -0.99) * mm});
            skLineSegment(sketch, "E1497", {"start": v(-39.1, -0.99) * mm, "end": v(-39.1, -0.02) * mm});
            skLineSegment(sketch, "E1498", {"start": v(-39.1, -0.02) * mm, "end": v(-39.1, 0.96) * mm});
            skLineSegment(sketch, "E1499", {"start": v(-39.1, 0.96) * mm, "end": v(-38.9, 3.87) * mm});
            skLineSegment(sketch, "E1500", {"start": v(-38.9, 3.87) * mm, "end": v(-38.34, 7.67) * mm});
            skLineSegment(sketch, "E1501", {"start": v(-38.34, 7.67) * mm, "end": v(-37.42, 11.37) * mm});
            skLineSegment(sketch, "E1502", {"start": v(-37.42, 11.37) * mm, "end": v(-36.14, 14.95) * mm});
            skLineSegment(sketch, "E1503", {"start": v(-36.14, 14.95) * mm, "end": v(-34.51, 18.39) * mm});
            skLineSegment(sketch, "E1504", {"start": v(-34.51, 18.39) * mm, "end": v(-32.55, 21.66) * mm});
            skLineSegment(sketch, "E1505", {"start": v(-32.55, 21.66) * mm, "end": v(-30.25, 24.75) * mm});
            skLineSegment(sketch, "E1506", {"start": v(-30.25, 24.75) * mm, "end": v(-28.33, 26.94) * mm});
            skLineSegment(sketch, "E1507", {"start": v(-28.33, 26.94) * mm, "end": v(-27.64, 27.63) * mm});
            skLineSegment(sketch, "E1508", {"start": v(-27.64, 27.63) * mm, "end": v(-26.95, 28.31) * mm});
            skLineSegment(sketch, "E1509", {"start": v(-26.95, 28.31) * mm, "end": v(-24.76, 30.24) * mm});
            skLineSegment(sketch, "E1510", {"start": v(-24.76, 30.24) * mm, "end": v(-21.67, 32.53) * mm});
            skLineSegment(sketch, "E1511", {"start": v(-21.67, 32.53) * mm, "end": v(-18.4, 34.5) * mm});
            skLineSegment(sketch, "E1512", {"start": v(-18.4, 34.5) * mm, "end": v(-14.96, 36.12) * mm});
            skLineSegment(sketch, "E1513", {"start": v(-14.96, 36.12) * mm, "end": v(-11.38, 37.4) * mm});
            skLineSegment(sketch, "E1514", {"start": v(-11.38, 37.4) * mm, "end": v(-7.68, 38.33) * mm});
            skLineSegment(sketch, "E1515", {"start": v(-7.68, 38.33) * mm, "end": v(-3.88, 38.89) * mm});
            skLineSegment(sketch, "E1516", {"start": v(-3.88, 38.89) * mm, "end": v(-0.97, 39.08) * mm});
            skLineSegment(sketch, "E1517", {"start": v(-0.97, 39.08) * mm, "end": v(0, 39.08) * mm});
            skLineSegment(sketch, "E1518", {"start": v(0, -37.38) * mm, "end": v(0.93, -37.38) * mm});
            skLineSegment(sketch, "E1519", {"start": v(0.93, -37.38) * mm, "end": v(3.71, -37.2) * mm});
            skLineSegment(sketch, "E1520", {"start": v(3.71, -37.2) * mm, "end": v(7.35, -36.66) * mm});
            skLineSegment(sketch, "E1521", {"start": v(7.35, -36.66) * mm, "end": v(10.89, -35.78) * mm});
            skLineSegment(sketch, "E1522", {"start": v(10.89, -35.78) * mm, "end": v(14.3, -34.55) * mm});
            skLineSegment(sketch, "E1523", {"start": v(14.3, -34.55) * mm, "end": v(17.6, -33) * mm});
            skLineSegment(sketch, "E1524", {"start": v(17.6, -33) * mm, "end": v(20.72, -31.12) * mm});
            skLineSegment(sketch, "E1525", {"start": v(20.72, -31.12) * mm, "end": v(23.67, -28.93) * mm});
            skLineSegment(sketch, "E1526", {"start": v(23.67, -28.93) * mm, "end": v(25.77, -27.1) * mm});
            skLineSegment(sketch, "E1527", {"start": v(25.77, -27.1) * mm, "end": v(26.43, -26.44) * mm});
            skLineSegment(sketch, "E1528", {"start": v(26.43, -26.44) * mm, "end": v(27.08, -25.78) * mm});
            skLineSegment(sketch, "E1529", {"start": v(27.08, -25.78) * mm, "end": v(28.92, -23.69) * mm});
            skLineSegment(sketch, "E1530", {"start": v(28.92, -23.69) * mm, "end": v(31.11, -20.74) * mm});
            skLineSegment(sketch, "E1531", {"start": v(31.11, -20.74) * mm, "end": v(33, -17.6) * mm});
            skLineSegment(sketch, "E1532", {"start": v(33, -17.6) * mm, "end": v(34.55, -14.32) * mm});
            skLineSegment(sketch, "E1533", {"start": v(34.55, -14.32) * mm, "end": v(35.77, -10.9) * mm});
            skLineSegment(sketch, "E1534", {"start": v(35.77, -10.9) * mm, "end": v(36.65, -7.36) * mm});
            skLineSegment(sketch, "E1535", {"start": v(36.65, -7.36) * mm, "end": v(37.19, -3.73) * mm});
            skLineSegment(sketch, "E1536", {"start": v(37.19, -3.73) * mm, "end": v(37.37, -0.94) * mm});
            skLineSegment(sketch, "E1537", {"start": v(37.37, -0.94) * mm, "end": v(37.37, -0.02) * mm});
            skLineSegment(sketch, "E1538", {"start": v(37.37, -0.02) * mm, "end": v(37.37, 0.91) * mm});
            skLineSegment(sketch, "E1539", {"start": v(37.37, 0.91) * mm, "end": v(37.19, 3.7) * mm});
            skLineSegment(sketch, "E1540", {"start": v(37.19, 3.7) * mm, "end": v(36.65, 7.33) * mm});
            skLineSegment(sketch, "E1541", {"start": v(36.65, 7.33) * mm, "end": v(35.76, 10.87) * mm});
            skLineSegment(sketch, "E1542", {"start": v(35.76, 10.87) * mm, "end": v(34.54, 14.3) * mm});
            skLineSegment(sketch, "E1543", {"start": v(34.54, 14.3) * mm, "end": v(32.98, 17.58) * mm});
            skLineSegment(sketch, "E1544", {"start": v(32.98, 17.58) * mm, "end": v(31.1, 20.7) * mm});
            skLineSegment(sketch, "E1545", {"start": v(31.1, 20.7) * mm, "end": v(28.92, 23.66) * mm});
            skLineSegment(sketch, "E1546", {"start": v(28.92, 23.66) * mm, "end": v(27.08, 25.75) * mm});
            skLineSegment(sketch, "E1547", {"start": v(27.08, 25.75) * mm, "end": v(26.43, 26.4) * mm});
            skLineSegment(sketch, "E1548", {"start": v(26.43, 26.4) * mm, "end": v(25.77, 27.07) * mm});
            skLineSegment(sketch, "E1549", {"start": v(25.77, 27.07) * mm, "end": v(23.67, 28.9) * mm});
            skLineSegment(sketch, "E1550", {"start": v(23.67, 28.9) * mm, "end": v(20.72, 31.1) * mm});
            skLineSegment(sketch, "E1551", {"start": v(20.72, 31.1) * mm, "end": v(17.6, 32.98) * mm});
            skLineSegment(sketch, "E1552", {"start": v(17.6, 32.98) * mm, "end": v(14.3, 34.53) * mm});
            skLineSegment(sketch, "E1553", {"start": v(14.3, 34.53) * mm, "end": v(10.89, 35.75) * mm});
            skLineSegment(sketch, "E1554", {"start": v(10.89, 35.75) * mm, "end": v(7.35, 36.64) * mm});
            skLineSegment(sketch, "E1555", {"start": v(7.35, 36.64) * mm, "end": v(3.71, 37.17) * mm});
            skLineSegment(sketch, "E1556", {"start": v(3.71, 37.17) * mm, "end": v(0.93, 37.35) * mm});
            skLineSegment(sketch, "E1557", {"start": v(0.93, 37.35) * mm, "end": v(0, 37.35) * mm});
            skLineSegment(sketch, "E1558", {"start": v(0, 37.35) * mm, "end": v(-0.93, 37.35) * mm});
            skLineSegment(sketch, "E1559", {"start": v(-0.93, 37.35) * mm, "end": v(-3.71, 37.17) * mm});
            skLineSegment(sketch, "E1560", {"start": v(-3.71, 37.17) * mm, "end": v(-7.35, 36.63) * mm});
            skLineSegment(sketch, "E1561", {"start": v(-7.35, 36.63) * mm, "end": v(-10.89, 35.75) * mm});
            skLineSegment(sketch, "E1562", {"start": v(-10.89, 35.75) * mm, "end": v(-14.31, 34.53) * mm});
            skLineSegment(sketch, "E1563", {"start": v(-14.31, 34.53) * mm, "end": v(-17.6, 32.97) * mm});
            skLineSegment(sketch, "E1564", {"start": v(-17.6, 32.97) * mm, "end": v(-20.72, 31.1) * mm});
            skLineSegment(sketch, "E1565", {"start": v(-20.72, 31.1) * mm, "end": v(-23.67, 28.9) * mm});
            skLineSegment(sketch, "E1566", {"start": v(-23.67, 28.9) * mm, "end": v(-25.77, 27.07) * mm});
            skLineSegment(sketch, "E1567", {"start": v(-25.77, 27.07) * mm, "end": v(-26.43, 26.4) * mm});
            skLineSegment(sketch, "E1568", {"start": v(-26.43, 26.4) * mm, "end": v(-27.08, 25.75) * mm});
            skLineSegment(sketch, "E1569", {"start": v(-27.08, 25.75) * mm, "end": v(-28.92, 23.66) * mm});
            skLineSegment(sketch, "E1570", {"start": v(-28.92, 23.66) * mm, "end": v(-31.12, 20.7) * mm});
            skLineSegment(sketch, "E1571", {"start": v(-31.12, 20.7) * mm, "end": v(-33, 17.58) * mm});
            skLineSegment(sketch, "E1572", {"start": v(-33, 17.58) * mm, "end": v(-34.55, 14.3) * mm});
            skLineSegment(sketch, "E1573", {"start": v(-34.55, 14.3) * mm, "end": v(-35.77, 10.87) * mm});
            skLineSegment(sketch, "E1574", {"start": v(-35.77, 10.87) * mm, "end": v(-36.65, 7.33) * mm});
            skLineSegment(sketch, "E1575", {"start": v(-36.65, 7.33) * mm, "end": v(-37.19, 3.7) * mm});
            skLineSegment(sketch, "E1576", {"start": v(-37.19, 3.7) * mm, "end": v(-37.37, 0.91) * mm});
            skLineSegment(sketch, "E1577", {"start": v(-37.37, 0.91) * mm, "end": v(-37.37, -0.02) * mm});
            skLineSegment(sketch, "E1578", {"start": v(-37.37, -0.02) * mm, "end": v(-37.37, -0.94) * mm});
            skLineSegment(sketch, "E1579", {"start": v(-37.37, -0.94) * mm, "end": v(-37.19, -3.73) * mm});
            skLineSegment(sketch, "E1580", {"start": v(-37.19, -3.73) * mm, "end": v(-36.65, -7.36) * mm});
            skLineSegment(sketch, "E1581", {"start": v(-36.65, -7.36) * mm, "end": v(-35.77, -10.9) * mm});
            skLineSegment(sketch, "E1582", {"start": v(-35.77, -10.9) * mm, "end": v(-34.54, -14.32) * mm});
            skLineSegment(sketch, "E1583", {"start": v(-34.54, -14.32) * mm, "end": v(-32.99, -17.6) * mm});
            skLineSegment(sketch, "E1584", {"start": v(-32.99, -17.6) * mm, "end": v(-31.1, -20.74) * mm});
            skLineSegment(sketch, "E1585", {"start": v(-31.1, -20.74) * mm, "end": v(-28.92, -23.69) * mm});
            skLineSegment(sketch, "E1586", {"start": v(-28.92, -23.69) * mm, "end": v(-27.08, -25.78) * mm});
            skLineSegment(sketch, "E1587", {"start": v(-27.08, -25.78) * mm, "end": v(-26.43, -26.44) * mm});
            skLineSegment(sketch, "E1588", {"start": v(-26.43, -26.44) * mm, "end": v(-25.77, -27.1) * mm});
            skLineSegment(sketch, "E1589", {"start": v(-25.77, -27.1) * mm, "end": v(-23.67, -28.93) * mm});
            skLineSegment(sketch, "E1590", {"start": v(-23.67, -28.93) * mm, "end": v(-20.72, -31.12) * mm});
            skLineSegment(sketch, "E1591", {"start": v(-20.72, -31.12) * mm, "end": v(-17.6, -33) * mm});
            skLineSegment(sketch, "E1592", {"start": v(-17.6, -33) * mm, "end": v(-14.3, -34.55) * mm});
            skLineSegment(sketch, "E1593", {"start": v(-14.3, -34.55) * mm, "end": v(-10.88, -35.78) * mm});
            skLineSegment(sketch, "E1594", {"start": v(-10.88, -35.78) * mm, "end": v(-7.34, -36.66) * mm});
            skLineSegment(sketch, "E1595", {"start": v(-7.34, -36.66) * mm, "end": v(-3.7, -37.2) * mm});
            skLineSegment(sketch, "E1596", {"start": v(-3.7, -37.2) * mm, "end": v(-0.93, -37.38) * mm});
            skLineSegment(sketch, "E1597", {"start": v(-0.93, -37.38) * mm, "end": v(0, -37.38) * mm});
            skLineSegment(sketch, "E1598", {"start": v(0, 40) * mm, "end": v(-1, 40) * mm});
            skLineSegment(sketch, "E1599", {"start": v(-1, 40) * mm, "end": v(-3.97, 39.8) * mm});
            skLineSegment(sketch, "E1600", {"start": v(-3.97, 39.8) * mm, "end": v(-7.86, 39.23) * mm});
            skLineSegment(sketch, "E1601", {"start": v(-7.86, 39.23) * mm, "end": v(-11.65, 38.29) * mm});
            skLineSegment(sketch, "E1602", {"start": v(-11.65, 38.29) * mm, "end": v(-15.32, 36.98) * mm});
            skLineSegment(sketch, "E1603", {"start": v(-15.32, 36.98) * mm, "end": v(-18.83, 35.31) * mm});
            skLineSegment(sketch, "E1604", {"start": v(-18.83, 35.31) * mm, "end": v(-22.18, 33.3) * mm});
            skLineSegment(sketch, "E1605", {"start": v(-22.18, 33.3) * mm, "end": v(-25.34, 30.96) * mm});
            skLineSegment(sketch, "E1606", {"start": v(-25.34, 30.96) * mm, "end": v(-27.59, 29) * mm});
            skLineSegment(sketch, "E1607", {"start": v(-27.59, 29) * mm, "end": v(-28.29, 28.29) * mm});
            skLineSegment(sketch, "E1608", {"start": v(-28.29, 28.29) * mm, "end": v(-29, 27.59) * mm});
            skLineSegment(sketch, "E1609", {"start": v(-29, 27.59) * mm, "end": v(-30.96, 25.34) * mm});
            skLineSegment(sketch, "E1610", {"start": v(-30.96, 25.34) * mm, "end": v(-33.3, 22.18) * mm});
            skLineSegment(sketch, "E1611", {"start": v(-33.3, 22.18) * mm, "end": v(-35.31, 18.83) * mm});
            skLineSegment(sketch, "E1612", {"start": v(-35.31, 18.83) * mm, "end": v(-36.98, 15.32) * mm});
            skLineSegment(sketch, "E1613", {"start": v(-36.98, 15.32) * mm, "end": v(-38.29, 11.65) * mm});
            skLineSegment(sketch, "E1614", {"start": v(-38.29, 11.65) * mm, "end": v(-39.23, 7.86) * mm});
            skLineSegment(sketch, "E1615", {"start": v(-39.23, 7.86) * mm, "end": v(-39.8, 3.97) * mm});
            skLineSegment(sketch, "E1616", {"start": v(-39.8, 3.97) * mm, "end": v(-40, 1) * mm});
            skLineSegment(sketch, "E1617", {"start": v(-40, 1) * mm, "end": v(-40, 0) * mm});
            skLineSegment(sketch, "E1618", {"start": v(-40, 0) * mm, "end": v(-40, -1) * mm});
            skLineSegment(sketch, "E1619", {"start": v(-40, -1) * mm, "end": v(-39.8, -3.97) * mm});
            skLineSegment(sketch, "E1620", {"start": v(-39.8, -3.97) * mm, "end": v(-39.23, -7.86) * mm});
            skLineSegment(sketch, "E1621", {"start": v(-39.23, -7.86) * mm, "end": v(-38.29, -11.65) * mm});
            skLineSegment(sketch, "E1622", {"start": v(-38.29, -11.65) * mm, "end": v(-36.98, -15.32) * mm});
            skLineSegment(sketch, "E1623", {"start": v(-36.98, -15.32) * mm, "end": v(-35.31, -18.83) * mm});
            skLineSegment(sketch, "E1624", {"start": v(-35.31, -18.83) * mm, "end": v(-33.3, -22.18) * mm});
            skLineSegment(sketch, "E1625", {"start": v(-33.3, -22.18) * mm, "end": v(-30.96, -25.34) * mm});
            skLineSegment(sketch, "E1626", {"start": v(-30.96, -25.34) * mm, "end": v(-29, -27.58) * mm});
            skLineSegment(sketch, "E1627", {"start": v(-29, -27.58) * mm, "end": v(-28.29, -28.29) * mm});
            skLineSegment(sketch, "E1628", {"start": v(-28.29, -28.29) * mm, "end": v(-27.59, -28.99) * mm});
            skLineSegment(sketch, "E1629", {"start": v(-27.59, -28.99) * mm, "end": v(-25.34, -30.96) * mm});
            skLineSegment(sketch, "E1630", {"start": v(-25.34, -30.96) * mm, "end": v(-22.18, -33.3) * mm});
            skLineSegment(sketch, "E1631", {"start": v(-22.18, -33.3) * mm, "end": v(-18.83, -35.31) * mm});
            skLineSegment(sketch, "E1632", {"start": v(-18.83, -35.31) * mm, "end": v(-15.32, -36.98) * mm});
            skLineSegment(sketch, "E1633", {"start": v(-15.32, -36.98) * mm, "end": v(-11.65, -38.29) * mm});
            skLineSegment(sketch, "E1634", {"start": v(-11.65, -38.29) * mm, "end": v(-7.86, -39.23) * mm});
            skLineSegment(sketch, "E1635", {"start": v(-7.86, -39.23) * mm, "end": v(-3.97, -39.8) * mm});
            skLineSegment(sketch, "E1636", {"start": v(-3.97, -39.8) * mm, "end": v(-1, -40) * mm});
            skLineSegment(sketch, "E1637", {"start": v(-1, -40) * mm, "end": v(0, -40) * mm});
            skLineSegment(sketch, "E1638", {"start": v(0, -40) * mm, "end": v(1, -40) * mm});
            skLineSegment(sketch, "E1639", {"start": v(1, -40) * mm, "end": v(3.97, -39.8) * mm});
            skLineSegment(sketch, "E1640", {"start": v(3.97, -39.8) * mm, "end": v(7.86, -39.23) * mm});
            skLineSegment(sketch, "E1641", {"start": v(7.86, -39.23) * mm, "end": v(11.65, -38.29) * mm});
            skLineSegment(sketch, "E1642", {"start": v(11.65, -38.29) * mm, "end": v(15.32, -36.98) * mm});
            skLineSegment(sketch, "E1643", {"start": v(15.32, -36.98) * mm, "end": v(18.83, -35.31) * mm});
            skLineSegment(sketch, "E1644", {"start": v(18.83, -35.31) * mm, "end": v(22.18, -33.3) * mm});
            skLineSegment(sketch, "E1645", {"start": v(22.18, -33.3) * mm, "end": v(25.34, -30.96) * mm});
            skLineSegment(sketch, "E1646", {"start": v(25.34, -30.96) * mm, "end": v(27.58, -28.99) * mm});
            skLineSegment(sketch, "E1647", {"start": v(27.58, -28.99) * mm, "end": v(28.29, -28.29) * mm});
            skLineSegment(sketch, "E1648", {"start": v(28.29, -28.29) * mm, "end": v(28.99, -27.58) * mm});
            skLineSegment(sketch, "E1649", {"start": v(28.99, -27.58) * mm, "end": v(30.96, -25.34) * mm});
            skLineSegment(sketch, "E1650", {"start": v(30.96, -25.34) * mm, "end": v(33.3, -22.18) * mm});
            skLineSegment(sketch, "E1651", {"start": v(33.3, -22.18) * mm, "end": v(35.31, -18.83) * mm});
            skLineSegment(sketch, "E1652", {"start": v(35.31, -18.83) * mm, "end": v(36.98, -15.32) * mm});
            skLineSegment(sketch, "E1653", {"start": v(36.98, -15.32) * mm, "end": v(38.29, -11.65) * mm});
            skLineSegment(sketch, "E1654", {"start": v(38.29, -11.65) * mm, "end": v(39.23, -7.86) * mm});
            skLineSegment(sketch, "E1655", {"start": v(39.23, -7.86) * mm, "end": v(39.8, -3.97) * mm});
            skLineSegment(sketch, "E1656", {"start": v(39.8, -3.97) * mm, "end": v(40, -1) * mm});
            skLineSegment(sketch, "E1657", {"start": v(40, -1) * mm, "end": v(40, 0) * mm});
            skLineSegment(sketch, "E1658", {"start": v(40, 0) * mm, "end": v(40, 1) * mm});
            skLineSegment(sketch, "E1659", {"start": v(40, 1) * mm, "end": v(39.8, 3.97) * mm});
            skLineSegment(sketch, "E1660", {"start": v(39.8, 3.97) * mm, "end": v(39.23, 7.86) * mm});
            skLineSegment(sketch, "E1661", {"start": v(39.23, 7.86) * mm, "end": v(38.29, 11.65) * mm});
            skLineSegment(sketch, "E1662", {"start": v(38.29, 11.65) * mm, "end": v(36.98, 15.32) * mm});
            skLineSegment(sketch, "E1663", {"start": v(36.98, 15.32) * mm, "end": v(35.31, 18.83) * mm});
            skLineSegment(sketch, "E1664", {"start": v(35.31, 18.83) * mm, "end": v(33.3, 22.18) * mm});
            skLineSegment(sketch, "E1665", {"start": v(33.3, 22.18) * mm, "end": v(30.96, 25.34) * mm});
            skLineSegment(sketch, "E1666", {"start": v(30.96, 25.34) * mm, "end": v(28.99, 27.59) * mm});
            skLineSegment(sketch, "E1667", {"start": v(28.99, 27.59) * mm, "end": v(28.29, 28.29) * mm});
            skLineSegment(sketch, "E1668", {"start": v(28.29, 28.29) * mm, "end": v(27.58, 29) * mm});
            skLineSegment(sketch, "E1669", {"start": v(27.58, 29) * mm, "end": v(25.34, 30.96) * mm});
            skLineSegment(sketch, "E1670", {"start": v(25.34, 30.96) * mm, "end": v(22.18, 33.3) * mm});
            skLineSegment(sketch, "E1671", {"start": v(22.18, 33.3) * mm, "end": v(18.84, 35.31) * mm});
            skLineSegment(sketch, "E1672", {"start": v(18.84, 35.31) * mm, "end": v(15.32, 36.98) * mm});
            skLineSegment(sketch, "E1673", {"start": v(15.32, 36.98) * mm, "end": v(11.66, 38.29) * mm});
            skLineSegment(sketch, "E1674", {"start": v(11.66, 38.29) * mm, "end": v(7.87, 39.23) * mm});
            skLineSegment(sketch, "E1675", {"start": v(7.87, 39.23) * mm, "end": v(3.98, 39.8) * mm});
            skLineSegment(sketch, "E1676", {"start": v(3.98, 39.8) * mm, "end": v(1, 40) * mm});
            skLineSegment(sketch, "E1677", {"start": v(1, 40) * mm, "end": v(0, 40) * mm});
            skLineSegment(sketch, "E1678", {"start": v(0, -36.46) * mm, "end": v(-0.9, -36.46) * mm});
            skLineSegment(sketch, "E1679", {"start": v(-0.9, -36.46) * mm, "end": v(-3.62, -36.28) * mm});
            skLineSegment(sketch, "E1680", {"start": v(-3.62, -36.28) * mm, "end": v(-7.17, -35.76) * mm});
            skLineSegment(sketch, "E1681", {"start": v(-7.17, -35.76) * mm, "end": v(-10.62, -34.9) * mm});
            skLineSegment(sketch, "E1682", {"start": v(-10.62, -34.9) * mm, "end": v(-13.96, -33.7) * mm});
            skLineSegment(sketch, "E1683", {"start": v(-13.96, -33.7) * mm, "end": v(-17.16, -32.19) * mm});
            skLineSegment(sketch, "E1684", {"start": v(-17.16, -32.19) * mm, "end": v(-20.21, -30.36) * mm});
            skLineSegment(sketch, "E1685", {"start": v(-20.21, -30.36) * mm, "end": v(-23.1, -28.22) * mm});
            skLineSegment(sketch, "E1686", {"start": v(-23.1, -28.22) * mm, "end": v(-25.14, -26.42) * mm});
            skLineSegment(sketch, "E1687", {"start": v(-25.14, -26.42) * mm, "end": v(-25.78, -25.78) * mm});
            skLineSegment(sketch, "E1688", {"start": v(-25.78, -25.78) * mm, "end": v(-26.42, -25.14) * mm});
            skLineSegment(sketch, "E1689", {"start": v(-26.42, -25.14) * mm, "end": v(-28.21, -23.1) * mm});
            skLineSegment(sketch, "E1690", {"start": v(-28.21, -23.1) * mm, "end": v(-30.35, -20.22) * mm});
            skLineSegment(sketch, "E1691", {"start": v(-30.35, -20.22) * mm, "end": v(-32.18, -17.17) * mm});
            skLineSegment(sketch, "E1692", {"start": v(-32.18, -17.17) * mm, "end": v(-33.7, -13.96) * mm});
            skLineSegment(sketch, "E1693", {"start": v(-33.7, -13.96) * mm, "end": v(-34.9, -10.62) * mm});
            skLineSegment(sketch, "E1694", {"start": v(-34.9, -10.62) * mm, "end": v(-35.76, -7.17) * mm});
            skLineSegment(sketch, "E1695", {"start": v(-35.76, -7.17) * mm, "end": v(-36.28, -3.62) * mm});
            skLineSegment(sketch, "E1696", {"start": v(-36.28, -3.62) * mm, "end": v(-36.46, -0.9) * mm});
            skLineSegment(sketch, "E1697", {"start": v(-36.46, -0.9) * mm, "end": v(-36.46, 0) * mm});
            skLineSegment(sketch, "E1698", {"start": v(-36.46, 0) * mm, "end": v(-36.46, 0.9) * mm});
            skLineSegment(sketch, "E1699", {"start": v(-36.46, 0.9) * mm, "end": v(-36.28, 3.62) * mm});
            skLineSegment(sketch, "E1700", {"start": v(-36.28, 3.62) * mm, "end": v(-35.76, 7.17) * mm});
            skLineSegment(sketch, "E1701", {"start": v(-35.76, 7.17) * mm, "end": v(-34.9, 10.62) * mm});
            skLineSegment(sketch, "E1702", {"start": v(-34.9, 10.62) * mm, "end": v(-33.7, 13.96) * mm});
            skLineSegment(sketch, "E1703", {"start": v(-33.7, 13.96) * mm, "end": v(-32.19, 17.16) * mm});
            skLineSegment(sketch, "E1704", {"start": v(-32.19, 17.16) * mm, "end": v(-30.36, 20.21) * mm});
            skLineSegment(sketch, "E1705", {"start": v(-30.36, 20.21) * mm, "end": v(-28.22, 23.1) * mm});
            skLineSegment(sketch, "E1706", {"start": v(-28.22, 23.1) * mm, "end": v(-26.42, 25.14) * mm});
            skLineSegment(sketch, "E1707", {"start": v(-26.42, 25.14) * mm, "end": v(-25.78, 25.78) * mm});
            skLineSegment(sketch, "E1708", {"start": v(-25.78, 25.78) * mm, "end": v(-25.14, 26.42) * mm});
            skLineSegment(sketch, "E1709", {"start": v(-25.14, 26.42) * mm, "end": v(-23.1, 28.21) * mm});
            skLineSegment(sketch, "E1710", {"start": v(-23.1, 28.21) * mm, "end": v(-20.22, 30.35) * mm});
            skLineSegment(sketch, "E1711", {"start": v(-20.22, 30.35) * mm, "end": v(-17.17, 32.18) * mm});
            skLineSegment(sketch, "E1712", {"start": v(-17.17, 32.18) * mm, "end": v(-13.96, 33.7) * mm});
            skLineSegment(sketch, "E1713", {"start": v(-13.96, 33.7) * mm, "end": v(-10.62, 34.9) * mm});
            skLineSegment(sketch, "E1714", {"start": v(-10.62, 34.9) * mm, "end": v(-7.17, 35.76) * mm});
            skLineSegment(sketch, "E1715", {"start": v(-7.17, 35.76) * mm, "end": v(-3.62, 36.28) * mm});
            skLineSegment(sketch, "E1716", {"start": v(-3.62, 36.28) * mm, "end": v(-0.9, 36.46) * mm});
            skLineSegment(sketch, "E1717", {"start": v(-0.9, 36.46) * mm, "end": v(0, 36.46) * mm});
            skLineSegment(sketch, "E1718", {"start": v(0, 36.46) * mm, "end": v(0.9, 36.46) * mm});
            skLineSegment(sketch, "E1719", {"start": v(0.9, 36.46) * mm, "end": v(3.62, 36.28) * mm});
            skLineSegment(sketch, "E1720", {"start": v(3.62, 36.28) * mm, "end": v(7.17, 35.76) * mm});
            skLineSegment(sketch, "E1721", {"start": v(7.17, 35.76) * mm, "end": v(10.62, 34.9) * mm});
            skLineSegment(sketch, "E1722", {"start": v(10.62, 34.9) * mm, "end": v(13.96, 33.7) * mm});
            skLineSegment(sketch, "E1723", {"start": v(13.96, 33.7) * mm, "end": v(17.16, 32.19) * mm});
            skLineSegment(sketch, "E1724", {"start": v(17.16, 32.19) * mm, "end": v(20.21, 30.36) * mm});
            skLineSegment(sketch, "E1725", {"start": v(20.21, 30.36) * mm, "end": v(23.1, 28.22) * mm});
            skLineSegment(sketch, "E1726", {"start": v(23.1, 28.22) * mm, "end": v(25.14, 26.42) * mm});
            skLineSegment(sketch, "E1727", {"start": v(25.14, 26.42) * mm, "end": v(25.78, 25.78) * mm});
            skLineSegment(sketch, "E1728", {"start": v(25.78, 25.78) * mm, "end": v(26.42, 25.14) * mm});
            skLineSegment(sketch, "E1729", {"start": v(26.42, 25.14) * mm, "end": v(28.21, 23.1) * mm});
            skLineSegment(sketch, "E1730", {"start": v(28.21, 23.1) * mm, "end": v(30.35, 20.22) * mm});
            skLineSegment(sketch, "E1731", {"start": v(30.35, 20.22) * mm, "end": v(32.18, 17.17) * mm});
            skLineSegment(sketch, "E1732", {"start": v(32.18, 17.17) * mm, "end": v(33.7, 13.96) * mm});
            skLineSegment(sketch, "E1733", {"start": v(33.7, 13.96) * mm, "end": v(34.9, 10.62) * mm});
            skLineSegment(sketch, "E1734", {"start": v(34.9, 10.62) * mm, "end": v(35.76, 7.17) * mm});
            skLineSegment(sketch, "E1735", {"start": v(35.76, 7.17) * mm, "end": v(36.28, 3.62) * mm});
            skLineSegment(sketch, "E1736", {"start": v(36.28, 3.62) * mm, "end": v(36.46, 0.9) * mm});
            skLineSegment(sketch, "E1737", {"start": v(36.46, 0.9) * mm, "end": v(36.46, 0) * mm});
            skLineSegment(sketch, "E1738", {"start": v(36.46, 0) * mm, "end": v(36.46, -0.9) * mm});
            skLineSegment(sketch, "E1739", {"start": v(36.46, -0.9) * mm, "end": v(36.28, -3.62) * mm});
            skLineSegment(sketch, "E1740", {"start": v(36.28, -3.62) * mm, "end": v(35.76, -7.17) * mm});
            skLineSegment(sketch, "E1741", {"start": v(35.76, -7.17) * mm, "end": v(34.9, -10.62) * mm});
            skLineSegment(sketch, "E1742", {"start": v(34.9, -10.62) * mm, "end": v(33.7, -13.96) * mm});
            skLineSegment(sketch, "E1743", {"start": v(33.7, -13.96) * mm, "end": v(32.19, -17.16) * mm});
            skLineSegment(sketch, "E1744", {"start": v(32.19, -17.16) * mm, "end": v(30.36, -20.21) * mm});
            skLineSegment(sketch, "E1745", {"start": v(30.36, -20.21) * mm, "end": v(28.22, -23.1) * mm});
            skLineSegment(sketch, "E1746", {"start": v(28.22, -23.1) * mm, "end": v(26.42, -25.14) * mm});
            skLineSegment(sketch, "E1747", {"start": v(26.42, -25.14) * mm, "end": v(25.78, -25.78) * mm});
            skLineSegment(sketch, "E1748", {"start": v(25.78, -25.78) * mm, "end": v(25.14, -26.42) * mm});
            skLineSegment(sketch, "E1749", {"start": v(25.14, -26.42) * mm, "end": v(23.1, -28.22) * mm});
            skLineSegment(sketch, "E1750", {"start": v(23.1, -28.22) * mm, "end": v(20.22, -30.36) * mm});
            skLineSegment(sketch, "E1751", {"start": v(20.22, -30.36) * mm, "end": v(17.17, -32.19) * mm});
            skLineSegment(sketch, "E1752", {"start": v(17.17, -32.19) * mm, "end": v(13.96, -33.7) * mm});
            skLineSegment(sketch, "E1753", {"start": v(13.96, -33.7) * mm, "end": v(10.62, -34.9) * mm});
            skLineSegment(sketch, "E1754", {"start": v(10.62, -34.9) * mm, "end": v(7.17, -35.76) * mm});
            skLineSegment(sketch, "E1755", {"start": v(7.17, -35.76) * mm, "end": v(3.62, -36.28) * mm});
            skLineSegment(sketch, "E1756", {"start": v(3.62, -36.28) * mm, "end": v(0.9, -36.46) * mm});
            skLineSegment(sketch, "E1757", {"start": v(0.9, -36.46) * mm, "end": v(0, -36.46) * mm});
            skLineSegment(sketch, "E1758", {"start": v(-17.22, 29.5) * mm, "end": v(-17.8, 28.55) * mm});
            skLineSegment(sketch, "E1759", {"start": v(-17.8, 28.55) * mm, "end": v(-19.04, 25.37) * mm});
            skLineSegment(sketch, "E1760", {"start": v(-19.04, 25.37) * mm, "end": v(-19.76, 20.83) * mm});
            skLineSegment(sketch, "E1761", {"start": v(-19.76, 20.83) * mm, "end": v(-19.37, 16) * mm});
            skLineSegment(sketch, "E1762", {"start": v(-19.37, 16) * mm, "end": v(-18.37, 12.22) * mm});
            skLineSegment(sketch, "E1763", {"start": v(-18.37, 12.22) * mm, "end": v(-17.88, 11.02) * mm});
            skLineSegment(sketch, "E1764", {"start": v(-17.88, 11.02) * mm, "end": v(-17.62, 10.38) * mm});
            skLineSegment(sketch, "E1765", {"start": v(-17.62, 10.38) * mm, "end": v(-16.73, 8.5) * mm});
            skLineSegment(sketch, "E1766", {"start": v(-16.73, 8.5) * mm, "end": v(-15.33, 6.06) * mm});
            skLineSegment(sketch, "E1767", {"start": v(-15.33, 6.06) * mm, "end": v(-13.7, 3.7) * mm});
            skLineSegment(sketch, "E1768", {"start": v(-13.7, 3.7) * mm, "end": v(-11.85, 1.46) * mm});
            skLineSegment(sketch, "E1769", {"start": v(-11.85, 1.46) * mm, "end": v(-9.8, -0.68) * mm});
            skLineSegment(sketch, "E1770", {"start": v(-9.8, -0.68) * mm, "end": v(-7.55, -2.68) * mm});
            skLineSegment(sketch, "E1771", {"start": v(-7.55, -2.68) * mm, "end": v(-5.12, -4.54) * mm});
            skLineSegment(sketch, "E1772", {"start": v(-5.12, -4.54) * mm, "end": v(-3.19, -5.85) * mm});
            skLineSegment(sketch, "E1773", {"start": v(-3.19, -5.85) * mm, "end": v(-2.52, -6.25) * mm});
            skLineSegment(sketch, "E1774", {"start": v(-2.52, -6.25) * mm, "end": v(-1.36, -6.95) * mm});
            skLineSegment(sketch, "E1775", {"start": v(-1.36, -6.95) * mm, "end": v(2.33, -8.77) * mm});
            skLineSegment(sketch, "E1776", {"start": v(2.33, -8.77) * mm, "end": v(7.27, -10.55) * mm});
            skLineSegment(sketch, "E1777", {"start": v(7.27, -10.55) * mm, "end": v(12.18, -11.62) * mm});
            skLineSegment(sketch, "E1778", {"start": v(12.18, -11.62) * mm, "end": v(15.78, -11.97) * mm});
            skLineSegment(sketch, "E1779", {"start": v(15.78, -11.97) * mm, "end": v(16.98, -11.97) * mm});
            skLineSegment(sketch, "E1780", {"start": v(16.98, -11.97) * mm, "end": v(17.73, -11.97) * mm});
            skLineSegment(sketch, "E1781", {"start": v(17.73, -11.97) * mm, "end": v(19.98, -11.82) * mm});
            skLineSegment(sketch, "E1782", {"start": v(19.98, -11.82) * mm, "end": v(22.86, -11.38) * mm});
            skLineSegment(sketch, "E1783", {"start": v(22.86, -11.38) * mm, "end": v(25.58, -10.65) * mm});
            skLineSegment(sketch, "E1784", {"start": v(25.58, -10.65) * mm, "end": v(28.13, -9.62) * mm});
            skLineSegment(sketch, "E1785", {"start": v(28.13, -9.62) * mm, "end": v(30.47, -8.3) * mm});
            skLineSegment(sketch, "E1786", {"start": v(30.47, -8.3) * mm, "end": v(32.58, -6.7) * mm});
            skLineSegment(sketch, "E1787", {"start": v(32.58, -6.7) * mm, "end": v(34.42, -4.82) * mm});
            skLineSegment(sketch, "E1788", {"start": v(34.42, -4.82) * mm, "end": v(35.62, -3.23) * mm});
            skLineSegment(sketch, "E1789", {"start": v(35.62, -3.23) * mm, "end": v(35.97, -2.66) * mm});
            skLineSegment(sketch, "E1790", {"start": v(35.97, -2.66) * mm, "end": v(36.23, -2.22) * mm});
            skLineSegment(sketch, "E1791", {"start": v(36.23, -2.22) * mm, "end": v(37.31, 0.09) * mm});
            skLineSegment(sketch, "E1792", {"start": v(37.31, 0.09) * mm, "end": v(38.06, 2.53) * mm});
            skLineSegment(sketch, "E1793", {"start": v(38.06, 2.53) * mm, "end": v(38.15, 3.03) * mm});
            skLineSegment(sketch, "E1794", {"start": v(38.15, 3.03) * mm, "end": v(38.1, 3.8) * mm});
            skLineSegment(sketch, "E1795", {"start": v(38.1, 3.8) * mm, "end": v(37.51, 7.54) * mm});
            skLineSegment(sketch, "E1796", {"start": v(37.51, 7.54) * mm, "end": v(36.6, 11.15) * mm});
            skLineSegment(sketch, "E1797", {"start": v(36.6, 11.15) * mm, "end": v(36.37, 11.85) * mm});
            skLineSegment(sketch, "E1798", {"start": v(36.37, 11.85) * mm, "end": v(36.27, 11.4) * mm});
            skLineSegment(sketch, "E1799", {"start": v(36.27, 11.4) * mm, "end": v(35.56, 9.23) * mm});
            skLineSegment(sketch, "E1800", {"start": v(35.56, 9.23) * mm, "end": v(34.56, 7.13) * mm});
            skLineSegment(sketch, "E1801", {"start": v(34.56, 7.13) * mm, "end": v(34.32, 6.73) * mm});
            skLineSegment(sketch, "E1802", {"start": v(34.32, 6.73) * mm, "end": v(33.8, 5.87) * mm});
            skLineSegment(sketch, "E1803", {"start": v(33.8, 5.87) * mm, "end": v(31.84, 3.54) * mm});
            skLineSegment(sketch, "E1804", {"start": v(31.84, 3.54) * mm, "end": v(28.68, 1.02) * mm});
            skLineSegment(sketch, "E1805", {"start": v(28.68, 1.02) * mm, "end": v(24.93, -0.8) * mm});
            skLineSegment(sketch, "E1806", {"start": v(24.93, -0.8) * mm, "end": v(21.75, -1.68) * mm});
            skLineSegment(sketch, "E1807", {"start": v(21.75, -1.68) * mm, "end": v(20.67, -1.83) * mm});
            skLineSegment(sketch, "E1808", {"start": v(20.67, -1.83) * mm, "end": v(20.38, -1.87) * mm});
            skLineSegment(sketch, "E1809", {"start": v(20.38, -1.87) * mm, "end": v(18.01, -2.08) * mm});
            skLineSegment(sketch, "E1810", {"start": v(18.01, -2.08) * mm, "end": v(17.22, -2.08) * mm});
            skLineSegment(sketch, "E1811", {"start": v(17.22, -2.08) * mm, "end": v(16.3, -2.08) * mm});
            skLineSegment(sketch, "E1812", {"start": v(16.3, -2.08) * mm, "end": v(13.55, -1.81) * mm});
            skLineSegment(sketch, "E1813", {"start": v(13.55, -1.81) * mm, "end": v(9.89, -1.02) * mm});
            skLineSegment(sketch, "E1814", {"start": v(9.89, -1.02) * mm, "end": v(6.3, 0.28) * mm});
            skLineSegment(sketch, "E1815", {"start": v(6.3, 0.28) * mm, "end": v(3.68, 1.57) * mm});
            skLineSegment(sketch, "E1816", {"start": v(3.68, 1.57) * mm, "end": v(2.85, 2.08) * mm});
            skLineSegment(sketch, "E1817", {"start": v(2.85, 2.08) * mm, "end": v(1.82, 2.7) * mm});
            skLineSegment(sketch, "E1818", {"start": v(1.82, 2.7) * mm, "end": v(-1.06, 4.9) * mm});
            skLineSegment(sketch, "E1819", {"start": v(-1.06, 4.9) * mm, "end": v(-4.36, 8.22) * mm});
            skLineSegment(sketch, "E1820", {"start": v(-4.36, 8.22) * mm, "end": v(-7, 11.97) * mm});
            skLineSegment(sketch, "E1821", {"start": v(-7, 11.97) * mm, "end": v(-8.52, 15) * mm});
            skLineSegment(sketch, "E1822", {"start": v(-8.52, 15) * mm, "end": v(-8.9, 16.05) * mm});
            skLineSegment(sketch, "E1823", {"start": v(-8.9, 16.05) * mm, "end": v(-9.26, 17.08) * mm});
            skLineSegment(sketch, "E1824", {"start": v(-9.26, 17.08) * mm, "end": v(-9.95, 20.3) * mm});
            skLineSegment(sketch, "E1825", {"start": v(-9.95, 20.3) * mm, "end": v(-10.08, 24.47) * mm});
            skLineSegment(sketch, "E1826", {"start": v(-10.08, 24.47) * mm, "end": v(-9.32, 28.44) * mm});
            skLineSegment(sketch, "E1827", {"start": v(-9.32, 28.44) * mm, "end": v(-8.17, 31.26) * mm});
            skLineSegment(sketch, "E1828", {"start": v(-8.17, 31.26) * mm, "end": v(-7.65, 32.12) * mm});
            skLineSegment(sketch, "E1829", {"start": v(-7.65, 32.12) * mm, "end": v(-7.28, 32.73) * mm});
            skLineSegment(sketch, "E1830", {"start": v(-7.28, 32.73) * mm, "end": v(-5.03, 35.44) * mm});
            skLineSegment(sketch, "E1831", {"start": v(-5.03, 35.44) * mm, "end": v(-2.3, 37.66) * mm});
            skLineSegment(sketch, "E1832", {"start": v(-2.3, 37.66) * mm, "end": v(-1.68, 38.03) * mm});
            skLineSegment(sketch, "E1833", {"start": v(-1.68, 38.03) * mm, "end": v(-2.14, 38) * mm});
            skLineSegment(sketch, "E1834", {"start": v(-2.14, 38) * mm, "end": v(-6.71, 37.47) * mm});
            skLineSegment(sketch, "E1835", {"start": v(-6.71, 37.47) * mm, "end": v(-7.16, 37.38) * mm});
            skLineSegment(sketch, "E1836", {"start": v(-7.16, 37.38) * mm, "end": v(-7.94, 37.1) * mm});
            skLineSegment(sketch, "E1837", {"start": v(-7.94, 37.1) * mm, "end": v(-10.21, 36.05) * mm});
            skLineSegment(sketch, "E1838", {"start": v(-10.21, 36.05) * mm, "end": v(-12.94, 34.29) * mm});
            skLineSegment(sketch, "E1839", {"start": v(-12.94, 34.29) * mm, "end": v(-15.3, 32.1) * mm});
            skLineSegment(sketch, "E1840", {"start": v(-15.3, 32.1) * mm, "end": v(-16.8, 30.2) * mm});
            skLineSegment(sketch, "E1841", {"start": v(-16.8, 30.2) * mm, "end": v(-17.22, 29.5) * mm});
            skLineSegment(sketch, "E1842", {"start": v(-30.87, 22.16) * mm, "end": v(-31.72, 20.99) * mm});
            skLineSegment(sketch, "E1843", {"start": v(-31.72, 20.99) * mm, "end": v(-33.9, 17.21) * mm});
            skLineSegment(sketch, "E1844", {"start": v(-33.9, 17.21) * mm, "end": v(-36.14, 11.8) * mm});
            skLineSegment(sketch, "E1845", {"start": v(-36.14, 11.8) * mm, "end": v(-37.55, 6.01) * mm});
            skLineSegment(sketch, "E1846", {"start": v(-37.55, 6.01) * mm, "end": v(-38.03, 1.43) * mm});
            skLineSegment(sketch, "E1847", {"start": v(-38.03, 1.43) * mm, "end": v(-38.03, -0.1) * mm});
            skLineSegment(sketch, "E1848", {"start": v(-38.03, -0.1) * mm, "end": v(-38.03, -0.33) * mm});
            skLineSegment(sketch, "E1849", {"start": v(-38.03, -0.33) * mm, "end": v(-38.02, -0.97) * mm});
            skLineSegment(sketch, "E1850", {"start": v(-38.02, -0.97) * mm, "end": v(-38.01, -1.05) * mm});
            skLineSegment(sketch, "E1851", {"start": v(-38.01, -1.05) * mm, "end": v(-37.93, -1.48) * mm});
            skLineSegment(sketch, "E1852", {"start": v(-37.93, -1.48) * mm, "end": v(-36.68, -5.91) * mm});
            skLineSegment(sketch, "E1853", {"start": v(-36.68, -5.91) * mm, "end": v(-36.52, -6.36) * mm});
            skLineSegment(sketch, "E1854", {"start": v(-36.52, -6.36) * mm, "end": v(-36.21, -7.21) * mm});
            skLineSegment(sketch, "E1855", {"start": v(-36.21, -7.21) * mm, "end": v(-35.11, -9.73) * mm});
            skLineSegment(sketch, "E1856", {"start": v(-35.11, -9.73) * mm, "end": v(-33.38, -12.99) * mm});
            skLineSegment(sketch, "E1857", {"start": v(-33.38, -12.99) * mm, "end": v(-31.35, -16.11) * mm});
            skLineSegment(sketch, "E1858", {"start": v(-31.35, -16.11) * mm, "end": v(-29.04, -19.09) * mm});
            skLineSegment(sketch, "E1859", {"start": v(-29.04, -19.09) * mm, "end": v(-26.45, -21.9) * mm});
            skLineSegment(sketch, "E1860", {"start": v(-26.45, -21.9) * mm, "end": v(-23.6, -24.5) * mm});
            skLineSegment(sketch, "E1861", {"start": v(-23.6, -24.5) * mm, "end": v(-20.5, -26.92) * mm});
            skLineSegment(sketch, "E1862", {"start": v(-20.5, -26.92) * mm, "end": v(-18.03, -28.6) * mm});
            skLineSegment(sketch, "E1863", {"start": v(-18.03, -28.6) * mm, "end": v(-17.18, -29.12) * mm});
            skLineSegment(sketch, "E1864", {"start": v(-17.18, -29.12) * mm, "end": v(-15.8, -29.96) * mm});
            skLineSegment(sketch, "E1865", {"start": v(-15.8, -29.96) * mm, "end": v(-11.42, -32.12) * mm});
            skLineSegment(sketch, "E1866", {"start": v(-11.42, -32.12) * mm, "end": v(-5.45, -34.28) * mm});
            skLineSegment(sketch, "E1867", {"start": v(-5.45, -34.28) * mm, "end": v(0.62, -35.6) * mm});
            skLineSegment(sketch, "E1868", {"start": v(0.62, -35.6) * mm, "end": v(5.18, -36.04) * mm});
            skLineSegment(sketch, "E1869", {"start": v(5.18, -36.04) * mm, "end": v(6.7, -36.04) * mm});
            skLineSegment(sketch, "E1870", {"start": v(6.7, -36.04) * mm, "end": v(8.01, -36.04) * mm});
            skLineSegment(sketch, "E1871", {"start": v(8.01, -36.04) * mm, "end": v(11.54, -35.75) * mm});
            skLineSegment(sketch, "E1872", {"start": v(11.54, -35.75) * mm, "end": v(11.97, -35.7) * mm});
            skLineSegment(sketch, "E1873", {"start": v(11.97, -35.7) * mm, "end": v(12.26, -35.65) * mm});
            skLineSegment(sketch, "E1874", {"start": v(12.26, -35.65) * mm, "end": v(15.09, -35.14) * mm});
            skLineSegment(sketch, "E1875", {"start": v(15.09, -35.14) * mm, "end": v(15.36, -35.08) * mm});
            skLineSegment(sketch, "E1876", {"start": v(15.36, -35.08) * mm, "end": v(16.26, -34.68) * mm});
            skLineSegment(sketch, "E1877", {"start": v(16.26, -34.68) * mm, "end": v(20.56, -32.3) * mm});
            skLineSegment(sketch, "E1878", {"start": v(20.56, -32.3) * mm, "end": v(24.53, -29.43) * mm});
            skLineSegment(sketch, "E1879", {"start": v(24.53, -29.43) * mm, "end": v(25.27, -28.78) * mm});
            skLineSegment(sketch, "E1880", {"start": v(25.27, -28.78) * mm, "end": v(24.56, -29.28) * mm});
            skLineSegment(sketch, "E1881", {"start": v(24.56, -29.28) * mm, "end": v(22.28, -30.6) * mm});
            skLineSegment(sketch, "E1882", {"start": v(22.28, -30.6) * mm, "end": v(19.01, -32.06) * mm});
            skLineSegment(sketch, "E1883", {"start": v(19.01, -32.06) * mm, "end": v(15.48, -33.16) * mm});
            skLineSegment(sketch, "E1884", {"start": v(15.48, -33.16) * mm, "end": v(12.66, -33.75) * mm});
            skLineSegment(sketch, "E1885", {"start": v(12.66, -33.75) * mm, "end": v(11.71, -33.87) * mm});
            skLineSegment(sketch, "E1886", {"start": v(11.71, -33.87) * mm, "end": v(10.85, -34) * mm});
            skLineSegment(sketch, "E1887", {"start": v(10.85, -34) * mm, "end": v(8.23, -34.18) * mm});
            skLineSegment(sketch, "E1888", {"start": v(8.23, -34.18) * mm, "end": v(4.7, -34.16) * mm});
            skLineSegment(sketch, "E1889", {"start": v(4.7, -34.16) * mm, "end": v(1.14, -33.82) * mm});
            skLineSegment(sketch, "E1890", {"start": v(1.14, -33.82) * mm, "end": v(-2.42, -33.18) * mm});
            skLineSegment(sketch, "E1891", {"start": v(-2.42, -33.18) * mm, "end": v(-5.96, -32.22) * mm});
            skLineSegment(sketch, "E1892", {"start": v(-5.96, -32.22) * mm, "end": v(-9.45, -30.96) * mm});
            skLineSegment(sketch, "E1893", {"start": v(-9.45, -30.96) * mm, "end": v(-12.89, -29.4) * mm});
            skLineSegment(sketch, "E1894", {"start": v(-12.89, -29.4) * mm, "end": v(-15.42, -28.04) * mm});
            skLineSegment(sketch, "E1895", {"start": v(-15.42, -28.04) * mm, "end": v(-16.24, -27.55) * mm});
            skLineSegment(sketch, "E1896", {"start": v(-16.24, -27.55) * mm, "end": v(-17.06, -27.05) * mm});
            skLineSegment(sketch, "E1897", {"start": v(-17.06, -27.05) * mm, "end": v(-19.43, -25.44) * mm});
            skLineSegment(sketch, "E1898", {"start": v(-19.43, -25.44) * mm, "end": v(-22.4, -23.12) * mm});
            skLineSegment(sketch, "E1899", {"start": v(-22.4, -23.12) * mm, "end": v(-25.14, -20.61) * mm});
            skLineSegment(sketch, "E1900", {"start": v(-25.14, -20.61) * mm, "end": v(-27.63, -17.92) * mm});
            skLineSegment(sketch, "E1901", {"start": v(-27.63, -17.92) * mm, "end": v(-29.85, -15.07) * mm});
            skLineSegment(sketch, "E1902", {"start": v(-29.85, -15.07) * mm, "end": v(-31.8, -12.08) * mm});
            skLineSegment(sketch, "E1903", {"start": v(-31.8, -12.08) * mm, "end": v(-33.45, -8.96) * mm});
            skLineSegment(sketch, "E1904", {"start": v(-33.45, -8.96) * mm, "end": v(-34.5, -6.55) * mm});
            skLineSegment(sketch, "E1905", {"start": v(-34.5, -6.55) * mm, "end": v(-34.8, -5.72) * mm});
            skLineSegment(sketch, "E1906", {"start": v(-34.8, -5.72) * mm, "end": v(-35.28, -4.41) * mm});
            skLineSegment(sketch, "E1907", {"start": v(-35.28, -4.41) * mm, "end": v(-36.29, -0.32) * mm});
            skLineSegment(sketch, "E1908", {"start": v(-36.29, -0.32) * mm, "end": v(-36.8, 4.99) * mm});
            skLineSegment(sketch, "E1909", {"start": v(-36.8, 4.99) * mm, "end": v(-36.36, 10.1) * mm});
            skLineSegment(sketch, "E1910", {"start": v(-36.36, 10.1) * mm, "end": v(-35.42, 13.78) * mm});
            skLineSegment(sketch, "E1911", {"start": v(-35.42, 13.78) * mm, "end": v(-34.95, 14.94) * mm});
            skLineSegment(sketch, "E1912", {"start": v(-34.95, 14.94) * mm, "end": v(-35.07, 14.03) * mm});
            skLineSegment(sketch, "E1913", {"start": v(-35.07, 14.03) * mm, "end": v(-35.18, 11.25) * mm});
            skLineSegment(sketch, "E1914", {"start": v(-35.18, 11.25) * mm, "end": v(-34.92, 7.45) * mm});
            skLineSegment(sketch, "E1915", {"start": v(-34.92, 7.45) * mm, "end": v(-34.16, 3.58) * mm});
            skLineSegment(sketch, "E1916", {"start": v(-34.16, 3.58) * mm, "end": v(-33.27, 0.62) * mm});
            skLineSegment(sketch, "E1917", {"start": v(-33.27, 0.62) * mm, "end": v(-32.9, -0.34) * mm});
            skLineSegment(sketch, "E1918", {"start": v(-32.9, -0.34) * mm, "end": v(-32.58, -1.18) * mm});
            skLineSegment(sketch, "E1919", {"start": v(-32.58, -1.18) * mm, "end": v(-31.46, -3.65) * mm});
            skLineSegment(sketch, "E1920", {"start": v(-31.46, -3.65) * mm, "end": v(-29.7, -6.86) * mm});
            skLineSegment(sketch, "E1921", {"start": v(-29.7, -6.86) * mm, "end": v(-27.64, -9.94) * mm});
            skLineSegment(sketch, "E1922", {"start": v(-27.64, -9.94) * mm, "end": v(-25.3, -12.87) * mm});
            skLineSegment(sketch, "E1923", {"start": v(-25.3, -12.87) * mm, "end": v(-22.69, -15.65) * mm});
            skLineSegment(sketch, "E1924", {"start": v(-22.69, -15.65) * mm, "end": v(-19.83, -18.24) * mm});
            skLineSegment(sketch, "E1925", {"start": v(-19.83, -18.24) * mm, "end": v(-16.73, -20.64) * mm});
            skLineSegment(sketch, "E1926", {"start": v(-16.73, -20.64) * mm, "end": v(-14.26, -22.3) * mm});
            skLineSegment(sketch, "E1927", {"start": v(-14.26, -22.3) * mm, "end": v(-13.4, -22.82) * mm});
            skLineSegment(sketch, "E1928", {"start": v(-13.4, -22.82) * mm, "end": v(-11.98, -23.68) * mm});
            skLineSegment(sketch, "E1929", {"start": v(-11.98, -23.68) * mm, "end": v(-7.5, -25.9) * mm});
            skLineSegment(sketch, "E1930", {"start": v(-7.5, -25.9) * mm, "end": v(-1.4, -28.12) * mm});
            skLineSegment(sketch, "E1931", {"start": v(-1.4, -28.12) * mm, "end": v(4.78, -29.48) * mm});
            skLineSegment(sketch, "E1932", {"start": v(4.78, -29.48) * mm, "end": v(9.41, -29.93) * mm});
            skLineSegment(sketch, "E1933", {"start": v(9.41, -29.93) * mm, "end": v(10.96, -29.93) * mm});
            skLineSegment(sketch, "E1934", {"start": v(10.96, -29.93) * mm, "end": v(12.11, -29.93) * mm});
            skLineSegment(sketch, "E1935", {"start": v(12.11, -29.93) * mm, "end": v(15.2, -29.71) * mm});
            skLineSegment(sketch, "E1936", {"start": v(15.2, -29.71) * mm, "end": v(15.57, -29.67) * mm});
            skLineSegment(sketch, "E1937", {"start": v(15.57, -29.67) * mm, "end": v(16.5, -29.56) * mm});
            skLineSegment(sketch, "E1938", {"start": v(16.5, -29.56) * mm, "end": v(19.25, -29.05) * mm});
            skLineSegment(sketch, "E1939", {"start": v(19.25, -29.05) * mm, "end": v(22.7, -28.09) * mm});
            skLineSegment(sketch, "E1940", {"start": v(22.7, -28.09) * mm, "end": v(25.92, -26.8) * mm});
            skLineSegment(sketch, "E1941", {"start": v(25.92, -26.8) * mm, "end": v(28.17, -25.62) * mm});
            skLineSegment(sketch, "E1942", {"start": v(28.17, -25.62) * mm, "end": v(28.89, -25.18) * mm});
            skLineSegment(sketch, "E1943", {"start": v(28.89, -25.18) * mm, "end": v(29.3, -24.71) * mm});
            skLineSegment(sketch, "E1944", {"start": v(29.3, -24.71) * mm, "end": v(31.2, -22.26) * mm});
            skLineSegment(sketch, "E1945", {"start": v(31.2, -22.26) * mm, "end": v(32.9, -19.67) * mm});
            skLineSegment(sketch, "E1946", {"start": v(32.9, -19.67) * mm, "end": v(33.21, -19.13) * mm});
            skSolve(sketch);
        }
        {
            var Q0;
            Q0=makeQuery(id+"F0.imprint","IMPRINT",FACE,{"disambiguationData":[TD([[makeQuery(id+"F0.imprint","IMPRINT",EDGE,{"derivedFrom":sQuery(id+"F0.wireOp",EDGE,"E174")}),1.0]])]});
            var Q1;
            {var subQ30=sQuery(id+"F0.wireOp",EDGE,"E1326");Q1=makeQuery(id+"F0.imprint","IMPRINT",FACE,{"disambiguationData":[TD([[makeQuery(id+"F0.imprint","IMPRINT",EDGE,{"derivedFrom":subQ30}),1.0]])]});}
            var Q2;
            Q2=makeQuery(id+"F0.imprint","IMPRINT",FACE,{"disambiguationData":[TD([[makeQuery(id+"F0.imprint","IMPRINT",EDGE,{"derivedFrom":sQuery(id+"F0.wireOp",EDGE,"E174")}),-1.0]])]});
            var Q3;
            {var subQ19=sQuery(id+"F0.wireOp",EDGE,"E489");Q3=makeQuery(id+"F0.imprint","IMPRINT",FACE,{"disambiguationData":[TD([[makeQuery(id+"F0.imprint","IMPRINT",EDGE,{"derivedFrom":subQ19}),1.0]])]});}
            var Q4;
            {var subQ16=sQuery(id+"F0.wireOp",EDGE,"E149");Q4=makeQuery(id+"F0.imprint","IMPRINT",FACE,{"disambiguationData":[TD([[makeQuery(id+"F0.imprint","IMPRINT",EDGE,{"derivedFrom":subQ16}),-1.0]])]});}
            var Q5;
            Q5=makeQuery(id+"F0.imprint","IMPRINT",FACE,{"disambiguationData":[TD([[makeQuery(id+"F0.imprint","IMPRINT",EDGE,{"derivedFrom":sQuery(id+"F0.wireOp",EDGE,"E0")}),1.0]])]});
            var Q6;
            Q6=makeQuery(id+"F0.imprint","IMPRINT",FACE,{"disambiguationData":[TD([[makeQuery(id+"F0.imprint","IMPRINT",EDGE,{"derivedFrom":sQuery(id+"F0.wireOp",EDGE,"E0")}),-1.0]])]});
            var Q7;
            Q7=makeQuery(id+"F0.imprint","IMPRINT",FACE,{"disambiguationData":[TD([[makeQuery(id+"F0.imprint","IMPRINT",EDGE,{"derivedFrom":sQuery(id+"F0.wireOp",EDGE,"E1438")}),1.0]])]});
            var Q8;
            {var subQ12=sQuery(id+"F0.wireOp",EDGE,"E79");Q8=makeQuery(id+"F0.imprint","IMPRINT",FACE,{"disambiguationData":[TD([[makeQuery(id+"F0.imprint","IMPRINT",EDGE,{"derivedFrom":subQ12}),1.0]])]});}
            var Q9;
            {var subQ16=sQuery(id+"F0.wireOp",EDGE,"E64");Q9=makeQuery(id+"F0.imprint","IMPRINT",FACE,{"disambiguationData":[TD([[makeQuery(id+"F0.imprint","IMPRINT",EDGE,{"derivedFrom":subQ16}),-1.0]])]});}
            var Q10;
            {var subQ2=sQuery(id+"F0.wireOp",EDGE,"E195");Q10=makeQuery(id+"F0.imprint","IMPRINT",FACE,{"disambiguationData":[TD([[makeQuery(id+"F0.imprint","IMPRINT",EDGE,{"derivedFrom":subQ2}),1.0]])]});}
            var Q11;
            Q11=makeQuery(id+"F0.imprint","IMPRINT",FACE,{"disambiguationData":[TD([[makeQuery(id+"F0.imprint","IMPRINT",EDGE,{"derivedFrom":sQuery(id+"F0.wireOp",EDGE,"E1678")}),-1.0]])]});
            var Q12;
            {var subQ8=sQuery(id+"F0.wireOp",EDGE,"E40");Q12=makeQuery(id+"F0.imprint","IMPRINT",FACE,{"disambiguationData":[TD([[makeQuery(id+"F0.imprint","IMPRINT",EDGE,{"derivedFrom":subQ8}),-1.0]])]});}
            var Q13;
            {var subQ23=sQuery(id+"F0.wireOp",EDGE,"E40");Q13=makeQuery(id+"F0.imprint","IMPRINT",FACE,{"disambiguationData":[TD([[makeQuery(id+"F0.imprint","IMPRINT",EDGE,{"derivedFrom":subQ23}),1.0]])]});}
            var Q14;
            {var subQ73=sQuery(id+"F0.wireOp",EDGE,"E17");Q14=makeQuery(id+"F0.imprint","IMPRINT",FACE,{"disambiguationData":[TD([[makeQuery(id+"F0.imprint","IMPRINT",EDGE,{"derivedFrom":subQ73}),-1.0]])]});}
            var Q15;
            {var subQ6=sQuery(id+"F0.wireOp",EDGE,"E190");Q15=makeQuery(id+"F0.imprint","IMPRINT",FACE,{"disambiguationData":[TD([[makeQuery(id+"F0.imprint","IMPRINT",EDGE,{"derivedFrom":subQ6}),1.0]])]});}
            var Q16;
            {var subQ3=sQuery(id+"F0.wireOp",EDGE,"E6");var subQ6=sQuery(id+"F0.wireOp",EDGE,"E320");var subQ10=makeQuery(id+"F0.imprint","INTERSECT",VERTEX,{"derivedFrom":[subQ3,subQ6]});Q16=makeQuery(id+"F0.imprint","IMPRINT",FACE,{"disambiguationData":[TD([[makeQuery(id+"F0.imprint","IMPRINT",EDGE,{"disambiguationData":[TD([[subQ10,-1.0]])],"derivedFrom":subQ3}),-1.0]])]});}
            var Q17;
            {var subQ9=sQuery(id+"F0.wireOp",EDGE,"E1518");Q17=makeQuery(id+"F0.imprint","IMPRINT",FACE,{"disambiguationData":[TD([[makeQuery(id+"F0.imprint","IMPRINT",EDGE,{"derivedFrom":subQ9}),1.0]])]});}
            var Q18;
            {var subQ6=sQuery(id+"F0.wireOp",EDGE,"E1695");Q18=makeQuery(id+"F0.imprint","IMPRINT",FACE,{"disambiguationData":[TD([[makeQuery(id+"F0.imprint","IMPRINT",EDGE,{"derivedFrom":subQ6}),-1.0]])]});}
            var Q19;
            {var subQ0=sQuery(id+"F0.wireOp",EDGE,"E1931");var subQ1=sQuery(id+"F0.wireOp",EDGE,"E321");var subQ2=makeQuery(id+"F0.imprint","INTERSECT",VERTEX,{"derivedFrom":[subQ1,subQ0]});Q19=makeQuery(id+"F0.imprint","IMPRINT",FACE,{"disambiguationData":[TD([[makeQuery(id+"F0.imprint","IMPRINT",EDGE,{"disambiguationData":[TD([[subQ2,-1.0]])],"derivedFrom":subQ1}),1.0]])]});}
            var Q20;
            {var subQ12=sQuery(id+"F0.wireOp",EDGE,"E103");Q20=makeQuery(id+"F0.imprint","IMPRINT",FACE,{"disambiguationData":[TD([[makeQuery(id+"F0.imprint","IMPRINT",EDGE,{"derivedFrom":subQ12}),1.0]])]});}
            var Q21;
            {var subQ8=sQuery(id+"F0.wireOp",EDGE,"E7");Q21=makeQuery(id+"F0.imprint","IMPRINT",FACE,{"disambiguationData":[TD([[makeQuery(id+"F0.imprint","IMPRINT",EDGE,{"derivedFrom":subQ8}),1.0]])]});}
            var Q22;
            {var subQ0=sQuery(id+"F0.wireOp",EDGE,"E320");var subQ3=sQuery(id+"F0.wireOp",EDGE,"E6");var subQ4=makeQuery(id+"F0.imprint","INTERSECT",VERTEX,{"derivedFrom":[subQ3,subQ0]});Q22=makeQuery(id+"F0.imprint","IMPRINT",FACE,{"disambiguationData":[TD([[makeQuery(id+"F0.imprint","IMPRINT",EDGE,{"disambiguationData":[TD([[subQ4,-1.0]])],"derivedFrom":subQ3}),1.0]])]});}
            var Q23;
            {var subQ8=sQuery(id+"F0.wireOp",EDGE,"E7");Q23=makeQuery(id+"F0.imprint","IMPRINT",FACE,{"disambiguationData":[TD([[makeQuery(id+"F0.imprint","IMPRINT",EDGE,{"derivedFrom":subQ8}),-1.0]])]});}
            var Q24;
            {var subQ0=sQuery(id+"F0.wireOp",EDGE,"E1889");var subQ1=sQuery(id+"F0.wireOp",EDGE,"E321");var subQ2=makeQuery(id+"F0.imprint","INTERSECT",VERTEX,{"derivedFrom":[subQ1,subQ0]});Q24=makeQuery(id+"F0.imprint","IMPRINT",FACE,{"disambiguationData":[TD([[makeQuery(id+"F0.imprint","IMPRINT",EDGE,{"disambiguationData":[TD([[subQ2,-1.0]])],"derivedFrom":subQ1}),1.0]])]});}
            var Q25;
            {var subQ4=sQuery(id+"F0.wireOp",EDGE,"E419");Q25=makeQuery(id+"F0.imprint","IMPRINT",FACE,{"disambiguationData":[TD([[makeQuery(id+"F0.imprint","IMPRINT",EDGE,{"derivedFrom":subQ4}),1.0]])]});}
            var Q26;
            {var subQ12=sQuery(id+"F0.wireOp",EDGE,"E192");Q26=makeQuery(id+"F0.imprint","IMPRINT",FACE,{"disambiguationData":[TD([[makeQuery(id+"F0.imprint","IMPRINT",EDGE,{"derivedFrom":subQ12}),1.0]])]});}
            var Q27;
            {var subQ12=sQuery(id+"F0.wireOp",EDGE,"E1750");Q27=makeQuery(id+"F0.imprint","IMPRINT",FACE,{"disambiguationData":[TD([[makeQuery(id+"F0.imprint","IMPRINT",EDGE,{"derivedFrom":subQ12}),-1.0]])]});}
            var Q28;
            {var subQ10=sQuery(id+"F0.wireOp",EDGE,"E32");Q28=makeQuery(id+"F0.imprint","IMPRINT",FACE,{"disambiguationData":[TD([[makeQuery(id+"F0.imprint","IMPRINT",EDGE,{"derivedFrom":subQ10}),-1.0]])]});}
            var Q29;
            {var subQ5=sQuery(id+"F0.wireOp",EDGE,"E1575");Q29=makeQuery(id+"F0.imprint","IMPRINT",FACE,{"disambiguationData":[TD([[makeQuery(id+"F0.imprint","IMPRINT",EDGE,{"derivedFrom":subQ5}),-1.0]])]});}
            var Q30;
            {var subQ7=sQuery(id+"F0.wireOp",EDGE,"E26");Q30=makeQuery(id+"F0.imprint","IMPRINT",FACE,{"disambiguationData":[TD([[makeQuery(id+"F0.imprint","IMPRINT",EDGE,{"derivedFrom":subQ7}),-1.0]])]});}
            var Q31;
            {var subQ11=sQuery(id+"F0.wireOp",EDGE,"E211");Q31=makeQuery(id+"F0.imprint","IMPRINT",FACE,{"disambiguationData":[TD([[makeQuery(id+"F0.imprint","IMPRINT",EDGE,{"derivedFrom":subQ11}),1.0]])]});}
            var Q32;
            {var subQ15=sQuery(id+"F0.wireOp",EDGE,"E330");Q32=makeQuery(id+"F0.imprint","IMPRINT",FACE,{"disambiguationData":[TD([[makeQuery(id+"F0.imprint","IMPRINT",EDGE,{"derivedFrom":subQ15}),1.0]])]});}
            var Q33;
            Q33=makeQuery(id+"F0.imprint","IMPRINT",FACE,{"disambiguationData":[TD([[makeQuery(id+"F0.imprint","IMPRINT",EDGE,{"derivedFrom":sQuery(id+"F0.wireOp",EDGE,"E265")}),1.0]])]});
            var Q34;
            {var subQ5=sQuery(id+"F0.wireOp",EDGE,"E230");Q34=makeQuery(id+"F0.imprint","IMPRINT",FACE,{"disambiguationData":[TD([[makeQuery(id+"F0.imprint","IMPRINT",EDGE,{"derivedFrom":subQ5}),-1.0]])]});}
            var Q35;
            {var subQ5=sQuery(id+"F0.wireOp",EDGE,"E100");Q35=makeQuery(id+"F0.imprint","IMPRINT",FACE,{"disambiguationData":[TD([[makeQuery(id+"F0.imprint","IMPRINT",EDGE,{"derivedFrom":subQ5}),1.0]])]});}
            var Q36;
            {var subQ1=sQuery(id+"F0.wireOp",EDGE,"E31");var subQ7=sQuery(id+"F0.wireOp",EDGE,"E379");var subQ9=makeQuery(id+"F0.imprint","INTERSECT",VERTEX,{"derivedFrom":[subQ1,subQ7]});Q36=makeQuery(id+"F0.imprint","IMPRINT",FACE,{"disambiguationData":[TD([[makeQuery(id+"F0.imprint","IMPRINT",EDGE,{"disambiguationData":[TD([[subQ9,-1.0]])],"derivedFrom":subQ1}),-1.0]])]});}
            var Q37;
            {var subQ7=sQuery(id+"F0.wireOp",EDGE,"E316");Q37=makeQuery(id+"F0.imprint","IMPRINT",FACE,{"disambiguationData":[TD([[makeQuery(id+"F0.imprint","IMPRINT",EDGE,{"derivedFrom":subQ7}),1.0]])]});}
            var Q38;
            {var subQ0=sQuery(id+"F0.wireOp",EDGE,"E385");var subQ1=sQuery(id+"F0.wireOp",EDGE,"E107");var subQ2=makeQuery(id+"F0.imprint","INTERSECT",VERTEX,{"derivedFrom":[subQ1,subQ0]});Q38=makeQuery(id+"F0.imprint","IMPRINT",FACE,{"disambiguationData":[TD([[makeQuery(id+"F0.imprint","IMPRINT",EDGE,{"disambiguationData":[TD([[subQ2,-1.0]])],"derivedFrom":subQ1}),1.0]])]});}
            var Q39;
            {var subQ1=sQuery(id+"F0.wireOp",EDGE,"E101");var subQ7=sQuery(id+"F0.wireOp",EDGE,"E102");var subQ8=makeQuery(id+"F0.imprint","INTERSECT",VERTEX,{"derivedFrom":[subQ1,subQ7]});Q39=makeQuery(id+"F0.imprint","IMPRINT",FACE,{"disambiguationData":[TD([[makeQuery(id+"F0.imprint","IMPRINT",EDGE,{"disambiguationData":[TD([[subQ8,1.0]])],"derivedFrom":subQ1}),1.0]])]});}
            var Q40;
            {var subQ14=sQuery(id+"F0.wireOp",EDGE,"E1735");Q40=makeQuery(id+"F0.imprint","IMPRINT",FACE,{"disambiguationData":[TD([[makeQuery(id+"F0.imprint","IMPRINT",EDGE,{"derivedFrom":subQ14}),-1.0]])]});}
            var Q41;
            {var subQ4=sQuery(id+"F0.wireOp",EDGE,"E1575");Q41=makeQuery(id+"F0.imprint","IMPRINT",FACE,{"disambiguationData":[TD([[makeQuery(id+"F0.imprint","IMPRINT",EDGE,{"derivedFrom":subQ4}),1.0]])]});}
            var Q42;
            {var subQ3=sQuery(id+"F0.wireOp",EDGE,"E1574");var subQ9=sQuery(id+"F0.wireOp",EDGE,"E1573");var subQ10=makeQuery(id+"F0.imprint","INTERSECT",VERTEX,{"derivedFrom":[subQ9,subQ3]});Q42=makeQuery(id+"F0.imprint","IMPRINT",FACE,{"disambiguationData":[TD([[makeQuery(id+"F0.imprint","IMPRINT",EDGE,{"disambiguationData":[TD([[subQ10,1.0]])],"derivedFrom":subQ9}),-1.0]])]});}
            var Q43;
            Q43=makeQuery(id+"F0.imprint","IMPRINT",FACE,{"disambiguationData":[TD([[makeQuery(id+"F0.imprint","IMPRINT",EDGE,{"derivedFrom":sQuery(id+"F0.wireOp",EDGE,"E391")}),1.0]])]});
            var Q44;
            {var subQ1=sQuery(id+"F0.wireOp",EDGE,"E1539");Q44=makeQuery(id+"F0.imprint","IMPRINT",FACE,{"disambiguationData":[TD([[makeQuery(id+"F0.imprint","IMPRINT",EDGE,{"derivedFrom":subQ1}),1.0]])]});}
            var Q45;
            {var subQ0=sQuery(id+"F0.wireOp",EDGE,"E131");Q45=makeQuery(id+"F0.imprint","IMPRINT",FACE,{"disambiguationData":[TD([[makeQuery(id+"F0.imprint","IMPRINT",EDGE,{"derivedFrom":subQ0}),1.0]])]});}
            var Q46;
            {var subQ13=sQuery(id+"F0.wireOp",EDGE,"E249");Q46=makeQuery(id+"F0.imprint","IMPRINT",FACE,{"disambiguationData":[TD([[makeQuery(id+"F0.imprint","IMPRINT",EDGE,{"derivedFrom":subQ13}),1.0]])]});}
            var Q47;
            {var subQ5=sQuery(id+"F0.wireOp",EDGE,"E251");Q47=makeQuery(id+"F0.imprint","IMPRINT",FACE,{"disambiguationData":[TD([[makeQuery(id+"F0.imprint","IMPRINT",EDGE,{"derivedFrom":subQ5}),1.0]])]});}
            var Q48;
            {var subQ11=sQuery(id+"F0.wireOp",EDGE,"E195");Q48=makeQuery(id+"F0.imprint","IMPRINT",FACE,{"disambiguationData":[TD([[makeQuery(id+"F0.imprint","IMPRINT",EDGE,{"derivedFrom":subQ11}),-1.0]])]});}
            var Q49;
            {var subQ5=sQuery(id+"F0.wireOp",EDGE,"E1911");Q49=makeQuery(id+"F0.imprint","IMPRINT",FACE,{"disambiguationData":[TD([[makeQuery(id+"F0.imprint","IMPRINT",EDGE,{"derivedFrom":subQ5}),-1.0]])]});}
            var Q50;
            {var subQ12=sQuery(id+"F0.wireOp",EDGE,"E61");Q50=makeQuery(id+"F0.imprint","IMPRINT",FACE,{"disambiguationData":[TD([[makeQuery(id+"F0.imprint","IMPRINT",EDGE,{"derivedFrom":subQ12}),-1.0]])]});}
            var Q51;
            {var subQ0=sQuery(id+"F0.wireOp",EDGE,"E1700");Q51=makeQuery(id+"F0.imprint","IMPRINT",FACE,{"disambiguationData":[TD([[makeQuery(id+"F0.imprint","IMPRINT",EDGE,{"derivedFrom":subQ0}),1.0]])]});}
            var Q52;
            {var subQ1=sQuery(id+"F0.wireOp",EDGE,"E1560");Q52=makeQuery(id+"F0.imprint","IMPRINT",FACE,{"disambiguationData":[TD([[makeQuery(id+"F0.imprint","IMPRINT",EDGE,{"derivedFrom":subQ1}),1.0]])]});}
            var Q53;
            {var subQ5=sQuery(id+"F0.wireOp",EDGE,"E110");Q53=makeQuery(id+"F0.imprint","IMPRINT",FACE,{"disambiguationData":[TD([[makeQuery(id+"F0.imprint","IMPRINT",EDGE,{"derivedFrom":subQ5}),1.0]])]});}
            var Q54;
            {var subQ5=sQuery(id+"F0.wireOp",EDGE,"E109");var subQ6=sQuery(id+"F0.wireOp",EDGE,"E108");var subQ7=makeQuery(id+"F0.imprint","INTERSECT",VERTEX,{"derivedFrom":[subQ6,subQ5]});Q54=makeQuery(id+"F0.imprint","IMPRINT",FACE,{"disambiguationData":[TD([[makeQuery(id+"F0.imprint","IMPRINT",EDGE,{"disambiguationData":[TD([[subQ7,1.0]])],"derivedFrom":subQ6}),1.0]])]});}
            var Q55;
            {var subQ11=sQuery(id+"F0.wireOp",EDGE,"E1753");Q55=makeQuery(id+"F0.imprint","IMPRINT",FACE,{"disambiguationData":[TD([[makeQuery(id+"F0.imprint","IMPRINT",EDGE,{"derivedFrom":subQ11}),-1.0]])]});}
            var Q56;
            {var subQ9=sQuery(id+"F0.wireOp",EDGE,"E133");Q56=makeQuery(id+"F0.imprint","IMPRINT",FACE,{"disambiguationData":[TD([[makeQuery(id+"F0.imprint","IMPRINT",EDGE,{"derivedFrom":subQ9}),-1.0]])]});}
            var Q57;
            {var subQ0=sQuery(id+"F0.wireOp",EDGE,"E1562");Q57=makeQuery(id+"F0.imprint","IMPRINT",FACE,{"disambiguationData":[TD([[makeQuery(id+"F0.imprint","IMPRINT",EDGE,{"derivedFrom":subQ0}),1.0]])]});}
            var Q58;
            {var subQ1=sQuery(id+"F0.wireOp",EDGE,"E131");Q58=makeQuery(id+"F0.imprint","IMPRINT",FACE,{"disambiguationData":[TD([[makeQuery(id+"F0.imprint","IMPRINT",EDGE,{"derivedFrom":subQ1}),-1.0]])]});}
            var Q59;
            {var subQ3=sQuery(id+"F0.wireOp",EDGE,"E200");var subQ6=sQuery(id+"F0.wireOp",EDGE,"E1733");var subQ10=makeQuery(id+"F0.imprint","INTERSECT",VERTEX,{"derivedFrom":[subQ3,subQ6]});Q59=makeQuery(id+"F0.imprint","IMPRINT",FACE,{"disambiguationData":[TD([[makeQuery(id+"F0.imprint","IMPRINT",EDGE,{"disambiguationData":[TD([[subQ10,-1.0]])],"derivedFrom":subQ3}),-1.0]])]});}
            var Q60;
            {var subQ0=sQuery(id+"F0.wireOp",EDGE,"E426");var subQ1=sQuery(id+"F0.wireOp",EDGE,"E25");var subQ2=makeQuery(id+"F0.imprint","INTERSECT",VERTEX,{"derivedFrom":[subQ1,subQ0]});Q60=makeQuery(id+"F0.imprint","IMPRINT",FACE,{"disambiguationData":[TD([[makeQuery(id+"F0.imprint","IMPRINT",EDGE,{"disambiguationData":[TD([[subQ2,-1.0]])],"derivedFrom":subQ1}),-1.0]])]});}
            var Q61;
            {var subQ5=sQuery(id+"F0.wireOp",EDGE,"E201");Q61=makeQuery(id+"F0.imprint","IMPRINT",FACE,{"disambiguationData":[TD([[makeQuery(id+"F0.imprint","IMPRINT",EDGE,{"derivedFrom":subQ5}),1.0]])]});}
            var Q62;
            {var subQ14=sQuery(id+"F0.wireOp",EDGE,"E127");Q62=makeQuery(id+"F0.imprint","IMPRINT",FACE,{"disambiguationData":[TD([[makeQuery(id+"F0.imprint","IMPRINT",EDGE,{"derivedFrom":subQ14}),-1.0]])]});}
            var Q63;
            {var subQ0=sQuery(id+"F0.wireOp",EDGE,"E1572");Q63=makeQuery(id+"F0.imprint","IMPRINT",FACE,{"disambiguationData":[TD([[makeQuery(id+"F0.imprint","IMPRINT",EDGE,{"derivedFrom":subQ0}),1.0]])]});}
            var Q64;
            {var subQ15=sQuery(id+"F0.wireOp",EDGE,"E1534");Q64=makeQuery(id+"F0.imprint","IMPRINT",FACE,{"disambiguationData":[TD([[makeQuery(id+"F0.imprint","IMPRINT",EDGE,{"derivedFrom":subQ15}),1.0]])]});}
            var Q65;
            {var subQ2=sQuery(id+"F0.wireOp",EDGE,"E1560");Q65=makeQuery(id+"F0.imprint","IMPRINT",FACE,{"disambiguationData":[TD([[makeQuery(id+"F0.imprint","IMPRINT",EDGE,{"derivedFrom":subQ2}),-1.0]])]});}
            var Q66;
            {var subQ8=sQuery(id+"F0.wireOp",EDGE,"E1539");Q66=makeQuery(id+"F0.imprint","IMPRINT",FACE,{"disambiguationData":[TD([[makeQuery(id+"F0.imprint","IMPRINT",EDGE,{"derivedFrom":subQ8}),-1.0]])]});}
            var Q67;
            {var subQ22=sQuery(id+"F0.wireOp",EDGE,"E211");Q67=makeQuery(id+"F0.imprint","IMPRINT",FACE,{"disambiguationData":[TD([[makeQuery(id+"F0.imprint","IMPRINT",EDGE,{"derivedFrom":subQ22}),-1.0]])]});}
            var Q68;
            {var subQ5=sQuery(id+"F0.wireOp",EDGE,"E1570");Q68=makeQuery(id+"F0.imprint","IMPRINT",FACE,{"disambiguationData":[TD([[makeQuery(id+"F0.imprint","IMPRINT",EDGE,{"derivedFrom":subQ5}),1.0]])]});}
            var Q69;
            {var subQ0=sQuery(id+"F0.wireOp",EDGE,"E1557");Q69=makeQuery(id+"F0.imprint","IMPRINT",FACE,{"disambiguationData":[TD([[makeQuery(id+"F0.imprint","IMPRINT",EDGE,{"derivedFrom":subQ0}),1.0]])]});}
            var Q70;
            {var subQ1=sQuery(id+"F0.wireOp",EDGE,"E229");var subQ7=sQuery(id+"F0.wireOp",EDGE,"E228");var subQ8=makeQuery(id+"F0.imprint","INTERSECT",VERTEX,{"derivedFrom":[subQ7,subQ1]});Q70=makeQuery(id+"F0.imprint","IMPRINT",FACE,{"disambiguationData":[TD([[makeQuery(id+"F0.imprint","IMPRINT",EDGE,{"disambiguationData":[TD([[subQ8,1.0]])],"derivedFrom":subQ7}),-1.0]])]});}
            var Q71;
            {var subQ19=sQuery(id+"F0.wireOp",EDGE,"E291");Q71=makeQuery(id+"F0.imprint","IMPRINT",FACE,{"disambiguationData":[TD([[makeQuery(id+"F0.imprint","IMPRINT",EDGE,{"derivedFrom":subQ19}),1.0]])]});}
            var Q72;
            {var subQ0=sQuery(id+"F0.wireOp",EDGE,"E113");Q72=makeQuery(id+"F0.imprint","IMPRINT",FACE,{"disambiguationData":[TD([[makeQuery(id+"F0.imprint","IMPRINT",EDGE,{"derivedFrom":subQ0}),1.0]])]});}
            var Q73;
            {var subQ1=sQuery(id+"F0.wireOp",EDGE,"E289");Q73=makeQuery(id+"F0.imprint","IMPRINT",FACE,{"disambiguationData":[TD([[makeQuery(id+"F0.imprint","IMPRINT",EDGE,{"derivedFrom":subQ1}),1.0]])]});}
            var Q74;
            {var subQ5=sQuery(id+"F0.wireOp",EDGE,"E307");Q74=makeQuery(id+"F0.imprint","IMPRINT",FACE,{"disambiguationData":[TD([[makeQuery(id+"F0.imprint","IMPRINT",EDGE,{"derivedFrom":subQ5}),1.0]])]});}
            var Q75;
            {var subQ0=sQuery(id+"F0.wireOp",EDGE,"E327");var subQ1=sQuery(id+"F0.wireOp",EDGE,"E130");var subQ2=makeQuery(id+"F0.imprint","INTERSECT",VERTEX,{"derivedFrom":[subQ1,subQ0]});Q75=makeQuery(id+"F0.imprint","IMPRINT",FACE,{"disambiguationData":[TD([[makeQuery(id+"F0.imprint","IMPRINT",EDGE,{"disambiguationData":[TD([[subQ2,-1.0]])],"derivedFrom":subQ1}),-1.0]])]});}
            var Q76;
            {var subQ3=sQuery(id+"F0.wireOp",EDGE,"E321");var subQ7=sQuery(id+"F0.wireOp",EDGE,"E1868");var subQ9=makeQuery(id+"F0.imprint","INTERSECT",VERTEX,{"derivedFrom":[subQ3,subQ7]});Q76=makeQuery(id+"F0.imprint","IMPRINT",FACE,{"disambiguationData":[TD([[makeQuery(id+"F0.imprint","IMPRINT",EDGE,{"disambiguationData":[TD([[subQ9,-1.0]])],"derivedFrom":subQ3}),1.0]])]});}
            var Q77;
            {var subQ6=sQuery(id+"F0.wireOp",EDGE,"E24");Q77=makeQuery(id+"F0.imprint","IMPRINT",FACE,{"disambiguationData":[TD([[makeQuery(id+"F0.imprint","IMPRINT",EDGE,{"derivedFrom":subQ6}),-1.0]])]});}
            var Q78;
            {var subQ8=sQuery(id+"F0.wireOp",EDGE,"E166");Q78=makeQuery(id+"F0.imprint","IMPRINT",FACE,{"disambiguationData":[TD([[makeQuery(id+"F0.imprint","IMPRINT",EDGE,{"derivedFrom":subQ8}),1.0]])]});}
            var Q79;
            {var subQ1=sQuery(id+"F0.wireOp",EDGE,"E110");Q79=makeQuery(id+"F0.imprint","IMPRINT",FACE,{"disambiguationData":[TD([[makeQuery(id+"F0.imprint","IMPRINT",EDGE,{"derivedFrom":subQ1}),-1.0]])]});}
            var Q80;
            {var subQ5=sQuery(id+"F0.wireOp",EDGE,"E1942");Q80=makeQuery(id+"F0.imprint","IMPRINT",FACE,{"disambiguationData":[TD([[makeQuery(id+"F0.imprint","IMPRINT",EDGE,{"derivedFrom":subQ5}),-1.0]])]});}
            var Q81;
            {var subQ3=sQuery(id+"F0.wireOp",EDGE,"E321");var subQ5=sQuery(id+"F0.wireOp",EDGE,"E322");var subQ6=makeQuery(id+"F0.imprint","INTERSECT",VERTEX,{"derivedFrom":[subQ3,subQ5]});Q81=makeQuery(id+"F0.imprint","IMPRINT",FACE,{"disambiguationData":[TD([[makeQuery(id+"F0.imprint","IMPRINT",EDGE,{"disambiguationData":[TD([[subQ6,1.0]])],"derivedFrom":subQ3}),1.0]])]});}
            var Q82;
            {var subQ15=sQuery(id+"F0.wireOp",EDGE,"E1743");Q82=makeQuery(id+"F0.imprint","IMPRINT",FACE,{"disambiguationData":[TD([[makeQuery(id+"F0.imprint","IMPRINT",EDGE,{"derivedFrom":subQ15}),1.0]])]});}
            var Q83;
            {var subQ5=sQuery(id+"F0.wireOp",EDGE,"E1870");Q83=makeQuery(id+"F0.imprint","IMPRINT",FACE,{"disambiguationData":[TD([[makeQuery(id+"F0.imprint","IMPRINT",EDGE,{"derivedFrom":subQ5}),-1.0]])]});}
            var Q84;
            {var subQ1=sQuery(id+"F0.wireOp",EDGE,"E384");var subQ5=sQuery(id+"F0.wireOp",EDGE,"E13");var subQ6=makeQuery(id+"F0.imprint","INTERSECT",VERTEX,{"derivedFrom":[subQ5,subQ1]});Q84=makeQuery(id+"F0.imprint","IMPRINT",FACE,{"disambiguationData":[TD([[makeQuery(id+"F0.imprint","IMPRINT",EDGE,{"disambiguationData":[TD([[subQ6,-1.0]])],"derivedFrom":subQ5}),1.0]])]});}
            var Q85;
            {var subQ0=sQuery(id+"F0.wireOp",EDGE,"E381");var subQ1=sQuery(id+"F0.wireOp",EDGE,"E322");var subQ2=makeQuery(id+"F0.imprint","INTERSECT",VERTEX,{"derivedFrom":[subQ1,subQ0]});Q85=makeQuery(id+"F0.imprint","IMPRINT",FACE,{"disambiguationData":[TD([[makeQuery(id+"F0.imprint","IMPRINT",EDGE,{"disambiguationData":[TD([[subQ2,-1.0]])],"derivedFrom":subQ1}),-1.0]])]});}
            var Q86;
            {var subQ4=sQuery(id+"F0.wireOp",EDGE,"E226");Q86=makeQuery(id+"F0.imprint","IMPRINT",FACE,{"disambiguationData":[TD([[makeQuery(id+"F0.imprint","IMPRINT",EDGE,{"derivedFrom":subQ4}),-1.0]])]});}
            var Q87;
            {var subQ0=sQuery(id+"F0.wireOp",EDGE,"E417");Q87=makeQuery(id+"F0.imprint","IMPRINT",FACE,{"disambiguationData":[TD([[makeQuery(id+"F0.imprint","IMPRINT",EDGE,{"derivedFrom":subQ0}),-1.0]])]});}
            var Q88;
            {var subQ1=sQuery(id+"F0.wireOp",EDGE,"E24");Q88=makeQuery(id+"F0.imprint","IMPRINT",FACE,{"disambiguationData":[TD([[makeQuery(id+"F0.imprint","IMPRINT",EDGE,{"derivedFrom":subQ1}),1.0]])]});}
            var Q89;
            {var subQ0=sQuery(id+"F0.wireOp",EDGE,"E426");var subQ1=sQuery(id+"F0.wireOp",EDGE,"E132");var subQ2=makeQuery(id+"F0.imprint","INTERSECT",VERTEX,{"derivedFrom":[subQ1,subQ0]});Q89=makeQuery(id+"F0.imprint","IMPRINT",FACE,{"disambiguationData":[TD([[makeQuery(id+"F0.imprint","IMPRINT",EDGE,{"disambiguationData":[TD([[subQ2,-1.0]])],"derivedFrom":subQ1}),-1.0]])]});}
            var Q90;
            {var subQ11=sQuery(id+"F0.wireOp",EDGE,"E173");Q90=makeQuery(id+"F0.imprint","IMPRINT",FACE,{"disambiguationData":[TD([[makeQuery(id+"F0.imprint","IMPRINT",EDGE,{"derivedFrom":subQ11}),1.0]])]});}
            var Q91;
            {var subQ0=sQuery(id+"F0.wireOp",EDGE,"E1744");var subQ1=sQuery(id+"F0.wireOp",EDGE,"E23");var subQ2=makeQuery(id+"F0.imprint","INTERSECT",VERTEX,{"derivedFrom":[subQ1,subQ0]});Q91=makeQuery(id+"F0.imprint","IMPRINT",FACE,{"disambiguationData":[TD([[makeQuery(id+"F0.imprint","IMPRINT",EDGE,{"disambiguationData":[TD([[subQ2,-1.0]])],"derivedFrom":subQ1}),1.0]])]});}
            var Q92;
            {var subQ3=sQuery(id+"F0.wireOp",EDGE,"E321");var subQ9=sQuery(id+"F0.wireOp",EDGE,"E1756");var subQ11=makeQuery(id+"F0.imprint","INTERSECT",VERTEX,{"derivedFrom":[subQ3,subQ9]});Q92=makeQuery(id+"F0.imprint","IMPRINT",FACE,{"disambiguationData":[TD([[makeQuery(id+"F0.imprint","IMPRINT",EDGE,{"disambiguationData":[TD([[subQ11,-1.0]])],"derivedFrom":subQ3}),1.0]])]});}
            var Q93;
            {var subQ17=sQuery(id+"F0.wireOp",EDGE,"E1875");Q93=makeQuery(id+"F0.imprint","IMPRINT",FACE,{"disambiguationData":[TD([[makeQuery(id+"F0.imprint","IMPRINT",EDGE,{"derivedFrom":subQ17}),-1.0]])]});}
            var Q94;
            {var subQ0=sQuery(id+"F0.wireOp",EDGE,"E1536");Q94=makeQuery(id+"F0.imprint","IMPRINT",FACE,{"disambiguationData":[TD([[makeQuery(id+"F0.imprint","IMPRINT",EDGE,{"derivedFrom":subQ0}),1.0]])]});}
            var Q95;
            {var subQ3=sQuery(id+"F0.wireOp",EDGE,"E194");var subQ7=sQuery(id+"F0.wireOp",EDGE,"E193");var subQ8=makeQuery(id+"F0.imprint","INTERSECT",VERTEX,{"derivedFrom":[subQ7,subQ3]});Q95=makeQuery(id+"F0.imprint","IMPRINT",FACE,{"disambiguationData":[TD([[makeQuery(id+"F0.imprint","IMPRINT",EDGE,{"disambiguationData":[TD([[subQ8,1.0]])],"derivedFrom":subQ7}),-1.0]])]});}
            var Q96;
            {var subQ3=sQuery(id+"F0.wireOp",EDGE,"E109");var subQ5=sQuery(id+"F0.wireOp",EDGE,"E108");var subQ6=makeQuery(id+"F0.imprint","INTERSECT",VERTEX,{"derivedFrom":[subQ5,subQ3]});Q96=makeQuery(id+"F0.imprint","IMPRINT",FACE,{"disambiguationData":[TD([[makeQuery(id+"F0.imprint","IMPRINT",EDGE,{"disambiguationData":[TD([[subQ6,1.0]])],"derivedFrom":subQ5}),-1.0]])]});}
            var Q97;
            {var subQ12=sQuery(id+"F0.wireOp",EDGE,"E1872");Q97=makeQuery(id+"F0.imprint","IMPRINT",FACE,{"disambiguationData":[TD([[makeQuery(id+"F0.imprint","IMPRINT",EDGE,{"derivedFrom":subQ12}),-1.0]])]});}
            var Q98;
            {var subQ0=sQuery(id+"F0.wireOp",EDGE,"E1782");var subQ1=sQuery(id+"F0.wireOp",EDGE,"E385");var subQ2=makeQuery(id+"F0.imprint","INTERSECT",VERTEX,{"derivedFrom":[subQ1,subQ0]});Q98=makeQuery(id+"F0.imprint","IMPRINT",FACE,{"disambiguationData":[TD([[makeQuery(id+"F0.imprint","IMPRINT",EDGE,{"disambiguationData":[TD([[subQ2,-1.0]])],"derivedFrom":subQ1}),-1.0]])]});}
            var Q99;
            Q99=makeQuery(id+"F0.imprint","IMPRINT",FACE,{"disambiguationData":[TD([[makeQuery(id+"F0.imprint","IMPRINT",EDGE,{"derivedFrom":sQuery(id+"F0.wireOp",EDGE,"E1161")}),1.0]])]});
            var Q100;
            {var subQ7=sQuery(id+"F0.wireOp",EDGE,"E23");var subQ8=sQuery(id+"F0.wireOp",EDGE,"E22");var subQ9=makeQuery(id+"F0.imprint","INTERSECT",VERTEX,{"derivedFrom":[subQ8,subQ7]});Q100=makeQuery(id+"F0.imprint","IMPRINT",FACE,{"disambiguationData":[TD([[makeQuery(id+"F0.imprint","IMPRINT",EDGE,{"disambiguationData":[TD([[subQ9,1.0]])],"derivedFrom":subQ8}),1.0]])]});}
            var Q101;
            {var subQ5=sQuery(id+"F0.wireOp",EDGE,"E1525");Q101=makeQuery(id+"F0.imprint","IMPRINT",FACE,{"disambiguationData":[TD([[makeQuery(id+"F0.imprint","IMPRINT",EDGE,{"derivedFrom":subQ5}),1.0]])]});}
            var Q102;
            {var subQ12=sQuery(id+"F0.wireOp",EDGE,"E1522");Q102=makeQuery(id+"F0.imprint","IMPRINT",FACE,{"disambiguationData":[TD([[makeQuery(id+"F0.imprint","IMPRINT",EDGE,{"derivedFrom":subQ12}),1.0]])]});}
            var Q103;
            {var subQ0=sQuery(id+"F0.wireOp",EDGE,"E1875");Q103=makeQuery(id+"F0.imprint","IMPRINT",FACE,{"disambiguationData":[TD([[makeQuery(id+"F0.imprint","IMPRINT",EDGE,{"derivedFrom":subQ0}),1.0]])]});}
            var Q104;
            {var subQ0=sQuery(id+"F0.wireOp",EDGE,"E323");var subQ1=sQuery(id+"F0.wireOp",EDGE,"E322");var subQ2=makeQuery(id+"F0.imprint","INTERSECT",VERTEX,{"derivedFrom":[subQ1,subQ0]});Q104=makeQuery(id+"F0.imprint","IMPRINT",FACE,{"disambiguationData":[TD([[makeQuery(id+"F0.imprint","IMPRINT",EDGE,{"disambiguationData":[TD([[subQ2,1.0]])],"derivedFrom":subQ1}),1.0]])]});}
            var Q105;
            {var subQ7=sQuery(id+"F0.wireOp",EDGE,"E55");Q105=makeQuery(id+"F0.imprint","IMPRINT",FACE,{"disambiguationData":[TD([[makeQuery(id+"F0.imprint","IMPRINT",EDGE,{"derivedFrom":subQ7}),1.0]])]});}
            var Q106;
            {var subQ4=sQuery(id+"F0.wireOp",EDGE,"E293");Q106=makeQuery(id+"F0.imprint","IMPRINT",FACE,{"disambiguationData":[TD([[makeQuery(id+"F0.imprint","IMPRINT",EDGE,{"derivedFrom":subQ4}),1.0]])]});}
            var Q107;
            {var subQ5=sQuery(id+"F0.wireOp",EDGE,"E17");Q107=makeQuery(id+"F0.imprint","IMPRINT",FACE,{"disambiguationData":[TD([[makeQuery(id+"F0.imprint","IMPRINT",EDGE,{"derivedFrom":subQ5}),1.0]])]});}
            var Q108;
            {var subQ11=sQuery(id+"F0.wireOp",EDGE,"E214");Q108=makeQuery(id+"F0.imprint","IMPRINT",FACE,{"disambiguationData":[TD([[makeQuery(id+"F0.imprint","IMPRINT",EDGE,{"derivedFrom":subQ11}),-1.0]])]});}
            var Q109;
            {var subQ16=sQuery(id+"F0.wireOp",EDGE,"E1522");Q109=makeQuery(id+"F0.imprint","IMPRINT",FACE,{"disambiguationData":[TD([[makeQuery(id+"F0.imprint","IMPRINT",EDGE,{"derivedFrom":subQ16}),-1.0]])]});}
            var Q110;
            {var subQ0=sQuery(id+"F0.wireOp",EDGE,"E1868");var subQ1=sQuery(id+"F0.wireOp",EDGE,"E381");var subQ2=makeQuery(id+"F0.imprint","INTERSECT",VERTEX,{"derivedFrom":[subQ1,subQ0]});Q110=makeQuery(id+"F0.imprint","IMPRINT",FACE,{"disambiguationData":[TD([[makeQuery(id+"F0.imprint","IMPRINT",EDGE,{"disambiguationData":[TD([[subQ2,-1.0]])],"derivedFrom":subQ1}),1.0]])]});}
            var Q111;
            {var subQ0=sQuery(id+"F0.wireOp",EDGE,"E1213");var subQ1=sQuery(id+"F0.wireOp",EDGE,"E148");var subQ2=makeQuery(id+"F0.imprint","INTERSECT",VERTEX,{"derivedFrom":[subQ1,subQ0]});Q111=makeQuery(id+"F0.imprint","IMPRINT",FACE,{"disambiguationData":[TD([[makeQuery(id+"F0.imprint","IMPRINT",EDGE,{"disambiguationData":[TD([[subQ2,-1.0]])],"derivedFrom":subQ1}),-1.0]])]});}
            var Q112;
            {var subQ1=sQuery(id+"F0.wireOp",EDGE,"E23");var subQ5=sQuery(id+"F0.wireOp",EDGE,"E326");var subQ6=makeQuery(id+"F0.imprint","INTERSECT",VERTEX,{"derivedFrom":[subQ1,subQ5]});Q112=makeQuery(id+"F0.imprint","IMPRINT",FACE,{"disambiguationData":[TD([[makeQuery(id+"F0.imprint","IMPRINT",EDGE,{"disambiguationData":[TD([[subQ6,1.0]])],"derivedFrom":subQ5}),1.0]])]});}
            var Q113;
            {var subQ1=sQuery(id+"F0.wireOp",EDGE,"E1469");Q113=makeQuery(id+"F0.imprint","IMPRINT",FACE,{"disambiguationData":[TD([[makeQuery(id+"F0.imprint","IMPRINT",EDGE,{"derivedFrom":subQ1}),-1.0]])]});}
            var Q114;
            {var subQ0=sQuery(id+"F0.wireOp",EDGE,"E383");var subQ1=sQuery(id+"F0.wireOp",EDGE,"E382");var subQ2=makeQuery(id+"F0.imprint","INTERSECT",VERTEX,{"derivedFrom":[subQ1,subQ0]});Q114=makeQuery(id+"F0.imprint","IMPRINT",FACE,{"disambiguationData":[TD([[makeQuery(id+"F0.imprint","IMPRINT",EDGE,{"disambiguationData":[TD([[subQ2,1.0]])],"derivedFrom":subQ1}),1.0]])]});}
            var Q115;
            {var subQ5=sQuery(id+"F0.wireOp",EDGE,"E13");var subQ7=sQuery(id+"F0.wireOp",EDGE,"E384");var subQ8=makeQuery(id+"F0.imprint","INTERSECT",VERTEX,{"derivedFrom":[subQ5,subQ7]});Q115=makeQuery(id+"F0.imprint","IMPRINT",FACE,{"disambiguationData":[TD([[makeQuery(id+"F0.imprint","IMPRINT",EDGE,{"disambiguationData":[TD([[subQ8,-1.0]])],"derivedFrom":subQ5}),-1.0]])]});}
            var Q116;
            {var subQ5=sQuery(id+"F0.wireOp",EDGE,"E362");Q116=makeQuery(id+"F0.imprint","IMPRINT",FACE,{"disambiguationData":[TD([[makeQuery(id+"F0.imprint","IMPRINT",EDGE,{"derivedFrom":subQ5}),1.0]])]});}
            var Q117;
            Q117=makeQuery(id+"F0.imprint","IMPRINT",FACE,{"disambiguationData":[TD([[makeQuery(id+"F0.imprint","IMPRINT",EDGE,{"derivedFrom":sQuery(id+"F0.wireOp",EDGE,"E333")}),1.0]])]});
            var Q118;
            {var subQ3=sQuery(id+"F0.wireOp",EDGE,"E325");var subQ5=sQuery(id+"F0.wireOp",EDGE,"E384");var subQ6=makeQuery(id+"F0.imprint","INTERSECT",VERTEX,{"derivedFrom":[subQ3,subQ5]});Q118=makeQuery(id+"F0.imprint","IMPRINT",FACE,{"disambiguationData":[TD([[makeQuery(id+"F0.imprint","IMPRINT",EDGE,{"disambiguationData":[TD([[subQ6,-1.0]])],"derivedFrom":subQ3}),-1.0]])]});}
            var Q119;
            {var subQ0=sQuery(id+"F0.wireOp",EDGE,"E14");var subQ1=sQuery(id+"F0.wireOp",EDGE,"E13");var subQ2=makeQuery(id+"F0.imprint","INTERSECT",VERTEX,{"derivedFrom":[subQ1,subQ0]});Q119=makeQuery(id+"F0.imprint","IMPRINT",FACE,{"disambiguationData":[TD([[makeQuery(id+"F0.imprint","IMPRINT",EDGE,{"disambiguationData":[TD([[subQ2,1.0]])],"derivedFrom":subQ1}),-1.0]])]});}
            var Q120;
            {var subQ0=sQuery(id+"F0.wireOp",EDGE,"E1748");Q120=makeQuery(id+"F0.imprint","IMPRINT",FACE,{"disambiguationData":[TD([[makeQuery(id+"F0.imprint","IMPRINT",EDGE,{"derivedFrom":subQ0}),1.0]])]});}
            var Q121;
            {var subQ5=sQuery(id+"F0.wireOp",EDGE,"E192");Q121=makeQuery(id+"F0.imprint","IMPRINT",FACE,{"disambiguationData":[TD([[makeQuery(id+"F0.imprint","IMPRINT",EDGE,{"derivedFrom":subQ5}),-1.0]])]});}
            var Q122;
            {var subQ11=sQuery(id+"F0.wireOp",EDGE,"E190");Q122=makeQuery(id+"F0.imprint","IMPRINT",FACE,{"disambiguationData":[TD([[makeQuery(id+"F0.imprint","IMPRINT",EDGE,{"derivedFrom":subQ11}),-1.0]])]});}
            var Q123;
            {var subQ4=sQuery(id+"F0.wireOp",EDGE,"E224");Q123=makeQuery(id+"F0.imprint","IMPRINT",FACE,{"disambiguationData":[TD([[makeQuery(id+"F0.imprint","IMPRINT",EDGE,{"derivedFrom":subQ4}),-1.0]])]});}
            var Q124;
            {var subQ1=sQuery(id+"F0.wireOp",EDGE,"E221");var subQ7=sQuery(id+"F0.wireOp",EDGE,"E222");var subQ8=makeQuery(id+"F0.imprint","INTERSECT",VERTEX,{"derivedFrom":[subQ1,subQ7]});Q124=makeQuery(id+"F0.imprint","IMPRINT",FACE,{"disambiguationData":[TD([[makeQuery(id+"F0.imprint","IMPRINT",EDGE,{"disambiguationData":[TD([[subQ8,1.0]])],"derivedFrom":subQ1}),-1.0]])]});}
            var Q125;
            {var subQ3=sQuery(id+"F0.wireOp",EDGE,"E15");var subQ5=sQuery(id+"F0.wireOp",EDGE,"E415");var subQ6=makeQuery(id+"F0.imprint","INTERSECT",VERTEX,{"derivedFrom":[subQ3,subQ5]});Q125=makeQuery(id+"F0.imprint","IMPRINT",FACE,{"disambiguationData":[TD([[makeQuery(id+"F0.imprint","IMPRINT",EDGE,{"disambiguationData":[TD([[subQ6,-1.0]])],"derivedFrom":subQ3}),1.0]])]});}
            var Q126;
            {var subQ6=sQuery(id+"F0.wireOp",EDGE,"E482");Q126=makeQuery(id+"F0.imprint","IMPRINT",FACE,{"disambiguationData":[TD([[makeQuery(id+"F0.imprint","IMPRINT",EDGE,{"derivedFrom":subQ6}),1.0]])]});}
            var Q127;
            {var subQ5=sQuery(id+"F0.wireOp",EDGE,"E15");var subQ7=sQuery(id+"F0.wireOp",EDGE,"E14");var subQ8=makeQuery(id+"F0.imprint","INTERSECT",VERTEX,{"derivedFrom":[subQ7,subQ5]});Q127=makeQuery(id+"F0.imprint","IMPRINT",FACE,{"disambiguationData":[TD([[makeQuery(id+"F0.imprint","IMPRINT",EDGE,{"disambiguationData":[TD([[subQ8,1.0]])],"derivedFrom":subQ7}),1.0]])]});}
            var Q128;
            {var subQ6=sQuery(id+"F0.wireOp",EDGE,"E417");Q128=makeQuery(id+"F0.imprint","IMPRINT",FACE,{"disambiguationData":[TD([[makeQuery(id+"F0.imprint","IMPRINT",EDGE,{"derivedFrom":subQ6}),1.0]])]});}
            var Q129;
            {var subQ0=sQuery(id+"F0.wireOp",EDGE,"E1525");Q129=makeQuery(id+"F0.imprint","IMPRINT",FACE,{"disambiguationData":[TD([[makeQuery(id+"F0.imprint","IMPRINT",EDGE,{"derivedFrom":subQ0}),-1.0]])]});}
            var Q130;
            {var subQ0=sQuery(id+"F0.wireOp",EDGE,"E426");var subQ1=sQuery(id+"F0.wireOp",EDGE,"E193");var subQ2=makeQuery(id+"F0.imprint","INTERSECT",VERTEX,{"derivedFrom":[subQ1,subQ0]});Q130=makeQuery(id+"F0.imprint","IMPRINT",FACE,{"disambiguationData":[TD([[makeQuery(id+"F0.imprint","IMPRINT",EDGE,{"disambiguationData":[TD([[subQ2,-1.0]])],"derivedFrom":subQ1}),-1.0]])]});}
            var Q131;
            {var subQ5=sQuery(id+"F0.wireOp",EDGE,"E15");var subQ6=sQuery(id+"F0.wireOp",EDGE,"E14");var subQ7=makeQuery(id+"F0.imprint","INTERSECT",VERTEX,{"derivedFrom":[subQ6,subQ5]});Q131=makeQuery(id+"F0.imprint","IMPRINT",FACE,{"disambiguationData":[TD([[makeQuery(id+"F0.imprint","IMPRINT",EDGE,{"disambiguationData":[TD([[subQ7,1.0]])],"derivedFrom":subQ6}),-1.0]])]});}
            var Q132;
            Q132=makeQuery(id+"F0.imprint","IMPRINT",FACE,{"disambiguationData":[TD([[makeQuery(id+"F0.imprint","IMPRINT",EDGE,{"derivedFrom":sQuery(id+"F0.wireOp",EDGE,"E391")}),-1.0]])]});
            var Q133;
            {var subQ5=sQuery(id+"F0.wireOp",EDGE,"E507");var subQ9=sQuery(id+"F0.wireOp",EDGE,"E71");var subQ11=makeQuery(id+"F0.imprint","INTERSECT",VERTEX,{"derivedFrom":[subQ9,subQ5]});Q133=makeQuery(id+"F0.imprint","IMPRINT",FACE,{"disambiguationData":[TD([[makeQuery(id+"F0.imprint","IMPRINT",EDGE,{"disambiguationData":[TD([[subQ11,-1.0]])],"derivedFrom":subQ9}),-1.0]])]});}
            var Q134;
            {var subQ0=sQuery(id+"F0.wireOp",EDGE,"E415");var subQ1=sQuery(id+"F0.wireOp",EDGE,"E15");var subQ2=makeQuery(id+"F0.imprint","INTERSECT",VERTEX,{"derivedFrom":[subQ1,subQ0]});Q134=makeQuery(id+"F0.imprint","IMPRINT",FACE,{"disambiguationData":[TD([[makeQuery(id+"F0.imprint","IMPRINT",EDGE,{"disambiguationData":[TD([[subQ2,-1.0]])],"derivedFrom":subQ1}),-1.0]])]});}
            var Q135;
            {var subQ0=sQuery(id+"F0.wireOp",EDGE,"E1941");var subQ1=sQuery(id+"F0.wireOp",EDGE,"E384");var subQ2=makeQuery(id+"F0.imprint","INTERSECT",VERTEX,{"derivedFrom":[subQ1,subQ0]});Q135=makeQuery(id+"F0.imprint","IMPRINT",FACE,{"disambiguationData":[TD([[makeQuery(id+"F0.imprint","IMPRINT",EDGE,{"disambiguationData":[TD([[subQ2,-1.0]])],"derivedFrom":subQ1}),1.0]])]});}
            var Q136;
            {var subQ5=sQuery(id+"F0.wireOp",EDGE,"E1941");var subQ6=sQuery(id+"F0.wireOp",EDGE,"E325");var subQ7=makeQuery(id+"F0.imprint","INTERSECT",VERTEX,{"derivedFrom":[subQ6,subQ5]});Q136=makeQuery(id+"F0.imprint","IMPRINT",FACE,{"disambiguationData":[TD([[makeQuery(id+"F0.imprint","IMPRINT",EDGE,{"disambiguationData":[TD([[subQ7,-1.0]])],"derivedFrom":subQ6}),1.0]])]});}
            var Q137;
            {var subQ0=sQuery(id+"F0.wireOp",EDGE,"E173");Q137=makeQuery(id+"F0.imprint","IMPRINT",FACE,{"disambiguationData":[TD([[makeQuery(id+"F0.imprint","IMPRINT",EDGE,{"derivedFrom":subQ0}),-1.0]])]});}
            var Q138;
            {var subQ1=sQuery(id+"F0.wireOp",EDGE,"E1528");var subQ8=sQuery(id+"F0.wireOp",EDGE,"E384");var subQ10=makeQuery(id+"F0.imprint","INTERSECT",VERTEX,{"derivedFrom":[subQ8,subQ1]});Q138=makeQuery(id+"F0.imprint","IMPRINT",FACE,{"disambiguationData":[TD([[makeQuery(id+"F0.imprint","IMPRINT",EDGE,{"disambiguationData":[TD([[subQ10,-1.0]])],"derivedFrom":subQ8}),-1.0]])]});}
            var Q139;
            {var subQ3=sQuery(id+"F0.wireOp",EDGE,"E384");var subQ7=sQuery(id+"F0.wireOp",EDGE,"E1941");var subQ9=makeQuery(id+"F0.imprint","INTERSECT",VERTEX,{"derivedFrom":[subQ3,subQ7]});Q139=makeQuery(id+"F0.imprint","IMPRINT",FACE,{"disambiguationData":[TD([[makeQuery(id+"F0.imprint","IMPRINT",EDGE,{"disambiguationData":[TD([[subQ9,-1.0]])],"derivedFrom":subQ3}),-1.0]])]});}
            var Q140;
            {var subQ0=sQuery(id+"F0.wireOp",EDGE,"E293");Q140=makeQuery(id+"F0.imprint","IMPRINT",FACE,{"disambiguationData":[TD([[makeQuery(id+"F0.imprint","IMPRINT",EDGE,{"derivedFrom":subQ0}),-1.0]])]});}
            var Q141;
            {var subQ0=sQuery(id+"F0.wireOp",EDGE,"E384");var subQ1=sQuery(id+"F0.wireOp",EDGE,"E383");var subQ2=makeQuery(id+"F0.imprint","INTERSECT",VERTEX,{"derivedFrom":[subQ1,subQ0]});Q141=makeQuery(id+"F0.imprint","IMPRINT",FACE,{"disambiguationData":[TD([[makeQuery(id+"F0.imprint","IMPRINT",EDGE,{"disambiguationData":[TD([[subQ2,1.0]])],"derivedFrom":subQ1}),1.0]])]});}
            var Q142;
            Q142=makeQuery(id+"F0.imprint","IMPRINT",FACE,{"disambiguationData":[TD([[makeQuery(id+"F0.imprint","IMPRINT",EDGE,{"derivedFrom":sQuery(id+"F0.wireOp",EDGE,"E452")}),-1.0]])]});
            var Q143;
            {var subQ5=sQuery(id+"F0.wireOp",EDGE,"E16");var subQ6=sQuery(id+"F0.wireOp",EDGE,"E15");var subQ7=makeQuery(id+"F0.imprint","INTERSECT",VERTEX,{"derivedFrom":[subQ6,subQ5]});Q143=makeQuery(id+"F0.imprint","IMPRINT",FACE,{"disambiguationData":[TD([[makeQuery(id+"F0.imprint","IMPRINT",EDGE,{"disambiguationData":[TD([[subQ7,1.0]])],"derivedFrom":subQ6}),-1.0]])]});}
            var Q144;
            {var subQ0=sQuery(id+"F0.wireOp",EDGE,"E384");var subQ1=sQuery(id+"F0.wireOp",EDGE,"E325");var subQ2=makeQuery(id+"F0.imprint","INTERSECT",VERTEX,{"derivedFrom":[subQ1,subQ0]});Q144=makeQuery(id+"F0.imprint","IMPRINT",FACE,{"disambiguationData":[TD([[makeQuery(id+"F0.imprint","IMPRINT",EDGE,{"disambiguationData":[TD([[subQ2,-1.0]])],"derivedFrom":subQ1}),1.0]])]});}
            var Q145;
            Q145=makeQuery(id+"F0.imprint","IMPRINT",FACE,{"disambiguationData":[TD([[makeQuery(id+"F0.imprint","IMPRINT",EDGE,{"derivedFrom":sQuery(id+"F0.wireOp",EDGE,"E1161")}),-1.0]])]});
            var Q146;
            {var subQ3=sQuery(id+"F0.wireOp",EDGE,"E71");var subQ8=sQuery(id+"F0.wireOp",EDGE,"E507");var subQ9=makeQuery(id+"F0.imprint","INTERSECT",VERTEX,{"derivedFrom":[subQ3,subQ8]});Q146=makeQuery(id+"F0.imprint","IMPRINT",FACE,{"disambiguationData":[TD([[makeQuery(id+"F0.imprint","IMPRINT",EDGE,{"disambiguationData":[TD([[subQ9,-1.0]])],"derivedFrom":subQ3}),1.0]])]});}
            var Q147;
            {var subQ0=sQuery(id+"F0.wireOp",EDGE,"E1214");var subQ1=sQuery(id+"F0.wireOp",EDGE,"E148");var subQ2=makeQuery(id+"F0.imprint","INTERSECT",VERTEX,{"derivedFrom":[subQ1,subQ0]});Q147=makeQuery(id+"F0.imprint","IMPRINT",FACE,{"disambiguationData":[TD([[makeQuery(id+"F0.imprint","IMPRINT",EDGE,{"disambiguationData":[TD([[subQ2,-1.0]])],"derivedFrom":subQ1}),1.0]])]});}
            var Q148;
            {var subQ0=sQuery(id+"F0.wireOp",EDGE,"E427");var subQ1=sQuery(id+"F0.wireOp",EDGE,"E325");var subQ2=makeQuery(id+"F0.imprint","INTERSECT",VERTEX,{"derivedFrom":[subQ1,subQ0]});Q148=makeQuery(id+"F0.imprint","IMPRINT",FACE,{"disambiguationData":[TD([[makeQuery(id+"F0.imprint","IMPRINT",EDGE,{"disambiguationData":[TD([[subQ2,-1.0]])],"derivedFrom":subQ1}),1.0]])]});}
            var Q149;
            {var subQ3=sQuery(id+"F0.wireOp",EDGE,"E15");var subQ6=sQuery(id+"F0.wireOp",EDGE,"E16");var subQ9=makeQuery(id+"F0.imprint","INTERSECT",VERTEX,{"derivedFrom":[subQ3,subQ6]});Q149=makeQuery(id+"F0.imprint","IMPRINT",FACE,{"disambiguationData":[TD([[makeQuery(id+"F0.imprint","IMPRINT",EDGE,{"disambiguationData":[TD([[subQ9,1.0]])],"derivedFrom":subQ3}),1.0]])]});}
            var Q150;
            Q150=makeQuery(id+"F0.imprint","IMPRINT",FACE,{"disambiguationData":[TD([[makeQuery(id+"F0.imprint","IMPRINT",EDGE,{"derivedFrom":sQuery(id+"F0.wireOp",EDGE,"E428")}),-1.0]])]});
            var Q151;
            {var subQ0=sQuery(id+"F0.wireOp",EDGE,"E1942");Q151=makeQuery(id+"F0.imprint","IMPRINT",FACE,{"disambiguationData":[TD([[makeQuery(id+"F0.imprint","IMPRINT",EDGE,{"derivedFrom":subQ0}),1.0]])]});}
            var Q152;
            {var subQ4=sQuery(id+"F0.wireOp",EDGE,"E836");Q152=makeQuery(id+"F0.imprint","IMPRINT",FACE,{"disambiguationData":[TD([[makeQuery(id+"F0.imprint","IMPRINT",EDGE,{"derivedFrom":subQ4}),1.0]])]});}
            var Q153;
            {var subQ2=sQuery(id+"F0.wireOp",EDGE,"E847");Q153=makeQuery(id+"F0.imprint","IMPRINT",FACE,{"disambiguationData":[TD([[makeQuery(id+"F0.imprint","IMPRINT",EDGE,{"derivedFrom":subQ2}),-1.0]])]});}
            var Q154;
            {var subQ0=sQuery(id+"F0.wireOp",EDGE,"E1814");var subQ5=sQuery(id+"F0.wireOp",EDGE,"E319");var subQ6=makeQuery(id+"F0.imprint","INTERSECT",VERTEX,{"derivedFrom":[subQ5,subQ0]});Q154=makeQuery(id+"F0.imprint","IMPRINT",FACE,{"disambiguationData":[TD([[makeQuery(id+"F0.imprint","IMPRINT",EDGE,{"disambiguationData":[TD([[subQ6,-1.0]])],"derivedFrom":subQ5}),1.0]])]});}
            var Q155;
            Q155=makeQuery(id+"F0.imprint","IMPRINT",FACE,{"disambiguationData":[TD([[makeQuery(id+"F0.imprint","IMPRINT",EDGE,{"derivedFrom":sQuery(id+"F0.wireOp",EDGE,"E1370")}),-1.0]])]});
            var Q156;
            Q156=makeQuery(id+"F0.imprint","IMPRINT",FACE,{"disambiguationData":[TD([[makeQuery(id+"F0.imprint","IMPRINT",EDGE,{"derivedFrom":sQuery(id+"F0.wireOp",EDGE,"E1370")}),1.0]])]});
            var Q157;
            {var subQ13=sQuery(id+"F0.wireOp",EDGE,"E378");Q157=makeQuery(id+"F0.imprint","IMPRINT",FACE,{"disambiguationData":[TD([[makeQuery(id+"F0.imprint","IMPRINT",EDGE,{"derivedFrom":subQ13}),-1.0]])]});}
            var Q158;
            {var subQ18=sQuery(id+"F0.wireOp",EDGE,"E1104");Q158=makeQuery(id+"F0.imprint","IMPRINT",FACE,{"disambiguationData":[TD([[makeQuery(id+"F0.imprint","IMPRINT",EDGE,{"derivedFrom":subQ18}),1.0]])]});}
            var Q159;
            {var subQ8=sQuery(id+"F0.wireOp",EDGE,"E1387");Q159=makeQuery(id+"F0.imprint","IMPRINT",FACE,{"disambiguationData":[TD([[makeQuery(id+"F0.imprint","IMPRINT",EDGE,{"derivedFrom":subQ8}),1.0]])]});}
            var Q160;
            {var subQ5=sQuery(id+"F0.wireOp",EDGE,"E1404");var subQ6=sQuery(id+"F0.wireOp",EDGE,"E1403");var subQ7=makeQuery(id+"F0.imprint","INTERSECT",VERTEX,{"derivedFrom":[subQ6,subQ5]});Q160=makeQuery(id+"F0.imprint","IMPRINT",FACE,{"disambiguationData":[TD([[makeQuery(id+"F0.imprint","IMPRINT",EDGE,{"disambiguationData":[TD([[subQ7,1.0]])],"derivedFrom":subQ6}),1.0]])]});}
            var Q161;
            {var subQ0=sQuery(id+"F0.wireOp",EDGE,"E1404");var subQ1=sQuery(id+"F0.wireOp",EDGE,"E1403");var subQ2=makeQuery(id+"F0.imprint","INTERSECT",VERTEX,{"derivedFrom":[subQ1,subQ0]});Q161=makeQuery(id+"F0.imprint","IMPRINT",FACE,{"disambiguationData":[TD([[makeQuery(id+"F0.imprint","IMPRINT",EDGE,{"disambiguationData":[TD([[subQ2,1.0]])],"derivedFrom":subQ1}),-1.0]])]});}
            var Q162;
            {var subQ3=sQuery(id+"F0.wireOp",EDGE,"E1368");var subQ8=sQuery(id+"F0.wireOp",EDGE,"E1367");var subQ9=makeQuery(id+"F0.imprint","INTERSECT",VERTEX,{"derivedFrom":[subQ8,subQ3]});Q162=makeQuery(id+"F0.imprint","IMPRINT",FACE,{"disambiguationData":[TD([[makeQuery(id+"F0.imprint","IMPRINT",EDGE,{"disambiguationData":[TD([[subQ9,1.0]])],"derivedFrom":subQ8}),-1.0]])]});}
            var Q163;
            {var subQ0=sQuery(id+"F0.wireOp",EDGE,"E1414");Q163=makeQuery(id+"F0.imprint","IMPRINT",FACE,{"disambiguationData":[TD([[makeQuery(id+"F0.imprint","IMPRINT",EDGE,{"derivedFrom":subQ0}),1.0]])]});}
            var Q164;
            Q164=makeQuery(id+"F0.imprint","IMPRINT",FACE,{"disambiguationData":[TD([[makeQuery(id+"F0.imprint","IMPRINT",EDGE,{"derivedFrom":sQuery(id+"F0.wireOp",EDGE,"E1346")}),1.0]])]});
            var Q165;
            {var subQ0=sQuery(id+"F0.wireOp",EDGE,"E148");var subQ1=sQuery(id+"F0.wireOp",EDGE,"E147");var subQ2=makeQuery(id+"F0.imprint","INTERSECT",VERTEX,{"derivedFrom":[subQ1,subQ0]});Q165=makeQuery(id+"F0.imprint","IMPRINT",FACE,{"disambiguationData":[TD([[makeQuery(id+"F0.imprint","IMPRINT",EDGE,{"disambiguationData":[TD([[subQ2,1.0]])],"derivedFrom":subQ1}),-1.0]])]});}
            var Q166;
            Q166=makeQuery(id+"F0.imprint","IMPRINT",FACE,{"disambiguationData":[TD([[makeQuery(id+"F0.imprint","IMPRINT",EDGE,{"derivedFrom":sQuery(id+"F0.wireOp",EDGE,"E1346")}),-1.0]])]});
            var Q167;
            {var subQ0=sQuery(id+"F0.wireOp",EDGE,"E1215");var subQ1=sQuery(id+"F0.wireOp",EDGE,"E147");var subQ2=makeQuery(id+"F0.imprint","INTERSECT",VERTEX,{"derivedFrom":[subQ1,subQ0]});Q167=makeQuery(id+"F0.imprint","IMPRINT",FACE,{"disambiguationData":[TD([[makeQuery(id+"F0.imprint","IMPRINT",EDGE,{"disambiguationData":[TD([[subQ2,-1.0]])],"derivedFrom":subQ1}),-1.0]])]});}
            var Q168;
            {var subQ0=sQuery(id+"F0.wireOp",EDGE,"E1215");var subQ1=sQuery(id+"F0.wireOp",EDGE,"E147");var subQ2=makeQuery(id+"F0.imprint","INTERSECT",VERTEX,{"derivedFrom":[subQ1,subQ0]});Q168=makeQuery(id+"F0.imprint","IMPRINT",FACE,{"disambiguationData":[TD([[makeQuery(id+"F0.imprint","IMPRINT",EDGE,{"disambiguationData":[TD([[subQ2,-1.0]])],"derivedFrom":subQ1}),1.0]])]});}
            var Q169;
            {var subQ0=sQuery(id+"F0.wireOp",EDGE,"E1410");Q169=makeQuery(id+"F0.imprint","IMPRINT",FACE,{"disambiguationData":[TD([[makeQuery(id+"F0.imprint","IMPRINT",EDGE,{"derivedFrom":subQ0}),-1.0]])]});}
            var Q170;
            {var subQ0=sQuery(id+"F0.wireOp",EDGE,"E1245");Q170=makeQuery(id+"F0.imprint","IMPRINT",FACE,{"disambiguationData":[TD([[makeQuery(id+"F0.imprint","IMPRINT",EDGE,{"derivedFrom":subQ0}),1.0]])]});}
            var Q171;
            Q171=makeQuery(id+"F0.imprint","IMPRINT",FACE,{"disambiguationData":[TD([[makeQuery(id+"F0.imprint","IMPRINT",EDGE,{"derivedFrom":sQuery(id+"F0.wireOp",EDGE,"E1229")}),1.0]])]});
            var Q172;
            Q172=makeQuery(id+"F0.imprint","IMPRINT",FACE,{"disambiguationData":[TD([[makeQuery(id+"F0.imprint","IMPRINT",EDGE,{"derivedFrom":sQuery(id+"F0.wireOp",EDGE,"E1229")}),-1.0]])]});
            var Q173;
            {var subQ0=sQuery(id+"F0.wireOp",EDGE,"E1245");Q173=makeQuery(id+"F0.imprint","IMPRINT",FACE,{"disambiguationData":[TD([[makeQuery(id+"F0.imprint","IMPRINT",EDGE,{"derivedFrom":subQ0}),-1.0]])]});}
            var Q174;
            {var subQ0=sQuery(id+"F0.wireOp",EDGE,"E1386");var subQ1=sQuery(id+"F0.wireOp",EDGE,"E1368");var subQ2=makeQuery(id+"F0.imprint","INTERSECT",VERTEX,{"derivedFrom":[subQ1,subQ0]});Q174=makeQuery(id+"F0.imprint","IMPRINT",FACE,{"disambiguationData":[TD([[makeQuery(id+"F0.imprint","IMPRINT",EDGE,{"disambiguationData":[TD([[subQ2,-1.0]])],"derivedFrom":subQ1}),-1.0]])]});}
            var Q175;
            {var subQ6=sQuery(id+"F0.wireOp",EDGE,"E482");Q175=makeQuery(id+"F0.imprint","IMPRINT",FACE,{"disambiguationData":[TD([[makeQuery(id+"F0.imprint","IMPRINT",EDGE,{"derivedFrom":subQ6}),-1.0]])]});}
            var Q176;
            {var subQ0=sQuery(id+"F0.wireOp",EDGE,"E1276");var subQ1=sQuery(id+"F0.wireOp",EDGE,"E1275");var subQ2=makeQuery(id+"F0.imprint","INTERSECT",VERTEX,{"derivedFrom":[subQ1,subQ0]});Q176=makeQuery(id+"F0.imprint","IMPRINT",FACE,{"disambiguationData":[TD([[makeQuery(id+"F0.imprint","IMPRINT",EDGE,{"disambiguationData":[TD([[subQ2,1.0]])],"derivedFrom":subQ1}),-1.0]])]});}
            var Q177;
            Q177=makeQuery(id+"F0.imprint","IMPRINT",FACE,{"disambiguationData":[TD([[makeQuery(id+"F0.imprint","IMPRINT",EDGE,{"derivedFrom":sQuery(id+"F0.wireOp",EDGE,"E452")}),1.0]])]});
            var Q178;
            {var subQ8=sQuery(id+"F0.wireOp",EDGE,"E1335");var subQ9=sQuery(id+"F0.wireOp",EDGE,"E1334");var subQ10=makeQuery(id+"F0.imprint","INTERSECT",VERTEX,{"derivedFrom":[subQ9,subQ8]});Q178=makeQuery(id+"F0.imprint","IMPRINT",FACE,{"disambiguationData":[TD([[makeQuery(id+"F0.imprint","IMPRINT",EDGE,{"disambiguationData":[TD([[subQ10,1.0]])],"derivedFrom":subQ9}),-1.0]])]});}
            var Q179;
            {var subQ0=sQuery(id+"F0.wireOp",EDGE,"E486");var subQ1=sQuery(id+"F0.wireOp",EDGE,"E71");var subQ2=makeQuery(id+"F0.imprint","INTERSECT",VERTEX,{"derivedFrom":[subQ1,subQ0]});Q179=makeQuery(id+"F0.imprint","IMPRINT",FACE,{"disambiguationData":[TD([[makeQuery(id+"F0.imprint","IMPRINT",EDGE,{"disambiguationData":[TD([[subQ2,-1.0]])],"derivedFrom":subQ1}),1.0]])]});}
            var Q180;
            {var subQ8=sQuery(id+"F0.wireOp",EDGE,"E143");var subQ11=sQuery(id+"F0.wireOp",EDGE,"E144");var subQ12=makeQuery(id+"F0.imprint","INTERSECT",VERTEX,{"derivedFrom":[subQ8,subQ11]});Q180=makeQuery(id+"F0.imprint","IMPRINT",FACE,{"disambiguationData":[TD([[makeQuery(id+"F0.imprint","IMPRINT",EDGE,{"disambiguationData":[TD([[subQ12,1.0]])],"derivedFrom":subQ8}),1.0]])]});}
            var Q181;
            {var subQ5=sQuery(id+"F0.wireOp",EDGE,"E509");Q181=makeQuery(id+"F0.imprint","IMPRINT",FACE,{"disambiguationData":[TD([[makeQuery(id+"F0.imprint","IMPRINT",EDGE,{"derivedFrom":subQ5}),1.0]])]});}
            var Q182;
            {var subQ0=sQuery(id+"F0.wireOp",EDGE,"E1291");var subQ1=sQuery(id+"F0.wireOp",EDGE,"E1290");var subQ2=makeQuery(id+"F0.imprint","INTERSECT",VERTEX,{"derivedFrom":[subQ1,subQ0]});Q182=makeQuery(id+"F0.imprint","IMPRINT",FACE,{"disambiguationData":[TD([[makeQuery(id+"F0.imprint","IMPRINT",EDGE,{"disambiguationData":[TD([[subQ2,1.0]])],"derivedFrom":subQ1}),-1.0]])]});}
            var Q183;
            {var subQ0=sQuery(id+"F0.wireOp",EDGE,"E144");var subQ1=sQuery(id+"F0.wireOp",EDGE,"E143");var subQ2=makeQuery(id+"F0.imprint","INTERSECT",VERTEX,{"derivedFrom":[subQ1,subQ0]});Q183=makeQuery(id+"F0.imprint","IMPRINT",FACE,{"disambiguationData":[TD([[makeQuery(id+"F0.imprint","IMPRINT",EDGE,{"disambiguationData":[TD([[subQ2,1.0]])],"derivedFrom":subQ1}),-1.0]])]});}
            var Q184;
            {var subQ1=sQuery(id+"F0.wireOp",EDGE,"E1306");Q184=makeQuery(id+"F0.imprint","IMPRINT",FACE,{"disambiguationData":[TD([[makeQuery(id+"F0.imprint","IMPRINT",EDGE,{"derivedFrom":subQ1}),-1.0]])]});}
            var Q185;
            Q185=makeQuery(id+"F0.imprint","IMPRINT",FACE,{"disambiguationData":[TD([[makeQuery(id+"F0.imprint","IMPRINT",EDGE,{"derivedFrom":sQuery(id+"F0.wireOp",EDGE,"E1298")}),-1.0]])]});
            var Q186;
            {var subQ1=sQuery(id+"F0.wireOp",EDGE,"E1262");Q186=makeQuery(id+"F0.imprint","IMPRINT",FACE,{"disambiguationData":[TD([[makeQuery(id+"F0.imprint","IMPRINT",EDGE,{"derivedFrom":subQ1}),1.0]])]});}
            var Q187;
            {var subQ5=sQuery(id+"F0.wireOp",EDGE,"E1306");Q187=makeQuery(id+"F0.imprint","IMPRINT",FACE,{"disambiguationData":[TD([[makeQuery(id+"F0.imprint","IMPRINT",EDGE,{"derivedFrom":subQ5}),1.0]])]});}
            var Q188;
            {var subQ8=sQuery(id+"F0.wireOp",EDGE,"E142");var subQ11=sQuery(id+"F0.wireOp",EDGE,"E143");var subQ12=makeQuery(id+"F0.imprint","INTERSECT",VERTEX,{"derivedFrom":[subQ8,subQ11]});Q188=makeQuery(id+"F0.imprint","IMPRINT",FACE,{"disambiguationData":[TD([[makeQuery(id+"F0.imprint","IMPRINT",EDGE,{"disambiguationData":[TD([[subQ12,1.0]])],"derivedFrom":subQ8}),-1.0]])]});}
            var Q189;
            {var subQ14=sQuery(id+"F0.wireOp",EDGE,"E97");Q189=makeQuery(id+"F0.imprint","IMPRINT",FACE,{"disambiguationData":[TD([[makeQuery(id+"F0.imprint","IMPRINT",EDGE,{"derivedFrom":subQ14}),1.0]])]});}
            var Q190;
            {var subQ5=sQuery(id+"F0.wireOp",EDGE,"E968");Q190=makeQuery(id+"F0.imprint","IMPRINT",FACE,{"disambiguationData":[TD([[makeQuery(id+"F0.imprint","IMPRINT",EDGE,{"derivedFrom":subQ5}),1.0]])]});}
            var Q191;
            {var subQ5=sQuery(id+"F0.wireOp",EDGE,"E1308");Q191=makeQuery(id+"F0.imprint","IMPRINT",FACE,{"disambiguationData":[TD([[makeQuery(id+"F0.imprint","IMPRINT",EDGE,{"derivedFrom":subQ5}),1.0]])]});}
            var Q192;
            {var subQ1=sQuery(id+"F0.wireOp",EDGE,"E783");Q192=makeQuery(id+"F0.imprint","IMPRINT",FACE,{"disambiguationData":[TD([[makeQuery(id+"F0.imprint","IMPRINT",EDGE,{"derivedFrom":subQ1}),1.0]])]});}
            var Q193;
            {var subQ31=sQuery(id+"F0.wireOp",EDGE,"E985");Q193=makeQuery(id+"F0.imprint","IMPRINT",FACE,{"disambiguationData":[TD([[makeQuery(id+"F0.imprint","IMPRINT",EDGE,{"derivedFrom":subQ31}),1.0]])]});}
            var Q194;
            Q194=makeQuery(id+"F0.imprint","IMPRINT",FACE,{"disambiguationData":[TD([[makeQuery(id+"F0.imprint","IMPRINT",EDGE,{"derivedFrom":sQuery(id+"F0.wireOp",EDGE,"E1298")}),1.0]])]});
            var Q195;
            {var subQ1=sQuery(id+"F0.wireOp",EDGE,"E858");var subQ5=sQuery(id+"F0.wireOp",EDGE,"E144");var subQ6=makeQuery(id+"F0.imprint","INTERSECT",VERTEX,{"derivedFrom":[subQ5,subQ1]});Q195=makeQuery(id+"F0.imprint","IMPRINT",FACE,{"disambiguationData":[TD([[makeQuery(id+"F0.imprint","IMPRINT",EDGE,{"disambiguationData":[TD([[subQ6,-1.0]])],"derivedFrom":subQ5}),1.0]])]});}
            var Q196;
            {var subQ0=sQuery(id+"F0.wireOp",EDGE,"E1291");var subQ1=sQuery(id+"F0.wireOp",EDGE,"E145");var subQ2=makeQuery(id+"F0.imprint","INTERSECT",VERTEX,{"derivedFrom":[subQ1,subQ0]});Q196=makeQuery(id+"F0.imprint","IMPRINT",FACE,{"disambiguationData":[TD([[makeQuery(id+"F0.imprint","IMPRINT",EDGE,{"disambiguationData":[TD([[subQ2,-1.0]])],"derivedFrom":subQ1}),1.0]])]});}
            var Q197;
            {var subQ0=sQuery(id+"F0.wireOp",EDGE,"E1336");var subQ1=sQuery(id+"F0.wireOp",EDGE,"E1335");var subQ2=makeQuery(id+"F0.imprint","INTERSECT",VERTEX,{"derivedFrom":[subQ1,subQ0]});Q197=makeQuery(id+"F0.imprint","IMPRINT",FACE,{"disambiguationData":[TD([[makeQuery(id+"F0.imprint","IMPRINT",EDGE,{"disambiguationData":[TD([[subQ2,1.0]])],"derivedFrom":subQ1}),-1.0]])]});}
            var Q198;
            {var subQ8=sQuery(id+"F0.wireOp",EDGE,"E978");Q198=makeQuery(id+"F0.imprint","IMPRINT",FACE,{"disambiguationData":[TD([[makeQuery(id+"F0.imprint","IMPRINT",EDGE,{"derivedFrom":subQ8}),1.0]])]});}
            var Q199;
            {var subQ0=sQuery(id+"F0.wireOp",EDGE,"E1338");Q199=makeQuery(id+"F0.imprint","IMPRINT",FACE,{"disambiguationData":[TD([[makeQuery(id+"F0.imprint","IMPRINT",EDGE,{"derivedFrom":subQ0}),1.0]])]});}
            var Q200;
            {var subQ0=sQuery(id+"F0.wireOp",EDGE,"E865");var subQ1=sQuery(id+"F0.wireOp",EDGE,"E855");var subQ2=makeQuery(id+"F0.imprint","INTERSECT",VERTEX,{"derivedFrom":[subQ1,subQ0]});Q200=makeQuery(id+"F0.imprint","IMPRINT",FACE,{"disambiguationData":[TD([[makeQuery(id+"F0.imprint","IMPRINT",EDGE,{"disambiguationData":[TD([[subQ2,-1.0]])],"derivedFrom":subQ1}),-1.0]])]});}
            var Q201;
            {var subQ0=sQuery(id+"F0.wireOp",EDGE,"E1773");Q201=makeQuery(id+"F0.imprint","IMPRINT",FACE,{"disambiguationData":[TD([[makeQuery(id+"F0.imprint","IMPRINT",EDGE,{"derivedFrom":subQ0}),-1.0]])]});}
            var Q202;
            {var subQ0=sQuery(id+"F0.wireOp",EDGE,"E145");var subQ1=sQuery(id+"F0.wireOp",EDGE,"E144");var subQ2=makeQuery(id+"F0.imprint","INTERSECT",VERTEX,{"derivedFrom":[subQ1,subQ0]});Q202=makeQuery(id+"F0.imprint","IMPRINT",FACE,{"disambiguationData":[TD([[makeQuery(id+"F0.imprint","IMPRINT",EDGE,{"disambiguationData":[TD([[subQ2,1.0]])],"derivedFrom":subQ1}),1.0]])]});}
            var Q203;
            {var subQ5=sQuery(id+"F0.wireOp",EDGE,"E1262");Q203=makeQuery(id+"F0.imprint","IMPRINT",FACE,{"disambiguationData":[TD([[makeQuery(id+"F0.imprint","IMPRINT",EDGE,{"derivedFrom":subQ5}),-1.0]])]});}
            var Q204;
            {var subQ0=sQuery(id+"F0.wireOp",EDGE,"E856");var subQ1=sQuery(id+"F0.wireOp",EDGE,"E855");var subQ2=makeQuery(id+"F0.imprint","INTERSECT",VERTEX,{"derivedFrom":[subQ1,subQ0]});Q204=makeQuery(id+"F0.imprint","IMPRINT",FACE,{"disambiguationData":[TD([[makeQuery(id+"F0.imprint","IMPRINT",EDGE,{"disambiguationData":[TD([[subQ2,1.0]])],"derivedFrom":subQ1}),-1.0]])]});}
            var Q205;
            {var subQ0=sQuery(id+"F0.wireOp",EDGE,"E379");var subQ1=sQuery(id+"F0.wireOp",EDGE,"E139");var subQ2=makeQuery(id+"F0.imprint","INTERSECT",VERTEX,{"derivedFrom":[subQ1,subQ0]});Q205=makeQuery(id+"F0.imprint","IMPRINT",FACE,{"disambiguationData":[TD([[makeQuery(id+"F0.imprint","IMPRINT",EDGE,{"disambiguationData":[TD([[subQ2,-1.0]])],"derivedFrom":subQ1}),-1.0]])]});}
            var Q206;
            {var subQ5=sQuery(id+"F0.wireOp",EDGE,"E836");Q206=makeQuery(id+"F0.imprint","IMPRINT",FACE,{"disambiguationData":[TD([[makeQuery(id+"F0.imprint","IMPRINT",EDGE,{"derivedFrom":subQ5}),-1.0]])]});}
            var Q207;
            {var subQ0=sQuery(id+"F0.wireOp",EDGE,"E835");var subQ9=sQuery(id+"F0.wireOp",EDGE,"E37");var subQ10=makeQuery(id+"F0.imprint","INTERSECT",VERTEX,{"derivedFrom":[subQ9,subQ0]});Q207=makeQuery(id+"F0.imprint","IMPRINT",FACE,{"disambiguationData":[TD([[makeQuery(id+"F0.imprint","IMPRINT",EDGE,{"disambiguationData":[TD([[subQ10,-1.0]])],"derivedFrom":subQ9}),-1.0]])]});}
            var Q208;
            {var subQ0=sQuery(id+"F0.wireOp",EDGE,"E861");var subQ1=sQuery(id+"F0.wireOp",EDGE,"E856");var subQ2=makeQuery(id+"F0.imprint","INTERSECT",VERTEX,{"derivedFrom":[subQ1,subQ0]});Q208=makeQuery(id+"F0.imprint","IMPRINT",FACE,{"disambiguationData":[TD([[makeQuery(id+"F0.imprint","IMPRINT",EDGE,{"disambiguationData":[TD([[subQ2,-1.0]])],"derivedFrom":subQ1}),1.0]])]});}
            var Q209;
            {var subQ0=sQuery(id+"F0.wireOp",EDGE,"E857");var subQ1=sQuery(id+"F0.wireOp",EDGE,"E856");var subQ2=makeQuery(id+"F0.imprint","INTERSECT",VERTEX,{"derivedFrom":[subQ1,subQ0]});Q209=makeQuery(id+"F0.imprint","IMPRINT",FACE,{"disambiguationData":[TD([[makeQuery(id+"F0.imprint","IMPRINT",EDGE,{"disambiguationData":[TD([[subQ2,1.0]])],"derivedFrom":subQ1}),1.0]])]});}
            var Q210;
            {var subQ22=sQuery(id+"F0.wireOp",EDGE,"E458");Q210=makeQuery(id+"F0.imprint","IMPRINT",FACE,{"disambiguationData":[TD([[makeQuery(id+"F0.imprint","IMPRINT",EDGE,{"derivedFrom":subQ22}),1.0]])]});}
            var Q211;
            {var subQ13=sQuery(id+"F0.wireOp",EDGE,"E1049");Q211=makeQuery(id+"F0.imprint","IMPRINT",FACE,{"disambiguationData":[TD([[makeQuery(id+"F0.imprint","IMPRINT",EDGE,{"derivedFrom":subQ13}),1.0]])]});}
            var Q212;
            {var subQ0=sQuery(id+"F0.wireOp",EDGE,"E1049");Q212=makeQuery(id+"F0.imprint","IMPRINT",FACE,{"disambiguationData":[TD([[makeQuery(id+"F0.imprint","IMPRINT",EDGE,{"derivedFrom":subQ0}),-1.0]])]});}
            var Q213;
            Q213=makeQuery(id+"F0.imprint","IMPRINT",FACE,{"disambiguationData":[TD([[makeQuery(id+"F0.imprint","IMPRINT",EDGE,{"derivedFrom":sQuery(id+"F0.wireOp",EDGE,"E866")}),1.0]])]});
            var Q214;
            {var subQ6=sQuery(id+"F0.wireOp",EDGE,"E924");Q214=makeQuery(id+"F0.imprint","IMPRINT",FACE,{"disambiguationData":[TD([[makeQuery(id+"F0.imprint","IMPRINT",EDGE,{"derivedFrom":subQ6}),1.0]])]});}
            var Q215;
            {var subQ5=sQuery(id+"F0.wireOp",EDGE,"E1217");Q215=makeQuery(id+"F0.imprint","IMPRINT",FACE,{"disambiguationData":[TD([[makeQuery(id+"F0.imprint","IMPRINT",EDGE,{"derivedFrom":subQ5}),1.0]])]});}
            var Q216;
            {var subQ18=sQuery(id+"F0.wireOp",EDGE,"E1051");Q216=makeQuery(id+"F0.imprint","IMPRINT",FACE,{"disambiguationData":[TD([[makeQuery(id+"F0.imprint","IMPRINT",EDGE,{"derivedFrom":subQ18}),-1.0]])]});}
            var Q217;
            {var subQ0=sQuery(id+"F0.wireOp",EDGE,"E1325");var subQ1=sQuery(id+"F0.wireOp",EDGE,"E145");var subQ2=makeQuery(id+"F0.imprint","INTERSECT",VERTEX,{"derivedFrom":[subQ1,subQ0]});Q217=makeQuery(id+"F0.imprint","IMPRINT",FACE,{"disambiguationData":[TD([[makeQuery(id+"F0.imprint","IMPRINT",EDGE,{"disambiguationData":[TD([[subQ2,-1.0]])],"derivedFrom":subQ1}),-1.0]])]});}
            var Q218;
            {var subQ17=sQuery(id+"F0.wireOp",EDGE,"E993");Q218=makeQuery(id+"F0.imprint","IMPRINT",FACE,{"disambiguationData":[TD([[makeQuery(id+"F0.imprint","IMPRINT",EDGE,{"derivedFrom":subQ17}),1.0]])]});}
            var Q219;
            {var subQ13=sQuery(id+"F0.wireOp",EDGE,"E1063");Q219=makeQuery(id+"F0.imprint","IMPRINT",FACE,{"disambiguationData":[TD([[makeQuery(id+"F0.imprint","IMPRINT",EDGE,{"derivedFrom":subQ13}),1.0]])]});}
            var Q220;
            {var subQ0=sQuery(id+"F0.wireOp",EDGE,"E834");var subQ1=sQuery(id+"F0.wireOp",EDGE,"E96");var subQ2=makeQuery(id+"F0.imprint","INTERSECT",VERTEX,{"derivedFrom":[subQ1,subQ0]});Q220=makeQuery(id+"F0.imprint","IMPRINT",FACE,{"disambiguationData":[TD([[makeQuery(id+"F0.imprint","IMPRINT",EDGE,{"disambiguationData":[TD([[subQ2,-1.0]])],"derivedFrom":subQ1}),1.0]])]});}
            var Q221;
            {var subQ5=sQuery(id+"F0.wireOp",EDGE,"E1289");var subQ6=sQuery(id+"F0.wireOp",EDGE,"E146");var subQ7=makeQuery(id+"F0.imprint","INTERSECT",VERTEX,{"derivedFrom":[subQ6,subQ5]});Q221=makeQuery(id+"F0.imprint","IMPRINT",FACE,{"disambiguationData":[TD([[makeQuery(id+"F0.imprint","IMPRINT",EDGE,{"disambiguationData":[TD([[subQ7,-1.0]])],"derivedFrom":subQ6}),-1.0]])]});}
            var Q222;
            Q222=makeQuery(id+"F0.imprint","IMPRINT",FACE,{"disambiguationData":[TD([[makeQuery(id+"F0.imprint","IMPRINT",EDGE,{"derivedFrom":sQuery(id+"F0.wireOp",EDGE,"E1031")}),-1.0]])]});
            var Q223;
            {var subQ0=sQuery(id+"F0.wireOp",EDGE,"E1056");Q223=makeQuery(id+"F0.imprint","IMPRINT",FACE,{"disambiguationData":[TD([[makeQuery(id+"F0.imprint","IMPRINT",EDGE,{"derivedFrom":subQ0}),-1.0]])]});}
            var Q224;
            {var subQ1=sQuery(id+"F0.wireOp",EDGE,"E145");var subQ5=sQuery(id+"F0.wireOp",EDGE,"E146");var subQ6=makeQuery(id+"F0.imprint","INTERSECT",VERTEX,{"derivedFrom":[subQ1,subQ5]});Q224=makeQuery(id+"F0.imprint","IMPRINT",FACE,{"disambiguationData":[TD([[makeQuery(id+"F0.imprint","IMPRINT",EDGE,{"disambiguationData":[TD([[subQ6,1.0]])],"derivedFrom":subQ1}),-1.0]])]});}
            var Q225;
            {var subQ6=sQuery(id+"F0.wireOp",EDGE,"E993");Q225=makeQuery(id+"F0.imprint","IMPRINT",FACE,{"disambiguationData":[TD([[makeQuery(id+"F0.imprint","IMPRINT",EDGE,{"derivedFrom":subQ6}),-1.0]])]});}
            var Q226;
            {var subQ5=sQuery(id+"F0.wireOp",EDGE,"E1277");Q226=makeQuery(id+"F0.imprint","IMPRINT",FACE,{"disambiguationData":[TD([[makeQuery(id+"F0.imprint","IMPRINT",EDGE,{"derivedFrom":subQ5}),1.0]])]});}
            var Q227;
            {var subQ5=sQuery(id+"F0.wireOp",EDGE,"E1048");var subQ6=sQuery(id+"F0.wireOp",EDGE,"E140");var subQ7=makeQuery(id+"F0.imprint","INTERSECT",VERTEX,{"derivedFrom":[subQ6,subQ5]});Q227=makeQuery(id+"F0.imprint","IMPRINT",FACE,{"disambiguationData":[TD([[makeQuery(id+"F0.imprint","IMPRINT",EDGE,{"disambiguationData":[TD([[subQ7,-1.0]])],"derivedFrom":subQ6}),-1.0]])]});}
            var Q228;
            {var subQ3=sQuery(id+"F0.wireOp",EDGE,"E865");var subQ8=sQuery(id+"F0.wireOp",EDGE,"E99");var subQ12=makeQuery(id+"F0.imprint","INTERSECT",VERTEX,{"derivedFrom":[subQ8,subQ3]});Q228=makeQuery(id+"F0.imprint","IMPRINT",FACE,{"disambiguationData":[TD([[makeQuery(id+"F0.imprint","IMPRINT",EDGE,{"disambiguationData":[TD([[subQ12,-1.0]])],"derivedFrom":subQ8}),-1.0]])]});}
            var Q229;
            {var subQ9=sQuery(id+"F0.wireOp",EDGE,"E97");Q229=makeQuery(id+"F0.imprint","IMPRINT",FACE,{"disambiguationData":[TD([[makeQuery(id+"F0.imprint","IMPRINT",EDGE,{"derivedFrom":subQ9}),-1.0]])]});}
            var Q230;
            {var subQ0=sQuery(id+"F0.wireOp",EDGE,"E1261");var subQ1=sQuery(id+"F0.wireOp",EDGE,"E146");var subQ2=makeQuery(id+"F0.imprint","INTERSECT",VERTEX,{"derivedFrom":[subQ1,subQ0]});Q230=makeQuery(id+"F0.imprint","IMPRINT",FACE,{"disambiguationData":[TD([[makeQuery(id+"F0.imprint","IMPRINT",EDGE,{"disambiguationData":[TD([[subQ2,-1.0]])],"derivedFrom":subQ1}),-1.0]])]});}
            var Q231;
            {var subQ10=sQuery(id+"F0.wireOp",EDGE,"E1247");Q231=makeQuery(id+"F0.imprint","IMPRINT",FACE,{"disambiguationData":[TD([[makeQuery(id+"F0.imprint","IMPRINT",EDGE,{"derivedFrom":subQ10}),1.0]])]});}
            var Q232;
            {var subQ0=sQuery(id+"F0.wireOp",EDGE,"E857");var subQ1=sQuery(id+"F0.wireOp",EDGE,"E99");var subQ2=makeQuery(id+"F0.imprint","INTERSECT",VERTEX,{"derivedFrom":[subQ1,subQ0]});Q232=makeQuery(id+"F0.imprint","IMPRINT",FACE,{"disambiguationData":[TD([[makeQuery(id+"F0.imprint","IMPRINT",EDGE,{"disambiguationData":[TD([[subQ2,-1.0]])],"derivedFrom":subQ1}),-1.0]])]});}
            var Q233;
            {var subQ0=sQuery(id+"F0.wireOp",EDGE,"E1291");var subQ1=sQuery(id+"F0.wireOp",EDGE,"E145");var subQ2=makeQuery(id+"F0.imprint","INTERSECT",VERTEX,{"derivedFrom":[subQ1,subQ0]});Q233=makeQuery(id+"F0.imprint","IMPRINT",FACE,{"disambiguationData":[TD([[makeQuery(id+"F0.imprint","IMPRINT",EDGE,{"disambiguationData":[TD([[subQ2,-1.0]])],"derivedFrom":subQ1}),-1.0]])]});}
            var Q234;
            {var subQ5=sQuery(id+"F0.wireOp",EDGE,"E99");var subQ7=sQuery(id+"F0.wireOp",EDGE,"E865");var subQ10=makeQuery(id+"F0.imprint","INTERSECT",VERTEX,{"derivedFrom":[subQ5,subQ7]});Q234=makeQuery(id+"F0.imprint","IMPRINT",FACE,{"disambiguationData":[TD([[makeQuery(id+"F0.imprint","IMPRINT",EDGE,{"disambiguationData":[TD([[subQ10,-1.0]])],"derivedFrom":subQ5}),1.0]])]});}
            var Q235;
            {var subQ0=sQuery(id+"F0.wireOp",EDGE,"E1117");Q235=makeQuery(id+"F0.imprint","IMPRINT",FACE,{"disambiguationData":[TD([[makeQuery(id+"F0.imprint","IMPRINT",EDGE,{"derivedFrom":subQ0}),1.0]])]});}
            var Q236;
            {var subQ0=sQuery(id+"F0.wireOp",EDGE,"E845");var subQ1=sQuery(id+"F0.wireOp",EDGE,"E844");var subQ2=makeQuery(id+"F0.imprint","INTERSECT",VERTEX,{"derivedFrom":[subQ1,subQ0]});Q236=makeQuery(id+"F0.imprint","IMPRINT",FACE,{"disambiguationData":[TD([[makeQuery(id+"F0.imprint","IMPRINT",EDGE,{"disambiguationData":[TD([[subQ2,1.0]])],"derivedFrom":subQ1}),-1.0]])]});}
            var Q237;
            {var subQ0=sQuery(id+"F0.wireOp",EDGE,"E844");var subQ1=sQuery(id+"F0.wireOp",EDGE,"E99");var subQ2=makeQuery(id+"F0.imprint","INTERSECT",VERTEX,{"derivedFrom":[subQ1,subQ0]});Q237=makeQuery(id+"F0.imprint","IMPRINT",FACE,{"disambiguationData":[TD([[makeQuery(id+"F0.imprint","IMPRINT",EDGE,{"disambiguationData":[TD([[subQ2,-1.0]])],"derivedFrom":subQ1}),-1.0]])]});}
            var Q238;
            {var subQ0=sQuery(id+"F0.wireOp",EDGE,"E861");var subQ1=sQuery(id+"F0.wireOp",EDGE,"E857");var subQ2=makeQuery(id+"F0.imprint","INTERSECT",VERTEX,{"derivedFrom":[subQ1,subQ0]});Q238=makeQuery(id+"F0.imprint","IMPRINT",FACE,{"disambiguationData":[TD([[makeQuery(id+"F0.imprint","IMPRINT",EDGE,{"disambiguationData":[TD([[subQ2,-1.0]])],"derivedFrom":subQ1}),-1.0]])]});}
            var Q239;
            {var subQ0=sQuery(id+"F0.wireOp",EDGE,"E1103");var subQ1=sQuery(id+"F0.wireOp",EDGE,"E140");var subQ2=makeQuery(id+"F0.imprint","INTERSECT",VERTEX,{"derivedFrom":[subQ1,subQ0]});Q239=makeQuery(id+"F0.imprint","IMPRINT",FACE,{"disambiguationData":[TD([[makeQuery(id+"F0.imprint","IMPRINT",EDGE,{"disambiguationData":[TD([[subQ2,-1.0]])],"derivedFrom":subQ1}),1.0]])]});}
            var Q240;
            {var subQ0=sQuery(id+"F0.wireOp",EDGE,"E1051");Q240=makeQuery(id+"F0.imprint","IMPRINT",FACE,{"disambiguationData":[TD([[makeQuery(id+"F0.imprint","IMPRINT",EDGE,{"derivedFrom":subQ0}),1.0]])]});}
            var Q241;
            {var subQ22=sQuery(id+"F0.wireOp",EDGE,"E649");Q241=makeQuery(id+"F0.imprint","IMPRINT",FACE,{"disambiguationData":[TD([[makeQuery(id+"F0.imprint","IMPRINT",EDGE,{"derivedFrom":subQ22}),1.0]])]});}
            var Q242;
            Q242=makeQuery(id+"F0.imprint","IMPRINT",FACE,{"disambiguationData":[TD([[makeQuery(id+"F0.imprint","IMPRINT",EDGE,{"derivedFrom":sQuery(id+"F0.wireOp",EDGE,"E866")}),-1.0]])]});
            var Q243;
            {var subQ20=sQuery(id+"F0.wireOp",EDGE,"E519");Q243=makeQuery(id+"F0.imprint","IMPRINT",FACE,{"disambiguationData":[TD([[makeQuery(id+"F0.imprint","IMPRINT",EDGE,{"derivedFrom":subQ20}),1.0]])]});}
            var Q244;
            {var subQ2=sQuery(id+"F0.wireOp",EDGE,"E467");Q244=makeQuery(id+"F0.imprint","IMPRINT",FACE,{"disambiguationData":[TD([[makeQuery(id+"F0.imprint","IMPRINT",EDGE,{"derivedFrom":subQ2}),1.0]])]});}
            var Q245;
            {var subQ0=sQuery(id+"F0.wireOp",EDGE,"E973");Q245=makeQuery(id+"F0.imprint","IMPRINT",FACE,{"disambiguationData":[TD([[makeQuery(id+"F0.imprint","IMPRINT",EDGE,{"derivedFrom":subQ0}),1.0]])]});}
            var Q246;
            Q246=makeQuery(id+"F0.imprint","IMPRINT",FACE,{"disambiguationData":[TD([[makeQuery(id+"F0.imprint","IMPRINT",EDGE,{"derivedFrom":sQuery(id+"F0.wireOp",EDGE,"E687")}),-1.0]])]});
            var Q247;
            {var subQ0=sQuery(id+"F0.wireOp",EDGE,"E976");Q247=makeQuery(id+"F0.imprint","IMPRINT",FACE,{"disambiguationData":[TD([[makeQuery(id+"F0.imprint","IMPRINT",EDGE,{"derivedFrom":subQ0}),-1.0]])]});}
            var Q248;
            {var subQ5=sQuery(id+"F0.wireOp",EDGE,"E37");var subQ7=sQuery(id+"F0.wireOp",EDGE,"E38");var subQ8=makeQuery(id+"F0.imprint","INTERSECT",VERTEX,{"derivedFrom":[subQ5,subQ7]});Q248=makeQuery(id+"F0.imprint","IMPRINT",FACE,{"disambiguationData":[TD([[makeQuery(id+"F0.imprint","IMPRINT",EDGE,{"disambiguationData":[TD([[subQ8,1.0]])],"derivedFrom":subQ5}),1.0]])]});}
            var Q249;
            {var subQ5=sQuery(id+"F0.wireOp",EDGE,"E695");Q249=makeQuery(id+"F0.imprint","IMPRINT",FACE,{"disambiguationData":[TD([[makeQuery(id+"F0.imprint","IMPRINT",EDGE,{"derivedFrom":subQ5}),-1.0]])]});}
            var Q250;
            {var subQ1=sQuery(id+"F0.wireOp",EDGE,"E1067");Q250=makeQuery(id+"F0.imprint","IMPRINT",FACE,{"disambiguationData":[TD([[makeQuery(id+"F0.imprint","IMPRINT",EDGE,{"derivedFrom":subQ1}),1.0]])]});}
            var Q251;
            {var subQ0=sQuery(id+"F0.wireOp",EDGE,"E695");Q251=makeQuery(id+"F0.imprint","IMPRINT",FACE,{"disambiguationData":[TD([[makeQuery(id+"F0.imprint","IMPRINT",EDGE,{"derivedFrom":subQ0}),1.0]])]});}
            var Q252;
            Q252=makeQuery(id+"F0.imprint","IMPRINT",FACE,{"disambiguationData":[TD([[makeQuery(id+"F0.imprint","IMPRINT",EDGE,{"derivedFrom":sQuery(id+"F0.wireOp",EDGE,"E687")}),1.0]])]});
            var Q253;
            {var subQ0=sQuery(id+"F0.wireOp",EDGE,"E824");Q253=makeQuery(id+"F0.imprint","IMPRINT",FACE,{"disambiguationData":[TD([[makeQuery(id+"F0.imprint","IMPRINT",EDGE,{"derivedFrom":subQ0}),-1.0]])]});}
            var Q254;
            {var subQ4=sQuery(id+"F0.wireOp",EDGE,"E469");Q254=makeQuery(id+"F0.imprint","IMPRINT",FACE,{"disambiguationData":[TD([[makeQuery(id+"F0.imprint","IMPRINT",EDGE,{"derivedFrom":subQ4}),1.0]])]});}
            var Q255;
            {var subQ3=sQuery(id+"F0.wireOp",EDGE,"E785");Q255=makeQuery(id+"F0.imprint","IMPRINT",FACE,{"disambiguationData":[TD([[makeQuery(id+"F0.imprint","IMPRINT",EDGE,{"derivedFrom":subQ3}),1.0]])]});}
            var Q256;
            {var subQ0=sQuery(id+"F0.wireOp",EDGE,"E787");var subQ1=sQuery(id+"F0.wireOp",EDGE,"E38");var subQ2=makeQuery(id+"F0.imprint","INTERSECT",VERTEX,{"derivedFrom":[subQ1,subQ0]});Q256=makeQuery(id+"F0.imprint","IMPRINT",FACE,{"disambiguationData":[TD([[makeQuery(id+"F0.imprint","IMPRINT",EDGE,{"disambiguationData":[TD([[subQ2,-1.0]])],"derivedFrom":subQ1}),1.0]])]});}
            var Q257;
            {var subQ0=sQuery(id+"F0.wireOp",EDGE,"E968");Q257=makeQuery(id+"F0.imprint","IMPRINT",FACE,{"disambiguationData":[TD([[makeQuery(id+"F0.imprint","IMPRINT",EDGE,{"derivedFrom":subQ0}),-1.0]])]});}
            var Q258;
            {var subQ16=sQuery(id+"F0.wireOp",EDGE,"E728");Q258=makeQuery(id+"F0.imprint","IMPRINT",FACE,{"disambiguationData":[TD([[makeQuery(id+"F0.imprint","IMPRINT",EDGE,{"derivedFrom":subQ16}),1.0]])]});}
            var Q259;
            {var subQ0=sQuery(id+"F0.wireOp",EDGE,"E458");Q259=makeQuery(id+"F0.imprint","IMPRINT",FACE,{"disambiguationData":[TD([[makeQuery(id+"F0.imprint","IMPRINT",EDGE,{"derivedFrom":subQ0}),-1.0]])]});}
            var Q260;
            {var subQ0=sQuery(id+"F0.wireOp",EDGE,"E1221");var subQ1=sQuery(id+"F0.wireOp",EDGE,"E1220");var subQ2=makeQuery(id+"F0.imprint","INTERSECT",VERTEX,{"derivedFrom":[subQ1,subQ0]});Q260=makeQuery(id+"F0.imprint","IMPRINT",FACE,{"disambiguationData":[TD([[makeQuery(id+"F0.imprint","IMPRINT",EDGE,{"disambiguationData":[TD([[subQ2,1.0]])],"derivedFrom":subQ1}),-1.0]])]});}
            var Q261;
            {var subQ0=sQuery(id+"F0.wireOp",EDGE,"E467");Q261=makeQuery(id+"F0.imprint","IMPRINT",FACE,{"disambiguationData":[TD([[makeQuery(id+"F0.imprint","IMPRINT",EDGE,{"derivedFrom":subQ0}),-1.0]])]});}
            var Q262;
            Q262=makeQuery(id+"F0.imprint","IMPRINT",FACE,{"disambiguationData":[TD([[makeQuery(id+"F0.imprint","IMPRINT",EDGE,{"derivedFrom":sQuery(id+"F0.wireOp",EDGE,"E939")}),1.0]])]});
            var Q263;
            {var subQ10=sQuery(id+"F0.wireOp",EDGE,"E800");Q263=makeQuery(id+"F0.imprint","IMPRINT",FACE,{"disambiguationData":[TD([[makeQuery(id+"F0.imprint","IMPRINT",EDGE,{"derivedFrom":subQ10}),1.0]])]});}
            var Q264;
            Q264=makeQuery(id+"F0.imprint","IMPRINT",FACE,{"disambiguationData":[TD([[makeQuery(id+"F0.imprint","IMPRINT",EDGE,{"derivedFrom":sQuery(id+"F0.wireOp",EDGE,"E522")}),-1.0]])]});
            var Q265;
            {var subQ0=sQuery(id+"F0.wireOp",EDGE,"E924");Q265=makeQuery(id+"F0.imprint","IMPRINT",FACE,{"disambiguationData":[TD([[makeQuery(id+"F0.imprint","IMPRINT",EDGE,{"derivedFrom":subQ0}),-1.0]])]});}
            var Q266;
            {var subQ0=sQuery(id+"F0.wireOp",EDGE,"E624");Q266=makeQuery(id+"F0.imprint","IMPRINT",FACE,{"disambiguationData":[TD([[makeQuery(id+"F0.imprint","IMPRINT",EDGE,{"derivedFrom":subQ0}),1.0]])]});}
            var Q267;
            {var subQ0=sQuery(id+"F0.wireOp",EDGE,"E823");var subQ1=sQuery(id+"F0.wireOp",EDGE,"E38");var subQ2=makeQuery(id+"F0.imprint","INTERSECT",VERTEX,{"derivedFrom":[subQ1,subQ0]});Q267=makeQuery(id+"F0.imprint","IMPRINT",FACE,{"disambiguationData":[TD([[makeQuery(id+"F0.imprint","IMPRINT",EDGE,{"disambiguationData":[TD([[subQ2,-1.0]])],"derivedFrom":subQ1}),-1.0]])]});}
            var Q268;
            Q268=makeQuery(id+"F0.imprint","IMPRINT",FACE,{"disambiguationData":[TD([[makeQuery(id+"F0.imprint","IMPRINT",EDGE,{"derivedFrom":sQuery(id+"F0.wireOp",EDGE,"E1008")}),1.0]])]});
            var Q269;
            {var subQ6=sQuery(id+"F0.wireOp",EDGE,"E785");Q269=makeQuery(id+"F0.imprint","IMPRINT",FACE,{"disambiguationData":[TD([[makeQuery(id+"F0.imprint","IMPRINT",EDGE,{"derivedFrom":subQ6}),-1.0]])]});}
            var Q270;
            {var subQ0=sQuery(id+"F0.wireOp",EDGE,"E624");Q270=makeQuery(id+"F0.imprint","IMPRINT",FACE,{"disambiguationData":[TD([[makeQuery(id+"F0.imprint","IMPRINT",EDGE,{"derivedFrom":subQ0}),-1.0]])]});}
            var Q271;
            {var subQ0=sQuery(id+"F0.wireOp",EDGE,"E719");Q271=makeQuery(id+"F0.imprint","IMPRINT",FACE,{"disambiguationData":[TD([[makeQuery(id+"F0.imprint","IMPRINT",EDGE,{"derivedFrom":subQ0}),-1.0]])]});}
            var Q272;
            {var subQ0=sQuery(id+"F0.wireOp",EDGE,"E628");var subQ1=sQuery(id+"F0.wireOp",EDGE,"E73");var subQ2=makeQuery(id+"F0.imprint","INTERSECT",VERTEX,{"derivedFrom":[subQ1,subQ0]});Q272=makeQuery(id+"F0.imprint","IMPRINT",FACE,{"disambiguationData":[TD([[makeQuery(id+"F0.imprint","IMPRINT",EDGE,{"disambiguationData":[TD([[subQ2,-1.0]])],"derivedFrom":subQ1}),1.0]])]});}
            var Q273;
            {var subQ13=sQuery(id+"F0.wireOp",EDGE,"E719");Q273=makeQuery(id+"F0.imprint","IMPRINT",FACE,{"disambiguationData":[TD([[makeQuery(id+"F0.imprint","IMPRINT",EDGE,{"derivedFrom":subQ13}),1.0]])]});}
            var Q274;
            {var subQ7=sQuery(id+"F0.wireOp",EDGE,"E723");Q274=makeQuery(id+"F0.imprint","IMPRINT",FACE,{"disambiguationData":[TD([[makeQuery(id+"F0.imprint","IMPRINT",EDGE,{"derivedFrom":subQ7}),1.0]])]});}
            var Q275;
            {var subQ6=sQuery(id+"F0.wireOp",EDGE,"E533");Q275=makeQuery(id+"F0.imprint","IMPRINT",FACE,{"disambiguationData":[TD([[makeQuery(id+"F0.imprint","IMPRINT",EDGE,{"derivedFrom":subQ6}),1.0]])]});}
            var Q276;
            {var subQ7=sQuery(id+"F0.wireOp",EDGE,"E1069");Q276=makeQuery(id+"F0.imprint","IMPRINT",FACE,{"disambiguationData":[TD([[makeQuery(id+"F0.imprint","IMPRINT",EDGE,{"derivedFrom":subQ7}),1.0]])]});}
            var Q277;
            {var subQ4=sQuery(id+"F0.wireOp",EDGE,"E629");Q277=makeQuery(id+"F0.imprint","IMPRINT",FACE,{"disambiguationData":[TD([[makeQuery(id+"F0.imprint","IMPRINT",EDGE,{"derivedFrom":subQ4}),1.0]])]});}
            var Q278;
            {var subQ0=sQuery(id+"F0.wireOp",EDGE,"E783");Q278=makeQuery(id+"F0.imprint","IMPRINT",FACE,{"disambiguationData":[TD([[makeQuery(id+"F0.imprint","IMPRINT",EDGE,{"derivedFrom":subQ0}),-1.0]])]});}
            var Q279;
            {var subQ7=sQuery(id+"F0.wireOp",EDGE,"E533");Q279=makeQuery(id+"F0.imprint","IMPRINT",FACE,{"disambiguationData":[TD([[makeQuery(id+"F0.imprint","IMPRINT",EDGE,{"derivedFrom":subQ7}),-1.0]])]});}
            var Q280;
            {var subQ0=sQuery(id+"F0.wireOp",EDGE,"E723");Q280=makeQuery(id+"F0.imprint","IMPRINT",FACE,{"disambiguationData":[TD([[makeQuery(id+"F0.imprint","IMPRINT",EDGE,{"derivedFrom":subQ0}),-1.0]])]});}
            var Q281;
            {var subQ1=sQuery(id+"F0.wireOp",EDGE,"E519");Q281=makeQuery(id+"F0.imprint","IMPRINT",FACE,{"disambiguationData":[TD([[makeQuery(id+"F0.imprint","IMPRINT",EDGE,{"derivedFrom":subQ1}),-1.0]])]});}
            var Q282;
            Q282=makeQuery(id+"F0.imprint","IMPRINT",FACE,{"disambiguationData":[TD([[makeQuery(id+"F0.imprint","IMPRINT",EDGE,{"derivedFrom":sQuery(id+"F0.wireOp",EDGE,"E1130")}),1.0]])]});
            var Q283;
            {var subQ5=sQuery(id+"F0.wireOp",EDGE,"E649");Q283=makeQuery(id+"F0.imprint","IMPRINT",FACE,{"disambiguationData":[TD([[makeQuery(id+"F0.imprint","IMPRINT",EDGE,{"derivedFrom":subQ5}),-1.0]])]});}
            var Q284;
            {var subQ6=sQuery(id+"F0.wireOp",EDGE,"E1148");Q284=makeQuery(id+"F0.imprint","IMPRINT",FACE,{"disambiguationData":[TD([[makeQuery(id+"F0.imprint","IMPRINT",EDGE,{"derivedFrom":subQ6}),1.0]])]});}
            var Q285;
            Q285=makeQuery(id+"F0.imprint","IMPRINT",FACE,{"disambiguationData":[TD([[makeQuery(id+"F0.imprint","IMPRINT",EDGE,{"derivedFrom":sQuery(id+"F0.wireOp",EDGE,"E1022")}),1.0]])]});
            var Q286;
            {var subQ5=sQuery(id+"F0.wireOp",EDGE,"E491");Q286=makeQuery(id+"F0.imprint","IMPRINT",FACE,{"disambiguationData":[TD([[makeQuery(id+"F0.imprint","IMPRINT",EDGE,{"derivedFrom":subQ5}),1.0]])]});}
            var Q287;
            Q287=makeQuery(id+"F0.imprint","IMPRINT",FACE,{"disambiguationData":[TD([[makeQuery(id+"F0.imprint","IMPRINT",EDGE,{"derivedFrom":sQuery(id+"F0.wireOp",EDGE,"E595")}),1.0]])]});
            var Q288;
            {var subQ6=sQuery(id+"F0.wireOp",EDGE,"E789");Q288=makeQuery(id+"F0.imprint","IMPRINT",FACE,{"disambiguationData":[TD([[makeQuery(id+"F0.imprint","IMPRINT",EDGE,{"derivedFrom":subQ6}),1.0]])]});}
            var Q289;
            Q289=makeQuery(id+"F0.imprint","IMPRINT",FACE,{"disambiguationData":[TD([[makeQuery(id+"F0.imprint","IMPRINT",EDGE,{"derivedFrom":sQuery(id+"F0.wireOp",EDGE,"E678")}),1.0]])]});
            var Q290;
            Q290=makeQuery(id+"F0.imprint","IMPRINT",FACE,{"disambiguationData":[TD([[makeQuery(id+"F0.imprint","IMPRINT",EDGE,{"derivedFrom":sQuery(id+"F0.wireOp",EDGE,"E664")}),1.0]])]});
            extrude(context, id + "F1", {"entities" : qUnion([Q0, Q1, Q2, Q3, Q4, Q5, Q6, Q7, Q8, Q9, Q10, Q11, Q12, Q13, Q14, Q15, Q16, Q17, Q18, Q19, Q20, Q21, Q22, Q23, Q24, Q25, Q26, Q27, Q28, Q29, Q30, Q31, Q32, Q33, Q34, Q35, Q36, Q37, Q38, Q39, Q40, Q41, Q42, Q43, Q44, Q45, Q46, Q47, Q48, Q49, Q50, Q51, Q52, Q53, Q54, Q55, Q56, Q57, Q58, Q59, Q60, Q61, Q62, Q63, Q64, Q65, Q66, Q67, Q68, Q69, Q70, Q71, Q72, Q73, Q74, Q75, Q76, Q77, Q78, Q79, Q80, Q81, Q82, Q83, Q84, Q85, Q86, Q87, Q88, Q89, Q90, Q91, Q92, Q93, Q94, Q95, Q96, Q97, Q98, Q99, Q100, Q101, Q102, Q103, Q104, Q105, Q106, Q107, Q108, Q109, Q110, Q111, Q112, Q113, Q114, Q115, Q116, Q117, Q118, Q119, Q120, Q121, Q122, Q123, Q124, Q125, Q126, Q127, Q128, Q129, Q130, Q131, Q132, Q133, Q134, Q135, Q136, Q137, Q138, Q139, Q140, Q141, Q142, Q143, Q144, Q145, Q146, Q147, Q148, Q149, Q150, Q151, Q152, Q153, Q154, Q155, Q156, Q157, Q158, Q159, Q160, Q161, Q162, Q163, Q164, Q165, Q166, Q167, Q168, Q169, Q170, Q171, Q172, Q173, Q174, Q175, Q176, Q177, Q178, Q179, Q180, Q181, Q182, Q183, Q184, Q185, Q186, Q187, Q188, Q189, Q190, Q191, Q192, Q193, Q194, Q195, Q196, Q197, Q198, Q199, Q200, Q201, Q202, Q203, Q204, Q205, Q206, Q207, Q208, Q209, Q210, Q211, Q212, Q213, Q214, Q215, Q216, Q217, Q218, Q219, Q220, Q221, Q222, Q223, Q224, Q225, Q226, Q227, Q228, Q229, Q230, Q231, Q232, Q233, Q234, Q235, Q236, Q237, Q238, Q239, Q240, Q241, Q242, Q243, Q244, Q245, Q246, Q247, Q248, Q249, Q250, Q251, Q252, Q253, Q254, Q255, Q256, Q257, Q258, Q259, Q260, Q261, Q262, Q263, Q264, Q265, Q266, Q267, Q268, Q269, Q270, Q271, Q272, Q273, Q274, Q275, Q276, Q277, Q278, Q279, Q280, Q281, Q282, Q283, Q284, Q285, Q286, Q287, Q288, Q289, Q290]), "oppositeDirection" : true, "depth" : 3 * mm, "offsetDistance" : 25 * mm});
        }
        {
            var Q0;
            {var subQ6=sQuery(id+"F0.wireOp",EDGE,"E482");Q0=makeQuery(id+"F0.imprint","IMPRINT",FACE,{"disambiguationData":[TD([[makeQuery(id+"F0.imprint","IMPRINT",EDGE,{"derivedFrom":subQ6}),-1.0]])]});}
            var Q1;
            Q1=makeQuery(id+"F0.imprint","IMPRINT",FACE,{"disambiguationData":[TD([[makeQuery(id+"F0.imprint","IMPRINT",EDGE,{"derivedFrom":sQuery(id+"F0.wireOp",EDGE,"E452")}),-1.0]])]});
            var Q2;
            {var subQ0=sQuery(id+"F0.wireOp",EDGE,"E458");Q2=makeQuery(id+"F0.imprint","IMPRINT",FACE,{"disambiguationData":[TD([[makeQuery(id+"F0.imprint","IMPRINT",EDGE,{"derivedFrom":subQ0}),-1.0]])]});}
            var Q3;
            {var subQ0=sQuery(id+"F0.wireOp",EDGE,"E467");Q3=makeQuery(id+"F0.imprint","IMPRINT",FACE,{"disambiguationData":[TD([[makeQuery(id+"F0.imprint","IMPRINT",EDGE,{"derivedFrom":subQ0}),-1.0]])]});}
            var Q4;
            Q4=makeQuery(id+"F0.imprint","IMPRINT",FACE,{"disambiguationData":[TD([[makeQuery(id+"F0.imprint","IMPRINT",EDGE,{"derivedFrom":sQuery(id+"F0.wireOp",EDGE,"E522")}),-1.0]])]});
            var Q5;
            {var subQ7=sQuery(id+"F0.wireOp",EDGE,"E533");Q5=makeQuery(id+"F0.imprint","IMPRINT",FACE,{"disambiguationData":[TD([[makeQuery(id+"F0.imprint","IMPRINT",EDGE,{"derivedFrom":subQ7}),-1.0]])]});}
            var Q6;
            Q6=makeQuery(id+"F0.imprint","IMPRINT",FACE,{"disambiguationData":[TD([[makeQuery(id+"F0.imprint","IMPRINT",EDGE,{"derivedFrom":sQuery(id+"F0.wireOp",EDGE,"E687")}),-1.0]])]});
            var Q7;
            {var subQ0=sQuery(id+"F0.wireOp",EDGE,"E719");Q7=makeQuery(id+"F0.imprint","IMPRINT",FACE,{"disambiguationData":[TD([[makeQuery(id+"F0.imprint","IMPRINT",EDGE,{"derivedFrom":subQ0}),-1.0]])]});}
            var Q8;
            {var subQ0=sQuery(id+"F0.wireOp",EDGE,"E723");Q8=makeQuery(id+"F0.imprint","IMPRINT",FACE,{"disambiguationData":[TD([[makeQuery(id+"F0.imprint","IMPRINT",EDGE,{"derivedFrom":subQ0}),-1.0]])]});}
            var Q9;
            {var subQ14=sQuery(id+"F0.wireOp",EDGE,"E97");Q9=makeQuery(id+"F0.imprint","IMPRINT",FACE,{"disambiguationData":[TD([[makeQuery(id+"F0.imprint","IMPRINT",EDGE,{"derivedFrom":subQ14}),1.0]])]});}
            var Q10;
            {var subQ0=sQuery(id+"F0.wireOp",EDGE,"E835");var subQ9=sQuery(id+"F0.wireOp",EDGE,"E37");var subQ10=makeQuery(id+"F0.imprint","INTERSECT",VERTEX,{"derivedFrom":[subQ9,subQ0]});Q10=makeQuery(id+"F0.imprint","IMPRINT",FACE,{"disambiguationData":[TD([[makeQuery(id+"F0.imprint","IMPRINT",EDGE,{"disambiguationData":[TD([[subQ10,-1.0]])],"derivedFrom":subQ9}),-1.0]])]});}
            var Q11;
            {var subQ9=sQuery(id+"F0.wireOp",EDGE,"E97");Q11=makeQuery(id+"F0.imprint","IMPRINT",FACE,{"disambiguationData":[TD([[makeQuery(id+"F0.imprint","IMPRINT",EDGE,{"derivedFrom":subQ9}),-1.0]])]});}
            var Q12;
            {var subQ5=sQuery(id+"F0.wireOp",EDGE,"E836");Q12=makeQuery(id+"F0.imprint","IMPRINT",FACE,{"disambiguationData":[TD([[makeQuery(id+"F0.imprint","IMPRINT",EDGE,{"derivedFrom":subQ5}),-1.0]])]});}
            var Q13;
            {var subQ0=sQuery(id+"F0.wireOp",EDGE,"E845");var subQ1=sQuery(id+"F0.wireOp",EDGE,"E844");var subQ2=makeQuery(id+"F0.imprint","INTERSECT",VERTEX,{"derivedFrom":[subQ1,subQ0]});Q13=makeQuery(id+"F0.imprint","IMPRINT",FACE,{"disambiguationData":[TD([[makeQuery(id+"F0.imprint","IMPRINT",EDGE,{"disambiguationData":[TD([[subQ2,1.0]])],"derivedFrom":subQ1}),-1.0]])]});}
            var Q14;
            {var subQ0=sQuery(id+"F0.wireOp",EDGE,"E861");var subQ1=sQuery(id+"F0.wireOp",EDGE,"E857");var subQ2=makeQuery(id+"F0.imprint","INTERSECT",VERTEX,{"derivedFrom":[subQ1,subQ0]});Q14=makeQuery(id+"F0.imprint","IMPRINT",FACE,{"disambiguationData":[TD([[makeQuery(id+"F0.imprint","IMPRINT",EDGE,{"disambiguationData":[TD([[subQ2,-1.0]])],"derivedFrom":subQ1}),-1.0]])]});}
            var Q15;
            {var subQ8=sQuery(id+"F0.wireOp",EDGE,"E143");var subQ11=sQuery(id+"F0.wireOp",EDGE,"E144");var subQ12=makeQuery(id+"F0.imprint","INTERSECT",VERTEX,{"derivedFrom":[subQ8,subQ11]});Q15=makeQuery(id+"F0.imprint","IMPRINT",FACE,{"disambiguationData":[TD([[makeQuery(id+"F0.imprint","IMPRINT",EDGE,{"disambiguationData":[TD([[subQ12,1.0]])],"derivedFrom":subQ8}),1.0]])]});}
            var Q16;
            {var subQ0=sQuery(id+"F0.wireOp",EDGE,"E856");var subQ1=sQuery(id+"F0.wireOp",EDGE,"E855");var subQ2=makeQuery(id+"F0.imprint","INTERSECT",VERTEX,{"derivedFrom":[subQ1,subQ0]});Q16=makeQuery(id+"F0.imprint","IMPRINT",FACE,{"disambiguationData":[TD([[makeQuery(id+"F0.imprint","IMPRINT",EDGE,{"disambiguationData":[TD([[subQ2,1.0]])],"derivedFrom":subQ1}),-1.0]])]});}
            var Q17;
            {var subQ0=sQuery(id+"F0.wireOp",EDGE,"E144");var subQ1=sQuery(id+"F0.wireOp",EDGE,"E143");var subQ2=makeQuery(id+"F0.imprint","INTERSECT",VERTEX,{"derivedFrom":[subQ1,subQ0]});Q17=makeQuery(id+"F0.imprint","IMPRINT",FACE,{"disambiguationData":[TD([[makeQuery(id+"F0.imprint","IMPRINT",EDGE,{"disambiguationData":[TD([[subQ2,1.0]])],"derivedFrom":subQ1}),-1.0]])]});}
            var Q18;
            Q18=makeQuery(id+"F0.imprint","IMPRINT",FACE,{"disambiguationData":[TD([[makeQuery(id+"F0.imprint","IMPRINT",EDGE,{"derivedFrom":sQuery(id+"F0.wireOp",EDGE,"E866")}),-1.0]])]});
            var Q19;
            {var subQ0=sQuery(id+"F0.wireOp",EDGE,"E924");Q19=makeQuery(id+"F0.imprint","IMPRINT",FACE,{"disambiguationData":[TD([[makeQuery(id+"F0.imprint","IMPRINT",EDGE,{"derivedFrom":subQ0}),-1.0]])]});}
            var Q20;
            Q20=makeQuery(id+"F0.imprint","IMPRINT",FACE,{"disambiguationData":[TD([[makeQuery(id+"F0.imprint","IMPRINT",EDGE,{"derivedFrom":sQuery(id+"F0.wireOp",EDGE,"E1031")}),-1.0]])]});
            var Q21;
            {var subQ18=sQuery(id+"F0.wireOp",EDGE,"E1051");Q21=makeQuery(id+"F0.imprint","IMPRINT",FACE,{"disambiguationData":[TD([[makeQuery(id+"F0.imprint","IMPRINT",EDGE,{"derivedFrom":subQ18}),-1.0]])]});}
            var Q22;
            {var subQ0=sQuery(id+"F0.wireOp",EDGE,"E1049");Q22=makeQuery(id+"F0.imprint","IMPRINT",FACE,{"disambiguationData":[TD([[makeQuery(id+"F0.imprint","IMPRINT",EDGE,{"derivedFrom":subQ0}),-1.0]])]});}
            var Q23;
            {var subQ0=sQuery(id+"F0.wireOp",EDGE,"E1056");Q23=makeQuery(id+"F0.imprint","IMPRINT",FACE,{"disambiguationData":[TD([[makeQuery(id+"F0.imprint","IMPRINT",EDGE,{"derivedFrom":subQ0}),-1.0]])]});}
            var Q24;
            Q24=makeQuery(id+"F0.imprint","IMPRINT",FACE,{"disambiguationData":[TD([[makeQuery(id+"F0.imprint","IMPRINT",EDGE,{"derivedFrom":sQuery(id+"F0.wireOp",EDGE,"E1161")}),-1.0]])]});
            var Q25;
            Q25=makeQuery(id+"F0.imprint","IMPRINT",FACE,{"disambiguationData":[TD([[makeQuery(id+"F0.imprint","IMPRINT",EDGE,{"derivedFrom":sQuery(id+"F0.wireOp",EDGE,"E1229")}),-1.0]])]});
            var Q26;
            {var subQ1=sQuery(id+"F0.wireOp",EDGE,"E145");var subQ5=sQuery(id+"F0.wireOp",EDGE,"E146");var subQ6=makeQuery(id+"F0.imprint","INTERSECT",VERTEX,{"derivedFrom":[subQ1,subQ5]});Q26=makeQuery(id+"F0.imprint","IMPRINT",FACE,{"disambiguationData":[TD([[makeQuery(id+"F0.imprint","IMPRINT",EDGE,{"disambiguationData":[TD([[subQ6,1.0]])],"derivedFrom":subQ1}),-1.0]])]});}
            var Q27;
            {var subQ5=sQuery(id+"F0.wireOp",EDGE,"E1262");Q27=makeQuery(id+"F0.imprint","IMPRINT",FACE,{"disambiguationData":[TD([[makeQuery(id+"F0.imprint","IMPRINT",EDGE,{"derivedFrom":subQ5}),-1.0]])]});}
            var Q28;
            {var subQ0=sQuery(id+"F0.wireOp",EDGE,"E1245");Q28=makeQuery(id+"F0.imprint","IMPRINT",FACE,{"disambiguationData":[TD([[makeQuery(id+"F0.imprint","IMPRINT",EDGE,{"derivedFrom":subQ0}),-1.0]])]});}
            var Q29;
            Q29=makeQuery(id+"F0.imprint","IMPRINT",FACE,{"disambiguationData":[TD([[makeQuery(id+"F0.imprint","IMPRINT",EDGE,{"derivedFrom":sQuery(id+"F0.wireOp",EDGE,"E1298")}),-1.0]])]});
            var Q30;
            Q30=makeQuery(id+"F0.imprint","IMPRINT",FACE,{"disambiguationData":[TD([[makeQuery(id+"F0.imprint","IMPRINT",EDGE,{"derivedFrom":sQuery(id+"F0.wireOp",EDGE,"E1346")}),-1.0]])]});
            var Q31;
            {var subQ0=sQuery(id+"F0.wireOp",EDGE,"E1336");var subQ1=sQuery(id+"F0.wireOp",EDGE,"E1335");var subQ2=makeQuery(id+"F0.imprint","INTERSECT",VERTEX,{"derivedFrom":[subQ1,subQ0]});Q31=makeQuery(id+"F0.imprint","IMPRINT",FACE,{"disambiguationData":[TD([[makeQuery(id+"F0.imprint","IMPRINT",EDGE,{"disambiguationData":[TD([[subQ2,1.0]])],"derivedFrom":subQ1}),-1.0]])]});}
            var Q32;
            {var subQ1=sQuery(id+"F0.wireOp",EDGE,"E1306");Q32=makeQuery(id+"F0.imprint","IMPRINT",FACE,{"disambiguationData":[TD([[makeQuery(id+"F0.imprint","IMPRINT",EDGE,{"derivedFrom":subQ1}),-1.0]])]});}
            var Q33;
            Q33=makeQuery(id+"F0.imprint","IMPRINT",FACE,{"disambiguationData":[TD([[makeQuery(id+"F0.imprint","IMPRINT",EDGE,{"derivedFrom":sQuery(id+"F0.wireOp",EDGE,"E1370")}),-1.0]])]});
            var Q34;
            {var subQ0=sQuery(id+"F0.wireOp",EDGE,"E1386");var subQ1=sQuery(id+"F0.wireOp",EDGE,"E1368");var subQ2=makeQuery(id+"F0.imprint","INTERSECT",VERTEX,{"derivedFrom":[subQ1,subQ0]});Q34=makeQuery(id+"F0.imprint","IMPRINT",FACE,{"disambiguationData":[TD([[makeQuery(id+"F0.imprint","IMPRINT",EDGE,{"disambiguationData":[TD([[subQ2,-1.0]])],"derivedFrom":subQ1}),-1.0]])]});}
            var Q35;
            {var subQ0=sQuery(id+"F0.wireOp",EDGE,"E1868");var subQ1=sQuery(id+"F0.wireOp",EDGE,"E381");var subQ2=makeQuery(id+"F0.imprint","INTERSECT",VERTEX,{"derivedFrom":[subQ1,subQ0]});Q35=makeQuery(id+"F0.imprint","IMPRINT",FACE,{"disambiguationData":[TD([[makeQuery(id+"F0.imprint","IMPRINT",EDGE,{"disambiguationData":[TD([[subQ2,-1.0]])],"derivedFrom":subQ1}),1.0]])]});}
            var Q36;
            {var subQ11=sQuery(id+"F0.wireOp",EDGE,"E1753");Q36=makeQuery(id+"F0.imprint","IMPRINT",FACE,{"disambiguationData":[TD([[makeQuery(id+"F0.imprint","IMPRINT",EDGE,{"derivedFrom":subQ11}),-1.0]])]});}
            var Q37;
            {var subQ12=sQuery(id+"F0.wireOp",EDGE,"E1750");Q37=makeQuery(id+"F0.imprint","IMPRINT",FACE,{"disambiguationData":[TD([[makeQuery(id+"F0.imprint","IMPRINT",EDGE,{"derivedFrom":subQ12}),-1.0]])]});}
            var Q38;
            {var subQ8=sQuery(id+"F0.wireOp",EDGE,"E7");Q38=makeQuery(id+"F0.imprint","IMPRINT",FACE,{"disambiguationData":[TD([[makeQuery(id+"F0.imprint","IMPRINT",EDGE,{"derivedFrom":subQ8}),-1.0]])]});}
            var Q39;
            {var subQ8=sQuery(id+"F0.wireOp",EDGE,"E7");Q39=makeQuery(id+"F0.imprint","IMPRINT",FACE,{"disambiguationData":[TD([[makeQuery(id+"F0.imprint","IMPRINT",EDGE,{"derivedFrom":subQ8}),1.0]])]});}
            var Q40;
            {var subQ1=sQuery(id+"F0.wireOp",EDGE,"E24");Q40=makeQuery(id+"F0.imprint","IMPRINT",FACE,{"disambiguationData":[TD([[makeQuery(id+"F0.imprint","IMPRINT",EDGE,{"derivedFrom":subQ1}),1.0]])]});}
            var Q41;
            {var subQ0=sQuery(id+"F0.wireOp",EDGE,"E14");var subQ1=sQuery(id+"F0.wireOp",EDGE,"E13");var subQ2=makeQuery(id+"F0.imprint","INTERSECT",VERTEX,{"derivedFrom":[subQ1,subQ0]});Q41=makeQuery(id+"F0.imprint","IMPRINT",FACE,{"disambiguationData":[TD([[makeQuery(id+"F0.imprint","IMPRINT",EDGE,{"disambiguationData":[TD([[subQ2,1.0]])],"derivedFrom":subQ1}),-1.0]])]});}
            var Q42;
            {var subQ6=sQuery(id+"F0.wireOp",EDGE,"E24");Q42=makeQuery(id+"F0.imprint","IMPRINT",FACE,{"disambiguationData":[TD([[makeQuery(id+"F0.imprint","IMPRINT",EDGE,{"derivedFrom":subQ6}),-1.0]])]});}
            var Q43;
            {var subQ0=sQuery(id+"F0.wireOp",EDGE,"E131");Q43=makeQuery(id+"F0.imprint","IMPRINT",FACE,{"disambiguationData":[TD([[makeQuery(id+"F0.imprint","IMPRINT",EDGE,{"derivedFrom":subQ0}),1.0]])]});}
            var Q44;
            {var subQ12=sQuery(id+"F0.wireOp",EDGE,"E103");Q44=makeQuery(id+"F0.imprint","IMPRINT",FACE,{"disambiguationData":[TD([[makeQuery(id+"F0.imprint","IMPRINT",EDGE,{"derivedFrom":subQ12}),1.0]])]});}
            var Q45;
            {var subQ7=sQuery(id+"F0.wireOp",EDGE,"E26");Q45=makeQuery(id+"F0.imprint","IMPRINT",FACE,{"disambiguationData":[TD([[makeQuery(id+"F0.imprint","IMPRINT",EDGE,{"derivedFrom":subQ7}),-1.0]])]});}
            var Q46;
            {var subQ9=sQuery(id+"F0.wireOp",EDGE,"E133");Q46=makeQuery(id+"F0.imprint","IMPRINT",FACE,{"disambiguationData":[TD([[makeQuery(id+"F0.imprint","IMPRINT",EDGE,{"derivedFrom":subQ9}),-1.0]])]});}
            var Q47;
            {var subQ1=sQuery(id+"F0.wireOp",EDGE,"E131");Q47=makeQuery(id+"F0.imprint","IMPRINT",FACE,{"disambiguationData":[TD([[makeQuery(id+"F0.imprint","IMPRINT",EDGE,{"derivedFrom":subQ1}),-1.0]])]});}
            var Q48;
            Q48=makeQuery(id+"F0.imprint","IMPRINT",FACE,{"disambiguationData":[TD([[makeQuery(id+"F0.imprint","IMPRINT",EDGE,{"derivedFrom":sQuery(id+"F0.wireOp",EDGE,"E391")}),1.0]])]});
            var Q49;
            {var subQ6=sQuery(id+"F0.wireOp",EDGE,"E417");Q49=makeQuery(id+"F0.imprint","IMPRINT",FACE,{"disambiguationData":[TD([[makeQuery(id+"F0.imprint","IMPRINT",EDGE,{"derivedFrom":subQ6}),1.0]])]});}
            var Q50;
            {var subQ0=sQuery(id+"F0.wireOp",EDGE,"E426");var subQ1=sQuery(id+"F0.wireOp",EDGE,"E193");var subQ2=makeQuery(id+"F0.imprint","INTERSECT",VERTEX,{"derivedFrom":[subQ1,subQ0]});Q50=makeQuery(id+"F0.imprint","IMPRINT",FACE,{"disambiguationData":[TD([[makeQuery(id+"F0.imprint","IMPRINT",EDGE,{"disambiguationData":[TD([[subQ2,-1.0]])],"derivedFrom":subQ1}),-1.0]])]});}
            var Q51;
            {var subQ11=sQuery(id+"F0.wireOp",EDGE,"E190");Q51=makeQuery(id+"F0.imprint","IMPRINT",FACE,{"disambiguationData":[TD([[makeQuery(id+"F0.imprint","IMPRINT",EDGE,{"derivedFrom":subQ11}),-1.0]])]});}
            var Q52;
            {var subQ6=sQuery(id+"F0.wireOp",EDGE,"E190");Q52=makeQuery(id+"F0.imprint","IMPRINT",FACE,{"disambiguationData":[TD([[makeQuery(id+"F0.imprint","IMPRINT",EDGE,{"derivedFrom":subQ6}),1.0]])]});}
            var Q53;
            {var subQ4=sQuery(id+"F0.wireOp",EDGE,"E419");Q53=makeQuery(id+"F0.imprint","IMPRINT",FACE,{"disambiguationData":[TD([[makeQuery(id+"F0.imprint","IMPRINT",EDGE,{"derivedFrom":subQ4}),1.0]])]});}
            var Q54;
            {var subQ4=sQuery(id+"F0.wireOp",EDGE,"E226");Q54=makeQuery(id+"F0.imprint","IMPRINT",FACE,{"disambiguationData":[TD([[makeQuery(id+"F0.imprint","IMPRINT",EDGE,{"derivedFrom":subQ4}),-1.0]])]});}
            var Q55;
            {var subQ0=sQuery(id+"F0.wireOp",EDGE,"E293");Q55=makeQuery(id+"F0.imprint","IMPRINT",FACE,{"disambiguationData":[TD([[makeQuery(id+"F0.imprint","IMPRINT",EDGE,{"derivedFrom":subQ0}),-1.0]])]});}
            var Q56;
            {var subQ4=sQuery(id+"F0.wireOp",EDGE,"E293");Q56=makeQuery(id+"F0.imprint","IMPRINT",FACE,{"disambiguationData":[TD([[makeQuery(id+"F0.imprint","IMPRINT",EDGE,{"derivedFrom":subQ4}),1.0]])]});}
            var Q57;
            Q57=makeQuery(id+"F0.imprint","IMPRINT",FACE,{"disambiguationData":[TD([[makeQuery(id+"F0.imprint","IMPRINT",EDGE,{"derivedFrom":sQuery(id+"F0.wireOp",EDGE,"E333")}),1.0]])]});
            var Q58;
            {var subQ1=sQuery(id+"F0.wireOp",EDGE,"E289");Q58=makeQuery(id+"F0.imprint","IMPRINT",FACE,{"disambiguationData":[TD([[makeQuery(id+"F0.imprint","IMPRINT",EDGE,{"derivedFrom":subQ1}),1.0]])]});}
            var Q59;
            {var subQ73=sQuery(id+"F0.wireOp",EDGE,"E17");Q59=makeQuery(id+"F0.imprint","IMPRINT",FACE,{"disambiguationData":[TD([[makeQuery(id+"F0.imprint","IMPRINT",EDGE,{"derivedFrom":subQ73}),-1.0]])]});}
            var Q60;
            {var subQ5=sQuery(id+"F0.wireOp",EDGE,"E1575");Q60=makeQuery(id+"F0.imprint","IMPRINT",FACE,{"disambiguationData":[TD([[makeQuery(id+"F0.imprint","IMPRINT",EDGE,{"derivedFrom":subQ5}),-1.0]])]});}
            var Q61;
            {var subQ3=sQuery(id+"F0.wireOp",EDGE,"E1574");var subQ9=sQuery(id+"F0.wireOp",EDGE,"E1573");var subQ10=makeQuery(id+"F0.imprint","INTERSECT",VERTEX,{"derivedFrom":[subQ9,subQ3]});Q61=makeQuery(id+"F0.imprint","IMPRINT",FACE,{"disambiguationData":[TD([[makeQuery(id+"F0.imprint","IMPRINT",EDGE,{"disambiguationData":[TD([[subQ10,1.0]])],"derivedFrom":subQ9}),-1.0]])]});}
            var Q62;
            {var subQ12=sQuery(id+"F0.wireOp",EDGE,"E61");Q62=makeQuery(id+"F0.imprint","IMPRINT",FACE,{"disambiguationData":[TD([[makeQuery(id+"F0.imprint","IMPRINT",EDGE,{"derivedFrom":subQ12}),-1.0]])]});}
            var Q63;
            {var subQ7=sQuery(id+"F0.wireOp",EDGE,"E55");Q63=makeQuery(id+"F0.imprint","IMPRINT",FACE,{"disambiguationData":[TD([[makeQuery(id+"F0.imprint","IMPRINT",EDGE,{"derivedFrom":subQ7}),1.0]])]});}
            var Q64;
            {var subQ8=sQuery(id+"F0.wireOp",EDGE,"E166");Q64=makeQuery(id+"F0.imprint","IMPRINT",FACE,{"disambiguationData":[TD([[makeQuery(id+"F0.imprint","IMPRINT",EDGE,{"derivedFrom":subQ8}),1.0]])]});}
            var Q65;
            {var subQ2=sQuery(id+"F0.wireOp",EDGE,"E1560");Q65=makeQuery(id+"F0.imprint","IMPRINT",FACE,{"disambiguationData":[TD([[makeQuery(id+"F0.imprint","IMPRINT",EDGE,{"derivedFrom":subQ2}),-1.0]])]});}
            var Q66;
            {var subQ5=sQuery(id+"F0.wireOp",EDGE,"E251");Q66=makeQuery(id+"F0.imprint","IMPRINT",FACE,{"disambiguationData":[TD([[makeQuery(id+"F0.imprint","IMPRINT",EDGE,{"derivedFrom":subQ5}),1.0]])]});}
            var Q67;
            {var subQ5=sQuery(id+"F0.wireOp",EDGE,"E201");Q67=makeQuery(id+"F0.imprint","IMPRINT",FACE,{"disambiguationData":[TD([[makeQuery(id+"F0.imprint","IMPRINT",EDGE,{"derivedFrom":subQ5}),1.0]])]});}
            var Q68;
            {var subQ8=sQuery(id+"F0.wireOp",EDGE,"E1539");Q68=makeQuery(id+"F0.imprint","IMPRINT",FACE,{"disambiguationData":[TD([[makeQuery(id+"F0.imprint","IMPRINT",EDGE,{"derivedFrom":subQ8}),-1.0]])]});}
            var Q69;
            {var subQ0=sQuery(id+"F0.wireOp",EDGE,"E113");Q69=makeQuery(id+"F0.imprint","IMPRINT",FACE,{"disambiguationData":[TD([[makeQuery(id+"F0.imprint","IMPRINT",EDGE,{"derivedFrom":subQ0}),1.0]])]});}
            var Q70;
            {var subQ5=sQuery(id+"F0.wireOp",EDGE,"E17");Q70=makeQuery(id+"F0.imprint","IMPRINT",FACE,{"disambiguationData":[TD([[makeQuery(id+"F0.imprint","IMPRINT",EDGE,{"derivedFrom":subQ5}),1.0]])]});}
            var Q71;
            {var subQ3=sQuery(id+"F0.wireOp",EDGE,"E15");var subQ6=sQuery(id+"F0.wireOp",EDGE,"E16");var subQ9=makeQuery(id+"F0.imprint","INTERSECT",VERTEX,{"derivedFrom":[subQ3,subQ6]});Q71=makeQuery(id+"F0.imprint","IMPRINT",FACE,{"disambiguationData":[TD([[makeQuery(id+"F0.imprint","IMPRINT",EDGE,{"disambiguationData":[TD([[subQ9,1.0]])],"derivedFrom":subQ3}),1.0]])]});}
            var Q72;
            {var subQ5=sQuery(id+"F0.wireOp",EDGE,"E16");var subQ6=sQuery(id+"F0.wireOp",EDGE,"E15");var subQ7=makeQuery(id+"F0.imprint","INTERSECT",VERTEX,{"derivedFrom":[subQ6,subQ5]});Q72=makeQuery(id+"F0.imprint","IMPRINT",FACE,{"disambiguationData":[TD([[makeQuery(id+"F0.imprint","IMPRINT",EDGE,{"disambiguationData":[TD([[subQ7,1.0]])],"derivedFrom":subQ6}),-1.0]])]});}
            var Q73;
            {var subQ5=sQuery(id+"F0.wireOp",EDGE,"E1941");var subQ6=sQuery(id+"F0.wireOp",EDGE,"E325");var subQ7=makeQuery(id+"F0.imprint","INTERSECT",VERTEX,{"derivedFrom":[subQ6,subQ5]});Q73=makeQuery(id+"F0.imprint","IMPRINT",FACE,{"disambiguationData":[TD([[makeQuery(id+"F0.imprint","IMPRINT",EDGE,{"disambiguationData":[TD([[subQ7,-1.0]])],"derivedFrom":subQ6}),1.0]])]});}
            var Q74;
            {var subQ0=sQuery(id+"F0.wireOp",EDGE,"E1942");Q74=makeQuery(id+"F0.imprint","IMPRINT",FACE,{"disambiguationData":[TD([[makeQuery(id+"F0.imprint","IMPRINT",EDGE,{"derivedFrom":subQ0}),1.0]])]});}
            var Q75;
            {var subQ5=sQuery(id+"F0.wireOp",EDGE,"E1942");Q75=makeQuery(id+"F0.imprint","IMPRINT",FACE,{"disambiguationData":[TD([[makeQuery(id+"F0.imprint","IMPRINT",EDGE,{"derivedFrom":subQ5}),-1.0]])]});}
            var Q76;
            {var subQ3=sQuery(id+"F0.wireOp",EDGE,"E384");var subQ7=sQuery(id+"F0.wireOp",EDGE,"E1941");var subQ9=makeQuery(id+"F0.imprint","INTERSECT",VERTEX,{"derivedFrom":[subQ3,subQ7]});Q76=makeQuery(id+"F0.imprint","IMPRINT",FACE,{"disambiguationData":[TD([[makeQuery(id+"F0.imprint","IMPRINT",EDGE,{"disambiguationData":[TD([[subQ9,-1.0]])],"derivedFrom":subQ3}),-1.0]])]});}
            var Q77;
            {var subQ0=sQuery(id+"F0.wireOp",EDGE,"E384");var subQ1=sQuery(id+"F0.wireOp",EDGE,"E325");var subQ2=makeQuery(id+"F0.imprint","INTERSECT",VERTEX,{"derivedFrom":[subQ1,subQ0]});Q77=makeQuery(id+"F0.imprint","IMPRINT",FACE,{"disambiguationData":[TD([[makeQuery(id+"F0.imprint","IMPRINT",EDGE,{"disambiguationData":[TD([[subQ2,-1.0]])],"derivedFrom":subQ1}),1.0]])]});}
            var Q78;
            {var subQ3=sQuery(id+"F0.wireOp",EDGE,"E325");var subQ5=sQuery(id+"F0.wireOp",EDGE,"E384");var subQ6=makeQuery(id+"F0.imprint","INTERSECT",VERTEX,{"derivedFrom":[subQ3,subQ5]});Q78=makeQuery(id+"F0.imprint","IMPRINT",FACE,{"disambiguationData":[TD([[makeQuery(id+"F0.imprint","IMPRINT",EDGE,{"disambiguationData":[TD([[subQ6,-1.0]])],"derivedFrom":subQ3}),-1.0]])]});}
            var Q79;
            {var subQ0=sQuery(id+"F0.wireOp",EDGE,"E1525");Q79=makeQuery(id+"F0.imprint","IMPRINT",FACE,{"disambiguationData":[TD([[makeQuery(id+"F0.imprint","IMPRINT",EDGE,{"derivedFrom":subQ0}),-1.0]])]});}
            var Q80;
            {var subQ0=sQuery(id+"F0.wireOp",EDGE,"E1941");var subQ1=sQuery(id+"F0.wireOp",EDGE,"E384");var subQ2=makeQuery(id+"F0.imprint","INTERSECT",VERTEX,{"derivedFrom":[subQ1,subQ0]});Q80=makeQuery(id+"F0.imprint","IMPRINT",FACE,{"disambiguationData":[TD([[makeQuery(id+"F0.imprint","IMPRINT",EDGE,{"disambiguationData":[TD([[subQ2,-1.0]])],"derivedFrom":subQ1}),1.0]])]});}
            var Q81;
            {var subQ17=sQuery(id+"F0.wireOp",EDGE,"E1875");Q81=makeQuery(id+"F0.imprint","IMPRINT",FACE,{"disambiguationData":[TD([[makeQuery(id+"F0.imprint","IMPRINT",EDGE,{"derivedFrom":subQ17}),-1.0]])]});}
            var Q82;
            {var subQ0=sQuery(id+"F0.wireOp",EDGE,"E427");var subQ1=sQuery(id+"F0.wireOp",EDGE,"E325");var subQ2=makeQuery(id+"F0.imprint","INTERSECT",VERTEX,{"derivedFrom":[subQ1,subQ0]});Q82=makeQuery(id+"F0.imprint","IMPRINT",FACE,{"disambiguationData":[TD([[makeQuery(id+"F0.imprint","IMPRINT",EDGE,{"disambiguationData":[TD([[subQ2,-1.0]])],"derivedFrom":subQ1}),1.0]])]});}
            var Q83;
            {var subQ1=sQuery(id+"F0.wireOp",EDGE,"E1469");Q83=makeQuery(id+"F0.imprint","IMPRINT",FACE,{"disambiguationData":[TD([[makeQuery(id+"F0.imprint","IMPRINT",EDGE,{"derivedFrom":subQ1}),-1.0]])]});}
            var Q84;
            {var subQ0=sQuery(id+"F0.wireOp",EDGE,"E1875");Q84=makeQuery(id+"F0.imprint","IMPRINT",FACE,{"disambiguationData":[TD([[makeQuery(id+"F0.imprint","IMPRINT",EDGE,{"derivedFrom":subQ0}),1.0]])]});}
            var Q85;
            {var subQ16=sQuery(id+"F0.wireOp",EDGE,"E1522");Q85=makeQuery(id+"F0.imprint","IMPRINT",FACE,{"disambiguationData":[TD([[makeQuery(id+"F0.imprint","IMPRINT",EDGE,{"derivedFrom":subQ16}),-1.0]])]});}
            var Q86;
            {var subQ12=sQuery(id+"F0.wireOp",EDGE,"E1872");Q86=makeQuery(id+"F0.imprint","IMPRINT",FACE,{"disambiguationData":[TD([[makeQuery(id+"F0.imprint","IMPRINT",EDGE,{"derivedFrom":subQ12}),-1.0]])]});}
            var Q87;
            {var subQ0=sQuery(id+"F0.wireOp",EDGE,"E381");var subQ1=sQuery(id+"F0.wireOp",EDGE,"E322");var subQ2=makeQuery(id+"F0.imprint","INTERSECT",VERTEX,{"derivedFrom":[subQ1,subQ0]});Q87=makeQuery(id+"F0.imprint","IMPRINT",FACE,{"disambiguationData":[TD([[makeQuery(id+"F0.imprint","IMPRINT",EDGE,{"disambiguationData":[TD([[subQ2,-1.0]])],"derivedFrom":subQ1}),-1.0]])]});}
            var Q88;
            {var subQ3=sQuery(id+"F0.wireOp",EDGE,"E321");var subQ5=sQuery(id+"F0.wireOp",EDGE,"E322");var subQ6=makeQuery(id+"F0.imprint","INTERSECT",VERTEX,{"derivedFrom":[subQ3,subQ5]});Q88=makeQuery(id+"F0.imprint","IMPRINT",FACE,{"disambiguationData":[TD([[makeQuery(id+"F0.imprint","IMPRINT",EDGE,{"disambiguationData":[TD([[subQ6,1.0]])],"derivedFrom":subQ3}),1.0]])]});}
            var Q89;
            {var subQ0=sQuery(id+"F0.wireOp",EDGE,"E323");var subQ1=sQuery(id+"F0.wireOp",EDGE,"E322");var subQ2=makeQuery(id+"F0.imprint","INTERSECT",VERTEX,{"derivedFrom":[subQ1,subQ0]});Q89=makeQuery(id+"F0.imprint","IMPRINT",FACE,{"disambiguationData":[TD([[makeQuery(id+"F0.imprint","IMPRINT",EDGE,{"disambiguationData":[TD([[subQ2,1.0]])],"derivedFrom":subQ1}),1.0]])]});}
            var Q90;
            {var subQ5=sQuery(id+"F0.wireOp",EDGE,"E1911");Q90=makeQuery(id+"F0.imprint","IMPRINT",FACE,{"disambiguationData":[TD([[makeQuery(id+"F0.imprint","IMPRINT",EDGE,{"derivedFrom":subQ5}),-1.0]])]});}
            var Q91;
            {var subQ0=sQuery(id+"F0.wireOp",EDGE,"E1404");var subQ1=sQuery(id+"F0.wireOp",EDGE,"E1403");var subQ2=makeQuery(id+"F0.imprint","INTERSECT",VERTEX,{"derivedFrom":[subQ1,subQ0]});Q91=makeQuery(id+"F0.imprint","IMPRINT",FACE,{"disambiguationData":[TD([[makeQuery(id+"F0.imprint","IMPRINT",EDGE,{"disambiguationData":[TD([[subQ2,1.0]])],"derivedFrom":subQ1}),-1.0]])]});}
            var Q92;
            {var subQ5=sQuery(id+"F0.wireOp",EDGE,"E695");Q92=makeQuery(id+"F0.imprint","IMPRINT",FACE,{"disambiguationData":[TD([[makeQuery(id+"F0.imprint","IMPRINT",EDGE,{"derivedFrom":subQ5}),-1.0]])]});}
            var Q93;
            {var subQ0=sQuery(id+"F0.wireOp",EDGE,"E486");var subQ1=sQuery(id+"F0.wireOp",EDGE,"E71");var subQ2=makeQuery(id+"F0.imprint","INTERSECT",VERTEX,{"derivedFrom":[subQ1,subQ0]});Q93=makeQuery(id+"F0.imprint","IMPRINT",FACE,{"disambiguationData":[TD([[makeQuery(id+"F0.imprint","IMPRINT",EDGE,{"disambiguationData":[TD([[subQ2,-1.0]])],"derivedFrom":subQ1}),1.0]])]});}
            extrude(context, id + "F2", {"entities" : qUnion([Q0, Q1, Q2, Q3, Q4, Q5, Q6, Q7, Q8, Q9, Q10, Q11, Q12, Q13, Q14, Q15, Q16, Q17, Q18, Q19, Q20, Q21, Q22, Q23, Q24, Q25, Q26, Q27, Q28, Q29, Q30, Q31, Q32, Q33, Q34, Q35, Q36, Q37, Q38, Q39, Q40, Q41, Q42, Q43, Q44, Q45, Q46, Q47, Q48, Q49, Q50, Q51, Q52, Q53, Q54, Q55, Q56, Q57, Q58, Q59, Q60, Q61, Q62, Q63, Q64, Q65, Q66, Q67, Q68, Q69, Q70, Q71, Q72, Q73, Q74, Q75, Q76, Q77, Q78, Q79, Q80, Q81, Q82, Q83, Q84, Q85, Q86, Q87, Q88, Q89, Q90, Q91, Q92, Q93]), "operationType" : NewBodyOperationType.ADD, "depth" : 1 * mm, "offsetDistance" : 25 * mm});
        }
        {
            var Q0;
            {var subQ5=sQuery(id+"F0.wireOp",EDGE,"E230");Q0=makeQuery(id+"F0.imprint","IMPRINT",FACE,{"disambiguationData":[TD([[makeQuery(id+"F0.imprint","IMPRINT",EDGE,{"derivedFrom":subQ5}),-1.0]])]});}
            var Q1;
            {var subQ11=sQuery(id+"F0.wireOp",EDGE,"E214");Q1=makeQuery(id+"F0.imprint","IMPRINT",FACE,{"disambiguationData":[TD([[makeQuery(id+"F0.imprint","IMPRINT",EDGE,{"derivedFrom":subQ11}),-1.0]])]});}
            var Q2;
            Q2=makeQuery(id+"F0.imprint","IMPRINT",FACE,{"disambiguationData":[TD([[makeQuery(id+"F0.imprint","IMPRINT",EDGE,{"derivedFrom":sQuery(id+"F0.wireOp",EDGE,"E174")}),-1.0]])]});
            var Q3;
            {var subQ11=sQuery(id+"F0.wireOp",EDGE,"E195");Q3=makeQuery(id+"F0.imprint","IMPRINT",FACE,{"disambiguationData":[TD([[makeQuery(id+"F0.imprint","IMPRINT",EDGE,{"derivedFrom":subQ11}),-1.0]])]});}
            var Q4;
            {var subQ16=sQuery(id+"F0.wireOp",EDGE,"E149");Q4=makeQuery(id+"F0.imprint","IMPRINT",FACE,{"disambiguationData":[TD([[makeQuery(id+"F0.imprint","IMPRINT",EDGE,{"derivedFrom":subQ16}),-1.0]])]});}
            var Q5;
            {var subQ14=sQuery(id+"F0.wireOp",EDGE,"E127");Q5=makeQuery(id+"F0.imprint","IMPRINT",FACE,{"disambiguationData":[TD([[makeQuery(id+"F0.imprint","IMPRINT",EDGE,{"derivedFrom":subQ14}),-1.0]])]});}
            var Q6;
            {var subQ0=sQuery(id+"F0.wireOp",EDGE,"E1117");Q6=makeQuery(id+"F0.imprint","IMPRINT",FACE,{"disambiguationData":[TD([[makeQuery(id+"F0.imprint","IMPRINT",EDGE,{"derivedFrom":subQ0}),1.0]])]});}
            var Q7;
            {var subQ31=sQuery(id+"F0.wireOp",EDGE,"E985");Q7=makeQuery(id+"F0.imprint","IMPRINT",FACE,{"disambiguationData":[TD([[makeQuery(id+"F0.imprint","IMPRINT",EDGE,{"derivedFrom":subQ31}),1.0]])]});}
            var Q8;
            {var subQ5=sQuery(id+"F0.wireOp",EDGE,"E1289");var subQ6=sQuery(id+"F0.wireOp",EDGE,"E146");var subQ7=makeQuery(id+"F0.imprint","INTERSECT",VERTEX,{"derivedFrom":[subQ6,subQ5]});Q8=makeQuery(id+"F0.imprint","IMPRINT",FACE,{"disambiguationData":[TD([[makeQuery(id+"F0.imprint","IMPRINT",EDGE,{"disambiguationData":[TD([[subQ7,-1.0]])],"derivedFrom":subQ6}),-1.0]])]});}
            var Q9;
            {var subQ8=sQuery(id+"F0.wireOp",EDGE,"E40");Q9=makeQuery(id+"F0.imprint","IMPRINT",FACE,{"disambiguationData":[TD([[makeQuery(id+"F0.imprint","IMPRINT",EDGE,{"derivedFrom":subQ8}),-1.0]])]});}
            var Q10;
            {var subQ0=sQuery(id+"F0.wireOp",EDGE,"E823");var subQ1=sQuery(id+"F0.wireOp",EDGE,"E38");var subQ2=makeQuery(id+"F0.imprint","INTERSECT",VERTEX,{"derivedFrom":[subQ1,subQ0]});Q10=makeQuery(id+"F0.imprint","IMPRINT",FACE,{"disambiguationData":[TD([[makeQuery(id+"F0.imprint","IMPRINT",EDGE,{"disambiguationData":[TD([[subQ2,-1.0]])],"derivedFrom":subQ1}),-1.0]])]});}
            var Q11;
            {var subQ10=sQuery(id+"F0.wireOp",EDGE,"E32");Q11=makeQuery(id+"F0.imprint","IMPRINT",FACE,{"disambiguationData":[TD([[makeQuery(id+"F0.imprint","IMPRINT",EDGE,{"derivedFrom":subQ10}),-1.0]])]});}
            var Q12;
            {var subQ1=sQuery(id+"F0.wireOp",EDGE,"E110");Q12=makeQuery(id+"F0.imprint","IMPRINT",FACE,{"disambiguationData":[TD([[makeQuery(id+"F0.imprint","IMPRINT",EDGE,{"derivedFrom":subQ1}),-1.0]])]});}
            var Q13;
            Q13=makeQuery(id+"F0.imprint","IMPRINT",FACE,{"disambiguationData":[TD([[makeQuery(id+"F0.imprint","IMPRINT",EDGE,{"derivedFrom":sQuery(id+"F0.wireOp",EDGE,"E0")}),-1.0]])]});
            var Q14;
            {var subQ5=sQuery(id+"F0.wireOp",EDGE,"E491");Q14=makeQuery(id+"F0.imprint","IMPRINT",FACE,{"disambiguationData":[TD([[makeQuery(id+"F0.imprint","IMPRINT",EDGE,{"derivedFrom":subQ5}),1.0]])]});}
            var Q15;
            {var subQ5=sQuery(id+"F0.wireOp",EDGE,"E509");Q15=makeQuery(id+"F0.imprint","IMPRINT",FACE,{"disambiguationData":[TD([[makeQuery(id+"F0.imprint","IMPRINT",EDGE,{"derivedFrom":subQ5}),1.0]])]});}
            var Q16;
            {var subQ16=sQuery(id+"F0.wireOp",EDGE,"E64");Q16=makeQuery(id+"F0.imprint","IMPRINT",FACE,{"disambiguationData":[TD([[makeQuery(id+"F0.imprint","IMPRINT",EDGE,{"derivedFrom":subQ16}),-1.0]])]});}
            var Q17;
            {var subQ6=sQuery(id+"F0.wireOp",EDGE,"E1695");Q17=makeQuery(id+"F0.imprint","IMPRINT",FACE,{"disambiguationData":[TD([[makeQuery(id+"F0.imprint","IMPRINT",EDGE,{"derivedFrom":subQ6}),-1.0]])]});}
            extrude(context, id + "F3", {"entities" : qUnion([Q0, Q1, Q2, Q3, Q4, Q5, Q6, Q7, Q8, Q9, Q10, Q11, Q12, Q13, Q14, Q15, Q16, Q17]), "operationType" : NewBodyOperationType.ADD, "depth" : 0.2 * mm, "offsetDistance" : 25 * mm});
        }
    });
